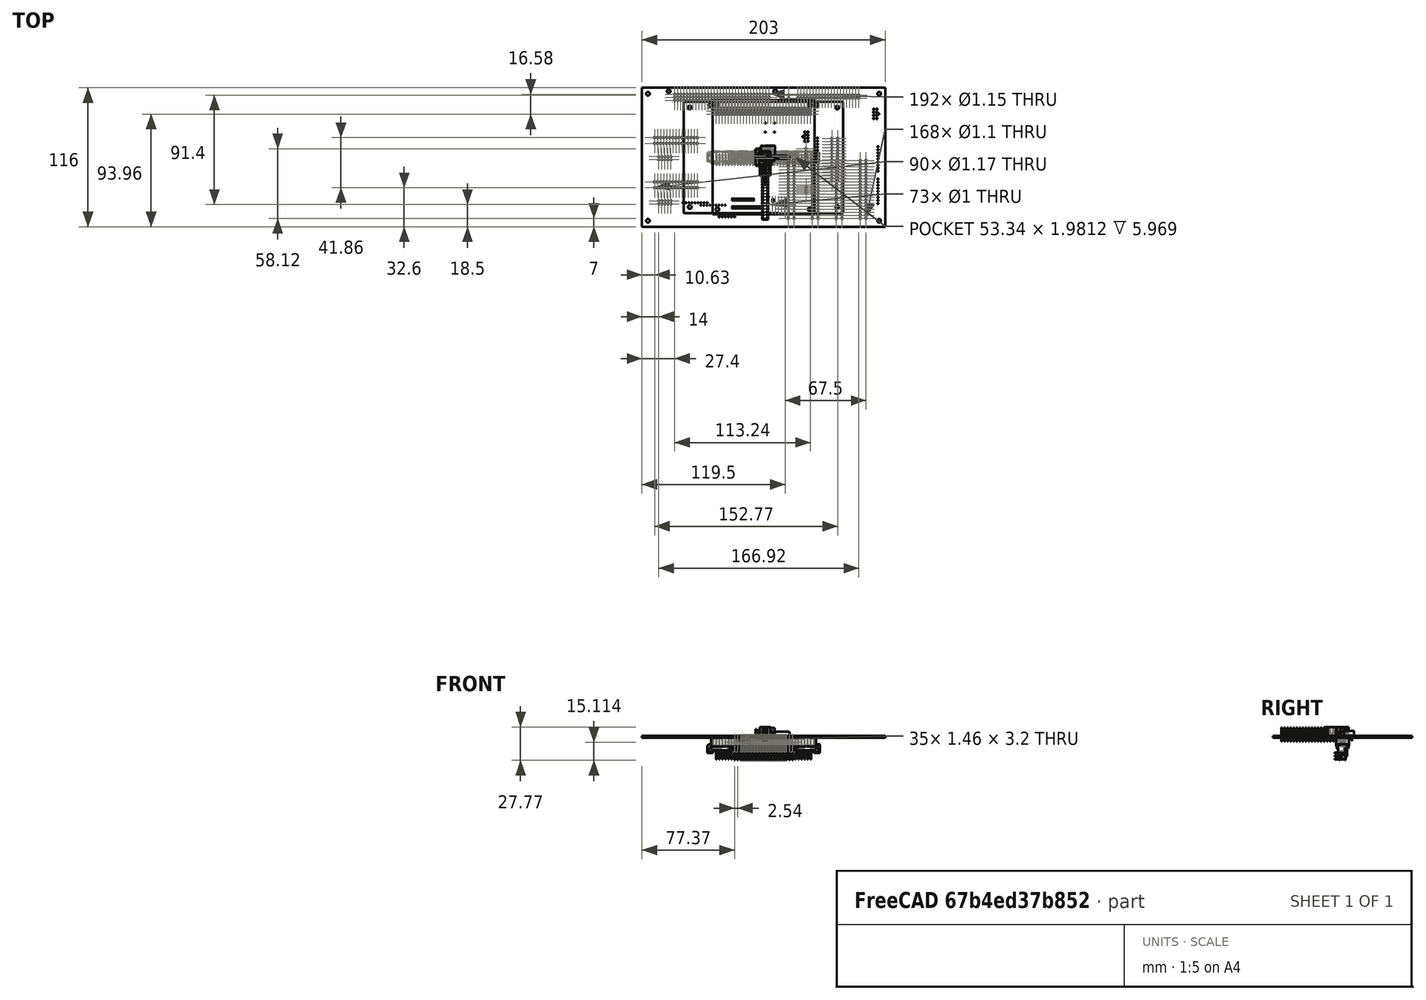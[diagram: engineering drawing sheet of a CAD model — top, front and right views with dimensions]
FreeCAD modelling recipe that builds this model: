
FCSTD DOCUMENT  (FreeCAD 2022.1112R26244 +5306 (Git))
Label: GComputerCaseAssembly
License: All rights reserved
objects: App::Link×216, App::FeaturePython×89, Part::FeaturePython×61, Part::Feature×46, App::LinkGroup×46, PartDesign::CoordinateSystem×1
note: 107 computed .brp shape members not serialized (recipe doc carries the construction recipe); baked Part::Feature solids carry a one-line shape summary decoded from their .brp
EXTERNAL_REF file=FirstPartPeripherals.FCStd obj=Part
EXTERNAL_REF file=SecondPartPeripherals.FCStd obj=Part
EXTERNAL_REF file=FirstPartProcessor.FCStd obj=Part
EXTERNAL_REF file=SecondPartProcessor.FCStd obj=Part
EXTERNAL_REF file=FirstPartPeripheralsTop.FCStd obj=Part
EXTERNAL_REF file=SecondPartPeripheralsTop.FCStd obj=Part
EXTERNAL_REF file=SecondPartProcessorTop.FCStd obj=Part
EXTERNAL_REF file=FirstPartProcessorTop.FCStd obj=Part

FEATURE [PartDesign::CoordinateSystem] Local_CS
  AttacherType = Attacher::AttachEngine3D
  TreeRank = 1
FEATURE [App::Link] Link  label="FirstPartPeripherals"
  AutoLinkLabel = false
  AutoPlacement = true
  LinkPlacement = pos=(65.4549,-31.7473,55.1601) rot=(0,0,1;0rad)
  LinkedObject = -> <external FirstPartPeripherals.FCStd>#Part
  Placement = pos=(65.4549,-31.7473,55.1601) rot=(0,0,1;0rad)
  SyncGroupVisibility = false
  TreeRank = 2
  _LinkOwner = 312
  _LinkVersion = 1
FEATURE [App::Link] Link001  label="SecondPartPeripherals"
  AutoLinkLabel = false
  AutoPlacement = true
  LinkPlacement = pos=(-74.5451,-31.7473,55.1601) rot=(0,0,1;0rad)
  LinkedObject = -> <external SecondPartPeripherals.FCStd>#Part
  Placement = pos=(-74.5451,-31.7473,55.1601) rot=(0,0,1;0rad)
  SyncGroupVisibility = false
  TreeRank = 3
  _LinkOwner = 312
  _LinkVersion = 1
FEATURE [App::Link] Link002  label="FirstPartProcessor"
  AutoLinkLabel = false
  AutoPlacement = true
  LinkPlacement = pos=(65.4549,91.6527,55.1601) rot=(0,0,1;0rad)
  LinkedObject = -> <external FirstPartProcessor.FCStd>#Part
  Placement = pos=(65.4549,91.6527,55.1601) rot=(0,0,1;0rad)
  SyncGroupVisibility = false
  TreeRank = 24
  _LinkOwner = 312
  _LinkVersion = 1
FEATURE [App::Link] Link003  label="SecondPartProcessor"
  AutoLinkLabel = false
  AutoPlacement = true
  LinkPlacement = pos=(-74.5451,91.6527,55.1601) rot=(0,0,1;0rad)
  LinkedObject = -> <external SecondPartProcessor.FCStd>#Part
  Placement = pos=(-74.5451,91.6527,55.1601) rot=(0,0,1;0rad)
  SyncGroupVisibility = false
  TreeRank = 39
  _LinkOwner = 312
  _LinkVersion = 1
FEATURE [Part::Feature] Solid  label="SOLID"
  TreeRank = 58
  shape: bbox 44.7 x 9.347 x 18.67 mm, 388 faces (baked)
FEATURE [App::LinkGroup] LinkGroup  label="5530843-2"
  ElementList = -> [Solid]
  LinkMode = 0
  Placement = pos=(59.5,-2.1,17.15) rot=(0,0,1;1.5708rad)
  TreeRank = 59
  _LinkVersion = 1
FEATURE [Part::Feature] Solid001  label="SOLID001"
  TreeRank = 60
  shape: bbox 93.85 x 12.08 x 18.02 mm, 1560 faces (baked)
FEATURE [App::LinkGroup] LinkGroup001  label="5650473-5"
  ElementList = -> [Solid001]
  LinkMode = 0
  Placement = pos=(-0.25,53.75,5.65) rot=(0,0.707107,0.707107;3.14159rad)
  TreeRank = 61
  _LinkVersion = 1
FEATURE [Part::Feature] Solid002  label="SOLID002"
  TreeRank = 121
  shape: bbox 2 x 1.25 x 1.25 mm, 28 faces (baked)
FEATURE [App::LinkGroup] LinkGroup002  label="C_0805_2012Metric"
  ElementList = -> [Solid002]
  LinkMode = 0
  Placement = pos=(8.5,11,-0.05) rot=(0,1,0;3.14159rad)
  TreeRank = 122
  _LinkVersion = 1
FEATURE [App::Link] Link004  label="C_0805_2012Metric001"
  AutoLinkLabel = true
  AutoPlacement = true
  LinkPlacement = pos=(20.5,11,-0.05) rot=(0,1,0;3.14159rad)
  LinkedObject = -> LinkGroup002
  Placement = pos=(20.5,11,-0.05) rot=(0,1,0;3.14159rad)
  SyncGroupVisibility = false
  TreeRank = 123
  _LinkVersion = 1
FEATURE [App::Link] Link005  label="C_0805_2012Metric002"
  AutoLinkLabel = true
  AutoPlacement = true
  LinkPlacement = pos=(32.5,11,-0.05) rot=(0,1,0;3.14159rad)
  LinkedObject = -> LinkGroup002
  Placement = pos=(32.5,11,-0.05) rot=(0,1,0;3.14159rad)
  SyncGroupVisibility = false
  TreeRank = 124
  _LinkVersion = 1
FEATURE [App::Link] Link006  label="C_0805_2012Metric003"
  AutoLinkLabel = true
  AutoPlacement = true
  LinkPlacement = pos=(-45.25,9.25,-0.05) rot=(1,0,0;3.14159rad)
  LinkedObject = -> LinkGroup002
  Placement = pos=(-45.25,9.25,-0.05) rot=(1,0,0;3.14159rad)
  SyncGroupVisibility = false
  TreeRank = 125
  _LinkVersion = 1
FEATURE [App::Link] Link007  label="C_0805_2012Metric004"
  AutoLinkLabel = true
  AutoPlacement = true
  LinkPlacement = pos=(-32.75,-4,-0.05) rot=(0,1,0;3.14159rad)
  LinkedObject = -> LinkGroup002
  Placement = pos=(-32.75,-4,-0.05) rot=(0,1,0;3.14159rad)
  SyncGroupVisibility = false
  TreeRank = 126
  _LinkVersion = 1
FEATURE [App::Link] Link008  label="C_0805_2012Metric005"
  AutoLinkLabel = true
  AutoPlacement = true
  LinkPlacement = pos=(-21.25,-4,-0.05) rot=(0,1,0;3.14159rad)
  LinkedObject = -> LinkGroup002
  Placement = pos=(-21.25,-4,-0.05) rot=(0,1,0;3.14159rad)
  SyncGroupVisibility = false
  TreeRank = 127
  _LinkVersion = 1
FEATURE [App::Link] Link009  label="C_0805_2012Metric006"
  AutoLinkLabel = true
  AutoPlacement = true
  LinkPlacement = pos=(-2,-7.5,1.65) rot=(0,0,1;3.14159rad)
  LinkedObject = -> LinkGroup002
  Placement = pos=(-2,-7.5,1.65) rot=(0,0,1;3.14159rad)
  SyncGroupVisibility = false
  TreeRank = 128
  _LinkVersion = 1
FEATURE [App::Link] Link010  label="C_0805_2012Metric007"
  AutoLinkLabel = true
  AutoPlacement = true
  LinkPlacement = pos=(-32.75,12.25,-0.05) rot=(0,1,0;3.14159rad)
  LinkedObject = -> LinkGroup002
  Placement = pos=(-32.75,12.25,-0.05) rot=(0,1,0;3.14159rad)
  SyncGroupVisibility = false
  TreeRank = 129
  _LinkVersion = 1
FEATURE [App::Link] Link011  label="C_0805_2012Metric008"
  AutoLinkLabel = true
  AutoPlacement = true
  LinkPlacement = pos=(25.5,-17.5,1.65) rot=(0,0,1;0rad)
  LinkedObject = -> LinkGroup002
  Placement = pos=(25.5,-17.5,1.65) rot=(0,0,1;0rad)
  SyncGroupVisibility = false
  TreeRank = 130
  _LinkVersion = 1
FEATURE [App::Link] Link012  label="C_0805_2012Metric009"
  AutoLinkLabel = true
  AutoPlacement = true
  LinkPlacement = pos=(-21.25,12.25,-0.05) rot=(0,1,0;3.14159rad)
  LinkedObject = -> LinkGroup002
  Placement = pos=(-21.25,12.25,-0.05) rot=(0,1,0;3.14159rad)
  SyncGroupVisibility = false
  TreeRank = 131
  _LinkVersion = 1
FEATURE [App::Link] Link013  label="C_0805_2012Metric010"
  AutoLinkLabel = true
  AutoPlacement = true
  LinkPlacement = pos=(-10,13.5,-0.05) rot=(0,1,0;3.14159rad)
  LinkedObject = -> LinkGroup002
  Placement = pos=(-10,13.5,-0.05) rot=(0,1,0;3.14159rad)
  SyncGroupVisibility = false
  TreeRank = 132
  _LinkVersion = 1
FEATURE [App::Link] Link014  label="C_0805_2012Metric011"
  AutoLinkLabel = true
  AutoPlacement = true
  LinkPlacement = pos=(-44.25,4.5,-0.05) rot=(-0.707107,0.707107,0;3.14159rad)
  LinkedObject = -> LinkGroup002
  Placement = pos=(-44.25,4.5,-0.05) rot=(-0.707107,0.707107,0;3.14159rad)
  SyncGroupVisibility = false
  TreeRank = 133
  _LinkVersion = 1
FEATURE [App::Link] Link015  label="C_0805_2012Metric012"
  AutoLinkLabel = true
  AutoPlacement = true
  LinkPlacement = pos=(-10,-3,-0.05) rot=(0,1,0;3.14159rad)
  LinkedObject = -> LinkGroup002
  Placement = pos=(-10,-3,-0.05) rot=(0,1,0;3.14159rad)
  SyncGroupVisibility = false
  TreeRank = 134
  _LinkVersion = 1
FEATURE [App::Link] Link016  label="C_0805_2012Metric013"
  AutoLinkLabel = true
  AutoPlacement = true
  LinkPlacement = pos=(-10.75,-13.5,-0.05) rot=(1,0,0;3.14159rad)
  LinkedObject = -> LinkGroup002
  Placement = pos=(-10.75,-13.5,-0.05) rot=(1,0,0;3.14159rad)
  SyncGroupVisibility = false
  TreeRank = 135
  _LinkVersion = 1
FEATURE [App::Link] Link017  label="C_0805_2012Metric014"
  AutoLinkLabel = true
  AutoPlacement = true
  LinkPlacement = pos=(-49,-12.25,1.65) rot=(0,0,1;3.14159rad)
  LinkedObject = -> LinkGroup002
  Placement = pos=(-49,-12.25,1.65) rot=(0,0,1;3.14159rad)
  SyncGroupVisibility = false
  TreeRank = 136
  _LinkVersion = 1
FEATURE [App::Link] Link018  label="C_0805_2012Metric015"
  AutoLinkLabel = true
  AutoPlacement = true
  LinkPlacement = pos=(-19,-27.75,-0.05) rot=(0,1,0;3.14159rad)
  LinkedObject = -> LinkGroup002
  Placement = pos=(-19,-27.75,-0.05) rot=(0,1,0;3.14159rad)
  SyncGroupVisibility = false
  TreeRank = 137
  _LinkVersion = 1
FEATURE [App::Link] Link019  label="C_0805_2012Metric016"
  AutoLinkLabel = true
  AutoPlacement = true
  LinkPlacement = pos=(-39.25,-27.75,-0.05) rot=(0,1,0;3.14159rad)
  LinkedObject = -> LinkGroup002
  Placement = pos=(-39.25,-27.75,-0.05) rot=(0,1,0;3.14159rad)
  SyncGroupVisibility = false
  TreeRank = 138
  _LinkVersion = 1
FEATURE [App::Link] Link020  label="C_0805_2012Metric017"
  AutoLinkLabel = true
  AutoPlacement = true
  LinkPlacement = pos=(-9,-12.25,1.65) rot=(0,0,1;3.14159rad)
  LinkedObject = -> LinkGroup002
  Placement = pos=(-9,-12.25,1.65) rot=(0,0,1;3.14159rad)
  SyncGroupVisibility = false
  TreeRank = 139
  _LinkVersion = 1
FEATURE [App::Link] Link021  label="C_0805_2012Metric018"
  AutoLinkLabel = true
  AutoPlacement = true
  LinkPlacement = pos=(-29,-12.25,1.65) rot=(0,0,1;3.14159rad)
  LinkedObject = -> LinkGroup002
  Placement = pos=(-29,-12.25,1.65) rot=(0,0,1;3.14159rad)
  SyncGroupVisibility = false
  TreeRank = 140
  _LinkVersion = 1
FEATURE [App::Link] Link022  label="C_0805_2012Metric019"
  AutoLinkLabel = true
  AutoPlacement = true
  LinkPlacement = pos=(11.5,2,1.65) rot=(0,0,1;1.5708rad)
  LinkedObject = -> LinkGroup002
  Placement = pos=(11.5,2,1.65) rot=(0,0,1;1.5708rad)
  SyncGroupVisibility = false
  TreeRank = 141
  _LinkVersion = 1
FEATURE [App::Link] Link023  label="C_0805_2012Metric020"
  AutoLinkLabel = true
  AutoPlacement = true
  LinkPlacement = pos=(-10.5,10,1.65) rot=(0,0,1;0rad)
  LinkedObject = -> LinkGroup002
  Placement = pos=(-10.5,10,1.65) rot=(0,0,1;0rad)
  SyncGroupVisibility = false
  TreeRank = 142
  _LinkVersion = 1
FEATURE [App::Link] Link024  label="C_0805_2012Metric021"
  AutoLinkLabel = true
  AutoPlacement = true
  LinkPlacement = pos=(-30.5,10,1.65) rot=(0,0,1;0rad)
  LinkedObject = -> LinkGroup002
  Placement = pos=(-30.5,10,1.65) rot=(0,0,1;0rad)
  SyncGroupVisibility = false
  TreeRank = 143
  _LinkVersion = 1
FEATURE [App::Link] Link025  label="C_0805_2012Metric022"
  AutoLinkLabel = true
  AutoPlacement = true
  LinkPlacement = pos=(-50.5,10,1.65) rot=(0,0,1;0rad)
  LinkedObject = -> LinkGroup002
  Placement = pos=(-50.5,10,1.65) rot=(0,0,1;0rad)
  SyncGroupVisibility = false
  TreeRank = 144
  _LinkVersion = 1
FEATURE [App::Link] Link026  label="C_0805_2012Metric023"
  AutoLinkLabel = true
  AutoPlacement = true
  LinkPlacement = pos=(25.5,-14.5,1.65) rot=(0,0,1;0rad)
  LinkedObject = -> LinkGroup002
  Placement = pos=(25.5,-14.5,1.65) rot=(0,0,1;0rad)
  SyncGroupVisibility = false
  TreeRank = 145
  _LinkVersion = 1
FEATURE [App::Link] Link027  label="C_0805_2012Metric024"
  AutoLinkLabel = true
  AutoPlacement = true
  LinkPlacement = pos=(-10.5,30,1.65) rot=(0,0,1;0rad)
  LinkedObject = -> LinkGroup002
  Placement = pos=(-10.5,30,1.65) rot=(0,0,1;0rad)
  SyncGroupVisibility = false
  TreeRank = 146
  _LinkVersion = 1
FEATURE [App::Link] Link028  label="C_0805_2012Metric025"
  AutoLinkLabel = true
  AutoPlacement = true
  LinkPlacement = pos=(6.5,2,1.65) rot=(0,0,1;1.5708rad)
  LinkedObject = -> LinkGroup002
  Placement = pos=(6.5,2,1.65) rot=(0,0,1;1.5708rad)
  SyncGroupVisibility = false
  TreeRank = 147
  _LinkVersion = 1
FEATURE [App::Link] Link029  label="C_0805_2012Metric026"
  AutoLinkLabel = true
  AutoPlacement = true
  LinkPlacement = pos=(-50.5,30,1.65) rot=(0,0,1;0rad)
  LinkedObject = -> LinkGroup002
  Placement = pos=(-50.5,30,1.65) rot=(0,0,1;0rad)
  SyncGroupVisibility = false
  TreeRank = 148
  _LinkVersion = 1
FEATURE [App::Link] Link030  label="C_0805_2012Metric027"
  AutoLinkLabel = true
  AutoPlacement = true
  LinkPlacement = pos=(5.5,-25,1.65) rot=(0,0,-1;1.5708rad)
  LinkedObject = -> LinkGroup002
  Placement = pos=(5.5,-25,1.65) rot=(0,0,-1;1.5708rad)
  SyncGroupVisibility = false
  TreeRank = 149
  _LinkVersion = 1
FEATURE [App::Link] Link031  label="C_0805_2012Metric028"
  AutoLinkLabel = true
  AutoPlacement = true
  LinkPlacement = pos=(-30.5,30,1.65) rot=(0,0,1;0rad)
  LinkedObject = -> LinkGroup002
  Placement = pos=(-30.5,30,1.65) rot=(0,0,1;0rad)
  SyncGroupVisibility = false
  TreeRank = 150
  _LinkVersion = 1
FEATURE [App::Link] Link032  label="C_0805_2012Metric029"
  AutoLinkLabel = true
  AutoPlacement = true
  LinkPlacement = pos=(34.25,32,-0.05) rot=(-0.707107,0.707107,0;3.14159rad)
  LinkedObject = -> LinkGroup002
  Placement = pos=(34.25,32,-0.05) rot=(-0.707107,0.707107,0;3.14159rad)
  SyncGroupVisibility = false
  TreeRank = 151
  _LinkVersion = 1
FEATURE [App::Link] Link033  label="C_0805_2012Metric030"
  AutoLinkLabel = true
  AutoPlacement = true
  LinkPlacement = pos=(36.5,32,-0.05) rot=(-0.707107,0.707107,0;3.14159rad)
  LinkedObject = -> LinkGroup002
  Placement = pos=(36.5,32,-0.05) rot=(-0.707107,0.707107,0;3.14159rad)
  SyncGroupVisibility = false
  TreeRank = 152
  _LinkVersion = 1
FEATURE [App::Link] Link034  label="C_0805_2012Metric031"
  AutoLinkLabel = true
  AutoPlacement = true
  LinkPlacement = pos=(11.5,-25,1.65) rot=(0,0,-1;1.5708rad)
  LinkedObject = -> LinkGroup002
  Placement = pos=(11.5,-25,1.65) rot=(0,0,-1;1.5708rad)
  SyncGroupVisibility = false
  TreeRank = 153
  _LinkVersion = 1
FEATURE [App::Link] Link035  label="C_0805_2012Metric032"
  AutoLinkLabel = true
  AutoPlacement = true
  LinkPlacement = pos=(15,-15.5,-0.05) rot=(-0.707107,0.707107,0;3.14159rad)
  LinkedObject = -> LinkGroup002
  Placement = pos=(15,-15.5,-0.05) rot=(-0.707107,0.707107,0;3.14159rad)
  SyncGroupVisibility = false
  TreeRank = 154
  _LinkVersion = 1
FEATURE [App::Link] Link036  label="C_0805_2012Metric033"
  AutoLinkLabel = true
  AutoPlacement = true
  LinkPlacement = pos=(45.75,-25,1.65) rot=(0,0,1;1.5708rad)
  LinkedObject = -> LinkGroup002
  Placement = pos=(45.75,-25,1.65) rot=(0,0,1;1.5708rad)
  SyncGroupVisibility = false
  TreeRank = 155
  _LinkVersion = 1
FEATURE [App::Link] Link037  label="C_0805_2012Metric034"
  AutoLinkLabel = true
  AutoPlacement = true
  LinkPlacement = pos=(42.25,-25,-0.05) rot=(0.707107,0.707107,0;3.14159rad)
  LinkedObject = -> LinkGroup002
  Placement = pos=(42.25,-25,-0.05) rot=(0.707107,0.707107,0;3.14159rad)
  SyncGroupVisibility = false
  TreeRank = 156
  _LinkVersion = 1
FEATURE [App::Link] Link038  label="C_0805_2012Metric035"
  AutoLinkLabel = true
  AutoPlacement = true
  LinkPlacement = pos=(62,19.5,-0.05) rot=(0.707107,0.707107,0;3.14159rad)
  LinkedObject = -> LinkGroup002
  Placement = pos=(62,19.5,-0.05) rot=(0.707107,0.707107,0;3.14159rad)
  SyncGroupVisibility = false
  TreeRank = 157
  _LinkVersion = 1
FEATURE [App::Link] Link039  label="C_0805_2012Metric036"
  AutoLinkLabel = true
  AutoPlacement = true
  LinkPlacement = pos=(26.75,-25,1.65) rot=(0,0,-1;1.5708rad)
  LinkedObject = -> LinkGroup002
  Placement = pos=(26.75,-25,1.65) rot=(0,0,-1;1.5708rad)
  SyncGroupVisibility = false
  TreeRank = 158
  _LinkVersion = 1
FEATURE [App::Link] Link040  label="C_0805_2012Metric037"
  AutoLinkLabel = true
  AutoPlacement = true
  LinkPlacement = pos=(57,19.5,-0.05) rot=(0.707107,0.707107,0;3.14159rad)
  LinkedObject = -> LinkGroup002
  Placement = pos=(57,19.5,-0.05) rot=(0.707107,0.707107,0;3.14159rad)
  SyncGroupVisibility = false
  TreeRank = 159
  _LinkVersion = 1
FEATURE [App::Link] Link041  label="C_0805_2012Metric038"
  AutoLinkLabel = true
  AutoPlacement = true
  LinkPlacement = pos=(-2,-15,1.65) rot=(0,0,1;3.14159rad)
  LinkedObject = -> LinkGroup002
  Placement = pos=(-2,-15,1.65) rot=(0,0,1;3.14159rad)
  SyncGroupVisibility = false
  TreeRank = 160
  _LinkVersion = 1
FEATURE [App::Link] Link042  label="C_0805_2012Metric039"
  AutoLinkLabel = true
  AutoPlacement = true
  LinkPlacement = pos=(8,-14.5,-0.05) rot=(-0.707107,0.707107,0;3.14159rad)
  LinkedObject = -> LinkGroup002
  Placement = pos=(8,-14.5,-0.05) rot=(-0.707107,0.707107,0;3.14159rad)
  SyncGroupVisibility = false
  TreeRank = 161
  _LinkVersion = 1
FEATURE [App::Link] Link043  label="C_0805_2012Metric040"
  AutoLinkLabel = true
  AutoPlacement = true
  LinkPlacement = pos=(10.25,26.75,1.65) rot=(0,0,1;3.14159rad)
  LinkedObject = -> LinkGroup002
  Placement = pos=(10.25,26.75,1.65) rot=(0,0,1;3.14159rad)
  SyncGroupVisibility = false
  TreeRank = 162
  _LinkVersion = 1
FEATURE [App::Link] Link044  label="C_0805_2012Metric041"
  AutoLinkLabel = true
  AutoPlacement = true
  LinkPlacement = pos=(33.5,23.75,1.65) rot=(0,0,1;3.14159rad)
  LinkedObject = -> LinkGroup002
  Placement = pos=(33.5,23.75,1.65) rot=(0,0,1;3.14159rad)
  SyncGroupVisibility = false
  TreeRank = 163
  _LinkVersion = 1
FEATURE [App::Link] Link045  label="C_0805_2012Metric042"
  AutoLinkLabel = true
  AutoPlacement = true
  LinkPlacement = pos=(21.5,23.75,1.65) rot=(0,0,1;3.14159rad)
  LinkedObject = -> LinkGroup002
  Placement = pos=(21.5,23.75,1.65) rot=(0,0,1;3.14159rad)
  SyncGroupVisibility = false
  TreeRank = 164
  _LinkVersion = 1
FEATURE [Part::Feature] Solid003  label="SOLID003"
  TreeRank = 165
  shape: bbox 3.2 x 1.6 x 1.1 mm, 50 faces (baked)
FEATURE [App::LinkGroup] LinkGroup003  label="LED_1206_3216Metric"
  ElementList = -> [Solid003]
  LinkMode = 0
  Placement = pos=(55.75,34.5,1.65) rot=(0,0,-1;1.5708rad)
  TreeRank = 166
  _LinkVersion = 1
FEATURE [App::Link] Link046  label="LED_1206_3216Metric001"
  AutoLinkLabel = true
  AutoPlacement = true
  LinkPlacement = pos=(51.5,34.5,1.65) rot=(0,0,-1;1.5708rad)
  LinkedObject = -> LinkGroup003
  Placement = pos=(51.5,34.5,1.65) rot=(0,0,-1;1.5708rad)
  SyncGroupVisibility = false
  TreeRank = 167
  _LinkVersion = 1
FEATURE [Part::Feature] Solid004  label="SOLID004"
  TreeRank = 168
  shape: bbox 2 x 1.2 x 0.45 mm, 26 faces (baked)
FEATURE [App::LinkGroup] LinkGroup004  label="R_0805_2012Metric"
  ElementList = -> [Solid004]
  LinkMode = 0
  Placement = pos=(-2.25,16.75,-0.05) rot=(1,0,0;3.14159rad)
  TreeRank = 169
  _LinkVersion = 1
FEATURE [App::Link] Link047  label="R_0805_2012Metric001"
  AutoLinkLabel = true
  AutoPlacement = true
  LinkPlacement = pos=(15.25,8.75,-0.05) rot=(0.707107,0.707107,0;3.14159rad)
  LinkedObject = -> LinkGroup004
  Placement = pos=(15.25,8.75,-0.05) rot=(0.707107,0.707107,0;3.14159rad)
  SyncGroupVisibility = false
  TreeRank = 170
  _LinkVersion = 1
FEATURE [App::Link] Link048  label="R_0805_2012Metric002"
  AutoLinkLabel = true
  AutoPlacement = true
  LinkPlacement = pos=(27.5,9,-0.05) rot=(0,1,0;3.14159rad)
  LinkedObject = -> LinkGroup004
  Placement = pos=(27.5,9,-0.05) rot=(0,1,0;3.14159rad)
  SyncGroupVisibility = false
  TreeRank = 171
  _LinkVersion = 1
FEATURE [App::Link] Link049  label="R_0805_2012Metric003"
  AutoLinkLabel = true
  AutoPlacement = true
  LinkPlacement = pos=(55.75,30.25,1.65) rot=(0,0,1;1.5708rad)
  LinkedObject = -> LinkGroup004
  Placement = pos=(55.75,30.25,1.65) rot=(0,0,1;1.5708rad)
  SyncGroupVisibility = false
  TreeRank = 172
  _LinkVersion = 1
FEATURE [App::Link] Link050  label="R_0805_2012Metric004"
  AutoLinkLabel = true
  AutoPlacement = true
  LinkPlacement = pos=(51.5,30.25,1.65) rot=(0,0,1;1.5708rad)
  LinkedObject = -> LinkGroup004
  Placement = pos=(51.5,30.25,1.65) rot=(0,0,1;1.5708rad)
  SyncGroupVisibility = false
  TreeRank = 173
  _LinkVersion = 1
FEATURE [Part::Feature] Solid005  label="SOLID005"
  TreeRank = 174
  shape: bbox 22.86 x 2.51 x 8.3 mm, 118 faces (baked)
FEATURE [App::LinkGroup] LinkGroup005  label="R_Array_SIP9"
  ElementList = -> [Solid005]
  LinkMode = 0
  Placement = pos=(-32,-40,1.65) rot=(0,0,1;3.14159rad)
  TreeRank = 175
  _LinkVersion = 1
FEATURE [App::Link] Link051  label="R_Array_SIP010"
  AutoLinkLabel = true
  AutoPlacement = true
  LinkPlacement = pos=(45,16,1.65) rot=(0,0,-1;1.5708rad)
  LinkedObject = -> LinkGroup005
  Placement = pos=(45,16,1.65) rot=(0,0,-1;1.5708rad)
  SyncGroupVisibility = false
  TreeRank = 176
  _LinkVersion = 1
FEATURE [Part::Feature] Solid006  label="SOLID006"
  TreeRank = 177
  shape: bbox 6 x 8.7 x 1.75 mm, 246 faces (baked)
FEATURE [App::LinkGroup] LinkGroup006  label="SOIC-14_3.9x8.7mm_P1.27mm"
  ElementList = -> [Solid006]
  LinkMode = 0
  Placement = pos=(5,16.75,-0.05) rot=(1,0,0;3.14159rad)
  TreeRank = 178
  _LinkVersion = 1
FEATURE [App::Link] Link052  label="SOIC-14_3.9x8.7mm_P1.27mm001"
  AutoLinkLabel = true
  AutoPlacement = true
  LinkPlacement = pos=(17,16.75,-0.05) rot=(1,0,0;3.14159rad)
  LinkedObject = -> LinkGroup006
  Placement = pos=(17,16.75,-0.05) rot=(1,0,0;3.14159rad)
  SyncGroupVisibility = false
  TreeRank = 179
  _LinkVersion = 1
FEATURE [Part::Feature] Solid007  label="SOLID007"
  TreeRank = 187
  shape: bbox 2.8 x 2.9 x 1.55 mm, 109 faces (baked)
FEATURE [App::LinkGroup] LinkGroup007  label="SOT-23-5"
  ElementList = -> [Solid007]
  LinkMode = 0
  Placement = pos=(29,26.5,-0.05) rot=(0.707107,0.707107,0;3.14159rad)
  TreeRank = 188
  _LinkVersion = 1
FEATURE [App::Link] Link053  label="SOT-23-006"
  AutoLinkLabel = true
  AutoPlacement = true
  LinkPlacement = pos=(17,26.5,-0.05) rot=(0.707107,0.707107,0;3.14159rad)
  LinkedObject = -> LinkGroup007
  Placement = pos=(17,26.5,-0.05) rot=(0.707107,0.707107,0;3.14159rad)
  SyncGroupVisibility = false
  TreeRank = 189
  _LinkVersion = 1
FEATURE [App::Link] Link054  label="SOIC-14_3.9x8.7mm_P1.27mm002"
  AutoLinkLabel = true
  AutoPlacement = true
  LinkPlacement = pos=(29,16.75,-0.05) rot=(1,0,0;3.14159rad)
  LinkedObject = -> LinkGroup006
  Placement = pos=(29,16.75,-0.05) rot=(1,0,0;3.14159rad)
  SyncGroupVisibility = false
  TreeRank = 190
  _LinkVersion = 1
FEATURE [Part::Feature] Solid008  label="SOLID008"
  TreeRank = 191
  shape: bbox 10.3 x 12.8 x 2.75 mm, 336 faces (baked)
FEATURE [App::LinkGroup] LinkGroup008  label="SOIC-20W_7.5x12.8mm_P1.27mm"
  ElementList = -> [Solid008]
  LinkMode = 0
  Placement = pos=(4.5,19,1.65) rot=(0,0,1;0rad)
  TreeRank = 192
  _LinkVersion = 1
FEATURE [App::Link] Link055  label="SOIC-20W_7.5x12.8mm_P1.27mm001"
  AutoLinkLabel = true
  AutoPlacement = true
  LinkPlacement = pos=(-50.75,17,-0.05) rot=(1,0,0;3.14159rad)
  LinkedObject = -> LinkGroup008
  Placement = pos=(-50.75,17,-0.05) rot=(1,0,0;3.14159rad)
  SyncGroupVisibility = false
  TreeRank = 193
  _LinkVersion = 1
FEATURE [Part::Feature] Solid009  label="SOLID009"
  TreeRank = 226
  shape: bbox 6 x 9.9 x 1.75 mm, 276 faces (baked)
FEATURE [App::LinkGroup] LinkGroup009  label="SOIC-16_3.9x9.9mm_P1.27mm"
  ElementList = -> [Solid009]
  LinkMode = 0
  Placement = pos=(-24.75,2.25,-0.05) rot=(1,0,0;3.14159rad)
  TreeRank = 227
  _LinkVersion = 1
FEATURE [App::Link] Link056  label="SOIC-16_3.9x9.9mm_P1.27mm001"
  AutoLinkLabel = true
  AutoPlacement = true
  LinkPlacement = pos=(-36.25,2.25,-0.05) rot=(1,0,0;3.14159rad)
  LinkedObject = -> LinkGroup009
  Placement = pos=(-36.25,2.25,-0.05) rot=(1,0,0;3.14159rad)
  SyncGroupVisibility = false
  TreeRank = 228
  _LinkVersion = 1
FEATURE [App::Link] Link057  label="SOT-23-007"
  AutoLinkLabel = true
  AutoPlacement = true
  LinkPlacement = pos=(-25,28.5,-0.05) rot=(0.707107,0.707107,0;3.14159rad)
  LinkedObject = -> LinkGroup007
  Placement = pos=(-25,28.5,-0.05) rot=(0.707107,0.707107,0;3.14159rad)
  SyncGroupVisibility = false
  TreeRank = 229
  _LinkVersion = 1
FEATURE [App::Link] Link058  label="SOIC-16_3.9x9.9mm_P1.27mm002"
  AutoLinkLabel = true
  AutoPlacement = true
  LinkPlacement = pos=(-24.75,18.5,-0.05) rot=(1,0,0;3.14159rad)
  LinkedObject = -> LinkGroup009
  Placement = pos=(-24.75,18.5,-0.05) rot=(1,0,0;3.14159rad)
  SyncGroupVisibility = false
  TreeRank = 230
  _LinkVersion = 1
FEATURE [App::Link] Link059  label="SOT-23-008"
  AutoLinkLabel = true
  AutoPlacement = true
  LinkPlacement = pos=(-13.5,28.5,-0.05) rot=(0.707107,0.707107,0;3.14159rad)
  LinkedObject = -> LinkGroup007
  Placement = pos=(-13.5,28.5,-0.05) rot=(0.707107,0.707107,0;3.14159rad)
  SyncGroupVisibility = false
  TreeRank = 231
  _LinkVersion = 1
FEATURE [App::Link] Link060  label="SOIC-16_3.9x9.9mm_P1.27mm003"
  AutoLinkLabel = true
  AutoPlacement = true
  LinkPlacement = pos=(-36.25,18.5,-0.05) rot=(1,0,0;3.14159rad)
  LinkedObject = -> LinkGroup009
  Placement = pos=(-36.25,18.5,-0.05) rot=(1,0,0;3.14159rad)
  SyncGroupVisibility = false
  TreeRank = 232
  _LinkVersion = 1
FEATURE [App::Link] Link061  label="SOIC-14_3.9x8.7mm_P1.27mm003"
  AutoLinkLabel = true
  AutoPlacement = true
  LinkPlacement = pos=(-13.5,19.25,-0.05) rot=(1,0,0;3.14159rad)
  LinkedObject = -> LinkGroup006
  Placement = pos=(-13.5,19.25,-0.05) rot=(1,0,0;3.14159rad)
  SyncGroupVisibility = false
  TreeRank = 233
  _LinkVersion = 1
FEATURE [App::Link] Link062  label="SOIC-16_3.9x9.9mm_P1.27mm004"
  AutoLinkLabel = true
  AutoPlacement = true
  LinkPlacement = pos=(-50.5,1,-0.05) rot=(0.707107,0.707107,0;3.14159rad)
  LinkedObject = -> LinkGroup009
  Placement = pos=(-50.5,1,-0.05) rot=(0.707107,0.707107,0;3.14159rad)
  SyncGroupVisibility = false
  TreeRank = 234
  _LinkVersion = 1
FEATURE [App::Link] Link063  label="SOIC-14_3.9x8.7mm_P1.27mm004"
  AutoLinkLabel = true
  AutoPlacement = true
  LinkPlacement = pos=(-13.5,2.75,-0.05) rot=(1,0,0;3.14159rad)
  LinkedObject = -> LinkGroup006
  Placement = pos=(-13.5,2.75,-0.05) rot=(1,0,0;3.14159rad)
  SyncGroupVisibility = false
  TreeRank = 235
  _LinkVersion = 1
FEATURE [Part::Feature] Solid010  label="SOLID010"
  TreeRank = 236
  shape: bbox 7.1 x 10.2 x 1.6 mm, 276 faces (baked)
FEATURE [App::LinkGroup] LinkGroup010  label="SOIC-16W_5.3x10.2mm_P1.27mm"
  ElementList = -> [Solid010]
  LinkMode = 0
  Placement = pos=(-6.25,-20,-0.05) rot=(0,1,0;3.14159rad)
  TreeRank = 237
  _LinkVersion = 1
FEATURE [App::Link] Link064  label="SOIC-16_3.9x9.9mm_P1.27mm005"
  AutoLinkLabel = true
  AutoPlacement = true
  LinkPlacement = pos=(30,17.5,1.65) rot=(0,0,1;0rad)
  LinkedObject = -> LinkGroup009
  Placement = pos=(30,17.5,1.65) rot=(0,0,1;0rad)
  SyncGroupVisibility = false
  TreeRank = 238
  _LinkVersion = 1
FEATURE [App::Link] Link065  label="SOIC-20W_7.5x12.8mm_P1.27mm002"
  AutoLinkLabel = true
  AutoPlacement = true
  LinkPlacement = pos=(-34.5,2,1.65) rot=(0,0,1;0rad)
  LinkedObject = -> LinkGroup008
  Placement = pos=(-34.5,2,1.65) rot=(0,0,1;0rad)
  SyncGroupVisibility = false
  TreeRank = 239
  _LinkVersion = 1
FEATURE [App::Link] Link066  label="SOIC-16_3.9x9.9mm_P1.27mm006"
  AutoLinkLabel = true
  AutoPlacement = true
  LinkPlacement = pos=(18,17.5,1.65) rot=(0,0,1;0rad)
  LinkedObject = -> LinkGroup009
  Placement = pos=(18,17.5,1.65) rot=(0,0,1;0rad)
  SyncGroupVisibility = false
  TreeRank = 240
  _LinkVersion = 1
FEATURE [App::Link] Link067  label="SOIC-20W_7.5x12.8mm_P1.27mm003"
  AutoLinkLabel = true
  AutoPlacement = true
  LinkPlacement = pos=(-14.5,2,1.65) rot=(0,0,1;0rad)
  LinkedObject = -> LinkGroup008
  Placement = pos=(-14.5,2,1.65) rot=(0,0,1;0rad)
  SyncGroupVisibility = false
  TreeRank = 241
  _LinkVersion = 1
FEATURE [App::Link] Link068  label="SOIC-20W_7.5x12.8mm_P1.27mm004"
  AutoLinkLabel = true
  AutoPlacement = true
  LinkPlacement = pos=(-54.5,2,1.65) rot=(0,0,1;0rad)
  LinkedObject = -> LinkGroup008
  Placement = pos=(-54.5,2,1.65) rot=(0,0,1;0rad)
  SyncGroupVisibility = false
  TreeRank = 242
  _LinkVersion = 1
FEATURE [App::Link] Link069  label="SOIC-20W_7.5x12.8mm_P1.27mm005"
  AutoLinkLabel = true
  AutoPlacement = true
  LinkPlacement = pos=(-14.5,22,1.65) rot=(0,0,1;0rad)
  LinkedObject = -> LinkGroup008
  Placement = pos=(-14.5,22,1.65) rot=(0,0,1;0rad)
  SyncGroupVisibility = false
  TreeRank = 243
  _LinkVersion = 1
FEATURE [App::Link] Link070  label="SOIC-20W_7.5x12.8mm_P1.27mm006"
  AutoLinkLabel = true
  AutoPlacement = true
  LinkPlacement = pos=(-54.5,22,1.65) rot=(0,0,1;0rad)
  LinkedObject = -> LinkGroup008
  Placement = pos=(-54.5,22,1.65) rot=(0,0,1;0rad)
  SyncGroupVisibility = false
  TreeRank = 244
  _LinkVersion = 1
FEATURE [App::Link] Link071  label="SOIC-20W_7.5x12.8mm_P1.27mm007"
  AutoLinkLabel = true
  AutoPlacement = true
  LinkPlacement = pos=(-34.5,22,1.65) rot=(0,0,1;0rad)
  LinkedObject = -> LinkGroup008
  Placement = pos=(-34.5,22,1.65) rot=(0,0,1;0rad)
  SyncGroupVisibility = false
  TreeRank = 245
  _LinkVersion = 1
FEATURE [App::Link] Link072  label="SOIC-20W_7.5x12.8mm_P1.27mm008"
  AutoLinkLabel = true
  AutoPlacement = true
  LinkPlacement = pos=(53.5,-30.5,1.65) rot=(0,0,1;1.5708rad)
  LinkedObject = -> LinkGroup008
  Placement = pos=(53.5,-30.5,1.65) rot=(0,0,1;1.5708rad)
  SyncGroupVisibility = false
  TreeRank = 246
  _LinkVersion = 1
FEATURE [App::Link] Link073  label="SOT-23-009"
  AutoLinkLabel = true
  AutoPlacement = true
  LinkPlacement = pos=(41,-11.75,1.65) rot=(0,0,1;3.14159rad)
  LinkedObject = -> LinkGroup007
  Placement = pos=(41,-11.75,1.65) rot=(0,0,1;3.14159rad)
  SyncGroupVisibility = false
  TreeRank = 247
  _LinkVersion = 1
FEATURE [App::Link] Link074  label="SOIC-20W_7.5x12.8mm_P1.27mm009"
  AutoLinkLabel = true
  AutoPlacement = true
  LinkPlacement = pos=(34.5,-30.5,-0.05) rot=(0.707107,0.707107,0;3.14159rad)
  LinkedObject = -> LinkGroup008
  Placement = pos=(34.5,-30.5,-0.05) rot=(0.707107,0.707107,0;3.14159rad)
  SyncGroupVisibility = false
  TreeRank = 248
  _LinkVersion = 1
FEATURE [App::Link] Link075  label="SOIC-20W_7.5x12.8mm_P1.27mm010"
  AutoLinkLabel = true
  AutoPlacement = true
  LinkPlacement = pos=(34.5,-30.5,1.65) rot=(0,0,1;1.5708rad)
  LinkedObject = -> LinkGroup008
  Placement = pos=(34.5,-30.5,1.65) rot=(0,0,1;1.5708rad)
  SyncGroupVisibility = false
  TreeRank = 249
  _LinkVersion = 1
FEATURE [App::Link] Link076  label="SOT-23-010"
  AutoLinkLabel = true
  AutoPlacement = true
  LinkPlacement = pos=(41,-17.25,1.65) rot=(0,0,1;3.14159rad)
  LinkedObject = -> LinkGroup007
  Placement = pos=(41,-17.25,1.65) rot=(0,0,1;3.14159rad)
  SyncGroupVisibility = false
  TreeRank = 250
  _LinkVersion = 1
FEATURE [App::Link] Link077  label="SOIC-20W_7.5x12.8mm_P1.27mm011"
  AutoLinkLabel = true
  AutoPlacement = true
  LinkPlacement = pos=(-44.75,-20,-0.05) rot=(1,0,0;3.14159rad)
  LinkedObject = -> LinkGroup008
  Placement = pos=(-44.75,-20,-0.05) rot=(1,0,0;3.14159rad)
  SyncGroupVisibility = false
  TreeRank = 251
  _LinkVersion = 1
FEATURE [App::Link] Link078  label="SOIC-20W_7.5x12.8mm_P1.27mm012"
  AutoLinkLabel = true
  AutoPlacement = true
  LinkPlacement = pos=(-54.5,-20,1.65) rot=(0,0,1;0rad)
  LinkedObject = -> LinkGroup008
  Placement = pos=(-54.5,-20,1.65) rot=(0,0,1;0rad)
  SyncGroupVisibility = false
  TreeRank = 252
  _LinkVersion = 1
FEATURE [App::Link] Link079  label="SOIC-20W_7.5x12.8mm_P1.27mm013"
  AutoLinkLabel = true
  AutoPlacement = true
  LinkPlacement = pos=(-24.5,-20,-0.05) rot=(1,0,0;3.14159rad)
  LinkedObject = -> LinkGroup008
  Placement = pos=(-24.5,-20,-0.05) rot=(1,0,0;3.14159rad)
  SyncGroupVisibility = false
  TreeRank = 253
  _LinkVersion = 1
FEATURE [App::Link] Link080  label="SOIC-20W_7.5x12.8mm_P1.27mm014"
  AutoLinkLabel = true
  AutoPlacement = true
  LinkPlacement = pos=(-14.5,-20,1.65) rot=(0,0,1;0rad)
  LinkedObject = -> LinkGroup008
  Placement = pos=(-14.5,-20,1.65) rot=(0,0,1;0rad)
  SyncGroupVisibility = false
  TreeRank = 254
  _LinkVersion = 1
FEATURE [App::Link] Link081  label="SOIC-20W_7.5x12.8mm_P1.27mm015"
  AutoLinkLabel = true
  AutoPlacement = true
  LinkPlacement = pos=(-34.5,-20,1.65) rot=(0,0,1;0rad)
  LinkedObject = -> LinkGroup008
  Placement = pos=(-34.5,-20,1.65) rot=(0,0,1;0rad)
  SyncGroupVisibility = false
  TreeRank = 255
  _LinkVersion = 1
FEATURE [App::Link] Link082  label="C_0805_2012Metric043"
  AutoLinkLabel = true
  AutoPlacement = true
  LinkPlacement = pos=(18.5,-25.5,-0.05) rot=(0,1,0;3.14159rad)
  LinkedObject = -> LinkGroup002
  Placement = pos=(18.5,-25.5,-0.05) rot=(0,1,0;3.14159rad)
  SyncGroupVisibility = false
  TreeRank = 256
  _LinkVersion = 1
FEATURE [App::Link] Link083  label="C_0805_2012Metric044"
  AutoLinkLabel = true
  AutoPlacement = true
  LinkPlacement = pos=(19,-3.5,-0.05) rot=(0,1,0;3.14159rad)
  LinkedObject = -> LinkGroup002
  Placement = pos=(19,-3.5,-0.05) rot=(0,1,0;3.14159rad)
  SyncGroupVisibility = false
  TreeRank = 257
  _LinkVersion = 1
FEATURE [Part::Feature] Solid011  label="SOLID011"
  TreeRank = 260
  shape: bbox 16.32 x 16.32 x 1.6 mm, 1536 faces (baked)
FEATURE [App::LinkGroup] LinkGroup011  label="VQFP-100_14x14mm_P0.5mm"
  ElementList = -> [Solid011]
  LinkMode = 0
  Placement = pos=(11.5,-11.5,1.65) rot=(0,0,1;0rad)
  TreeRank = 261
  _LinkVersion = 1
FEATURE [Part::Feature] Solid012  label="SOLID012"
  TreeRank = 264
  shape: bbox 3.4 x 19.05 x 6.3 mm, 634 faces (baked)
FEATURE [App::LinkGroup] LinkGroup012  label="PinHeader_2x15_P1.27mm_Vertical"
  ElementList = -> [Solid012]
  LinkMode = 0
  Placement = pos=(-26,-36,1.65) rot=(0,0,1;1.5708rad)
  TreeRank = 265
  _LinkVersion = 1
FEATURE [Part::Feature] Solid013  label="SOLID013"
  TreeRank = 268
  shape: bbox 3.4 x 24.13 x 6.3 mm, 802 faces (baked)
FEATURE [App::LinkGroup] LinkGroup013  label="PinHeader_2x19_P1.27mm_Vertical"
  ElementList = -> [Solid013]
  LinkMode = 0
  Placement = pos=(-26,-42.5,1.65) rot=(0,0,1;1.5708rad)
  TreeRank = 269
  _LinkVersion = 1
FEATURE [Part::Feature] Solid014  label="SOLID014"
  TreeRank = 280
  shape: bbox 2.5 x 3 x 1.2 mm, 76 faces (baked)
FEATURE [App::LinkGroup] LinkGroup014  label="SOT-23"
  ElementList = -> [Solid014]
  LinkMode = 0
  Placement = pos=(11.5,-14.5,-0.05) rot=(1,0,0;3.14159rad)
  TreeRank = 281
  _LinkVersion = 1
FEATURE [Part::Feature] Solid015  label="SOLID015"
  TreeRank = 282
  shape: bbox 10.3 x 15.4 x 2.75 mm, 396 faces (baked)
FEATURE [App::LinkGroup] LinkGroup015  label="SOIC-24W_7.5x15.4mm_P1.27mm"
  ElementList = -> [Solid015]
  LinkMode = 0
  Placement = pos=(9,-3.5,-0.05) rot=(0.707107,0.707107,0;3.14159rad)
  TreeRank = 283
  _LinkVersion = 1
FEATURE [App::Link] Link084  label="SOIC-16_3.9x9.9mm_P1.27mm007"
  AutoLinkLabel = true
  AutoPlacement = true
  LinkPlacement = pos=(11,-25.5,-0.05) rot=(0.707107,0.707107,0;3.14159rad)
  LinkedObject = -> LinkGroup009
  Placement = pos=(11,-25.5,-0.05) rot=(0.707107,0.707107,0;3.14159rad)
  SyncGroupVisibility = false
  TreeRank = 284
  _LinkVersion = 1
FEATURE [App::Link] Link085  label="SOT-23-011"
  AutoLinkLabel = true
  AutoPlacement = true
  LinkPlacement = pos=(41,-11.75,-0.05) rot=(1,0,0;3.14159rad)
  LinkedObject = -> LinkGroup007
  Placement = pos=(41,-11.75,-0.05) rot=(1,0,0;3.14159rad)
  SyncGroupVisibility = false
  TreeRank = 285
  _LinkVersion = 1
FEATURE [App::Link] Link086  label="C_0805_2012Metric045"
  AutoLinkLabel = true
  AutoPlacement = true
  LinkPlacement = pos=(28,30,-0.05) rot=(1,0,0;3.14159rad)
  LinkedObject = -> LinkGroup002
  Placement = pos=(28,30,-0.05) rot=(1,0,0;3.14159rad)
  SyncGroupVisibility = false
  TreeRank = 286
  _LinkVersion = 1
FEATURE [App::Link] Link087  label="C_0805_2012Metric046"
  AutoLinkLabel = true
  AutoPlacement = true
  LinkPlacement = pos=(16,30,-0.05) rot=(1,0,0;3.14159rad)
  LinkedObject = -> LinkGroup002
  Placement = pos=(16,30,-0.05) rot=(1,0,0;3.14159rad)
  SyncGroupVisibility = false
  TreeRank = 287
  _LinkVersion = 1
FEATURE [App::Link] Link088  label="C_0805_2012Metric047"
  AutoLinkLabel = true
  AutoPlacement = true
  LinkPlacement = pos=(34.25,32,1.65) rot=(0,0,-1;1.5708rad)
  LinkedObject = -> LinkGroup002
  Placement = pos=(34.25,32,1.65) rot=(0,0,-1;1.5708rad)
  SyncGroupVisibility = false
  TreeRank = 288
  _LinkVersion = 1
FEATURE [App::Link] Link089  label="C_0805_2012Metric048"
  AutoLinkLabel = true
  AutoPlacement = true
  LinkPlacement = pos=(36.5,32,1.65) rot=(0,0,-1;1.5708rad)
  LinkedObject = -> LinkGroup002
  Placement = pos=(36.5,32,1.65) rot=(0,0,-1;1.5708rad)
  SyncGroupVisibility = false
  TreeRank = 289
  _LinkVersion = 1
FEATURE [Part::Feature] Solid016  label="SOLID016"
  TreeRank = 296
  shape: bbox 2.54 x 15.24 x 11.54 mm, 148 faces (baked)
FEATURE [App::LinkGroup] LinkGroup016  label="PinHeader_1x06_P2.54mm_Vertical"
  ElementList = -> [Solid016]
  LinkMode = 0
  Placement = pos=(7.5,-39.5,1.65) rot=(0,0,1;1.5708rad)
  TreeRank = 297
  _LinkVersion = 1
FEATURE [App::Link] Link090  label="R_0805_2012Metric005"
  AutoLinkLabel = true
  AutoPlacement = true
  LinkPlacement = pos=(7.4,24.1,-0.05) rot=(-0.707107,0.707107,0;3.14159rad)
  LinkedObject = -> LinkGroup004
  Placement = pos=(7.4,24.1,-0.05) rot=(-0.707107,0.707107,0;3.14159rad)
  SyncGroupVisibility = false
  TreeRank = 298
  _LinkVersion = 1
FEATURE [App::Link] Link091  label="R_0805_2012Metric006"
  AutoLinkLabel = true
  AutoPlacement = true
  LinkPlacement = pos=(36.6,15.5,-0.05) rot=(0,1,0;3.14159rad)
  LinkedObject = -> LinkGroup004
  Placement = pos=(36.6,15.5,-0.05) rot=(0,1,0;3.14159rad)
  SyncGroupVisibility = false
  TreeRank = 299
  _LinkVersion = 1
FEATURE [Part::Feature] Solid017  label="COMPOUND"
  TreeRank = 300
  shape: bbox 133 x 93 x 1.6 mm, 233 faces (baked)
FEATURE [App::LinkGroup] LinkGroup017  label="GP8B"
  ElementList = -> [LinkGroup,LinkGroup001,LinkGroup002,Link004,Link005,Link006,Link007,Link008,Link009,Link010,Link011,Link012,Link013,Link014,Link015,Link016,Link017,Link018,Link019,Link020,Link021,Link022,Link023,Link024,Link025,Link026,Link027,Link028,Link029,Link030,Link031,Link032,Link033,Link034,Link035,Link036,Link037,Link038,Link039,Link040,Link041,Link042,Link043,Link044,Link045,LinkGroup003,Link046,+59 more]
  LinkMode = 0
  Placement = pos=(-71.0451,138.153,72.5601) rot=(0,0,-1;3.14159rad)
  TreeRank = 301
  _LinkVersion = 1
FEATURE [Part::Feature] Solid018  label="SOLID017"
  TreeRank = 332
  shape: bbox 6 x 8.7 x 1.75 mm, 246 faces (baked)
FEATURE [App::LinkGroup] LinkGroup018  label="SOIC-14_3.9x8.7mm_P1.27mm005"
  ElementList = -> [Solid018]
  LinkMode = 0
  Placement = pos=(-34.5,17.5,1.65) rot=(0,0,1;0rad)
  TreeRank = 333
  _LinkVersion = 1
FEATURE [Part::Feature] Solid019  label="SOLID018"
  TreeRank = 334
  shape: bbox 5.08 x 53.34 x 11.54 mm, 886 faces (baked)
FEATURE [App::LinkGroup] LinkGroup019  label="PinHeader_2x21_P2.54mm_Vertical"
  ElementList = -> [Solid019]
  LinkMode = 0
  Placement = pos=(28.62,49.36,1.65) rot=(0,0,1;1.5708rad)
  TreeRank = 335
  _LinkVersion = 1
FEATURE [Part::Feature] Solid020  label="SOLID019"
  TreeRank = 340
  shape: bbox 6 x 9.9 x 1.75 mm, 276 faces (baked)
FEATURE [App::LinkGroup] LinkGroup020  label="SOIC-16_3.9x9.9mm_P1.27mm008"
  ElementList = -> [Solid020]
  LinkMode = 0
  Placement = pos=(21.83,18.65,-0.05) rot=(0,1,0;3.14159rad)
  TreeRank = 341
  _LinkVersion = 1
FEATURE [Part::Feature] Solid021  label="SOLID020"
  TreeRank = 342
  shape: bbox 93.85 x 12.08 x 18.02 mm, 1560 faces (baked)
FEATURE [App::LinkGroup] LinkGroup021  label="5650473-006"
  ElementList = -> [Solid021]
  LinkMode = 0
  Placement = pos=(-34.75,65.25,5.65) rot=(0,0.707107,0.707107;3.14159rad)
  TreeRank = 343
  _LinkVersion = 1
FEATURE [Part::Feature] Solid022  label="SOLID021"
  TreeRank = 347
  shape: bbox 44.7 x 9.347 x 18.67 mm, 388 faces (baked)
FEATURE [App::LinkGroup] LinkGroup022  label="5530843-003"
  ElementList = -> [Solid022]
  LinkMode = 0
  Placement = pos=(-73.1,-23,17.15) rot=(0,0,1;0rad)
  TreeRank = 348
  _LinkVersion = 1
FEATURE [App::Link] Link092  label="5530843-004"
  AutoLinkLabel = true
  AutoPlacement = true
  LinkPlacement = pos=(-73.1,14,17.15) rot=(0,0,1;0rad)
  LinkedObject = -> LinkGroup022
  Placement = pos=(-73.1,14,17.15) rot=(0,0,1;0rad)
  SyncGroupVisibility = false
  TreeRank = 349
  _LinkVersion = 1
FEATURE [Part::Feature] Solid023  label="SOLID022"
  TreeRank = 401
  shape: bbox 2 x 1.25 x 1.25 mm, 28 faces (baked)
FEATURE [App::LinkGroup] LinkGroup023  label="C_0805_2012Metric049"
  ElementList = -> [Solid023]
  LinkMode = 0
  Placement = pos=(-11,0,1.65) rot=(0,0,1;0rad)
  TreeRank = 402
  _LinkVersion = 1
FEATURE [App::Link] Link093  label="C_0805_2012Metric050"
  AutoLinkLabel = true
  AutoPlacement = true
  LinkPlacement = pos=(93.5,43,-0.05) rot=(0,1,0;3.14159rad)
  LinkedObject = -> LinkGroup023
  Placement = pos=(93.5,43,-0.05) rot=(0,1,0;3.14159rad)
  SyncGroupVisibility = false
  TreeRank = 403
  _LinkVersion = 1
FEATURE [App::Link] Link094  label="C_0805_2012Metric051"
  AutoLinkLabel = true
  AutoPlacement = true
  LinkPlacement = pos=(93.5,45,-0.05) rot=(0,1,0;3.14159rad)
  LinkedObject = -> LinkGroup023
  Placement = pos=(93.5,45,-0.05) rot=(0,1,0;3.14159rad)
  SyncGroupVisibility = false
  TreeRank = 404
  _LinkVersion = 1
FEATURE [App::Link] Link095  label="C_0805_2012Metric052"
  AutoLinkLabel = true
  AutoPlacement = true
  LinkPlacement = pos=(86.5,36,-0.05) rot=(0.707107,0.707107,0;3.14159rad)
  LinkedObject = -> LinkGroup023
  Placement = pos=(86.5,36,-0.05) rot=(0.707107,0.707107,0;3.14159rad)
  SyncGroupVisibility = false
  TreeRank = 405
  _LinkVersion = 1
FEATURE [App::Link] Link096  label="C_0805_2012Metric053"
  AutoLinkLabel = true
  AutoPlacement = true
  LinkPlacement = pos=(-47,38.5,1.65) rot=(0,0,1;0rad)
  LinkedObject = -> LinkGroup023
  Placement = pos=(-47,38.5,1.65) rot=(0,0,1;0rad)
  SyncGroupVisibility = false
  TreeRank = 406
  _LinkVersion = 1
FEATURE [App::Link] Link097  label="C_0805_2012Metric054"
  AutoLinkLabel = true
  AutoPlacement = true
  LinkPlacement = pos=(20.33,25.15,-0.05) rot=(0,1,0;3.14159rad)
  LinkedObject = -> LinkGroup023
  Placement = pos=(20.33,25.15,-0.05) rot=(0,1,0;3.14159rad)
  SyncGroupVisibility = false
  TreeRank = 407
  _LinkVersion = 1
FEATURE [App::Link] Link098  label="C_0805_2012Metric055"
  AutoLinkLabel = true
  AutoPlacement = true
  LinkPlacement = pos=(32.83,25.65,-0.05) rot=(1,0,0;3.14159rad)
  LinkedObject = -> LinkGroup023
  Placement = pos=(32.83,25.65,-0.05) rot=(1,0,0;3.14159rad)
  SyncGroupVisibility = false
  TreeRank = 408
  _LinkVersion = 1
FEATURE [App::Link] Link099  label="C_0805_2012Metric056"
  AutoLinkLabel = true
  AutoPlacement = true
  LinkPlacement = pos=(-71.5,44.5,-0.05) rot=(0,1,0;3.14159rad)
  LinkedObject = -> LinkGroup023
  Placement = pos=(-71.5,44.5,-0.05) rot=(0,1,0;3.14159rad)
  SyncGroupVisibility = false
  TreeRank = 409
  _LinkVersion = 1
FEATURE [App::Link] Link100  label="C_0805_2012Metric057"
  AutoLinkLabel = true
  AutoPlacement = true
  LinkPlacement = pos=(-72.5,44.5,1.65) rot=(0,0,1;3.14159rad)
  LinkedObject = -> LinkGroup023
  Placement = pos=(-72.5,44.5,1.65) rot=(0,0,1;3.14159rad)
  SyncGroupVisibility = false
  TreeRank = 410
  _LinkVersion = 1
FEATURE [App::Link] Link101  label="C_0805_2012Metric058"
  AutoLinkLabel = true
  AutoPlacement = true
  LinkPlacement = pos=(-76.5,28.5,-0.05) rot=(-0.707107,0.707107,0;3.14159rad)
  LinkedObject = -> LinkGroup023
  Placement = pos=(-76.5,28.5,-0.05) rot=(-0.707107,0.707107,0;3.14159rad)
  SyncGroupVisibility = false
  TreeRank = 411
  _LinkVersion = 1
FEATURE [App::Link] Link102  label="C_0805_2012Metric059"
  AutoLinkLabel = true
  AutoPlacement = true
  LinkPlacement = pos=(-96,28.5,-0.05) rot=(-0.707107,0.707107,0;3.14159rad)
  LinkedObject = -> LinkGroup023
  Placement = pos=(-96,28.5,-0.05) rot=(-0.707107,0.707107,0;3.14159rad)
  SyncGroupVisibility = false
  TreeRank = 412
  _LinkVersion = 1
FEATURE [App::Link] Link103  label="C_0805_2012Metric060"
  AutoLinkLabel = true
  AutoPlacement = true
  LinkPlacement = pos=(-25.5,-53,-0.05) rot=(1,0,0;3.14159rad)
  LinkedObject = -> LinkGroup023
  Placement = pos=(-25.5,-53,-0.05) rot=(1,0,0;3.14159rad)
  SyncGroupVisibility = false
  TreeRank = 413
  _LinkVersion = 1
FEATURE [App::Link] Link104  label="C_0805_2012Metric061"
  AutoLinkLabel = true
  AutoPlacement = true
  LinkPlacement = pos=(83.5,52,-0.05) rot=(0,1,0;3.14159rad)
  LinkedObject = -> LinkGroup023
  Placement = pos=(83.5,52,-0.05) rot=(0,1,0;3.14159rad)
  SyncGroupVisibility = false
  TreeRank = 414
  _LinkVersion = 1
FEATURE [App::Link] Link105  label="C_0805_2012Metric062"
  AutoLinkLabel = true
  AutoPlacement = true
  LinkPlacement = pos=(-31,37,1.65) rot=(0,0,1;3.14159rad)
  LinkedObject = -> LinkGroup023
  Placement = pos=(-31,37,1.65) rot=(0,0,1;3.14159rad)
  SyncGroupVisibility = false
  TreeRank = 415
  _LinkVersion = 1
FEATURE [App::Link] Link106  label="C_0805_2012Metric063"
  AutoLinkLabel = true
  AutoPlacement = true
  LinkPlacement = pos=(0.5,-19,-0.05) rot=(0.707107,0.707107,0;3.14159rad)
  LinkedObject = -> LinkGroup023
  Placement = pos=(0.5,-19,-0.05) rot=(0.707107,0.707107,0;3.14159rad)
  SyncGroupVisibility = false
  TreeRank = 416
  _LinkVersion = 1
FEATURE [App::Link] Link107  label="C_0805_2012Metric064"
  AutoLinkLabel = true
  AutoPlacement = true
  LinkPlacement = pos=(0.5,-32,-0.05) rot=(0.707107,0.707107,0;3.14159rad)
  LinkedObject = -> LinkGroup023
  Placement = pos=(0.5,-32,-0.05) rot=(0.707107,0.707107,0;3.14159rad)
  SyncGroupVisibility = false
  TreeRank = 417
  _LinkVersion = 1
FEATURE [App::Link] Link108  label="C_0805_2012Metric065"
  AutoLinkLabel = true
  AutoPlacement = true
  LinkPlacement = pos=(0.5,-45.562,-0.05) rot=(0.707107,0.707107,0;3.14159rad)
  LinkedObject = -> LinkGroup023
  Placement = pos=(0.5,-45.562,-0.05) rot=(0.707107,0.707107,0;3.14159rad)
  SyncGroupVisibility = false
  TreeRank = 418
  _LinkVersion = 1
FEATURE [App::Link] Link109  label="C_0805_2012Metric066"
  AutoLinkLabel = true
  AutoPlacement = true
  LinkPlacement = pos=(-16,-32,-0.05) rot=(0.707107,0.707107,0;3.14159rad)
  LinkedObject = -> LinkGroup023
  Placement = pos=(-16,-32,-0.05) rot=(0.707107,0.707107,0;3.14159rad)
  SyncGroupVisibility = false
  TreeRank = 419
  _LinkVersion = 1
FEATURE [App::Link] Link110  label="C_0805_2012Metric067"
  AutoLinkLabel = true
  AutoPlacement = true
  LinkPlacement = pos=(-16,-19,-0.05) rot=(0.707107,0.707107,0;3.14159rad)
  LinkedObject = -> LinkGroup023
  Placement = pos=(-16,-19,-0.05) rot=(0.707107,0.707107,0;3.14159rad)
  SyncGroupVisibility = false
  TreeRank = 420
  _LinkVersion = 1
FEATURE [App::Link] Link111  label="C_0805_2012Metric068"
  AutoLinkLabel = true
  AutoPlacement = true
  LinkPlacement = pos=(-16,-45.5,-0.05) rot=(0.707107,0.707107,0;3.14159rad)
  LinkedObject = -> LinkGroup023
  Placement = pos=(-16,-45.5,-0.05) rot=(0.707107,0.707107,0;3.14159rad)
  SyncGroupVisibility = false
  TreeRank = 421
  _LinkVersion = 1
FEATURE [App::Link] Link112  label="C_0805_2012Metric069"
  AutoLinkLabel = true
  AutoPlacement = true
  LinkPlacement = pos=(-54.5,-1,1.65) rot=(0,0,1;3.14159rad)
  LinkedObject = -> LinkGroup023
  Placement = pos=(-54.5,-1,1.65) rot=(0,0,1;3.14159rad)
  SyncGroupVisibility = false
  TreeRank = 422
  _LinkVersion = 1
FEATURE [App::Link] Link113  label="C_0805_2012Metric070"
  AutoLinkLabel = true
  AutoPlacement = true
  LinkPlacement = pos=(80.5,1,-0.05) rot=(0.707107,0.707107,0;3.14159rad)
  LinkedObject = -> LinkGroup023
  Placement = pos=(80.5,1,-0.05) rot=(0.707107,0.707107,0;3.14159rad)
  SyncGroupVisibility = false
  TreeRank = 423
  _LinkVersion = 1
FEATURE [App::Link] Link114  label="C_0805_2012Metric071"
  AutoLinkLabel = true
  AutoPlacement = true
  LinkPlacement = pos=(-52,12,-0.05) rot=(1,0,0;3.14159rad)
  LinkedObject = -> LinkGroup023
  Placement = pos=(-52,12,-0.05) rot=(1,0,0;3.14159rad)
  SyncGroupVisibility = false
  TreeRank = 424
  _LinkVersion = 1
FEATURE [App::Link] Link115  label="C_0805_2012Metric072"
  AutoLinkLabel = true
  AutoPlacement = true
  LinkPlacement = pos=(-52,16.5,-0.05) rot=(1,0,0;3.14159rad)
  LinkedObject = -> LinkGroup023
  Placement = pos=(-52,16.5,-0.05) rot=(1,0,0;3.14159rad)
  SyncGroupVisibility = false
  TreeRank = 425
  _LinkVersion = 1
FEATURE [App::Link] Link116  label="C_0805_2012Metric073"
  AutoLinkLabel = true
  AutoPlacement = true
  LinkPlacement = pos=(-39,27,-0.05) rot=(0,1,0;3.14159rad)
  LinkedObject = -> LinkGroup023
  Placement = pos=(-39,27,-0.05) rot=(0,1,0;3.14159rad)
  SyncGroupVisibility = false
  TreeRank = 426
  _LinkVersion = 1
FEATURE [App::Link] Link117  label="C_0805_2012Metric074"
  AutoLinkLabel = true
  AutoPlacement = true
  LinkPlacement = pos=(-23,27,-0.05) rot=(0,1,0;3.14159rad)
  LinkedObject = -> LinkGroup023
  Placement = pos=(-23,27,-0.05) rot=(0,1,0;3.14159rad)
  SyncGroupVisibility = false
  TreeRank = 427
  _LinkVersion = 1
FEATURE [App::Link] Link118  label="C_0805_2012Metric075"
  AutoLinkLabel = true
  AutoPlacement = true
  LinkPlacement = pos=(-54,-10.5,-0.05) rot=(1,0,0;3.14159rad)
  LinkedObject = -> LinkGroup023
  Placement = pos=(-54,-10.5,-0.05) rot=(1,0,0;3.14159rad)
  SyncGroupVisibility = false
  TreeRank = 428
  _LinkVersion = 1
FEATURE [App::Link] Link119  label="C_0805_2012Metric076"
  AutoLinkLabel = true
  AutoPlacement = true
  LinkPlacement = pos=(-17.5,-10.5,-0.05) rot=(1,0,0;3.14159rad)
  LinkedObject = -> LinkGroup023
  Placement = pos=(-17.5,-10.5,-0.05) rot=(1,0,0;3.14159rad)
  SyncGroupVisibility = false
  TreeRank = 429
  _LinkVersion = 1
FEATURE [App::Link] Link120  label="C_0805_2012Metric077"
  AutoLinkLabel = true
  AutoPlacement = true
  LinkPlacement = pos=(-35.5,4.5,1.65) rot=(0,0,1;0rad)
  LinkedObject = -> LinkGroup023
  Placement = pos=(-35.5,4.5,1.65) rot=(0,0,1;0rad)
  SyncGroupVisibility = false
  TreeRank = 430
  _LinkVersion = 1
FEATURE [App::Link] Link121  label="C_0805_2012Metric078"
  AutoLinkLabel = true
  AutoPlacement = true
  LinkPlacement = pos=(-52.05,-25,-0.05) rot=(1,0,0;3.14159rad)
  LinkedObject = -> LinkGroup023
  Placement = pos=(-52.05,-25,-0.05) rot=(1,0,0;3.14159rad)
  SyncGroupVisibility = false
  TreeRank = 431
  _LinkVersion = 1
FEATURE [App::Link] Link122  label="C_0805_2012Metric079"
  AutoLinkLabel = true
  AutoPlacement = true
  LinkPlacement = pos=(-51.95,-20.5,-0.05) rot=(1,0,0;3.14159rad)
  LinkedObject = -> LinkGroup023
  Placement = pos=(-51.95,-20.5,-0.05) rot=(1,0,0;3.14159rad)
  SyncGroupVisibility = false
  TreeRank = 432
  _LinkVersion = 1
FEATURE [App::Link] Link123  label="C_0805_2012Metric080"
  AutoLinkLabel = true
  AutoPlacement = true
  LinkPlacement = pos=(40.5,1,-0.05) rot=(0.707107,0.707107,0;3.14159rad)
  LinkedObject = -> LinkGroup023
  Placement = pos=(40.5,1,-0.05) rot=(0.707107,0.707107,0;3.14159rad)
  SyncGroupVisibility = false
  TreeRank = 433
  _LinkVersion = 1
FEATURE [App::Link] Link124  label="C_0805_2012Metric081"
  AutoLinkLabel = true
  AutoPlacement = true
  LinkPlacement = pos=(85.5,1,-0.05) rot=(0.707107,0.707107,0;3.14159rad)
  LinkedObject = -> LinkGroup023
  Placement = pos=(85.5,1,-0.05) rot=(0.707107,0.707107,0;3.14159rad)
  SyncGroupVisibility = false
  TreeRank = 434
  _LinkVersion = 1
FEATURE [App::Link] Link125  label="C_0805_2012Metric082"
  AutoLinkLabel = true
  AutoPlacement = true
  LinkPlacement = pos=(45.5,1,-0.05) rot=(0.707107,0.707107,0;3.14159rad)
  LinkedObject = -> LinkGroup023
  Placement = pos=(45.5,1,-0.05) rot=(0.707107,0.707107,0;3.14159rad)
  SyncGroupVisibility = false
  TreeRank = 435
  _LinkVersion = 1
FEATURE [App::Link] Link126  label="C_0805_2012Metric083"
  AutoLinkLabel = true
  AutoPlacement = true
  LinkPlacement = pos=(60.5,1,-0.05) rot=(0.707107,0.707107,0;3.14159rad)
  LinkedObject = -> LinkGroup023
  Placement = pos=(60.5,1,-0.05) rot=(0.707107,0.707107,0;3.14159rad)
  SyncGroupVisibility = false
  TreeRank = 436
  _LinkVersion = 1
FEATURE [App::Link] Link127  label="C_0805_2012Metric084"
  AutoLinkLabel = true
  AutoPlacement = true
  LinkPlacement = pos=(20.5,1,-0.05) rot=(0.707107,0.707107,0;3.14159rad)
  LinkedObject = -> LinkGroup023
  Placement = pos=(20.5,1,-0.05) rot=(0.707107,0.707107,0;3.14159rad)
  SyncGroupVisibility = false
  TreeRank = 437
  _LinkVersion = 1
FEATURE [App::Link] Link128  label="C_0805_2012Metric085"
  AutoLinkLabel = true
  AutoPlacement = true
  LinkPlacement = pos=(65.5,1,-0.05) rot=(0.707107,0.707107,0;3.14159rad)
  LinkedObject = -> LinkGroup023
  Placement = pos=(65.5,1,-0.05) rot=(0.707107,0.707107,0;3.14159rad)
  SyncGroupVisibility = false
  TreeRank = 438
  _LinkVersion = 1
FEATURE [App::Link] Link129  label="C_0805_2012Metric086"
  AutoLinkLabel = true
  AutoPlacement = true
  LinkPlacement = pos=(25.5,1,-0.05) rot=(0.707107,0.707107,0;3.14159rad)
  LinkedObject = -> LinkGroup023
  Placement = pos=(25.5,1,-0.05) rot=(0.707107,0.707107,0;3.14159rad)
  SyncGroupVisibility = false
  TreeRank = 439
  _LinkVersion = 1
FEATURE [Part::Feature] Solid024  label="SOLID023"
  TreeRank = 440
  shape: bbox 2 x 1.2 x 0.45 mm, 26 faces (baked)
FEATURE [App::LinkGroup] LinkGroup024  label="R_0805_2012Metric007"
  ElementList = -> [Solid024]
  LinkMode = 0
  Placement = pos=(7.5,0.5,1.65) rot=(0,0,-1;1.5708rad)
  TreeRank = 441
  _LinkVersion = 1
FEATURE [App::Link] Link130  label="R_0805_2012Metric008"
  AutoLinkLabel = true
  AutoPlacement = true
  LinkPlacement = pos=(7.5,-4.5,1.65) rot=(0,0,-1;1.5708rad)
  LinkedObject = -> LinkGroup024
  Placement = pos=(7.5,-4.5,1.65) rot=(0,0,-1;1.5708rad)
  SyncGroupVisibility = false
  TreeRank = 442
  _LinkVersion = 1
FEATURE [App::Link] Link131  label="R_0805_2012Metric009"
  AutoLinkLabel = true
  AutoPlacement = true
  LinkPlacement = pos=(-2,-3.5,1.65) rot=(0,0,-1;1.5708rad)
  LinkedObject = -> LinkGroup024
  Placement = pos=(-2,-3.5,1.65) rot=(0,0,-1;1.5708rad)
  SyncGroupVisibility = false
  TreeRank = 443
  _LinkVersion = 1
FEATURE [App::Link] Link132  label="R_0805_2012Metric010"
  AutoLinkLabel = true
  AutoPlacement = true
  LinkPlacement = pos=(21,45.5,-0.05) rot=(-0.707107,0.707107,0;3.14159rad)
  LinkedObject = -> LinkGroup024
  Placement = pos=(21,45.5,-0.05) rot=(-0.707107,0.707107,0;3.14159rad)
  SyncGroupVisibility = false
  TreeRank = 444
  _LinkVersion = 1
FEATURE [App::Link] Link133  label="R_0805_2012Metric011"
  AutoLinkLabel = true
  AutoPlacement = true
  LinkPlacement = pos=(-26.5,-46,-0.05) rot=(0.707107,0.707107,0;3.14159rad)
  LinkedObject = -> LinkGroup024
  Placement = pos=(-26.5,-46,-0.05) rot=(0.707107,0.707107,0;3.14159rad)
  SyncGroupVisibility = false
  TreeRank = 445
  _LinkVersion = 1
FEATURE [Part::Feature] Solid025  label="SOLID024"
  TreeRank = 446
  shape: bbox 22.86 x 2.51 x 8.3 mm, 118 faces (baked)
FEATURE [App::LinkGroup] LinkGroup025  label="R_Array_SIP011"
  ElementList = -> [Solid025]
  LinkMode = 0
  Placement = pos=(-47,-38,1.65) rot=(0,0,1;3.14159rad)
  TreeRank = 447
  _LinkVersion = 1
FEATURE [App::Link] Link134  label="R_Array_SIP012"
  AutoLinkLabel = true
  AutoPlacement = true
  LinkPlacement = pos=(95.5,-11.5,1.65) rot=(0,0,1;1.5708rad)
  LinkedObject = -> LinkGroup025
  Placement = pos=(95.5,-11.5,1.65) rot=(0,0,1;1.5708rad)
  SyncGroupVisibility = false
  TreeRank = 448
  _LinkVersion = 1
FEATURE [App::Link] Link135  label="R_Array_SIP013"
  AutoLinkLabel = true
  AutoPlacement = true
  LinkPlacement = pos=(95.5,-38.5,1.65) rot=(0,0,1;1.5708rad)
  LinkedObject = -> LinkGroup025
  Placement = pos=(95.5,-38.5,1.65) rot=(0,0,1;1.5708rad)
  SyncGroupVisibility = false
  TreeRank = 449
  _LinkVersion = 1
FEATURE [Part::Feature] Solid026  label="SOLID025"
  TreeRank = 450
  shape: bbox 2.8 x 2.9 x 1.55 mm, 109 faces (baked)
FEATURE [App::LinkGroup] LinkGroup026  label="SOT-23-012"
  ElementList = -> [Solid026]
  LinkMode = 0
  Placement = pos=(-5.5,10,-0.05) rot=(1,0,0;3.14159rad)
  TreeRank = 451
  _LinkVersion = 1
FEATURE [Part::Feature] Solid027  label="SOLID026"
  TreeRank = 455
  shape: bbox 10.3 x 12.8 x 2.75 mm, 336 faces (baked)
FEATURE [App::LinkGroup] LinkGroup027  label="SOIC-20W_7.5x12.8mm_P1.27mm016"
  ElementList = -> [Solid027]
  LinkMode = 0
  Placement = pos=(-50.5,30,1.65) rot=(0,0,1;0rad)
  TreeRank = 456
  _LinkVersion = 1
FEATURE [App::Link] Link136  label="SOT-23-013"
  AutoLinkLabel = true
  AutoPlacement = true
  LinkPlacement = pos=(4,10,-0.05) rot=(1,0,0;3.14159rad)
  LinkedObject = -> LinkGroup026
  Placement = pos=(4,10,-0.05) rot=(1,0,0;3.14159rad)
  SyncGroupVisibility = false
  TreeRank = 457
  _LinkVersion = 1
FEATURE [Part::Feature] Solid028  label="SOLID027"
  TreeRank = 485
  shape: bbox 7.1 x 10.2 x 1.6 mm, 276 faces (baked)
FEATURE [App::LinkGroup] LinkGroup028  label="SOIC-16W_5.3x10.2mm_P1.27mm001"
  ElementList = -> [Solid028]
  LinkMode = 0
  Placement = pos=(35.33,18.65,-0.05) rot=(0,1,0;3.14159rad)
  TreeRank = 486
  _LinkVersion = 1
FEATURE [App::Link] Link137  label="SOIC-20W_7.5x12.8mm_P1.27mm017"
  AutoLinkLabel = true
  AutoPlacement = true
  LinkPlacement = pos=(-68.5,32,-0.05) rot=(-0.707107,0.707107,0;3.14159rad)
  LinkedObject = -> LinkGroup027
  Placement = pos=(-68.5,32,-0.05) rot=(-0.707107,0.707107,0;3.14159rad)
  SyncGroupVisibility = false
  TreeRank = 487
  _LinkVersion = 1
FEATURE [App::Link] Link138  label="SOIC-20W_7.5x12.8mm_P1.27mm018"
  AutoLinkLabel = true
  AutoPlacement = true
  LinkPlacement = pos=(-88,32,-0.05) rot=(-0.707107,0.707107,0;3.14159rad)
  LinkedObject = -> LinkGroup027
  Placement = pos=(-88,32,-0.05) rot=(-0.707107,0.707107,0;3.14159rad)
  SyncGroupVisibility = false
  TreeRank = 488
  _LinkVersion = 1
FEATURE [App::Link] Link139  label="SOT-23-014"
  AutoLinkLabel = true
  AutoPlacement = true
  LinkPlacement = pos=(4,3,-0.05) rot=(1,0,0;3.14159rad)
  LinkedObject = -> LinkGroup026
  Placement = pos=(4,3,-0.05) rot=(1,0,0;3.14159rad)
  SyncGroupVisibility = false
  TreeRank = 489
  _LinkVersion = 1
FEATURE [App::Link] Link140  label="SOIC-20W_7.5x12.8mm_P1.27mm019"
  AutoLinkLabel = true
  AutoPlacement = true
  LinkPlacement = pos=(-35.5,18,-0.05) rot=(0,1,0;3.14159rad)
  LinkedObject = -> LinkGroup027
  Placement = pos=(-35.5,18,-0.05) rot=(0,1,0;3.14159rad)
  SyncGroupVisibility = false
  TreeRank = 490
  _LinkVersion = 1
FEATURE [App::Link] Link141  label="SOT-23-015"
  AutoLinkLabel = true
  AutoPlacement = true
  LinkPlacement = pos=(-24.5,-30.5,-0.05) rot=(1,0,0;3.14159rad)
  LinkedObject = -> LinkGroup026
  Placement = pos=(-24.5,-30.5,-0.05) rot=(1,0,0;3.14159rad)
  SyncGroupVisibility = false
  TreeRank = 491
  _LinkVersion = 1
FEATURE [App::Link] Link142  label="SOT-23-016"
  AutoLinkLabel = true
  AutoPlacement = true
  LinkPlacement = pos=(8.5,-18,1.65) rot=(0,0,-1;1.5708rad)
  LinkedObject = -> LinkGroup026
  Placement = pos=(8.5,-18,1.65) rot=(0,0,-1;1.5708rad)
  SyncGroupVisibility = false
  TreeRank = 492
  _LinkVersion = 1
FEATURE [App::Link] Link143  label="SOIC-20W_7.5x12.8mm_P1.27mm020"
  AutoLinkLabel = true
  AutoPlacement = true
  LinkPlacement = pos=(-19.5,18,-0.05) rot=(0,1,0;3.14159rad)
  LinkedObject = -> LinkGroup027
  Placement = pos=(-19.5,18,-0.05) rot=(0,1,0;3.14159rad)
  SyncGroupVisibility = false
  TreeRank = 493
  _LinkVersion = 1
FEATURE [Part::Feature] Solid029  label="SOLID028"
  TreeRank = 494
  shape: bbox 8.1 x 14 x 1.05 mm, 876 faces (baked)
FEATURE [App::LinkGroup] LinkGroup029  label="TSSOP-56_6.1x14mm_P0.5mm"
  ElementList = -> [Solid029]
  LinkMode = 0
  Placement = pos=(-54,-3,-0.05) rot=(0.707107,0.707107,0;3.14159rad)
  TreeRank = 495
  _LinkVersion = 1
FEATURE [App::Link] Link144  label="TSSOP-56_6.1x14mm_P0.5mm001"
  AutoLinkLabel = true
  AutoPlacement = true
  LinkPlacement = pos=(-17.5,-3,-0.05) rot=(0.707107,0.707107,0;3.14159rad)
  LinkedObject = -> LinkGroup029
  Placement = pos=(-17.5,-3,-0.05) rot=(0.707107,0.707107,0;3.14159rad)
  SyncGroupVisibility = false
  TreeRank = 496
  _LinkVersion = 1
FEATURE [App::Link] Link145  label="TSSOP-56_6.1x14mm_P0.5mm002"
  AutoLinkLabel = true
  AutoPlacement = true
  LinkPlacement = pos=(-35.5,-3,1.65) rot=(0,0,-1;1.5708rad)
  LinkedObject = -> LinkGroup029
  Placement = pos=(-35.5,-3,1.65) rot=(0,0,-1;1.5708rad)
  SyncGroupVisibility = false
  TreeRank = 497
  _LinkVersion = 1
FEATURE [App::Link] Link146  label="C_0805_2012Metric087"
  AutoLinkLabel = true
  AutoPlacement = true
  LinkPlacement = pos=(-31,23.5,1.65) rot=(0,0,1;3.14159rad)
  LinkedObject = -> LinkGroup023
  Placement = pos=(-31,23.5,1.65) rot=(0,0,1;3.14159rad)
  SyncGroupVisibility = false
  TreeRank = 498
  _LinkVersion = 1
FEATURE [App::Link] Link147  label="C_0805_2012Metric088"
  AutoLinkLabel = true
  AutoPlacement = true
  LinkPlacement = pos=(-18.5,38,1.65) rot=(0,0,1;3.14159rad)
  LinkedObject = -> LinkGroup023
  Placement = pos=(-18.5,38,1.65) rot=(0,0,1;3.14159rad)
  SyncGroupVisibility = false
  TreeRank = 499
  _LinkVersion = 1
FEATURE [App::Link] Link148  label="C_0805_2012Metric089"
  AutoLinkLabel = true
  AutoPlacement = true
  LinkPlacement = pos=(-18.5,23.5,1.65) rot=(0,0,1;3.14159rad)
  LinkedObject = -> LinkGroup023
  Placement = pos=(-18.5,23.5,1.65) rot=(0,0,1;3.14159rad)
  SyncGroupVisibility = false
  TreeRank = 500
  _LinkVersion = 1
FEATURE [App::Link] Link149  label="C_0805_2012Metric090"
  AutoLinkLabel = true
  AutoPlacement = true
  LinkPlacement = pos=(-6.5,31,1.65) rot=(0,0,1;3.14159rad)
  LinkedObject = -> LinkGroup023
  Placement = pos=(-6.5,31,1.65) rot=(0,0,1;3.14159rad)
  SyncGroupVisibility = false
  TreeRank = 501
  _LinkVersion = 1
FEATURE [App::Link] Link150  label="C_0805_2012Metric091"
  AutoLinkLabel = true
  AutoPlacement = true
  LinkPlacement = pos=(29,35.5,1.65) rot=(0,0,1;0rad)
  LinkedObject = -> LinkGroup023
  Placement = pos=(29,35.5,1.65) rot=(0,0,1;0rad)
  SyncGroupVisibility = false
  TreeRank = 502
  _LinkVersion = 1
FEATURE [App::Link] Link151  label="C_0805_2012Metric092"
  AutoLinkLabel = true
  AutoPlacement = true
  LinkPlacement = pos=(44.5,39.5,1.65) rot=(0,0,1;3.14159rad)
  LinkedObject = -> LinkGroup023
  Placement = pos=(44.5,39.5,1.65) rot=(0,0,1;3.14159rad)
  SyncGroupVisibility = false
  TreeRank = 503
  _LinkVersion = 1
FEATURE [App::Link] Link152  label="C_0805_2012Metric093"
  AutoLinkLabel = true
  AutoPlacement = true
  LinkPlacement = pos=(44.5,24,1.65) rot=(0,0,1;3.14159rad)
  LinkedObject = -> LinkGroup023
  Placement = pos=(44.5,24,1.65) rot=(0,0,1;3.14159rad)
  SyncGroupVisibility = false
  TreeRank = 504
  _LinkVersion = 1
FEATURE [App::Link] Link153  label="C_0805_2012Metric094"
  AutoLinkLabel = true
  AutoPlacement = true
  LinkPlacement = pos=(57.5,40.5,1.65) rot=(0,0,1;3.14159rad)
  LinkedObject = -> LinkGroup023
  Placement = pos=(57.5,40.5,1.65) rot=(0,0,1;3.14159rad)
  SyncGroupVisibility = false
  TreeRank = 505
  _LinkVersion = 1
FEATURE [App::Link] Link154  label="C_0805_2012Metric095"
  AutoLinkLabel = true
  AutoPlacement = true
  LinkPlacement = pos=(57.5,24,1.65) rot=(0,0,1;3.14159rad)
  LinkedObject = -> LinkGroup023
  Placement = pos=(57.5,24,1.65) rot=(0,0,1;3.14159rad)
  SyncGroupVisibility = false
  TreeRank = 506
  _LinkVersion = 1
FEATURE [App::Link] Link155  label="C_0805_2012Metric096"
  AutoLinkLabel = true
  AutoPlacement = true
  LinkPlacement = pos=(68.5,32,1.65) rot=(0,0,1;3.14159rad)
  LinkedObject = -> LinkGroup023
  Placement = pos=(68.5,32,1.65) rot=(0,0,1;3.14159rad)
  SyncGroupVisibility = false
  TreeRank = 507
  _LinkVersion = 1
FEATURE [App::Link] Link156  label="C_0805_2012Metric097"
  AutoLinkLabel = true
  AutoPlacement = true
  LinkPlacement = pos=(-40.5,-19.5,-0.05) rot=(0,1,0;3.14159rad)
  LinkedObject = -> LinkGroup023
  Placement = pos=(-40.5,-19.5,-0.05) rot=(0,1,0;3.14159rad)
  SyncGroupVisibility = false
  TreeRank = 508
  _LinkVersion = 1
FEATURE [App::Link] Link157  label="C_0805_2012Metric098"
  AutoLinkLabel = true
  AutoPlacement = true
  LinkPlacement = pos=(-33.5,-19.5,1.65) rot=(0,0,1;0rad)
  LinkedObject = -> LinkGroup023
  Placement = pos=(-33.5,-19.5,1.65) rot=(0,0,1;0rad)
  SyncGroupVisibility = false
  TreeRank = 509
  _LinkVersion = 1
FEATURE [App::Link] Link158  label="C_0805_2012Metric099"
  AutoLinkLabel = true
  AutoPlacement = true
  LinkPlacement = pos=(-20.5,-19.5,1.65) rot=(0,0,1;0rad)
  LinkedObject = -> LinkGroup023
  Placement = pos=(-20.5,-19.5,1.65) rot=(0,0,1;0rad)
  SyncGroupVisibility = false
  TreeRank = 510
  _LinkVersion = 1
FEATURE [App::Link] Link159  label="C_0805_2012Metric100"
  AutoLinkLabel = true
  AutoPlacement = true
  LinkPlacement = pos=(-7.5,-19.5,1.65) rot=(0,0,1;0rad)
  LinkedObject = -> LinkGroup023
  Placement = pos=(-7.5,-19.5,1.65) rot=(0,0,1;0rad)
  SyncGroupVisibility = false
  TreeRank = 511
  _LinkVersion = 1
FEATURE [Part::Feature] Solid030  label="SOLID029"
  TreeRank = 518
  shape: bbox 57.4 x 9.347 x 18.67 mm, 488 faces (baked)
FEATURE [App::LinkGroup] LinkGroup030  label="TE_5-5530843-4"
  ElementList = -> [Solid030]
  LinkMode = 0
  Placement = pos=(83,-26.85,17.15) rot=(0,0,1;1.5708rad)
  TreeRank = 519
  _LinkVersion = 1
FEATURE [App::Link] Link160  label="TE_5-5530843-005"
  AutoLinkLabel = true
  AutoPlacement = true
  LinkPlacement = pos=(43,-26.85,17.15) rot=(0,0,1;1.5708rad)
  LinkedObject = -> LinkGroup030
  Placement = pos=(43,-26.85,17.15) rot=(0,0,1;1.5708rad)
  SyncGroupVisibility = false
  TreeRank = 520
  _LinkVersion = 1
FEATURE [App::Link] Link161  label="TE_5-5530843-006"
  AutoLinkLabel = true
  AutoPlacement = true
  LinkPlacement = pos=(63,-26.85,17.15) rot=(0,0,1;1.5708rad)
  LinkedObject = -> LinkGroup030
  Placement = pos=(63,-26.85,17.15) rot=(0,0,1;1.5708rad)
  SyncGroupVisibility = false
  TreeRank = 521
  _LinkVersion = 1
FEATURE [App::Link] Link162  label="TE_5-5530843-007"
  AutoLinkLabel = true
  AutoPlacement = true
  LinkPlacement = pos=(23,-26.85,17.15) rot=(0,0,1;1.5708rad)
  LinkedObject = -> LinkGroup030
  Placement = pos=(23,-26.85,17.15) rot=(0,0,1;1.5708rad)
  SyncGroupVisibility = false
  TreeRank = 522
  _LinkVersion = 1
FEATURE [App::Link] Link163  label="R_0805_2012Metric012"
  AutoLinkLabel = true
  AutoPlacement = true
  LinkPlacement = pos=(9.5,24.5,-0.05) rot=(-0.707107,0.707107,0;3.14159rad)
  LinkedObject = -> LinkGroup024
  Placement = pos=(9.5,24.5,-0.05) rot=(-0.707107,0.707107,0;3.14159rad)
  SyncGroupVisibility = false
  TreeRank = 523
  _LinkVersion = 1
FEATURE [Part::Feature] Solid031  label="SOLID030"
  TreeRank = 528
  shape: bbox 2.5 x 3 x 1.2 mm, 76 faces (baked)
FEATURE [App::LinkGroup] LinkGroup031  label="SOT-024"
  ElementList = -> [Solid031]
  LinkMode = 0
  Placement = pos=(-11,3,1.65) rot=(0,0,1;3.14159rad)
  TreeRank = 529
  _LinkVersion = 1
FEATURE [Part::Feature] Solid032  label="SOLID031"
  TreeRank = 530
  shape: bbox 2.8 x 2.9 x 0.95 mm, 124 faces (baked)
FEATURE [App::LinkGroup] LinkGroup032  label="TSOT-23-6"
  ElementList = -> [Solid032]
  LinkMode = 0
  Placement = pos=(1.5,0,1.65) rot=(0,0,1;0rad)
  TreeRank = 531
  _LinkVersion = 1
FEATURE [Part::Feature] Solid033  label="SOLID032"
  TreeRank = 571
  shape: bbox 4 x 2.95 x 1.35 mm, 156 faces (baked)
FEATURE [App::LinkGroup] LinkGroup033  label="SSOP-8_2.95x2.8mm_P0.65mm"
  ElementList = -> [Solid033]
  LinkMode = 0
  Placement = pos=(-58,-4,1.65) rot=(0,0,1;0rad)
  TreeRank = 572
  _LinkVersion = 1
FEATURE [App::Link] Link164  label="SOIC-16_3.9x9.9mm_P1.27mm009"
  AutoLinkLabel = true
  AutoPlacement = true
  LinkPlacement = pos=(7,-15.5,-0.05) rot=(-0.707107,0.707107,0;3.14159rad)
  LinkedObject = -> LinkGroup020
  Placement = pos=(7,-15.5,-0.05) rot=(-0.707107,0.707107,0;3.14159rad)
  SyncGroupVisibility = false
  TreeRank = 573
  _LinkVersion = 1
FEATURE [App::Link] Link165  label="SOIC-16_3.9x9.9mm_P1.27mm010"
  AutoLinkLabel = true
  AutoPlacement = true
  LinkPlacement = pos=(7,-28.5,-0.05) rot=(-0.707107,0.707107,0;3.14159rad)
  LinkedObject = -> LinkGroup020
  Placement = pos=(7,-28.5,-0.05) rot=(-0.707107,0.707107,0;3.14159rad)
  SyncGroupVisibility = false
  TreeRank = 574
  _LinkVersion = 1
FEATURE [App::Link] Link166  label="SOIC-16_3.9x9.9mm_P1.27mm011"
  AutoLinkLabel = true
  AutoPlacement = true
  LinkPlacement = pos=(7,-42,-0.05) rot=(-0.707107,0.707107,0;3.14159rad)
  LinkedObject = -> LinkGroup020
  Placement = pos=(7,-42,-0.05) rot=(-0.707107,0.707107,0;3.14159rad)
  SyncGroupVisibility = false
  TreeRank = 575
  _LinkVersion = 1
FEATURE [App::Link] Link167  label="SOIC-16_3.9x9.9mm_P1.27mm012"
  AutoLinkLabel = true
  AutoPlacement = true
  LinkPlacement = pos=(-9.5,-28.5,-0.05) rot=(-0.707107,0.707107,0;3.14159rad)
  LinkedObject = -> LinkGroup020
  Placement = pos=(-9.5,-28.5,-0.05) rot=(-0.707107,0.707107,0;3.14159rad)
  SyncGroupVisibility = false
  TreeRank = 576
  _LinkVersion = 1
FEATURE [App::Link] Link168  label="SOIC-16_3.9x9.9mm_P1.27mm013"
  AutoLinkLabel = true
  AutoPlacement = true
  LinkPlacement = pos=(-9.5,-15.5,-0.05) rot=(-0.707107,0.707107,0;3.14159rad)
  LinkedObject = -> LinkGroup020
  Placement = pos=(-9.5,-15.5,-0.05) rot=(-0.707107,0.707107,0;3.14159rad)
  SyncGroupVisibility = false
  TreeRank = 577
  _LinkVersion = 1
FEATURE [App::Link] Link169  label="SOIC-16_3.9x9.9mm_P1.27mm014"
  AutoLinkLabel = true
  AutoPlacement = true
  LinkPlacement = pos=(-9.5,-42,-0.05) rot=(-0.707107,0.707107,0;3.14159rad)
  LinkedObject = -> LinkGroup020
  Placement = pos=(-9.5,-42,-0.05) rot=(-0.707107,0.707107,0;3.14159rad)
  SyncGroupVisibility = false
  TreeRank = 578
  _LinkVersion = 1
FEATURE [App::Link] Link170  label="SOT-23-017"
  AutoLinkLabel = true
  AutoPlacement = true
  LinkPlacement = pos=(-5.5,10,1.65) rot=(0,0,1;0rad)
  LinkedObject = -> LinkGroup026
  Placement = pos=(-5.5,10,1.65) rot=(0,0,1;0rad)
  SyncGroupVisibility = false
  TreeRank = 579
  _LinkVersion = 1
FEATURE [App::Link] Link171  label="SOIC-14_3.9x8.7mm_P1.27mm006"
  AutoLinkLabel = true
  AutoPlacement = true
  LinkPlacement = pos=(-34.5,31,1.65) rot=(0,0,1;0rad)
  LinkedObject = -> LinkGroup018
  Placement = pos=(-34.5,31,1.65) rot=(0,0,1;0rad)
  SyncGroupVisibility = false
  TreeRank = 580
  _LinkVersion = 1
FEATURE [App::Link] Link172  label="SOIC-16_3.9x9.9mm_P1.27mm015"
  AutoLinkLabel = true
  AutoPlacement = true
  LinkPlacement = pos=(-22,31.5,1.65) rot=(0,0,1;0rad)
  LinkedObject = -> LinkGroup020
  Placement = pos=(-22,31.5,1.65) rot=(0,0,1;0rad)
  SyncGroupVisibility = false
  TreeRank = 581
  _LinkVersion = 1
FEATURE [App::Link] Link173  label="SOIC-16_3.9x9.9mm_P1.27mm016"
  AutoLinkLabel = true
  AutoPlacement = true
  LinkPlacement = pos=(-22,17,1.65) rot=(0,0,1;0rad)
  LinkedObject = -> LinkGroup020
  Placement = pos=(-22,17,1.65) rot=(0,0,1;0rad)
  SyncGroupVisibility = false
  TreeRank = 582
  _LinkVersion = 1
FEATURE [App::Link] Link174  label="SOT-23-018"
  AutoLinkLabel = true
  AutoPlacement = true
  LinkPlacement = pos=(4,10,1.65) rot=(0,0,1;0rad)
  LinkedObject = -> LinkGroup026
  Placement = pos=(4,10,1.65) rot=(0,0,1;0rad)
  SyncGroupVisibility = false
  TreeRank = 583
  _LinkVersion = 1
FEATURE [App::Link] Link175  label="SOIC-16_3.9x9.9mm_P1.27mm017"
  AutoLinkLabel = true
  AutoPlacement = true
  LinkPlacement = pos=(-10,24.5,1.65) rot=(0,0,1;0rad)
  LinkedObject = -> LinkGroup020
  Placement = pos=(-10,24.5,1.65) rot=(0,0,1;0rad)
  SyncGroupVisibility = false
  TreeRank = 584
  _LinkVersion = 1
FEATURE [App::Link] Link176  label="SOIC-20W_7.5x12.8mm_P1.27mm021"
  AutoLinkLabel = true
  AutoPlacement = true
  LinkPlacement = pos=(25.5,27.5,1.65) rot=(0,0,1;0rad)
  LinkedObject = -> LinkGroup027
  Placement = pos=(25.5,27.5,1.65) rot=(0,0,1;0rad)
  SyncGroupVisibility = false
  TreeRank = 585
  _LinkVersion = 1
FEATURE [App::Link] Link177  label="SOIC-14_3.9x8.7mm_P1.27mm007"
  AutoLinkLabel = true
  AutoPlacement = true
  LinkPlacement = pos=(41,33.5,1.65) rot=(0,0,1;0rad)
  LinkedObject = -> LinkGroup018
  Placement = pos=(41,33.5,1.65) rot=(0,0,1;0rad)
  SyncGroupVisibility = false
  TreeRank = 586
  _LinkVersion = 1
FEATURE [App::Link] Link178  label="SOIC-14_3.9x8.7mm_P1.27mm008"
  AutoLinkLabel = true
  AutoPlacement = true
  LinkPlacement = pos=(41,18,1.65) rot=(0,0,1;0rad)
  LinkedObject = -> LinkGroup018
  Placement = pos=(41,18,1.65) rot=(0,0,1;0rad)
  SyncGroupVisibility = false
  TreeRank = 587
  _LinkVersion = 1
FEATURE [App::Link] Link179  label="SOIC-16_3.9x9.9mm_P1.27mm018"
  AutoLinkLabel = true
  AutoPlacement = true
  LinkPlacement = pos=(54,34,1.65) rot=(0,0,1;0rad)
  LinkedObject = -> LinkGroup020
  Placement = pos=(54,34,1.65) rot=(0,0,1;0rad)
  SyncGroupVisibility = false
  TreeRank = 588
  _LinkVersion = 1
FEATURE [App::Link] Link180  label="SOIC-16_3.9x9.9mm_P1.27mm019"
  AutoLinkLabel = true
  AutoPlacement = true
  LinkPlacement = pos=(54,17.5,1.65) rot=(0,0,1;0rad)
  LinkedObject = -> LinkGroup020
  Placement = pos=(54,17.5,1.65) rot=(0,0,1;0rad)
  SyncGroupVisibility = false
  TreeRank = 589
  _LinkVersion = 1
FEATURE [App::Link] Link181  label="SOIC-16_3.9x9.9mm_P1.27mm020"
  AutoLinkLabel = true
  AutoPlacement = true
  LinkPlacement = pos=(65,25.5,1.65) rot=(0,0,1;0rad)
  LinkedObject = -> LinkGroup020
  Placement = pos=(65,25.5,1.65) rot=(0,0,1;0rad)
  SyncGroupVisibility = false
  TreeRank = 590
  _LinkVersion = 1
FEATURE [App::Link] Link182  label="SOIC-20W_7.5x12.8mm_P1.27mm022"
  AutoLinkLabel = true
  AutoPlacement = true
  LinkPlacement = pos=(-36.845,-27.955,-0.05) rot=(0,1,0;3.14159rad)
  LinkedObject = -> LinkGroup027
  Placement = pos=(-36.845,-27.955,-0.05) rot=(0,1,0;3.14159rad)
  SyncGroupVisibility = false
  TreeRank = 591
  _LinkVersion = 1
FEATURE [App::Link] Link183  label="SOT-23-019"
  AutoLinkLabel = true
  AutoPlacement = true
  LinkPlacement = pos=(-24.5,-23.5,-0.05) rot=(1,0,0;3.14159rad)
  LinkedObject = -> LinkGroup026
  Placement = pos=(-24.5,-23.5,-0.05) rot=(1,0,0;3.14159rad)
  SyncGroupVisibility = false
  TreeRank = 592
  _LinkVersion = 1
FEATURE [App::Link] Link184  label="SOIC-20W_7.5x12.8mm_P1.27mm023"
  AutoLinkLabel = true
  AutoPlacement = true
  LinkPlacement = pos=(-36.785,-27.795,1.65) rot=(0,0,1;0rad)
  LinkedObject = -> LinkGroup027
  Placement = pos=(-36.785,-27.795,1.65) rot=(0,0,1;0rad)
  SyncGroupVisibility = false
  TreeRank = 593
  _LinkVersion = 1
FEATURE [App::Link] Link185  label="SOIC-20W_7.5x12.8mm_P1.27mm024"
  AutoLinkLabel = true
  AutoPlacement = true
  LinkPlacement = pos=(-23.875,-27.795,1.65) rot=(0,0,1;0rad)
  LinkedObject = -> LinkGroup027
  Placement = pos=(-23.875,-27.795,1.65) rot=(0,0,1;0rad)
  SyncGroupVisibility = false
  TreeRank = 594
  _LinkVersion = 1
FEATURE [App::Link] Link186  label="SOIC-20W_7.5x12.8mm_P1.27mm025"
  AutoLinkLabel = true
  AutoPlacement = true
  LinkPlacement = pos=(-10.965,-27.795,1.65) rot=(0,0,1;0rad)
  LinkedObject = -> LinkGroup027
  Placement = pos=(-10.965,-27.795,1.65) rot=(0,0,1;0rad)
  SyncGroupVisibility = false
  TreeRank = 595
  _LinkVersion = 1
FEATURE [Part::Feature] Solid034  label="SOLID033"
  TreeRank = 596
  shape: bbox 12.7 x 12.7 x 8.08 mm, 35 faces (baked)
FEATURE [App::LinkGroup] LinkGroup034  label="Oscillator_DIP-8"
  ElementList = -> [Solid034]
  LinkMode = 0
  Placement = pos=(1.5,21,1.65) rot=(0,0,1;0rad)
  TreeRank = 597
  _LinkVersion = 1
FEATURE [Part::Feature] Solid035  label="SOLID034"
  TreeRank = 598
  shape: bbox 9.1 x 20.36 x 12.1 mm, 222 faces (baked)
FEATURE [App::LinkGroup] LinkGroup035  label="IDC-Header_2x05_P2.54mm_Vertical"
  ElementList = -> [Solid035]
  LinkMode = 0
  Placement = pos=(-87.5,-2,1.65) rot=(0,0,1;1.5708rad)
  TreeRank = 599
  _LinkVersion = 1
FEATURE [App::Link] Link187  label="IDC-Header_2x05_P2.54mm_Vertical001"
  AutoLinkLabel = true
  AutoPlacement = true
  LinkPlacement = pos=(-87.5,-39,1.65) rot=(0,0,1;1.5708rad)
  LinkedObject = -> LinkGroup035
  Placement = pos=(-87.5,-39,1.65) rot=(0,0,1;1.5708rad)
  SyncGroupVisibility = false
  TreeRank = 600
  _LinkVersion = 1
FEATURE [App::Link] Link188  label="C_0805_2012Metric101"
  AutoLinkLabel = true
  AutoPlacement = true
  LinkPlacement = pos=(2.82,4.53,1.65) rot=(0,0,1;0rad)
  LinkedObject = -> LinkGroup023
  Placement = pos=(2.82,4.53,1.65) rot=(0,0,1;0rad)
  SyncGroupVisibility = false
  TreeRank = 601
  _LinkVersion = 1
FEATURE [App::Link] Link189  label="C_0805_2012Metric102"
  AutoLinkLabel = true
  AutoPlacement = true
  LinkPlacement = pos=(5,24.5,-0.05) rot=(1,0,0;3.14159rad)
  LinkedObject = -> LinkGroup023
  Placement = pos=(5,24.5,-0.05) rot=(1,0,0;3.14159rad)
  SyncGroupVisibility = false
  TreeRank = 602
  _LinkVersion = 1
FEATURE [App::Link] Link190  label="C_0805_2012Metric103"
  AutoLinkLabel = true
  AutoPlacement = true
  LinkPlacement = pos=(88.5,36,-0.05) rot=(0.707107,0.707107,0;3.14159rad)
  LinkedObject = -> LinkGroup023
  Placement = pos=(88.5,36,-0.05) rot=(0.707107,0.707107,0;3.14159rad)
  SyncGroupVisibility = false
  TreeRank = 603
  _LinkVersion = 1
FEATURE [Part::Feature] Solid036  label="SOLID035"
  TreeRank = 604
  shape: bbox 15.24 x 5.715 x 13.59 mm, 79 faces (baked)
FEATURE [App::LinkGroup] LinkGroup036  label="TE_3-641124-6"
  ElementList = -> [Solid036]
  LinkMode = 0
  Placement = pos=(-30.5,-49.5,4.15) rot=(0,0,1;0rad)
  TreeRank = 605
  _LinkVersion = 1
FEATURE [Part::Feature] Solid037  label="SOLID036"
  TreeRank = 606
  shape: bbox 2.54 x 5.08 x 11.54 mm, 52 faces (baked)
FEATURE [App::LinkGroup] LinkGroup037  label="PinHeader_1x02_P2.54mm_Vertical"
  ElementList = -> [Solid037]
  LinkMode = 0
  Placement = pos=(21,51.9,1.65) rot=(0,0,1;0rad)
  TreeRank = 607
  _LinkVersion = 1
FEATURE [App::Link] Link191  label="C_0805_2012Metric104"
  AutoLinkLabel = true
  AutoPlacement = true
  LinkPlacement = pos=(-71.5,42.5,-0.05) rot=(0,1,0;3.14159rad)
  LinkedObject = -> LinkGroup023
  Placement = pos=(-71.5,42.5,-0.05) rot=(0,1,0;3.14159rad)
  SyncGroupVisibility = false
  TreeRank = 608
  _LinkVersion = 1
FEATURE [App::Link] Link192  label="C_0805_2012Metric105"
  AutoLinkLabel = true
  AutoPlacement = true
  LinkPlacement = pos=(-72.5,42.5,1.65) rot=(0,0,1;3.14159rad)
  LinkedObject = -> LinkGroup023
  Placement = pos=(-72.5,42.5,1.65) rot=(0,0,1;3.14159rad)
  SyncGroupVisibility = false
  TreeRank = 609
  _LinkVersion = 1
FEATURE [Part::Feature] Solid038  label="COMPOUND001"
  TreeRank = 612
  shape: bbox 203 x 116 x 1.6 mm, 438 faces (baked)
FEATURE [App::LinkGroup] LinkGroup038  label="GCM"
  ElementList = -> [LinkGroup018,LinkGroup019,LinkGroup020,LinkGroup021,LinkGroup022,Link092,LinkGroup023,Link093,Link094,Link095,Link096,Link097,Link098,Link099,Link100,Link101,Link102,Link103,Link104,Link105,Link106,Link107,Link108,Link109,Link110,Link111,Link112,Link113,Link114,Link115,Link116,Link117,Link118,Link119,Link120,Link121,Link122,Link123,Link124,Link125,Link126,Link127,Link128,Link129,LinkGroup024,+77 more]
  LinkMode = 0
  Placement = pos=(-36.0451,26.2527,72.5601) rot=(0,0,1;0rad)
  TreeRank = 613
  _LinkVersion = 1
FEATURE [Part::Feature] Solid039  label="SOLID037"
  TreeRank = 650
  shape: bbox 3.2 x 1.6 x 1.6 mm, 28 faces (baked)
FEATURE [App::LinkGroup] LinkGroup039  label="C_1206_3216Metric"
  ElementList = -> [Solid039]
  LinkMode = 0
  Placement = pos=(4,-7.5,1.65) rot=(0,0,1;1.5708rad)
  TreeRank = 651
  _LinkVersion = 1
FEATURE [App::Link] Link193  label="C_1206_3216Metric001"
  AutoLinkLabel = true
  AutoPlacement = true
  LinkPlacement = pos=(4,26,1.65) rot=(0,0,1;1.5708rad)
  LinkedObject = -> LinkGroup039
  Placement = pos=(4,26,1.65) rot=(0,0,1;1.5708rad)
  SyncGroupVisibility = false
  TreeRank = 652
  _LinkVersion = 1
FEATURE [App::Link] Link194  label="C_1206_3216Metric002"
  AutoLinkLabel = true
  AutoPlacement = true
  LinkPlacement = pos=(12,-7.5,1.65) rot=(0,0,1;1.5708rad)
  LinkedObject = -> LinkGroup039
  Placement = pos=(12,-7.5,1.65) rot=(0,0,1;1.5708rad)
  SyncGroupVisibility = false
  TreeRank = 653
  _LinkVersion = 1
FEATURE [App::Link] Link195  label="C_1206_3216Metric003"
  AutoLinkLabel = true
  AutoPlacement = true
  LinkPlacement = pos=(12,26,1.65) rot=(0,0,1;1.5708rad)
  LinkedObject = -> LinkGroup039
  Placement = pos=(12,26,1.65) rot=(0,0,1;1.5708rad)
  SyncGroupVisibility = false
  TreeRank = 654
  _LinkVersion = 1
FEATURE [App::Link] Link196  label="C_1206_3216Metric004"
  AutoLinkLabel = true
  AutoPlacement = true
  LinkPlacement = pos=(8,-7.5,1.65) rot=(0,0,1;1.5708rad)
  LinkedObject = -> LinkGroup039
  Placement = pos=(8,-7.5,1.65) rot=(0,0,1;1.5708rad)
  SyncGroupVisibility = false
  TreeRank = 655
  _LinkVersion = 1
FEATURE [App::Link] Link197  label="C_1206_3216Metric005"
  AutoLinkLabel = true
  AutoPlacement = true
  LinkPlacement = pos=(8,26,1.65) rot=(0,0,1;1.5708rad)
  LinkedObject = -> LinkGroup039
  Placement = pos=(8,26,1.65) rot=(0,0,1;1.5708rad)
  SyncGroupVisibility = false
  TreeRank = 656
  _LinkVersion = 1
FEATURE [App::Link] Link198  label="C_1206_3216Metric006"
  AutoLinkLabel = true
  AutoPlacement = true
  LinkPlacement = pos=(21,-2.5,1.65) rot=(0,0,1;0rad)
  LinkedObject = -> LinkGroup039
  Placement = pos=(21,-2.5,1.65) rot=(0,0,1;0rad)
  SyncGroupVisibility = false
  TreeRank = 657
  _LinkVersion = 1
FEATURE [App::Link] Link199  label="C_1206_3216Metric007"
  AutoLinkLabel = true
  AutoPlacement = true
  LinkPlacement = pos=(21,31,1.65) rot=(0,0,1;0rad)
  LinkedObject = -> LinkGroup039
  Placement = pos=(21,31,1.65) rot=(0,0,1;0rad)
  SyncGroupVisibility = false
  TreeRank = 658
  _LinkVersion = 1
FEATURE [App::Link] Link200  label="C_1206_3216Metric008"
  AutoLinkLabel = true
  AutoPlacement = true
  LinkPlacement = pos=(1,5.5,1.65) rot=(0,0,1;0rad)
  LinkedObject = -> LinkGroup039
  Placement = pos=(1,5.5,1.65) rot=(0,0,1;0rad)
  SyncGroupVisibility = false
  TreeRank = 659
  _LinkVersion = 1
FEATURE [App::Link] Link201  label="C_1206_3216Metric009"
  AutoLinkLabel = true
  AutoPlacement = true
  LinkPlacement = pos=(1,43,1.65) rot=(0,0,1;0rad)
  LinkedObject = -> LinkGroup039
  Placement = pos=(1,43,1.65) rot=(0,0,1;0rad)
  SyncGroupVisibility = false
  TreeRank = 660
  _LinkVersion = 1
FEATURE [App::Link] Link202  label="C_1206_3216Metric010"
  AutoLinkLabel = true
  AutoPlacement = true
  LinkPlacement = pos=(1,1.5,1.65) rot=(0,0,1;0rad)
  LinkedObject = -> LinkGroup039
  Placement = pos=(1,1.5,1.65) rot=(0,0,1;0rad)
  SyncGroupVisibility = false
  TreeRank = 661
  _LinkVersion = 1
FEATURE [App::Link] Link203  label="C_1206_3216Metric011"
  AutoLinkLabel = true
  AutoPlacement = true
  LinkPlacement = pos=(1,39,1.65) rot=(0,0,1;0rad)
  LinkedObject = -> LinkGroup039
  Placement = pos=(1,39,1.65) rot=(0,0,1;0rad)
  SyncGroupVisibility = false
  TreeRank = 662
  _LinkVersion = 1
FEATURE [App::Link] Link204  label="C_1206_3216Metric012"
  AutoLinkLabel = true
  AutoPlacement = true
  LinkPlacement = pos=(1,35,1.65) rot=(0,0,1;0rad)
  LinkedObject = -> LinkGroup039
  Placement = pos=(1,35,1.65) rot=(0,0,1;0rad)
  SyncGroupVisibility = false
  TreeRank = 663
  _LinkVersion = 1
FEATURE [Part::Feature] Solid040  label="SOLID038"
  TreeRank = 664
  shape: bbox 8 x 5.9 x 2.31 mm, 41 faces (baked)
FEATURE [App::LinkGroup] LinkGroup040  label="D_SMC"
  ElementList = -> [Solid040]
  LinkMode = 0
  Placement = pos=(3,-25,1.65) rot=(0,0,-1;1.5708rad)
  TreeRank = 665
  _LinkVersion = 1
FEATURE [App::Link] Link205  label="D_SMC001"
  AutoLinkLabel = true
  AutoPlacement = true
  LinkPlacement = pos=(20.5,-25,1.65) rot=(0,0,-1;1.5708rad)
  LinkedObject = -> LinkGroup040
  Placement = pos=(20.5,-25,1.65) rot=(0,0,-1;1.5708rad)
  SyncGroupVisibility = false
  TreeRank = 666
  _LinkVersion = 1
FEATURE [Part::Feature] Solid041  label="SOLID039"
  TreeRank = 667
  shape: bbox 5.54 x 6.2 x 12 mm, 81 faces (baked)
FEATURE [App::LinkGroup] LinkGroup041  label="TerminalBlock_Phoenix_MPT-0,5-2-2.54_1x02_P2.54mm_Horizontal"
  ElementList = -> [Solid041]
  LinkMode = 0
  Placement = pos=(18,-40.5,1.65) rot=(0,0,1;0rad)
  TreeRank = 668
  _LinkVersion = 1
FEATURE [Part::Feature] Solid042  label="SOLID040"
  TreeRank = 669
  shape: bbox 10.62 x 6.2 x 12 mm, 145 faces (baked)
FEATURE [App::LinkGroup] LinkGroup042  label="TerminalBlock_Phoenix_MPT-0,5-4-2.54_1x04_P2.54mm_Horizontal"
  ElementList = -> [Solid042]
  LinkMode = 0
  Placement = pos=(35.5,-0.5,1.65) rot=(0,0,1;1.5708rad)
  TreeRank = 670
  _LinkVersion = 1
FEATURE [Part::Feature] Solid043  label="SOLID041"
  TreeRank = 683
  shape: bbox 2 x 1.2 x 0.45 mm, 26 faces (baked)
FEATURE [App::LinkGroup] LinkGroup043  label="R_0805_2012Metric013"
  ElementList = -> [Solid043]
  LinkMode = 0
  Placement = pos=(24,-12.5,1.65) rot=(0,0,1;1.5708rad)
  TreeRank = 684
  _LinkVersion = 1
FEATURE [App::Link] Link206  label="R_0805_2012Metric014"
  AutoLinkLabel = true
  AutoPlacement = true
  LinkPlacement = pos=(24,20.5,1.65) rot=(0,0,1;1.5708rad)
  LinkedObject = -> LinkGroup043
  Placement = pos=(24,20.5,1.65) rot=(0,0,1;1.5708rad)
  SyncGroupVisibility = false
  TreeRank = 685
  _LinkVersion = 1
FEATURE [App::Link] Link207  label="R_0805_2012Metric015"
  AutoLinkLabel = true
  AutoPlacement = true
  LinkPlacement = pos=(29,-6.5,1.65) rot=(0,0,-1;1.5708rad)
  LinkedObject = -> LinkGroup043
  Placement = pos=(29,-6.5,1.65) rot=(0,0,-1;1.5708rad)
  SyncGroupVisibility = false
  TreeRank = 686
  _LinkVersion = 1
FEATURE [App::Link] Link208  label="R_0805_2012Metric016"
  AutoLinkLabel = true
  AutoPlacement = true
  LinkPlacement = pos=(27,-6.5,1.65) rot=(0,0,1;1.5708rad)
  LinkedObject = -> LinkGroup043
  Placement = pos=(27,-6.5,1.65) rot=(0,0,1;1.5708rad)
  SyncGroupVisibility = false
  TreeRank = 687
  _LinkVersion = 1
FEATURE [App::Link] Link209  label="R_0805_2012Metric017"
  AutoLinkLabel = true
  AutoPlacement = true
  LinkPlacement = pos=(29,27,1.65) rot=(0,0,-1;1.5708rad)
  LinkedObject = -> LinkGroup043
  Placement = pos=(29,27,1.65) rot=(0,0,-1;1.5708rad)
  SyncGroupVisibility = false
  TreeRank = 688
  _LinkVersion = 1
FEATURE [App::Link] Link210  label="R_0805_2012Metric018"
  AutoLinkLabel = true
  AutoPlacement = true
  LinkPlacement = pos=(27,27,1.65) rot=(0,0,1;1.5708rad)
  LinkedObject = -> LinkGroup043
  Placement = pos=(27,27,1.65) rot=(0,0,1;1.5708rad)
  SyncGroupVisibility = false
  TreeRank = 689
  _LinkVersion = 1
FEATURE [Part::Feature] Solid044  label="SOLID042"
  TreeRank = 690
  shape: bbox 2.8 x 2.9 x 1.55 mm, 124 faces (baked)
FEATURE [App::LinkGroup] LinkGroup044  label="SOT-23-6"
  ElementList = -> [Solid044]
  LinkMode = 0
  Placement = pos=(20,-7.5,1.65) rot=(0,0,1;0rad)
  TreeRank = 691
  _LinkVersion = 1
FEATURE [App::Link] Link211  label="SOT-23-020"
  AutoLinkLabel = true
  AutoPlacement = true
  LinkPlacement = pos=(20,26,1.65) rot=(0,0,1;0rad)
  LinkedObject = -> LinkGroup044
  Placement = pos=(20,26,1.65) rot=(0,0,1;0rad)
  SyncGroupVisibility = false
  TreeRank = 692
  _LinkVersion = 1
FEATURE [Part::Feature] Solid045  label="COMPOUND002"
  TreeRank = 693
  shape: bbox 85 x 95 x 1.6 mm, 45 faces (baked)
FEATURE [App::LinkGroup] LinkGroup045  label="GCM_powerSupply"
  ElementList = -> [LinkGroup039,Link193,Link194,Link195,Link196,Link197,Link198,Link199,Link200,Link201,Link202,Link203,Link204,LinkGroup040,Link205,LinkGroup041,LinkGroup042,LinkGroup043,Link206,Link207,Link208,Link209,Link210,LinkGroup044,Link211,Solid045]
  LinkMode = 0
  Placement = pos=(58.4549,136.153,106.66) rot=(-0.707107,0,0.707107;3.14159rad)
  TreeRank = 694
  _LinkVersion = 1
FEATURE [App::Link] Link212  label="FirstPartPeripheralsTop"
  AutoLinkLabel = false
  AutoPlacement = true
  LinkPlacement = pos=(65.4549,-31.7473,162.16) rot=(0,0,1;0rad)
  LinkedObject = -> <external FirstPartPeripheralsTop.FCStd>#Part
  Placement = pos=(65.4549,-31.7473,162.16) rot=(0,0,1;0rad)
  SyncGroupVisibility = false
  TreeRank = 713
  _LinkOwner = 312
  _LinkVersion = 1
FEATURE [App::Link] Link213  label="SecondPartPeripheralsTop"
  AutoLinkLabel = false
  AutoPlacement = true
  LinkPlacement = pos=(-74.5451,-31.7473,162.16) rot=(0,0,1;0rad)
  LinkedObject = -> <external SecondPartPeripheralsTop.FCStd>#Part
  Placement = pos=(-74.5451,-31.7473,162.16) rot=(0,0,1;0rad)
  SyncGroupVisibility = false
  TreeRank = 728
  _LinkOwner = 312
  _LinkVersion = 1
FEATURE [App::Link] Link214  label="SecondPartProcessorTop"
  AutoLinkLabel = false
  AutoPlacement = true
  LinkPlacement = pos=(-74.5451,91.6527,162.16) rot=(0,0,1;0rad)
  LinkedObject = -> <external SecondPartProcessorTop.FCStd>#Part
  Placement = pos=(-74.5451,91.6527,162.16) rot=(0,0,1;0rad)
  SyncGroupVisibility = false
  TreeRank = 744
  _LinkOwner = 312
  _LinkVersion = 1
FEATURE [App::Link] Link215  label="FirstPartProcessorTop"
  AutoLinkLabel = false
  AutoPlacement = true
  LinkPlacement = pos=(65.4549,91.6527,162.16) rot=(0,0,1;0rad)
  LinkedObject = -> <external FirstPartProcessorTop.FCStd>#Part
  Placement = pos=(65.4549,91.6527,162.16) rot=(0,0,1;0rad)
  SyncGroupVisibility = false
  TreeRank = 760
  _LinkOwner = 312
  _LinkVersion = 1
FEATURE [Part::FeaturePython] Parts  # WARN: FeaturePython — macro-defined, semantics opaque (R4)
  Group = -> [Link,Link001,Link002,Link003,LinkGroup017,LinkGroup038,LinkGroup045,Link212,Link213,Link214,Link215]
  GroupMode = 0
  TreeRank = 0
  _LinkVersion = 1
FEATURE [Part::FeaturePython] Assembly  # WARN: FeaturePython — macro-defined, semantics opaque (R4)
  AutoRelax = true
  BuildShape = 0
  Freeze = false
  Group = -> [Constraints,Elements,Parts]
  Placement = pos=(6.43504,0.0201416,-24.6051) rot=(0,0,1;0rad)
  TreeRank = 0
  Verbose = false
  _LinkVersion = 1
  _SolverType = 1
  _Version = 1
FEATURE [App::FeaturePython] Constraints  # WARN: FeaturePython — macro-defined, semantics opaque (R4)
  Group = -> [Constraint001,Constraint,Constraint002,Constraint003,Constraint004,Constraint005,Constraint006,Constraint007,Constraint008,Constraint009,Constraint010,Constraint011,Constraint012,Constraint013,Constraint014,Constraint015,Constraint016,Constraint017,Constraint018,Constraint019,Constraint020,Constraint021,Constraint022,Constraint023,Constraint024,Constraint025,Constraint026,Constraint027,+1 more]
  TreeRank = 0
  _LinkVersion = 1
  _Version = 1
FEATURE [App::FeaturePython] Elements  # WARN: FeaturePython — macro-defined, semantics opaque (R4)
  Group = -> [_Element,_Element001,_Element002,_Element003,_Element004,_Element005,_Element006,_Element007,_Element008,_Element009,_Element010,_Element011,_Element012,_Element013,_Element014,_Element015,_Element016,_Element017,_Element018,_Element019,_Element020,_Element021,_Element022,_Element023,_Element024,_Element025,_Element026,_Element027,_Element028,_Element029,_Element030,_Element031,_Element032,+26 more]
  TreeRank = 0
  _LinkVersion = 1
FEATURE [Part::FeaturePython] _Element  # link proxy (typed FeaturePython)
  Detach = false
  LinkTransform = true
  LinkedObject = -> Link001 [Body.Fillet.Face7]
  TreeRank = 6
  _LinkVersion = 1
  _Parent = -> Elements
FEATURE [Part::FeaturePython] _Element001  # link proxy (typed FeaturePython)
  Detach = false
  LinkTransform = true
  LinkedObject = -> Link [Body.Fillet.Face4]
  TreeRank = 10
  _LinkVersion = 1
  _Parent = -> Elements
FEATURE [App::FeaturePython] Constraint001  label="PlaneAlignment"  # WARN: FeaturePython — macro-defined, semantics opaque (R4)
  Angle = 0
  AnglePitch = 0
  AngleRoll = 0
  Cascade = false
  Disabled = false
  Group = -> [ElementLink002,ElementLink003]
  LockAngle = false
  TreeRank = 11
  _ConstraintType = 37
  _LinkVersion = 1
  _Parent = -> Constraints
FEATURE [App::FeaturePython] ElementLink002  label="_Element002"  # link proxy (typed FeaturePython)
  LinkTransform = true
  LinkedObject = -> _Element002
  TreeRank = 12
  _LinkVersion = 1
  _Parent = -> Constraint001
FEATURE [Part::FeaturePython] _Element002  # link proxy (typed FeaturePython)
  Detach = false
  LinkTransform = true
  LinkedObject = -> Link001 [Body.Fillet.Face59]
  TreeRank = 13
  _LinkVersion = 1
  _Parent = -> Elements
FEATURE [App::FeaturePython] ElementLink003  label="_Element003"  # link proxy (typed FeaturePython)
  LinkTransform = true
  LinkedObject = -> _Element003
  TreeRank = 14
  _LinkVersion = 1
  _Parent = -> Constraint001
FEATURE [Part::FeaturePython] _Element003  # link proxy (typed FeaturePython)
  Detach = false
  LinkTransform = true
  LinkedObject = -> Link [Body.Fillet.Face32]
  TreeRank = 15
  _LinkVersion = 1
  _Parent = -> Elements
FEATURE [App::FeaturePython] Constraint  label="PlaneAlignment001"  # WARN: FeaturePython — macro-defined, semantics opaque (R4)
  Angle = 0
  AnglePitch = 0
  AngleRoll = 0
  Cascade = false
  Disabled = false
  Group = -> [ElementLink,ElementLink004]
  LockAngle = false
  TreeRank = 16
  _ConstraintType = 37
  _LinkVersion = 1
  _Parent = -> Constraints
FEATURE [App::FeaturePython] ElementLink  label="_Element"  # link proxy (typed FeaturePython)
  LinkTransform = true
  LinkedObject = -> _Element
  TreeRank = 17
  _LinkVersion = 1
  _Parent = -> Constraint
FEATURE [App::FeaturePython] ElementLink004  label="_Element001"  # link proxy (typed FeaturePython)
  LinkTransform = true
  LinkedObject = -> _Element001
  TreeRank = 18
  _LinkVersion = 1
  _Parent = -> Constraint
FEATURE [App::FeaturePython] Constraint002  label="PlaneAlignment002"  # WARN: FeaturePython — macro-defined, semantics opaque (R4)
  Angle = 0
  AnglePitch = 0
  AngleRoll = 0
  Cascade = false
  Disabled = false
  Group = -> [ElementLink005,ElementLink006]
  LockAngle = false
  TreeRank = 19
  _ConstraintType = 37
  _LinkVersion = 1
  _Parent = -> Constraints
FEATURE [App::FeaturePython] ElementLink005  label="_Element004"  # link proxy (typed FeaturePython)
  LinkTransform = true
  LinkedObject = -> _Element004
  TreeRank = 20
  _LinkVersion = 1
  _Parent = -> Constraint002
FEATURE [Part::FeaturePython] _Element004  # link proxy (typed FeaturePython)
  Detach = false
  LinkTransform = true
  LinkedObject = -> Link001 [Body.Fillet.Face5]
  TreeRank = 21
  _LinkVersion = 1
  _Parent = -> Elements
FEATURE [App::FeaturePython] ElementLink006  label="_Element005"  # link proxy (typed FeaturePython)
  LinkTransform = true
  LinkedObject = -> _Element005
  TreeRank = 22
  _LinkVersion = 1
  _Parent = -> Constraint002
FEATURE [Part::FeaturePython] _Element005  # link proxy (typed FeaturePython)
  Detach = false
  LinkTransform = true
  LinkedObject = -> Link [Body.Fillet.Face2]
  TreeRank = 23
  _LinkVersion = 1
  _Parent = -> Elements
FEATURE [App::FeaturePython] Constraint003  label="PlaneAlignment003"  # WARN: FeaturePython — macro-defined, semantics opaque (R4)
  Angle = 0
  AnglePitch = 0
  AngleRoll = 0
  Cascade = false
  Disabled = false
  Group = -> [ElementLink007,ElementLink008]
  LockAngle = false
  TreeRank = 25
  _ConstraintType = 37
  _LinkVersion = 1
  _Parent = -> Constraints
FEATURE [App::FeaturePython] ElementLink007  label="_Element006"  # link proxy (typed FeaturePython)
  LinkTransform = true
  LinkedObject = -> _Element006
  TreeRank = 26
  _LinkVersion = 1
  _Parent = -> Constraint003
FEATURE [Part::FeaturePython] _Element006  # link proxy (typed FeaturePython)
  Detach = false
  LinkTransform = true
  LinkedObject = -> Link002 [Body.Pocket006.Face30]
  TreeRank = 27
  _LinkVersion = 1
  _Parent = -> Elements
FEATURE [App::FeaturePython] ElementLink008  label="_Element007"  # link proxy (typed FeaturePython)
  LinkTransform = true
  LinkedObject = -> _Element007
  TreeRank = 28
  _LinkVersion = 1
  _Parent = -> Constraint003
FEATURE [Part::FeaturePython] _Element007  # link proxy (typed FeaturePython)
  Detach = false
  LinkTransform = true
  LinkedObject = -> Link [Body.Fillet.Face1]
  TreeRank = 29
  _LinkVersion = 1
  _Parent = -> Elements
FEATURE [App::FeaturePython] Constraint004  label="PlaneAlignment004"  # WARN: FeaturePython — macro-defined, semantics opaque (R4)
  Angle = 0
  AnglePitch = 0
  AngleRoll = 0
  Cascade = false
  Disabled = false
  Group = -> [ElementLink009,ElementLink010]
  LockAngle = false
  TreeRank = 30
  _ConstraintType = 37
  _LinkVersion = 1
  _Parent = -> Constraints
FEATURE [App::FeaturePython] ElementLink009  label="_Element008"  # link proxy (typed FeaturePython)
  LinkTransform = true
  LinkedObject = -> _Element008
  TreeRank = 31
  _LinkVersion = 1
  _Parent = -> Constraint004
FEATURE [Part::FeaturePython] _Element008  # link proxy (typed FeaturePython)
  Detach = false
  LinkTransform = true
  LinkedObject = -> Link002 [Body.Pocket006.Face5]
  TreeRank = 32
  _LinkVersion = 1
  _Parent = -> Elements
FEATURE [App::FeaturePython] ElementLink010  label="_Element005"  # link proxy (typed FeaturePython)
  LinkTransform = true
  LinkedObject = -> _Element005
  TreeRank = 33
  _LinkVersion = 1
  _Parent = -> Constraint004
FEATURE [App::FeaturePython] Constraint005  label="PlaneAlignment005"  # WARN: FeaturePython — macro-defined, semantics opaque (R4)
  Angle = 0
  AnglePitch = 0
  AngleRoll = 0
  Cascade = false
  Disabled = false
  Group = -> [ElementLink011,ElementLink012]
  LockAngle = false
  TreeRank = 34
  _ConstraintType = 37
  _LinkVersion = 1
  _Parent = -> Constraints
FEATURE [App::FeaturePython] ElementLink011  label="_Element009"  # link proxy (typed FeaturePython)
  LinkTransform = true
  LinkedObject = -> _Element009
  TreeRank = 35
  _LinkVersion = 1
  _Parent = -> Constraint005
FEATURE [Part::FeaturePython] _Element009  # link proxy (typed FeaturePython)
  Detach = false
  LinkTransform = true
  LinkedObject = -> Link [Body.Fillet.Face49]
  TreeRank = 36
  _LinkVersion = 1
  _Parent = -> Elements
FEATURE [App::FeaturePython] ElementLink012  label="_Element010"  # link proxy (typed FeaturePython)
  LinkTransform = true
  LinkedObject = -> _Element010
  TreeRank = 37
  _LinkVersion = 1
  _Parent = -> Constraint005
FEATURE [Part::FeaturePython] _Element010  # link proxy (typed FeaturePython)
  Detach = false
  LinkTransform = true
  LinkedObject = -> Link002 [Body.Pocket006.Face8]
  TreeRank = 38
  _LinkVersion = 1
  _Parent = -> Elements
FEATURE [App::FeaturePython] Constraint006  label="PlaneAlignment006"  # WARN: FeaturePython — macro-defined, semantics opaque (R4)
  Angle = 0
  AnglePitch = 0
  AngleRoll = 0
  Cascade = false
  Disabled = false
  Group = -> [ElementLink013,ElementLink014]
  LockAngle = false
  TreeRank = 40
  _ConstraintType = 37
  _LinkVersion = 1
  _Parent = -> Constraints
FEATURE [App::FeaturePython] ElementLink013  label="_Element011"  # link proxy (typed FeaturePython)
  LinkTransform = true
  LinkedObject = -> _Element011
  TreeRank = 41
  _LinkVersion = 1
  _Parent = -> Constraint006
FEATURE [Part::FeaturePython] _Element011  # link proxy (typed FeaturePython)
  Detach = false
  LinkTransform = true
  LinkedObject = -> Link003 [Body.Fillet.Face4]
  TreeRank = 42
  _LinkVersion = 1
  _Parent = -> Elements
FEATURE [App::FeaturePython] ElementLink014  label="_Element012"  # link proxy (typed FeaturePython)
  LinkTransform = true
  LinkedObject = -> _Element012
  TreeRank = 43
  _LinkVersion = 1
  _Parent = -> Constraint006
FEATURE [Part::FeaturePython] _Element012  # link proxy (typed FeaturePython)
  Detach = false
  LinkTransform = true
  LinkedObject = -> Link002 [Body.Pocket006.Face14]
  TreeRank = 44
  _LinkVersion = 1
  _Parent = -> Elements
FEATURE [App::FeaturePython] Constraint007  label="PlaneAlignment007"  # WARN: FeaturePython — macro-defined, semantics opaque (R4)
  Angle = 0
  AnglePitch = 0
  AngleRoll = 0
  Cascade = false
  Disabled = false
  Group = -> [ElementLink015,ElementLink016]
  LockAngle = false
  TreeRank = 45
  _ConstraintType = 37
  _LinkVersion = 1
  _Parent = -> Constraints
FEATURE [App::FeaturePython] ElementLink015  label="_Element013"  # link proxy (typed FeaturePython)
  LinkTransform = true
  LinkedObject = -> _Element013
  TreeRank = 46
  _LinkVersion = 1
  _Parent = -> Constraint007
FEATURE [Part::FeaturePython] _Element013  # link proxy (typed FeaturePython)
  Detach = false
  LinkTransform = true
  LinkedObject = -> Link003 [Body.Fillet.Face1]
  TreeRank = 47
  _LinkVersion = 1
  _Parent = -> Elements
FEATURE [App::FeaturePython] ElementLink016  label="_Element008"  # link proxy (typed FeaturePython)
  LinkTransform = true
  LinkedObject = -> _Element008
  TreeRank = 48
  _LinkVersion = 1
  _Parent = -> Constraint007
FEATURE [App::FeaturePython] Constraint008  label="PlaneAlignment008"  # WARN: FeaturePython — macro-defined, semantics opaque (R4)
  Angle = 0
  AnglePitch = 0
  AngleRoll = 0
  Cascade = false
  Disabled = false
  Group = -> [ElementLink017,ElementLink018]
  LockAngle = false
  TreeRank = 49
  _ConstraintType = 37
  _LinkVersion = 1
  _Parent = -> Constraints
FEATURE [App::FeaturePython] ElementLink017  label="_Element014"  # link proxy (typed FeaturePython)
  LinkTransform = true
  LinkedObject = -> _Element014
  TreeRank = 50
  _LinkVersion = 1
  _Parent = -> Constraint008
FEATURE [Part::FeaturePython] _Element014  # link proxy (typed FeaturePython)
  Detach = false
  LinkTransform = true
  LinkedObject = -> Link003 [Body.Fillet.Face23]
  TreeRank = 51
  _LinkVersion = 1
  _Parent = -> Elements
FEATURE [App::FeaturePython] ElementLink018  label="_Element015"  # link proxy (typed FeaturePython)
  LinkTransform = true
  LinkedObject = -> _Element015
  TreeRank = 52
  _LinkVersion = 1
  _Parent = -> Constraint008
FEATURE [Part::FeaturePython] _Element015  # link proxy (typed FeaturePython)
  Detach = false
  LinkTransform = true
  LinkedObject = -> Link002 [Body.Pocket006.Face79]
  TreeRank = 53
  _LinkVersion = 1
  _Parent = -> Elements
FEATURE [App::FeaturePython] Constraint009  label="PlaneAlignment009"  # WARN: FeaturePython — macro-defined, semantics opaque (R4)
  Angle = 0
  AnglePitch = 0
  AngleRoll = 0
  Cascade = false
  Disabled = false
  Group = -> [ElementLink019,ElementLink020]
  LockAngle = false
  TreeRank = 302
  _ConstraintType = 37
  _LinkVersion = 1
  _Parent = -> Constraints
FEATURE [App::FeaturePython] ElementLink019  label="_Element016"  # link proxy (typed FeaturePython)
  LinkTransform = true
  LinkedObject = -> _Element016
  TreeRank = 303
  _LinkVersion = 1
  _Parent = -> Constraint009
FEATURE [Part::FeaturePython] _Element016  # link proxy (typed FeaturePython)
  Detach = false
  LinkTransform = true
  LinkedObject = -> LinkGroup017 [Solid017.Face4]
  TreeRank = 304
  _LinkVersion = 1
  _Parent = -> Elements
FEATURE [App::FeaturePython] ElementLink020  label="_Element017"  # link proxy (typed FeaturePython)
  LinkTransform = true
  LinkedObject = -> _Element017
  TreeRank = 305
  _LinkVersion = 1
  _Parent = -> Constraint009
FEATURE [Part::FeaturePython] _Element017  # link proxy (typed FeaturePython)
  Detach = false
  LinkTransform = true
  LinkedObject = -> Link002 [Body.Pocket006.Face59]
  TreeRank = 306
  _LinkVersion = 1
  _Parent = -> Elements
FEATURE [Part::FeaturePython] _Element018  # link proxy (typed FeaturePython)
  Detach = false
  LinkTransform = true
  LinkedObject = -> LinkGroup017 [Solid017.Edge231]
  TreeRank = 309
  _LinkVersion = 1
  _Parent = -> Elements
FEATURE [Part::FeaturePython] _Element019  # link proxy (typed FeaturePython)
  Detach = false
  LinkTransform = true
  LinkedObject = -> Link002 [Body.Pocket006.Edge186]
  TreeRank = 311
  _LinkVersion = 1
  _Parent = -> Elements
FEATURE [App::FeaturePython] Constraint010  label="PointsCoincident"  # WARN: FeaturePython — macro-defined, semantics opaque (R4)
  Disabled = false
  Group = -> [ElementLink021,ElementLink022]
  TreeRank = 312
  _ConstraintType = 1
  _LinkVersion = 1
  _Parent = -> Constraints
FEATURE [App::FeaturePython] ElementLink021  label="_Element018"  # link proxy (typed FeaturePython)
  LinkTransform = true
  LinkedObject = -> _Element018
  TreeRank = 313
  _LinkVersion = 1
  _Parent = -> Constraint010
FEATURE [App::FeaturePython] ElementLink022  label="_Element019"  # link proxy (typed FeaturePython)
  LinkTransform = true
  LinkedObject = -> _Element019
  TreeRank = 314
  _LinkVersion = 1
  _Parent = -> Constraint010
FEATURE [Part::FeaturePython] _Element020  # link proxy (typed FeaturePython)
  Detach = false
  LinkTransform = true
  LinkedObject = -> LinkGroup017 [Solid017.Edge142]
  TreeRank = 317
  _LinkVersion = 1
  _Parent = -> Elements
FEATURE [Part::FeaturePython] _Element021  # link proxy (typed FeaturePython)
  Detach = false
  LinkTransform = true
  LinkedObject = -> Link003 [Body.Fillet.Edge139]
  TreeRank = 319
  _LinkVersion = 1
  _Parent = -> Elements
FEATURE [Part::FeaturePython] _Element022  # link proxy (typed FeaturePython)
  Detach = false
  LinkTransform = true
  LinkedObject = -> LinkGroup017 [Solid017.Face3]
  TreeRank = 322
  _LinkVersion = 1
  _Parent = -> Elements
FEATURE [Part::FeaturePython] _Element023  # link proxy (typed FeaturePython)
  Detach = false
  LinkTransform = true
  LinkedObject = -> Link002 [Body.Pocket006.Face49]
  TreeRank = 324
  _LinkVersion = 1
  _Parent = -> Elements
FEATURE [App::FeaturePython] Constraint011  label="SameOrientation"  # WARN: FeaturePython — macro-defined, semantics opaque (R4)
  Disabled = false
  Group = -> [ElementLink023,ElementLink024]
  TreeRank = 325
  _ConstraintType = 2
  _LinkVersion = 1
  _Parent = -> Constraints
FEATURE [App::FeaturePython] ElementLink023  label="_Element022"  # link proxy (typed FeaturePython)
  LinkTransform = true
  LinkedObject = -> _Element022
  TreeRank = 326
  _LinkVersion = 1
  _Parent = -> Constraint011
FEATURE [App::FeaturePython] ElementLink024  label="_Element023"  # link proxy (typed FeaturePython)
  LinkTransform = true
  LinkedObject = -> _Element023
  TreeRank = 327
  _LinkVersion = 1
  _Parent = -> Constraint011
FEATURE [App::FeaturePython] Constraint012  label="PlaneAlignment010"  # WARN: FeaturePython — macro-defined, semantics opaque (R4)
  Angle = 0
  AnglePitch = 0
  AngleRoll = 0
  Cascade = false
  Disabled = false
  Group = -> [ElementLink025,ElementLink026]
  LockAngle = false
  TreeRank = 614
  _ConstraintType = 37
  _LinkVersion = 1
  _Parent = -> Constraints
FEATURE [App::FeaturePython] ElementLink025  label="_Element024"  # link proxy (typed FeaturePython)
  LinkTransform = true
  LinkedObject = -> _Element024
  TreeRank = 615
  _LinkVersion = 1
  _Parent = -> Constraint012
FEATURE [Part::FeaturePython] _Element024  # link proxy (typed FeaturePython)
  Detach = false
  LinkTransform = true
  LinkedObject = -> LinkGroup038 [Solid038.Face4]
  TreeRank = 616
  _LinkVersion = 1
  _Parent = -> Elements
FEATURE [App::FeaturePython] ElementLink026  label="_Element025"  # link proxy (typed FeaturePython)
  LinkTransform = true
  LinkedObject = -> _Element025
  TreeRank = 617
  _LinkVersion = 1
  _Parent = -> Constraint012
FEATURE [Part::FeaturePython] _Element025  # link proxy (typed FeaturePython)
  Detach = false
  LinkTransform = true
  LinkedObject = -> Link001 [Body.Fillet.Face34]
  TreeRank = 618
  _LinkVersion = 1
  _Parent = -> Elements
FEATURE [App::FeaturePython] Constraint013  label="PointsCoincident001"  # WARN: FeaturePython — macro-defined, semantics opaque (R4)
  Disabled = false
  Group = -> [ElementLink027,ElementLink028]
  TreeRank = 619
  _ConstraintType = 1
  _LinkVersion = 1
  _Parent = -> Constraints
FEATURE [App::FeaturePython] ElementLink027  label="_Element026"  # link proxy (typed FeaturePython)
  LinkTransform = true
  LinkedObject = -> _Element026
  TreeRank = 620
  _LinkVersion = 1
  _Parent = -> Constraint013
FEATURE [Part::FeaturePython] _Element026  # link proxy (typed FeaturePython)
  Detach = false
  LinkTransform = true
  LinkedObject = -> LinkGroup038 [Solid038.Edge393]
  TreeRank = 621
  _LinkVersion = 1
  _Parent = -> Elements
FEATURE [App::FeaturePython] ElementLink028  label="_Element027"  # link proxy (typed FeaturePython)
  LinkTransform = true
  LinkedObject = -> _Element027
  TreeRank = 622
  _LinkVersion = 1
  _Parent = -> Constraint013
FEATURE [Part::FeaturePython] _Element027  # link proxy (typed FeaturePython)
  Detach = false
  LinkTransform = true
  LinkedObject = -> Link001 [Body.Fillet.Edge105]
  TreeRank = 623
  _LinkVersion = 1
  _Parent = -> Elements
FEATURE [App::FeaturePython] Constraint014  label="SameOrientation001"  # WARN: FeaturePython — macro-defined, semantics opaque (R4)
  Disabled = false
  Group = -> [ElementLink029,ElementLink030]
  TreeRank = 624
  _ConstraintType = 2
  _LinkVersion = 1
  _Parent = -> Constraints
FEATURE [App::FeaturePython] ElementLink029  label="_Element028"  # link proxy (typed FeaturePython)
  LinkTransform = true
  LinkedObject = -> _Element028
  TreeRank = 625
  _LinkVersion = 1
  _Parent = -> Constraint014
FEATURE [Part::FeaturePython] _Element028  # link proxy (typed FeaturePython)
  Detach = false
  LinkTransform = true
  LinkedObject = -> LinkGroup038 [Solid038.Face6]
  TreeRank = 626
  _LinkVersion = 1
  _Parent = -> Elements
FEATURE [App::FeaturePython] ElementLink030  label="_Element029"  # link proxy (typed FeaturePython)
  LinkTransform = true
  LinkedObject = -> _Element029
  TreeRank = 627
  _LinkVersion = 1
  _Parent = -> Constraint014
FEATURE [Part::FeaturePython] _Element029  # link proxy (typed FeaturePython)
  Detach = false
  LinkTransform = true
  LinkedObject = -> Link [Body.Fillet.Face50]
  TreeRank = 628
  _LinkVersion = 1
  _Parent = -> Elements
FEATURE [Part::FeaturePython] _Element030  # link proxy (typed FeaturePython)
  Detach = false
  LinkTransform = true
  LinkedObject = -> LinkGroup045 [Solid045.Face4]
  TreeRank = 697
  _LinkVersion = 1
  _Parent = -> Elements
FEATURE [Part::FeaturePython] _Element031  # link proxy (typed FeaturePython)
  Detach = false
  LinkTransform = true
  LinkedObject = -> Link002 [Body.Pocket006.Face4]
  TreeRank = 699
  _LinkVersion = 1
  _Parent = -> Elements
FEATURE [App::FeaturePython] Constraint015  label="PointsCoincident002"  # WARN: FeaturePython — macro-defined, semantics opaque (R4)
  Disabled = false
  Group = -> [ElementLink031,ElementLink032]
  TreeRank = 700
  _ConstraintType = 1
  _LinkVersion = 1
  _Parent = -> Constraints
FEATURE [App::FeaturePython] ElementLink031  label="_Element032"  # link proxy (typed FeaturePython)
  LinkTransform = true
  LinkedObject = -> _Element032
  TreeRank = 701
  _LinkVersion = 1
  _Parent = -> Constraint015
FEATURE [Part::FeaturePython] _Element032  # link proxy (typed FeaturePython)
  Detach = false
  LinkTransform = true
  LinkedObject = -> LinkGroup045 [Solid045.Edge28]
  TreeRank = 702
  _LinkVersion = 1
  _Parent = -> Elements
FEATURE [App::FeaturePython] ElementLink032  label="_Element033"  # link proxy (typed FeaturePython)
  LinkTransform = true
  LinkedObject = -> _Element033
  TreeRank = 703
  _LinkVersion = 1
  _Parent = -> Constraint015
FEATURE [Part::FeaturePython] _Element033  # link proxy (typed FeaturePython)
  Detach = false
  LinkTransform = true
  LinkedObject = -> Link002 [Body.Pocket006.Edge74]
  TreeRank = 704
  _LinkVersion = 1
  _Parent = -> Elements
FEATURE [Part::FeaturePython] _Element034  # link proxy (typed FeaturePython)
  Detach = false
  LinkTransform = true
  LinkedObject = -> LinkGroup045 [Solid045.Edge48]
  TreeRank = 707
  _LinkVersion = 1
  _Parent = -> Elements
FEATURE [Part::FeaturePython] _Element035  # link proxy (typed FeaturePython)
  Detach = false
  LinkTransform = true
  LinkedObject = -> Link002 [Body.Pocket006.Edge14]
  TreeRank = 709
  _LinkVersion = 1
  _Parent = -> Elements
FEATURE [App::FeaturePython] Constraint016  label="SameOrientation002"  # WARN: FeaturePython — macro-defined, semantics opaque (R4)
  Disabled = false
  Group = -> [ElementLink033,ElementLink034]
  TreeRank = 710
  _ConstraintType = 2
  _LinkVersion = 1
  _Parent = -> Constraints
FEATURE [App::FeaturePython] ElementLink033  label="_Element030"  # link proxy (typed FeaturePython)
  LinkTransform = true
  LinkedObject = -> _Element030
  TreeRank = 711
  _LinkVersion = 1
  _Parent = -> Constraint016
FEATURE [App::FeaturePython] ElementLink034  label="_Element023"  # link proxy (typed FeaturePython)
  LinkTransform = true
  LinkedObject = -> _Element023
  TreeRank = 712
  _LinkVersion = 1
  _Parent = -> Constraint016
FEATURE [App::FeaturePython] Constraint017  label="PlaneAlignment011"  # WARN: FeaturePython — macro-defined, semantics opaque (R4)
  Angle = 0
  AnglePitch = 0
  AngleRoll = 0
  Cascade = false
  Disabled = false
  Group = -> [ElementLink035,ElementLink036]
  LockAngle = false
  TreeRank = 714
  _ConstraintType = 37
  _LinkVersion = 1
  _Parent = -> Constraints
FEATURE [App::FeaturePython] ElementLink035  label="_Element036"  # link proxy (typed FeaturePython)
  LinkTransform = true
  LinkedObject = -> _Element036
  TreeRank = 715
  _LinkVersion = 1
  _Parent = -> Constraint017
FEATURE [Part::FeaturePython] _Element036  # link proxy (typed FeaturePython)
  Detach = false
  LinkTransform = true
  LinkedObject = -> Link212 [Body.Chamfer.Face63]
  TreeRank = 716
  _LinkVersion = 1
  _Parent = -> Elements
FEATURE [App::FeaturePython] ElementLink036  label="_Element037"  # link proxy (typed FeaturePython)
  LinkTransform = true
  LinkedObject = -> _Element037
  TreeRank = 717
  _LinkVersion = 1
  _Parent = -> Constraint017
FEATURE [Part::FeaturePython] _Element037  # link proxy (typed FeaturePython)
  Detach = false
  LinkTransform = true
  LinkedObject = -> Link [Body.Fillet.Face53]
  TreeRank = 718
  _LinkVersion = 1
  _Parent = -> Elements
FEATURE [App::FeaturePython] Constraint018  label="PlaneAlignment012"  # WARN: FeaturePython — macro-defined, semantics opaque (R4)
  Angle = 0
  AnglePitch = 0
  AngleRoll = 0
  Cascade = false
  Disabled = false
  Group = -> [ElementLink037,ElementLink038]
  LockAngle = false
  TreeRank = 719
  _ConstraintType = 37
  _LinkVersion = 1
  _Parent = -> Constraints
FEATURE [App::FeaturePython] ElementLink037  label="_Element038"  # link proxy (typed FeaturePython)
  LinkTransform = true
  LinkedObject = -> _Element038
  TreeRank = 720
  _LinkVersion = 1
  _Parent = -> Constraint018
FEATURE [Part::FeaturePython] _Element038  # link proxy (typed FeaturePython)
  Detach = false
  LinkTransform = true
  LinkedObject = -> Link212 [Body.Chamfer.Face72]
  TreeRank = 721
  _LinkVersion = 1
  _Parent = -> Elements
FEATURE [App::FeaturePython] ElementLink038  label="_Element029"  # link proxy (typed FeaturePython)
  LinkTransform = true
  LinkedObject = -> _Element029
  TreeRank = 722
  _LinkVersion = 1
  _Parent = -> Constraint018
FEATURE [App::FeaturePython] Constraint019  label="PlaneAlignment013"  # WARN: FeaturePython — macro-defined, semantics opaque (R4)
  Angle = 0
  AnglePitch = 0
  AngleRoll = 0
  Cascade = false
  Disabled = false
  Group = -> [ElementLink039,ElementLink040]
  LockAngle = false
  TreeRank = 723
  _ConstraintType = 37
  _LinkVersion = 1
  _Parent = -> Constraints
FEATURE [App::FeaturePython] ElementLink039  label="_Element039"  # link proxy (typed FeaturePython)
  LinkTransform = true
  LinkedObject = -> _Element039
  TreeRank = 724
  _LinkVersion = 1
  _Parent = -> Constraint019
FEATURE [Part::FeaturePython] _Element039  # link proxy (typed FeaturePython)
  Detach = false
  LinkTransform = true
  LinkedObject = -> Link212 [Body.Chamfer.Face13]
  TreeRank = 725
  _LinkVersion = 1
  _Parent = -> Elements
FEATURE [App::FeaturePython] ElementLink040  label="_Element040"  # link proxy (typed FeaturePython)
  LinkTransform = true
  LinkedObject = -> _Element040
  TreeRank = 726
  _LinkVersion = 1
  _Parent = -> Constraint019
FEATURE [Part::FeaturePython] _Element040  # link proxy (typed FeaturePython)
  Detach = false
  LinkTransform = true
  LinkedObject = -> Link [Body.Fillet.Face75]
  TreeRank = 727
  _LinkVersion = 1
  _Parent = -> Elements
FEATURE [App::FeaturePython] Constraint020  label="PlaneAlignment014"  # WARN: FeaturePython — macro-defined, semantics opaque (R4)
  Angle = 0
  AnglePitch = 0
  AngleRoll = 0
  Cascade = false
  Disabled = false
  Group = -> [ElementLink041,ElementLink042]
  LockAngle = false
  TreeRank = 729
  _ConstraintType = 37
  _LinkVersion = 1
  _Parent = -> Constraints
FEATURE [App::FeaturePython] ElementLink041  label="_Element041"  # link proxy (typed FeaturePython)
  LinkTransform = true
  LinkedObject = -> _Element041
  TreeRank = 730
  _LinkVersion = 1
  _Parent = -> Constraint020
FEATURE [Part::FeaturePython] _Element041  # link proxy (typed FeaturePython)
  Detach = false
  LinkTransform = true
  LinkedObject = -> Link213 [Body.Pocket002.Face44]
  TreeRank = 731
  _LinkVersion = 1
  _Parent = -> Elements
FEATURE [App::FeaturePython] ElementLink042  label="_Element042"  # link proxy (typed FeaturePython)
  LinkTransform = true
  LinkedObject = -> _Element042
  TreeRank = 732
  _LinkVersion = 1
  _Parent = -> Constraint020
FEATURE [Part::FeaturePython] _Element042  # link proxy (typed FeaturePython)
  Detach = false
  LinkTransform = true
  LinkedObject = -> Link001 [Body.Fillet.Face51]
  TreeRank = 733
  _LinkVersion = 1
  _Parent = -> Elements
FEATURE [App::FeaturePython] Constraint021  label="PlaneAlignment015"  # WARN: FeaturePython — macro-defined, semantics opaque (R4)
  Angle = 0
  AnglePitch = 0
  AngleRoll = 0
  Cascade = false
  Disabled = false
  Group = -> [ElementLink043,ElementLink044]
  LockAngle = false
  TreeRank = 734
  _ConstraintType = 37
  _LinkVersion = 1
  _Parent = -> Constraints
FEATURE [App::FeaturePython] ElementLink043  label="_Element043"  # link proxy (typed FeaturePython)
  LinkTransform = true
  LinkedObject = -> _Element043
  TreeRank = 735
  _LinkVersion = 1
  _Parent = -> Constraint021
FEATURE [Part::FeaturePython] _Element043  # link proxy (typed FeaturePython)
  Detach = false
  LinkTransform = true
  LinkedObject = -> Link213 [Body.Pocket002.Face25]
  TreeRank = 736
  _LinkVersion = 1
  _Parent = -> Elements
FEATURE [App::FeaturePython] ElementLink044  label="_Element044"  # link proxy (typed FeaturePython)
  LinkTransform = true
  LinkedObject = -> _Element044
  TreeRank = 737
  _LinkVersion = 1
  _Parent = -> Constraint021
FEATURE [Part::FeaturePython] _Element044  # link proxy (typed FeaturePython)
  Detach = false
  LinkTransform = true
  LinkedObject = -> Link001 [Body.Fillet.Face36]
  TreeRank = 738
  _LinkVersion = 1
  _Parent = -> Elements
FEATURE [App::FeaturePython] Constraint022  label="PlaneAlignment016"  # WARN: FeaturePython — macro-defined, semantics opaque (R4)
  Angle = 0
  AnglePitch = 0
  AngleRoll = 0
  Cascade = false
  Disabled = false
  Group = -> [ElementLink045,ElementLink046]
  LockAngle = false
  TreeRank = 739
  _ConstraintType = 37
  _LinkVersion = 1
  _Parent = -> Constraints
FEATURE [App::FeaturePython] ElementLink045  label="_Element045"  # link proxy (typed FeaturePython)
  LinkTransform = true
  LinkedObject = -> _Element045
  TreeRank = 740
  _LinkVersion = 1
  _Parent = -> Constraint022
FEATURE [Part::FeaturePython] _Element045  # link proxy (typed FeaturePython)
  Detach = false
  LinkTransform = true
  LinkedObject = -> Link001 [Body.Fillet.Face53]
  TreeRank = 741
  _LinkVersion = 1
  _Parent = -> Elements
FEATURE [App::FeaturePython] ElementLink046  label="_Element046"  # link proxy (typed FeaturePython)
  LinkTransform = true
  LinkedObject = -> _Element046
  TreeRank = 742
  _LinkVersion = 1
  _Parent = -> Constraint022
FEATURE [Part::FeaturePython] _Element046  # link proxy (typed FeaturePython)
  Detach = false
  LinkTransform = true
  LinkedObject = -> Link213 [Body.Pocket002.Face38]
  TreeRank = 743
  _LinkVersion = 1
  _Parent = -> Elements
FEATURE [App::FeaturePython] Constraint023  label="PlaneAlignment017"  # WARN: FeaturePython — macro-defined, semantics opaque (R4)
  Angle = 0
  AnglePitch = 0
  AngleRoll = 0
  Cascade = false
  Disabled = false
  Group = -> [ElementLink047,ElementLink048]
  LockAngle = false
  TreeRank = 745
  _ConstraintType = 37
  _LinkVersion = 1
  _Parent = -> Constraints
FEATURE [App::FeaturePython] ElementLink047  label="_Element047"  # link proxy (typed FeaturePython)
  LinkTransform = true
  LinkedObject = -> _Element047
  TreeRank = 746
  _LinkVersion = 1
  _Parent = -> Constraint023
FEATURE [Part::FeaturePython] _Element047  # link proxy (typed FeaturePython)
  Detach = false
  LinkTransform = true
  LinkedObject = -> Link214 [Body.Pocket001.Face43]
  TreeRank = 747
  _LinkVersion = 1
  _Parent = -> Elements
FEATURE [App::FeaturePython] ElementLink048  label="_Element048"  # link proxy (typed FeaturePython)
  LinkTransform = true
  LinkedObject = -> _Element048
  TreeRank = 748
  _LinkVersion = 1
  _Parent = -> Constraint023
FEATURE [Part::FeaturePython] _Element048  # link proxy (typed FeaturePython)
  Detach = false
  LinkTransform = true
  LinkedObject = -> Link003 [Body.Fillet.Face44]
  TreeRank = 749
  _LinkVersion = 1
  _Parent = -> Elements
FEATURE [App::FeaturePython] Constraint024  label="PlaneAlignment018"  # WARN: FeaturePython — macro-defined, semantics opaque (R4)
  Angle = 0
  AnglePitch = 0
  AngleRoll = 0
  Cascade = false
  Disabled = false
  Group = -> [ElementLink049,ElementLink050]
  LockAngle = false
  TreeRank = 750
  _ConstraintType = 37
  _LinkVersion = 1
  _Parent = -> Constraints
FEATURE [App::FeaturePython] ElementLink049  label="_Element049"  # link proxy (typed FeaturePython)
  LinkTransform = true
  LinkedObject = -> _Element049
  TreeRank = 751
  _LinkVersion = 1
  _Parent = -> Constraint024
FEATURE [Part::FeaturePython] _Element049  # link proxy (typed FeaturePython)
  Detach = false
  LinkTransform = true
  LinkedObject = -> Link214 [Body.Pocket001.Face30]
  TreeRank = 752
  _LinkVersion = 1
  _Parent = -> Elements
FEATURE [App::FeaturePython] ElementLink050  label="_Element050"  # link proxy (typed FeaturePython)
  LinkTransform = true
  LinkedObject = -> _Element050
  TreeRank = 753
  _LinkVersion = 1
  _Parent = -> Constraint024
FEATURE [Part::FeaturePython] _Element050  # link proxy (typed FeaturePython)
  Detach = false
  LinkTransform = true
  LinkedObject = -> Link002 [Body.Pocket006.Face50]
  TreeRank = 754
  _LinkVersion = 1
  _Parent = -> Elements
FEATURE [App::FeaturePython] Constraint025  label="PlaneAlignment019"  # WARN: FeaturePython — macro-defined, semantics opaque (R4)
  Angle = 0
  AnglePitch = 0
  AngleRoll = 0
  Cascade = false
  Disabled = false
  Group = -> [ElementLink051,ElementLink052]
  LockAngle = false
  TreeRank = 755
  _ConstraintType = 37
  _LinkVersion = 1
  _Parent = -> Constraints
FEATURE [App::FeaturePython] ElementLink051  label="_Element051"  # link proxy (typed FeaturePython)
  LinkTransform = true
  LinkedObject = -> _Element051
  TreeRank = 756
  _LinkVersion = 1
  _Parent = -> Constraint025
FEATURE [Part::FeaturePython] _Element051  # link proxy (typed FeaturePython)
  Detach = false
  LinkTransform = true
  LinkedObject = -> Link214 [Body.Pocket001.Face37]
  TreeRank = 757
  _LinkVersion = 1
  _Parent = -> Elements
FEATURE [App::FeaturePython] ElementLink052  label="_Element052"  # link proxy (typed FeaturePython)
  LinkTransform = true
  LinkedObject = -> _Element052
  TreeRank = 758
  _LinkVersion = 1
  _Parent = -> Constraint025
FEATURE [Part::FeaturePython] _Element052  # link proxy (typed FeaturePython)
  Detach = false
  LinkTransform = true
  LinkedObject = -> Link003 [Body.Fillet.Face55]
  TreeRank = 759
  _LinkVersion = 1
  _Parent = -> Elements
FEATURE [App::FeaturePython] Constraint026  label="PlaneAlignment020"  # WARN: FeaturePython — macro-defined, semantics opaque (R4)
  Angle = 0
  AnglePitch = 0
  AngleRoll = 0
  Cascade = false
  Disabled = false
  Group = -> [ElementLink053,ElementLink054]
  LockAngle = false
  TreeRank = 761
  _ConstraintType = 37
  _LinkVersion = 1
  _Parent = -> Constraints
FEATURE [App::FeaturePython] ElementLink053  label="_Element053"  # link proxy (typed FeaturePython)
  LinkTransform = true
  LinkedObject = -> _Element053
  TreeRank = 762
  _LinkVersion = 1
  _Parent = -> Constraint026
FEATURE [Part::FeaturePython] _Element053  # link proxy (typed FeaturePython)
  Detach = false
  LinkTransform = true
  LinkedObject = -> Link215 [Body.Pad009.Face46]
  TreeRank = 763
  _LinkVersion = 1
  _Parent = -> Elements
FEATURE [App::FeaturePython] ElementLink054  label="_Element054"  # link proxy (typed FeaturePython)
  LinkTransform = true
  LinkedObject = -> _Element054
  TreeRank = 764
  _LinkVersion = 1
  _Parent = -> Constraint026
FEATURE [Part::FeaturePython] _Element054  # link proxy (typed FeaturePython)
  Detach = false
  LinkTransform = true
  LinkedObject = -> Link002 [Body.PolarPattern.Face52]
  TreeRank = 765
  _LinkVersion = 1
  _Parent = -> Elements
FEATURE [App::FeaturePython] Constraint027  label="PlaneAlignment021"  # WARN: FeaturePython — macro-defined, semantics opaque (R4)
  Angle = 0
  AnglePitch = 0
  AngleRoll = 0
  Cascade = false
  Disabled = false
  Group = -> [ElementLink055,ElementLink056]
  LockAngle = false
  TreeRank = 766
  _ConstraintType = 37
  _LinkVersion = 1
  _Parent = -> Constraints
FEATURE [App::FeaturePython] ElementLink055  label="_Element055"  # link proxy (typed FeaturePython)
  LinkTransform = true
  LinkedObject = -> _Element055
  TreeRank = 767
  _LinkVersion = 1
  _Parent = -> Constraint027
FEATURE [Part::FeaturePython] _Element055  # link proxy (typed FeaturePython)
  Detach = false
  LinkTransform = true
  LinkedObject = -> Link215 [Body.Pad009.Face30]
  TreeRank = 768
  _LinkVersion = 1
  _Parent = -> Elements
FEATURE [App::FeaturePython] ElementLink056  label="_Element056"  # link proxy (typed FeaturePython)
  LinkTransform = true
  LinkedObject = -> _Element056
  TreeRank = 769
  _LinkVersion = 1
  _Parent = -> Constraint027
FEATURE [Part::FeaturePython] _Element056  # link proxy (typed FeaturePython)
  Detach = false
  LinkTransform = true
  LinkedObject = -> Link002 [Body.PolarPattern.Face50]
  TreeRank = 770
  _LinkVersion = 1
  _Parent = -> Elements
FEATURE [App::FeaturePython] Constraint028  label="PlaneAlignment022"  # WARN: FeaturePython — macro-defined, semantics opaque (R4)
  Angle = 0
  AnglePitch = 0
  AngleRoll = 0
  Cascade = false
  Disabled = false
  Group = -> [ElementLink057,ElementLink058]
  LockAngle = false
  TreeRank = 771
  _ConstraintType = 37
  _LinkVersion = 1
  _Parent = -> Constraints
FEATURE [App::FeaturePython] ElementLink057  label="_Element057"  # link proxy (typed FeaturePython)
  LinkTransform = true
  LinkedObject = -> _Element057
  TreeRank = 772
  _LinkVersion = 1
  _Parent = -> Constraint028
FEATURE [Part::FeaturePython] _Element057  # link proxy (typed FeaturePython)
  Detach = false
  LinkTransform = true
  LinkedObject = -> Link215 [Body.Pad009.Face44]
  TreeRank = 773
  _LinkVersion = 1
  _Parent = -> Elements
FEATURE [App::FeaturePython] ElementLink058  label="_Element058"  # link proxy (typed FeaturePython)
  LinkTransform = true
  LinkedObject = -> _Element058
  TreeRank = 774
  _LinkVersion = 1
  _Parent = -> Constraint028
FEATURE [Part::FeaturePython] _Element058  # link proxy (typed FeaturePython)
  Detach = false
  LinkTransform = true
  LinkedObject = -> Link002 [Body.PolarPattern.Face49]
  TreeRank = 775
  _LinkVersion = 1
  _Parent = -> Elements

RESOLVED EXTERNAL PARTS (link-assembly join: the EXTERNAL_REF files above that resolve inside this repo's crawl, each included once):
---- part FirstPartPeripherals.FCStd = doc fcstd_c1a7728164f3 ----
FCSTD DOCUMENT  (FreeCAD 2022.1112R26244 +5306 (Git))
Label: FirstPartPeripherals
License: All rights reserved
LicenseURL: http://en.wikipedia.org/wiki/All_rights_reserved
objects: Sketcher::SketchObject×14, PartDesign::Pad×9, PartDesign::Pocket×5, PartDesign::CoordinateSystem×1, PartDesign::Fillet×1, PartDesign::Chamfer×1, PartDesign::Body×1, App::Part×1
note: 78 computed .brp shape members not serialized (recipe doc carries the construction recipe); baked Part::Feature solids carry a one-line shape summary decoded from their .brp

FEATURE [PartDesign::CoordinateSystem] LCS_0
  AttacherType = Attacher::AttachEngine3D
  AttachmentSupport = -> [X_Axis001]
  MapMode = 2
  Support = -> [X_Axis001]
  TreeRank = 0
FEATURE [Sketcher::SketchObject] Sketch_1
  ArcFitTolerance = 0
  ExternalBSplineMaxDegree = 0
  ExternalBSplineTolerance = 0
  FullyConstrained = true
  InternalTolerance = 1e-06
  MakeInternals = false
  TreeRank = 0
  sketch-geometry (4):
    g0: LineSegment StartX=0 StartY=0 StartZ=0 EndX=-140 EndY=0 EndZ=0
    g1: LineSegment StartX=-140 StartY=0 StartZ=0 EndX=-140 EndY=116 EndZ=0
    g2: LineSegment StartX=-140 StartY=116 StartZ=0 EndX=0 EndY=116 EndZ=0
    g3: LineSegment StartX=0 StartY=116 StartZ=0 EndX=0 EndY=0 EndZ=0
  constraints (11):
    c: Coincident(g0,g1)
    c: Coincident(g1,g2)
    c: Coincident(g2,g3)
    c: Coincident(g3,g0)
    c: Horizontal(g0)
    c: Horizontal(g2)
    c: Vertical(g1)
    c: Vertical(g3)
    c: Coincident(g0,g-1)
    c: DistanceY(g3,g3) = 116
    c: DistanceX(g2,g2) = 140
FEATURE [PartDesign::Pad] Pad  label="MainSupport"
  AddSubType = 0
  AutoTaperInnerAngle = false
  CheckUpToFaceLimits = true
  ClaimChildren = false
  Direction = (0,0,1)
  Fit = 0
  FitJoin = 0
  InnerFit = 0
  InnerFitJoin = 0
  Length = 5
  Length2 = 100
  NewSolid = false
  Profile = -> Sketch_1
  Suppress = false
  TaperInnerAngle = 0
  TaperInnerAngleRev = 0
  TreeRank = 0
  Type = 0
  _ProfileBasedVersion = 0
FEATURE [Sketcher::SketchObject] Sketch
  ArcFitTolerance = 0
  AttachmentSupport = -> [XY_Plane001]
  ExternalBSplineMaxDegree = 0
  ExternalBSplineTolerance = 0
  ExternalGeometry = -> [Pad]
  FullyConstrained = true
  InternalTolerance = 1e-06
  MakeInternals = false
  MapMode = 5
  Support = -> [XY_Plane001]
  TreeRank = 0
  sketch-geometry (4):
    g0: LineSegment StartX=0 StartY=0 StartZ=0 EndX=-140 EndY=0 EndZ=0
    g1: LineSegment StartX=-140 StartY=0 StartZ=0 EndX=-140 EndY=-15 EndZ=0
    g2: LineSegment StartX=-140 StartY=-15 StartZ=0 EndX=0 EndY=-15 EndZ=0
    g3: LineSegment StartX=0 StartY=-15 StartZ=0 EndX=0 EndY=0 EndZ=0
  constraints (10):
    c: Coincident(g0,g1)
    c: Coincident(g1,g2)
    c: Coincident(g2,g3)
    c: Coincident(g3,g0)
    c: Horizontal(g2)
    c: Vertical(g1)
    c: Vertical(g3)
    c: Coincident(g0,g-1)
    c: Coincident(g0,g-3)
    c: DistanceY(g3,g3) = 15
FEATURE [PartDesign::Pad] Pad001  label="ExtraPeripheralsSize"
  AddSubType = 0
  AutoTaperInnerAngle = false
  BaseFeature = -> Pad
  CheckUpToFaceLimits = true
  ClaimChildren = false
  Direction = (0,0,1)
  Fit = 0
  FitJoin = 0
  InnerFit = 0
  InnerFitJoin = 0
  Length = 5
  Length2 = 100
  NewSolid = false
  Profile = -> Sketch
  Suppress = false
  TaperInnerAngle = 0
  TaperInnerAngleRev = 0
  TreeRank = 0
  Type = 0
  _ProfileBasedVersion = 0
FEATURE [Sketcher::SketchObject] Sketch001
  ArcFitTolerance = 0
  AttachmentSupport = -> [Pad001]
  ExternalBSplineMaxDegree = 0
  ExternalBSplineTolerance = 0
  ExternalGeometry = -> [Pad001]
  FullyConstrained = true
  InternalTolerance = 1e-06
  MakeInternals = false
  MapMode = 5
  Placement = pos=(0,0,5) rot=(0,0,1;0rad)
  Support = -> [Pad001]
  TreeRank = 0
  sketch-geometry (4):
    g0: LineSegment StartX=0 StartY=-15 StartZ=0 EndX=-107 EndY=-15 EndZ=0
    g1: LineSegment StartX=-107 StartY=-15 StartZ=0 EndX=-107 EndY=-13 EndZ=0
    g2: LineSegment StartX=-107 StartY=-13 StartZ=0 EndX=0 EndY=-13 EndZ=0
    g3: LineSegment StartX=0 StartY=-13 StartZ=0 EndX=0 EndY=-15 EndZ=0
  constraints (11):
    c: Coincident(g0,g1)
    c: Coincident(g1,g2)
    c: Coincident(g2,g3)
    c: Coincident(g3,g0)
    c: Horizontal(g2)
    c: Vertical(g1)
    c: Vertical(g3)
    c: Coincident(g0,g-3)
    c: DistanceY(g3,g3) = 2
    c: DistanceX(g0,g0) = 107
    c: Horizontal(g0)
FEATURE [PartDesign::Pad] Pad002  label="PeripheralPanel"
  AddSubType = 0
  AutoTaperInnerAngle = false
  BaseFeature = -> Pad001
  CheckUpToFaceLimits = true
  ClaimChildren = false
  Direction = (0,0,1)
  Fit = 0
  FitJoin = 0
  InnerFit = 0
  InnerFitJoin = 0
  Length = 51
  Length2 = 100
  NewSolid = false
  Profile = -> Sketch001
  Suppress = false
  TaperInnerAngle = 0
  TaperInnerAngleRev = 0
  TreeRank = 0
  Type = 0
  _ProfileBasedVersion = 0
FEATURE [Sketcher::SketchObject] Sketch002
  ArcFitTolerance = 0
  AttachmentSupport = -> [Pad002]
  ExternalBSplineMaxDegree = 0
  ExternalBSplineTolerance = 0
  ExternalGeometry = -> [Pad002]
  FullyConstrained = true
  InternalTolerance = 1e-06
  MakeInternals = false
  MapMode = 5
  Placement = pos=(0,-15,0) rot=(1,0,0;1.5708rad)
  Support = -> [Pad002]
  TreeRank = 0
  sketch-geometry (20):
    g0: LineSegment [constr] StartX=0 StartY=5 StartZ=0 EndX=-107 EndY=5 EndZ=0
    g1: LineSegment [constr] StartX=-107 StartY=5 StartZ=0 EndX=-107 EndY=35 EndZ=0
    g2: LineSegment [constr] StartX=-107 StartY=35 StartZ=0 EndX=0 EndY=35 EndZ=0
    g3: LineSegment [constr] StartX=0 StartY=35 StartZ=0 EndX=0 EndY=5 EndZ=0
    g4: LineSegment StartX=-16 StartY=35 StartZ=0 EndX=-31 EndY=35 EndZ=0
    g5: LineSegment StartX=-31 StartY=35 StartZ=0 EndX=-31 EndY=76 EndZ=0
    g6: LineSegment StartX=-31 StartY=76 StartZ=0 EndX=-16 EndY=76 EndZ=0
    g7: LineSegment StartX=-16 StartY=76 StartZ=0 EndX=-16 EndY=35 EndZ=0
    g8: LineSegment StartX=-36 StartY=35 StartZ=0 EndX=-51 EndY=35 EndZ=0
    g9: LineSegment StartX=-51 StartY=35 StartZ=0 EndX=-51 EndY=76 EndZ=0
    g10: LineSegment StartX=-51 StartY=76 StartZ=0 EndX=-36 EndY=76 EndZ=0
    g11: LineSegment StartX=-36 StartY=76 StartZ=0 EndX=-36 EndY=35 EndZ=0
    g12: LineSegment StartX=-56 StartY=35 StartZ=0 EndX=-71 EndY=35 EndZ=0
    g13: LineSegment StartX=-71 StartY=35 StartZ=0 EndX=-71 EndY=76 EndZ=0
    g14: LineSegment StartX=-71 StartY=76 StartZ=0 EndX=-56 EndY=76 EndZ=0
    g15: LineSegment StartX=-56 StartY=76 StartZ=0 EndX=-56 EndY=35 EndZ=0
    g16: LineSegment StartX=-76 StartY=35 StartZ=0 EndX=-91 EndY=35 EndZ=0
    g17: LineSegment StartX=-91 StartY=35 StartZ=0 EndX=-91 EndY=76 EndZ=0
    g18: LineSegment StartX=-91 StartY=76 StartZ=0 EndX=-76 EndY=76 EndZ=0
    g19: LineSegment StartX=-76 StartY=76 StartZ=0 EndX=-76 EndY=35 EndZ=0
  constraints (58):
    c: Coincident(g0,g1)
    c: Coincident(g1,g2)
    c: Coincident(g2,g3)
    c: Coincident(g3,g0)
    c: Horizontal(g2)
    c: Vertical(g1)
    c: Vertical(g3)
    c: Coincident(g0,g-3)
    c: Coincident(g0,g-3)
    c: DistanceY(g3,g3) = 30
    c: Coincident(g4,g5)
    c: Coincident(g5,g6)
    c: Coincident(g6,g7)
    c: Coincident(g7,g4)
    c: Horizontal(g4)
    c: Horizontal(g6)
    c: Vertical(g5)
    c: Vertical(g7)
    c: PointOnObject(g4,g2)
    c: DistanceX(g4,g2) = 16
    c: DistanceX(g4,g4) = 15
    c: DistanceY(g5,g5) = 41
    c: Coincident(g8,g9)
    c: Coincident(g9,g10)
    c: Coincident(g10,g11)
    c: Coincident(g11,g8)
    c: Horizontal(g8)
    c: Horizontal(g10)
    c: Vertical(g9)
    c: Vertical(g11)
    c: PointOnObject(g8,g2)
    c: Coincident(g12,g13)
    c: Coincident(g13,g14)
    c: Coincident(g14,g15)
    c: Coincident(g15,g12)
    c: Horizontal(g12)
    c: Horizontal(g14)
    c: Vertical(g13)
    c: Vertical(g15)
    c: PointOnObject(g12,g2)
    c: Coincident(g16,g17)
    c: Coincident(g17,g18)
    c: Coincident(g18,g19)
    c: Coincident(g19,g16)
    c: Horizontal(g16)
    c: Horizontal(g18)
    c: Vertical(g17)
    c: Vertical(g19)
    c: PointOnObject(g16,g2)
    c: DistanceX(g8,g4) = 5
    c: Equal(g4,g8)
    c: Equal(g5,g11)
    c: DistanceX(g12,g8) = 5
    c: Equal(g12,g8)
    c: Equal(g15,g9)
    c: DistanceX(g16,g12) = 5
    c: Equal(g16,g12)
    c: Equal(g19,g13)
FEATURE [PartDesign::Pocket] Pocket  label="PeripheralHoles"
  AddSubType = 1
  AutoTaperInnerAngle = false
  BaseFeature = -> Pad002
  CheckUpToFaceLimits = true
  ClaimChildren = false
  Fit = 0
  FitJoin = 0
  InnerFit = 0
  InnerFitJoin = 0
  Length = 0
  Length2 = 100
  NewSolid = false
  Profile = -> Sketch002
  Suppress = false
  TaperInnerAngle = 0
  TaperInnerAngleRev = 0
  TreeRank = 0
  Type = 2
  _ProfileBasedVersion = 0
  _Version = 0
FEATURE [Sketcher::SketchObject] Sketch003
  ArcFitTolerance = 0
  AttachmentSupport = -> [XY_Plane001]
  ExternalBSplineMaxDegree = 0
  ExternalBSplineTolerance = 0
  ExternalGeometry = -> [Pocket]
  FullyConstrained = true
  InternalTolerance = 1e-06
  MakeInternals = false
  MapMode = 5
  Support = -> [XY_Plane001]
  TreeRank = 0
  sketch-geometry (4):
    g0: LineSegment StartX=0 StartY=-15 StartZ=0 EndX=5 EndY=-15 EndZ=0
    g1: LineSegment StartX=5 StartY=-15 StartZ=0 EndX=5 EndY=116 EndZ=0
    g2: LineSegment StartX=5 StartY=116 StartZ=0 EndX=0 EndY=116 EndZ=0
    g3: LineSegment StartX=0 StartY=116 StartZ=0 EndX=0 EndY=-15 EndZ=0
  constraints (10):
    c: Coincident(g0,g1)
    c: Coincident(g1,g2)
    c: Coincident(g2,g3)
    c: Coincident(g3,g0)
    c: Horizontal(g0)
    c: Horizontal(g2)
    c: Vertical(g1)
    c: Coincident(g0,g-3)
    c: Coincident(g2,g-4)
    c: DistanceX(g0,g0) = 5
FEATURE [PartDesign::Pad] Pad003  label="ExtraSideSize"
  AddSubType = 0
  AutoTaperInnerAngle = false
  BaseFeature = -> Pocket
  CheckUpToFaceLimits = true
  ClaimChildren = false
  Direction = (0,0,1)
  Fit = 0
  FitJoin = 0
  InnerFit = 0
  InnerFitJoin = 0
  Length = 5
  Length2 = 100
  NewSolid = false
  Profile = -> Sketch003
  Suppress = false
  TaperInnerAngle = 0
  TaperInnerAngleRev = 0
  TreeRank = 0
  Type = 0
  _ProfileBasedVersion = 0
FEATURE [Sketcher::SketchObject] Sketch004
  ArcFitTolerance = 0
  AttachmentSupport = -> [Pad003]
  ExternalBSplineMaxDegree = 0
  ExternalBSplineTolerance = 0
  ExternalGeometry = -> [Pad003]
  FullyConstrained = true
  InternalTolerance = 1e-06
  MakeInternals = false
  MapMode = 5
  Placement = pos=(0,0,5) rot=(0,0,1;0rad)
  Support = -> [Pad003]
  TreeRank = 0
  sketch-geometry (6):
    g0: LineSegment StartX=5 StartY=116 StartZ=0 EndX=3 EndY=116 EndZ=0
    g1: LineSegment StartX=5 StartY=-15 StartZ=0 EndX=5 EndY=116 EndZ=0
    g2: LineSegment StartX=0 StartY=-13 StartZ=0 EndX=3 EndY=-13 EndZ=0
    g3: LineSegment StartX=5 StartY=-15 StartZ=0 EndX=0 EndY=-15 EndZ=0
    g4: LineSegment StartX=0 StartY=-15 StartZ=0 EndX=0 EndY=-13 EndZ=0
    g5: LineSegment StartX=3 StartY=-13 StartZ=0 EndX=3 EndY=116 EndZ=0
  constraints (15):
    c: Coincident(g1,g0)
    c: Horizontal(g0)
    c: Coincident(g0,g-3)
    c: DistanceX(g0,g0) = 2
    c: Coincident(g3,g4)
    c: Coincident(g4,g2)
    c: Horizontal(g2)
    c: Horizontal(g3)
    c: Vertical(g4)
    c: Coincident(g2,g-4)
    c: Coincident(g5,g2)
    c: Coincident(g5,g0)
    c: Vertical(g5)
    c: Coincident(g3,g1)
    c: Coincident(g1,g-3)
FEATURE [PartDesign::Pad] Pad004  label="SidePanel"
  AddSubType = 0
  AutoTaperInnerAngle = false
  BaseFeature = -> Pad003
  CheckUpToFaceLimits = true
  ClaimChildren = false
  Direction = (0,0,1)
  Fit = 0
  FitJoin = 0
  InnerFit = 0
  InnerFitJoin = 0
  Length = 51
  Length2 = 100
  NewSolid = false
  Profile = -> Sketch004
  Suppress = false
  TaperInnerAngle = 0
  TaperInnerAngleRev = 0
  TreeRank = 0
  Type = 0
  _ProfileBasedVersion = 0
FEATURE [Sketcher::SketchObject] Sketch005
  ArcFitTolerance = 0
  AttachmentSupport = -> [Pad004]
  ExternalBSplineMaxDegree = 0
  ExternalBSplineTolerance = 0
  ExternalGeometry = -> [Pad004]
  FullyConstrained = true
  InternalTolerance = 1e-06
  MakeInternals = false
  MapMode = 5
  Placement = pos=(0,0,5) rot=(0,0,1;0rad)
  Support = -> [Pad004]
  TreeRank = 0
  sketch-geometry (4):
    g0: LineSegment StartX=-140 StartY=-13 StartZ=0 EndX=-107 EndY=-13 EndZ=0
    g1: LineSegment StartX=-107 StartY=-13 StartZ=0 EndX=-107 EndY=-15 EndZ=0
    g2: LineSegment StartX=-107 StartY=-15 StartZ=0 EndX=-140 EndY=-15 EndZ=0
    g3: LineSegment StartX=-140 StartY=-15 StartZ=0 EndX=-140 EndY=-13 EndZ=0
  constraints (10):
    c: Coincident(g0,g1)
    c: Coincident(g1,g2)
    c: Coincident(g2,g3)
    c: Coincident(g3,g0)
    c: Horizontal(g0)
    c: Horizontal(g2)
    c: Vertical(g1)
    c: Vertical(g3)
    c: Coincident(g2,g-4)
    c: Coincident(g0,g-3)
FEATURE [PartDesign::Pad] Pad005  label="EndPeripheralPanel"
  AddSubType = 0
  AutoTaperInnerAngle = false
  BaseFeature = -> Pad004
  CheckUpToFaceLimits = true
  ClaimChildren = false
  Direction = (0,0,1)
  Fit = 0
  FitJoin = 0
  InnerFit = 0
  InnerFitJoin = 0
  Length = 51
  Length2 = 100
  NewSolid = false
  Profile = -> Sketch005
  Suppress = false
  TaperInnerAngle = 0
  TaperInnerAngleRev = 0
  TreeRank = 0
  Type = 0
  _ProfileBasedVersion = 0
FEATURE [Sketcher::SketchObject] Sketch006
  ArcFitTolerance = 0
  AttachmentSupport = -> [Pad005]
  ExternalBSplineMaxDegree = 0
  ExternalBSplineTolerance = 0
  ExternalGeometry = -> [Pad005]
  FullyConstrained = true
  InternalTolerance = 1e-06
  MakeInternals = false
  MapMode = 5
  Placement = pos=(0,0,5) rot=(0,0,1;0rad)
  Support = -> [Pad005]
  TreeRank = 0
  sketch-geometry (2):
    g0: Circle CenterX=-5 CenterY=5 CenterZ=0 NormalX=0 NormalY=0 NormalZ=1 AngleXU=0 Radius=3.6
    g1: Circle CenterX=-5 CenterY=111 CenterZ=0 NormalX=0 NormalY=0 NormalZ=1 AngleXU=0 Radius=3.6
  constraints (6):
    c: DistanceX(g0,g-1) = 5
    c: DistanceY(g-1,g0) = 5
    c: Diameter(g0) = 7.2
    c: DistanceY(g1,g-3) = 5
    c: DistanceX(g1,g-3) = 5
    c: Diameter(g1) = 7.2
FEATURE [PartDesign::Pad] Pad006  label="MotherboardColumn"
  AddSubType = 0
  AutoTaperInnerAngle = false
  BaseFeature = -> Pad005
  CheckUpToFaceLimits = true
  ClaimChildren = false
  Direction = (0,0,1)
  Fit = 0
  FitJoin = 0
  InnerFit = 0
  InnerFitJoin = 0
  Length = 12.4
  Length2 = 100
  NewSolid = false
  Profile = -> Sketch006
  Suppress = false
  TaperInnerAngle = 0
  TaperInnerAngleRev = 0
  TreeRank = 0
  Type = 0
  _ProfileBasedVersion = 0
FEATURE [Sketcher::SketchObject] Sketch007
  ArcFitTolerance = 0
  AttachmentSupport = -> [Pad006]
  ExternalBSplineMaxDegree = 0
  ExternalBSplineTolerance = 0
  ExternalGeometry = -> [Pad006]
  FullyConstrained = true
  InternalTolerance = 1e-06
  MakeInternals = false
  MapMode = 5
  Placement = pos=(0,0,17.4) rot=(0,0,1;0rad)
  Support = -> [Pad006]
  TreeRank = 0
  sketch-geometry (2):
    g0: Circle CenterX=-5 CenterY=5 CenterZ=0 NormalX=0 NormalY=0 NormalZ=1 AngleXU=0 Radius=2
    g1: Circle CenterX=-5 CenterY=111 CenterZ=0 NormalX=0 NormalY=0 NormalZ=1 AngleXU=0 Radius=2
  constraints (4):
    c: Coincident(g0,g-3)
    c: Diameter(g0) = 4
    c: Coincident(g1,g-4)
    c: Diameter(g1) = 4
FEATURE [PartDesign::Pocket] Pocket001  label="ColumnInsertHole"
  AddSubType = 1
  AutoTaperInnerAngle = false
  BaseFeature = -> Pad006
  CheckUpToFaceLimits = true
  ClaimChildren = false
  Fit = 0
  FitJoin = 0
  InnerFit = 0
  InnerFitJoin = 0
  Length = 6.7
  Length2 = 100
  NewSolid = false
  Profile = -> Sketch007
  Suppress = false
  TaperInnerAngle = 0
  TaperInnerAngleRev = 0
  TreeRank = 0
  Type = 0
  _ProfileBasedVersion = 0
  _Version = 0
FEATURE [Sketcher::SketchObject] Sketch008
  ArcFitTolerance = 0
  AttachmentSupport = -> [Pocket001]
  ExternalBSplineMaxDegree = 0
  ExternalBSplineTolerance = 0
  ExternalGeometry = -> [Pocket001]
  FullyConstrained = true
  InternalTolerance = 1e-06
  MakeInternals = false
  MapMode = 5
  Placement = pos=(0,116,0) rot=(0,0.707107,0.707107;3.14159rad)
  Support = -> [Pocket001]
  TreeRank = 0
  sketch-geometry (4):
    g0: LineSegment StartX=-3.05 StartY=3.5 StartZ=0 EndX=119.05 EndY=3.5 EndZ=0
    g1: LineSegment StartX=119.05 StartY=3.5 StartZ=0 EndX=119.05 EndY=1.42 EndZ=0
    g2: LineSegment StartX=119.05 StartY=1.42 StartZ=0 EndX=-3.05 EndY=1.42 EndZ=0
    g3: LineSegment StartX=-3.05 StartY=1.42 StartZ=0 EndX=-3.05 EndY=3.5 EndZ=0
  constraints (12):
    c: Coincident(g0,g1)
    c: Coincident(g1,g2)
    c: Coincident(g2,g3)
    c: Coincident(g3,g0)
    c: Horizontal(g0)
    c: Horizontal(g2)
    c: Vertical(g1)
    c: Vertical(g3)
    c: DistanceX(g-4,g0) = 1.95
    c: DistanceY(g3,g3) = 2.08
    c: DistanceY(g0,g-4) = 1.5
    c: DistanceX(g0,g-3) = 20.95
FEATURE [PartDesign::Pocket] Pocket002  label="PuzzleHole1"
  AddSubType = 1
  AutoTaperInnerAngle = false
  BaseFeature = -> Pocket001
  CheckUpToFaceLimits = true
  ClaimChildren = false
  Fit = 0
  FitJoin = 0
  InnerFit = 0
  InnerFitJoin = 0
  Length = 11
  Length2 = 100
  NewSolid = false
  Profile = -> Sketch008
  Suppress = false
  TaperInnerAngle = 0
  TaperInnerAngleRev = 0
  TreeRank = 0
  Type = 0
  _ProfileBasedVersion = 0
  _Version = 0
FEATURE [Sketcher::SketchObject] Sketch009
  ArcFitTolerance = 0
  AttachmentSupport = -> [Pocket002]
  ExternalBSplineMaxDegree = 0
  ExternalBSplineTolerance = 0
  ExternalGeometry = -> [Pocket002]
  FullyConstrained = true
  InternalTolerance = 1e-06
  MakeInternals = false
  MapMode = 5
  Placement = pos=(-140,0,0) rot=(0.57735,-0.57735,-0.57735;2.0944rad)
  Support = -> [Pocket002]
  TreeRank = 0
  sketch-geometry (4):
    g0: LineSegment StartX=-95.05 StartY=3.5 StartZ=0 EndX=13.05 EndY=3.5 EndZ=0
    g1: LineSegment StartX=13.05 StartY=3.5 StartZ=0 EndX=13.05 EndY=1.42 EndZ=0
    g2: LineSegment StartX=13.05 StartY=1.42 StartZ=0 EndX=-95.05 EndY=1.42 EndZ=0
    g3: LineSegment StartX=-95.05 StartY=1.42 StartZ=0 EndX=-95.05 EndY=3.5 EndZ=0
  constraints (12):
    c: Coincident(g0,g1)
    c: Coincident(g1,g2)
    c: Coincident(g2,g3)
    c: Coincident(g3,g0)
    c: Horizontal(g0)
    c: Horizontal(g2)
    c: Vertical(g1)
    c: Vertical(g3)
    c: DistanceX(g-3,g0) = 20.95
    c: DistanceY(g1,g1) = 2.08
    c: DistanceY(g0,g-4) = 1.5
    c: DistanceX(g0,g-4) = 1.95
FEATURE [PartDesign::Pocket] Pocket003  label="PuzzleHole2"
  AddSubType = 1
  AutoTaperInnerAngle = false
  BaseFeature = -> Pocket002
  CheckUpToFaceLimits = true
  ClaimChildren = false
  Fit = 0
  FitJoin = 0
  InnerFit = 0
  InnerFitJoin = 0
  Length = 11
  Length2 = 100
  NewSolid = false
  Profile = -> Sketch009
  Suppress = false
  TaperInnerAngle = 0
  TaperInnerAngleRev = 0
  TreeRank = 0
  Type = 0
  _ProfileBasedVersion = 0
  _Version = 0
FEATURE [Sketcher::SketchObject] Sketch010
  ArcFitTolerance = 0
  AttachmentSupport = -> [Pocket003]
  ExternalBSplineMaxDegree = 0
  ExternalBSplineTolerance = 0
  ExternalGeometry = -> [Pocket003]
  FullyConstrained = true
  InternalTolerance = 1e-06
  MakeInternals = false
  MapMode = 5
  Placement = pos=(0,0,5) rot=(0,0,1;0rad)
  Support = -> [Pocket003]
  TreeRank = 0
  sketch-geometry (4):
    g0: LineSegment StartX=-4.2 StartY=-13 StartZ=0 EndX=3 EndY=-13 EndZ=0
    g1: LineSegment StartX=3 StartY=-13 StartZ=0 EndX=3 EndY=-5.8 EndZ=0
    g2: LineSegment StartX=3 StartY=-5.8 StartZ=0 EndX=-4.2 EndY=-5.8 EndZ=0
    g3: LineSegment StartX=-4.2 StartY=-5.8 StartZ=0 EndX=-4.2 EndY=-13 EndZ=0
  constraints (11):
    c: Coincident(g0,g1)
    c: Coincident(g1,g2)
    c: Coincident(g2,g3)
    c: Coincident(g3,g0)
    c: Horizontal(g0)
    c: Horizontal(g2)
    c: Vertical(g1)
    c: Vertical(g3)
    c: Coincident(g0,g-4)
    c: Equal(g2,g3)
    c: DistanceX(g2,g2) = 7.2
FEATURE [PartDesign::Pad] Pad007  label="ColumnPart"
  AddSubType = 0
  AutoTaperInnerAngle = false
  BaseFeature = -> Pocket003
  CheckUpToFaceLimits = true
  ClaimChildren = false
  Direction = (0,0,1)
  Fit = 0
  FitJoin = 0
  InnerFit = 0
  InnerFitJoin = 0
  Length = 10
  Length2 = 100
  NewSolid = false
  Profile = -> Sketch010
  Suppress = false
  TaperInnerAngle = 0
  TaperInnerAngleRev = 0
  TreeRank = 0
  Type = 3
  UpToFace = -> Pocket003 [Face39]
  _ProfileBasedVersion = 0
FEATURE [Sketcher::SketchObject] Sketch011
  ArcFitTolerance = 0
  AttachmentSupport = -> [Pad007]
  ExternalBSplineMaxDegree = 0
  ExternalBSplineTolerance = 0
  ExternalGeometry = -> [Pad007]
  FullyConstrained = true
  InternalTolerance = 1e-06
  MakeInternals = false
  MapMode = 5
  Placement = pos=(0,0,56) rot=(0,0,1;0rad)
  Support = -> [Pad007]
  TreeRank = 0
  sketch-geometry (3):
    g0: Circle CenterX=-0.6 CenterY=-9.4 CenterZ=0 NormalX=0 NormalY=0 NormalZ=1 AngleXU=0 Radius=2
    g1: LineSegment [constr] StartX=-0.6 StartY=-5.8 StartZ=0 EndX=-0.6 EndY=-9.4 EndZ=0
    g2: LineSegment [constr] StartX=-0.6 StartY=-9.4 StartZ=0 EndX=-4.2 EndY=-9.4 EndZ=0
  constraints (8):
    c: Vertical(g1)
    c: Coincident(g2,g1)
    c: PointOnObject(g2,g-4)
    c: Horizontal(g2)
    c: Equal(g1,g2)
    c: Symmetric(g-3,g-4,g1)
    c: Coincident(g0,g1)
    c: Diameter(g0) = 4
FEATURE [PartDesign::Pocket] Pocket004  label="ColumnPartHole"
  AddSubType = 1
  AutoTaperInnerAngle = false
  BaseFeature = -> Pad007
  CheckUpToFaceLimits = true
  ClaimChildren = false
  Fit = 0
  FitJoin = 0
  InnerFit = 0
  InnerFitJoin = 0
  Length = 6.7
  Length2 = 100
  NewSolid = false
  Profile = -> Sketch011
  Suppress = false
  TaperInnerAngle = 0
  TaperInnerAngleRev = 0
  TreeRank = 0
  Type = 0
  _ProfileBasedVersion = 0
  _Version = 0
FEATURE [Sketcher::SketchObject] Sketch012
  ArcFitTolerance = 0
  AttachmentSupport = -> [Pocket004]
  ExternalBSplineMaxDegree = 0
  ExternalBSplineTolerance = 0
  ExternalGeometry = -> [Pocket004]
  FullyConstrained = true
  InternalTolerance = 1e-06
  MakeInternals = false
  MapMode = 5
  Placement = pos=(0,0,5) rot=(0,0,1;0rad)
  Support = -> [Pocket004]
  TreeRank = 1
  sketch-geometry (7):
    g0: LineSegment StartX=3 StartY=116 StartZ=0 EndX=3 EndY=114 EndZ=0
    g1: LineSegment [constr] StartX=3 StartY=114 StartZ=0 EndX=2 EndY=114 EndZ=0
    g2: LineSegment StartX=2 StartY=114 StartZ=0 EndX=2 EndY=117.5 EndZ=0
    g3: LineSegment StartX=2 StartY=117.5 StartZ=0 EndX=3 EndY=117.5 EndZ=0
    g4: LineSegment StartX=3 StartY=117.5 StartZ=0 EndX=3 EndY=116 EndZ=0
    g5: LineSegment StartX=2 StartY=114 StartZ=0 EndX=3 EndY=113 EndZ=0
    g6: LineSegment StartX=3 StartY=113 StartZ=0 EndX=3 EndY=114 EndZ=0
  constraints (19):
    c: Coincident(g0,g-3)
    c: Vertical(g0)
    c: Coincident(g1,g0)
    c: Horizontal(g1)
    c: Coincident(g2,g1)
    c: Vertical(g2)
    c: Coincident(g3,g2)
    c: Horizontal(g3)
    c: Coincident(g4,g3)
    c: Coincident(g4,g0)
    c: Vertical(g4)
    c: DistanceY(g4,g4) = 1.5
    c: DistanceX(g1,g1) = 1
    c: DistanceY(g0,g0) = 2
    c: Coincident(g5,g2)
    c: PointOnObject(g5,g-3)
    c: Coincident(g6,g5)
    c: Coincident(g6,g0)
    c: Angle(g5,g1) = 0.785398
FEATURE [PartDesign::Pad] Pad008  label="PanelGuard1"
  AddSubType = 0
  AlongSketchNormal = false
  AutoTaperInnerAngle = false
  BaseFeature = -> Pocket004
  CheckUpToFaceLimits = true
  ClaimChildren = false
  Direction = (0,0,1)
  Fit = 0
  FitJoin = 0
  InnerFit = 0
  InnerFitJoin = 0
  Length = 51
  Length2 = 100
  Linearize = true
  NewSolid = false
  Profile = -> Sketch012
  Suppress = false
  TaperInnerAngle = 0
  TaperInnerAngleRev = 0
  TreeRank = 2
  Type = 0
  _ProfileBasedVersion = 1
FEATURE [PartDesign::Fillet] Fillet
  AddSubType = 0
  Base = -> Pad008 [Edge20,Edge21]
  BaseFeature = -> Pad008
  NewSolid = false
  Radius = 2
  SupportTransform = false
  Suppress = false
  TreeRank = 3
FEATURE [PartDesign::Chamfer] Chamfer
  AddSubType = 0
  Angle = 45
  Base = -> Fillet [Edge192,Edge184,Edge190,Edge182,Edge176,Edge174,Edge168,Edge166]
  BaseFeature = -> Fillet
  ChamferType = 0
  FlipDirection = false
  NewSolid = false
  Size = 2
  Size2 = 1
  SupportTransform = false
  Suppress = false
  TreeRank = 4
FEATURE [PartDesign::Body] Body
  AutoGroupSolids = false
  ClaimAllChildren = false
  ExportMode = 0
  Group = -> [LCS_0,Sketch_1,Pad,Sketch,Pad001,Sketch001,Pad002,Sketch002,Pocket,Sketch003,Pad003,Sketch004,Pad004,Sketch005,Pad005,Sketch006,Pad006,Sketch007,Pocket001,Sketch008,Pocket002,Sketch009,Pocket003,Sketch010,Pad007,Sketch011,Pocket004,Sketch012,Pad008,Fillet,Chamfer]
  Origin = -> Origin001
  Tip = -> Chamfer
  TreeRank = 0
  _ExportChildren = -> [LCS_0,Pad,Pad001,Pad002,Pocket,Pad003,Pad004,Pad005,Pad006,Pocket001,Pocket002,Pocket003,Pad007,Pocket004,Pad008,Fillet,Chamfer]
  _GroupVersion = 1
FEATURE [App::Part] Part  label="FirstPartPeripherals"
  ClaimAllChildren = false
  ExportMode = 1
  Group = -> [Body]
  Origin = -> Origin
  TreeRank = 0
  _ExportChildren = -> [Body]
  _GroupVersion = 1
---- part FirstPartPeripheralsTop.FCStd = doc fcstd_58b2082d1679 ----
FCSTD DOCUMENT  (FreeCAD 2022.1112R26244 +5306 (Git))
Label: FirstPartPeripheralsTop
License: All rights reserved
LicenseURL: http://en.wikipedia.org/wiki/All_rights_reserved
objects: Sketcher::SketchObject×14, PartDesign::Pad×9, PartDesign::Pocket×5, PartDesign::Chamfer×2, PartDesign::CoordinateSystem×1, PartDesign::Body×1, App::Part×1
note: 78 computed .brp shape members not serialized (recipe doc carries the construction recipe); baked Part::Feature solids carry a one-line shape summary decoded from their .brp

FEATURE [PartDesign::CoordinateSystem] LCS_0
  AttacherType = Attacher::AttachEngine3D
  AttachmentSupport = -> [X_Axis001]
  MapMode = 2
  Support = -> [X_Axis001]
  TreeRank = 0
FEATURE [Sketcher::SketchObject] Sketch_1
  ArcFitTolerance = 0
  ExternalBSplineMaxDegree = 0
  ExternalBSplineTolerance = 0
  FullyConstrained = true
  InternalTolerance = 1e-06
  MakeInternals = false
  TreeRank = 0
  sketch-geometry (4):
    g0: LineSegment StartX=0 StartY=0 StartZ=0 EndX=-140 EndY=0 EndZ=0
    g1: LineSegment StartX=-140 StartY=0 StartZ=0 EndX=-140 EndY=116 EndZ=0
    g2: LineSegment StartX=-140 StartY=116 StartZ=0 EndX=0 EndY=116 EndZ=0
    g3: LineSegment StartX=0 StartY=116 StartZ=0 EndX=0 EndY=0 EndZ=0
  constraints (11):
    c: Coincident(g0,g1)
    c: Coincident(g1,g2)
    c: Coincident(g2,g3)
    c: Coincident(g3,g0)
    c: Horizontal(g0)
    c: Horizontal(g2)
    c: Vertical(g1)
    c: Vertical(g3)
    c: Coincident(g0,g-1)
    c: DistanceY(g3,g3) = 116
    c: DistanceX(g2,g2) = 140
FEATURE [PartDesign::Pad] Pad  label="MainSupport"
  AddSubType = 0
  AutoTaperInnerAngle = false
  CheckUpToFaceLimits = true
  ClaimChildren = false
  Direction = (0,0,1)
  Fit = 0
  FitJoin = 0
  InnerFit = 0
  InnerFitJoin = 0
  Length = 5
  Length2 = 100
  NewSolid = false
  Profile = -> Sketch_1
  Suppress = false
  TaperInnerAngle = 0
  TaperInnerAngleRev = 0
  TreeRank = 0
  Type = 0
  _ProfileBasedVersion = 0
FEATURE [Sketcher::SketchObject] Sketch
  ArcFitTolerance = 0
  AttachmentSupport = -> [XY_Plane001]
  ExternalBSplineMaxDegree = 0
  ExternalBSplineTolerance = 0
  ExternalGeometry = -> [Pad]
  FullyConstrained = true
  InternalTolerance = 1e-06
  MakeInternals = false
  MapMode = 5
  Support = -> [XY_Plane001]
  TreeRank = 0
  sketch-geometry (4):
    g0: LineSegment StartX=0 StartY=0 StartZ=0 EndX=-140 EndY=0 EndZ=0
    g1: LineSegment StartX=-140 StartY=0 StartZ=0 EndX=-140 EndY=-15 EndZ=0
    g2: LineSegment StartX=-140 StartY=-15 StartZ=0 EndX=0 EndY=-15 EndZ=0
    g3: LineSegment StartX=0 StartY=-15 StartZ=0 EndX=0 EndY=0 EndZ=0
  constraints (10):
    c: Coincident(g0,g1)
    c: Coincident(g1,g2)
    c: Coincident(g2,g3)
    c: Coincident(g3,g0)
    c: Horizontal(g2)
    c: Vertical(g1)
    c: Vertical(g3)
    c: Coincident(g0,g-1)
    c: Coincident(g0,g-3)
    c: DistanceY(g3,g3) = 15
FEATURE [PartDesign::Pad] Pad001  label="ExtraPeripheralsSize"
  AddSubType = 0
  AutoTaperInnerAngle = false
  BaseFeature = -> Pad
  CheckUpToFaceLimits = true
  ClaimChildren = false
  Direction = (0,0,1)
  Fit = 0
  FitJoin = 0
  InnerFit = 0
  InnerFitJoin = 0
  Length = 5
  Length2 = 100
  NewSolid = false
  Profile = -> Sketch
  Suppress = false
  TaperInnerAngle = 0
  TaperInnerAngleRev = 0
  TreeRank = 0
  Type = 0
  _ProfileBasedVersion = 0
FEATURE [Sketcher::SketchObject] Sketch001
  ArcFitTolerance = 0
  AttachmentSupport = -> [Pad001]
  ExternalBSplineMaxDegree = 0
  ExternalBSplineTolerance = 0
  ExternalGeometry = -> [Pad001]
  FullyConstrained = true
  InternalTolerance = 1e-06
  MakeInternals = false
  MapMode = 5
  Placement = pos=(0,0,0) rot=(0.57735,0.57735,0.57735;2.0944rad)
  Support = -> [Pad001]
  TreeRank = 1
  sketch-geometry (4):
    g0: LineSegment StartX=-15 StartY=5 StartZ=0 EndX=116 EndY=5 EndZ=0
    g1: LineSegment StartX=116 StartY=5 StartZ=0 EndX=116 EndY=0 EndZ=0
    g2: LineSegment StartX=116 StartY=0 StartZ=0 EndX=-15 EndY=0 EndZ=0
    g3: LineSegment StartX=-15 StartY=0 StartZ=0 EndX=-15 EndY=5 EndZ=0
  constraints (10):
    c: Coincident(g0,g1)
    c: Coincident(g1,g2)
    c: Coincident(g2,g3)
    c: Coincident(g3,g0)
    c: Horizontal(g0)
    c: Horizontal(g2)
    c: Vertical(g1)
    c: Vertical(g3)
    c: Coincident(g0,g-3)
    c: Coincident(g1,g-4)
FEATURE [PartDesign::Pad] Pad002  label="ExtraSideSize"
  AddSubType = 0
  AlongSketchNormal = false
  AutoTaperInnerAngle = false
  BaseFeature = -> Pad001
  CheckUpToFaceLimits = true
  ClaimChildren = false
  Direction = (1,0,0)
  Fit = 0
  FitJoin = 0
  InnerFit = 0
  InnerFitJoin = 0
  Length = 5
  Length2 = 100
  Linearize = true
  NewSolid = false
  Profile = -> Sketch001
  Suppress = false
  TaperInnerAngle = 0
  TaperInnerAngleRev = 0
  TreeRank = 2
  Type = 0
  _ProfileBasedVersion = 1
FEATURE [Sketcher::SketchObject] Sketch002
  ArcFitTolerance = 0
  AttachmentSupport = -> [Pad002]
  ExternalBSplineMaxDegree = 0
  ExternalBSplineTolerance = 0
  ExternalGeometry = -> [Pad002]
  FullyConstrained = true
  InternalTolerance = 1e-06
  MakeInternals = false
  MapMode = 5
  Placement = pos=(0,0,5) rot=(0,0,1;0rad)
  Support = -> [Pad002]
  TreeRank = 3
  sketch-geometry (4):
    g0: LineSegment StartX=5 StartY=-15 StartZ=0 EndX=-4.2 EndY=-15 EndZ=0
    g1: LineSegment StartX=-4.2 StartY=-15 StartZ=0 EndX=-4.2 EndY=-5.8 EndZ=0
    g2: LineSegment StartX=-4.2 StartY=-5.8 StartZ=0 EndX=5 EndY=-5.8 EndZ=0
    g3: LineSegment StartX=5 StartY=-5.8 StartZ=0 EndX=5 EndY=-15 EndZ=0
  constraints (11):
    c: Coincident(g0,g1)
    c: Coincident(g1,g2)
    c: Coincident(g2,g3)
    c: Coincident(g3,g0)
    c: Horizontal(g0)
    c: Horizontal(g2)
    c: Vertical(g1)
    c: Vertical(g3)
    c: Coincident(g0,g-3)
    c: Equal(g2,g1)
    c: DistanceX(g2,g2) = 9.2
FEATURE [PartDesign::Pocket] Pocket  label="ColumnPartHole"
  AddSubType = 1
  AutoTaperInnerAngle = false
  BaseFeature = -> Pad002
  CheckUpToFaceLimits = true
  ClaimChildren = false
  Fit = 0
  FitJoin = 0
  InnerFit = 0
  InnerFitJoin = 0
  Length = 5
  Length2 = 100
  Linearize = true
  NewSolid = false
  Profile = -> Sketch002
  Suppress = false
  TaperInnerAngle = 0
  TaperInnerAngleRev = 0
  TreeRank = 4
  Type = 0
  _ProfileBasedVersion = 1
  _Version = 1
FEATURE [Sketcher::SketchObject] Sketch003
  ArcFitTolerance = 0
  AttachmentSupport = -> [Pocket]
  ExternalBSplineMaxDegree = 0
  ExternalBSplineTolerance = 0
  ExternalGeometry = -> [Pocket]
  FullyConstrained = true
  InternalTolerance = 1e-06
  MakeInternals = false
  MapMode = 5
  Placement = pos=(0,0,0) rot=(1,0,0;3.14159rad)
  Support = -> [Pocket]
  TreeRank = 5
  sketch-geometry (4):
    g0: LineSegment StartX=-4.2 StartY=15 StartZ=0 EndX=-107 EndY=15 EndZ=0
    g1: LineSegment StartX=-107 StartY=15 StartZ=0 EndX=-107 EndY=13 EndZ=0
    g2: LineSegment StartX=-107 StartY=13 StartZ=0 EndX=-4.2 EndY=13 EndZ=0
    g3: LineSegment StartX=-4.2 StartY=13 StartZ=0 EndX=-4.2 EndY=15 EndZ=0
  constraints (11):
    c: Coincident(g0,g1)
    c: Coincident(g1,g2)
    c: Coincident(g2,g3)
    c: Coincident(g3,g0)
    c: Horizontal(g0)
    c: Horizontal(g2)
    c: Vertical(g1)
    c: Vertical(g3)
    c: Coincident(g0,g-4)
    c: DistanceX(g0,g-1) = 107
    c: DistanceY(g3,g3) = 2
FEATURE [PartDesign::Pad] Pad003  label="PeripheralPanel"
  AddSubType = 0
  AlongSketchNormal = false
  AutoTaperInnerAngle = false
  BaseFeature = -> Pocket
  CheckUpToFaceLimits = true
  ClaimChildren = false
  Direction = (0,0,-1)
  Fit = 0
  FitJoin = 0
  InnerFit = 0
  InnerFitJoin = 0
  Length = 51
  Length2 = 100
  Linearize = true
  NewSolid = false
  Profile = -> Sketch003
  Suppress = false
  TaperInnerAngle = 0
  TaperInnerAngleRev = 0
  TreeRank = 6
  Type = 0
  _ProfileBasedVersion = 1
FEATURE [Sketcher::SketchObject] Sketch004
  ArcFitTolerance = 0
  AttachmentSupport = -> [Pad003]
  ExternalBSplineMaxDegree = 0
  ExternalBSplineTolerance = 0
  ExternalGeometry = -> [Pad003]
  FullyConstrained = true
  InternalTolerance = 1e-06
  MakeInternals = false
  MapMode = 5
  Placement = pos=(0,0,0) rot=(1,0,0;3.14159rad)
  Support = -> [Pad003]
  TreeRank = 7
  sketch-geometry (4):
    g0: LineSegment StartX=5 StartY=-116 StartZ=0 EndX=3 EndY=-116 EndZ=0
    g1: LineSegment StartX=3 StartY=-116 StartZ=0 EndX=3 EndY=5.8 EndZ=0
    g2: LineSegment StartX=3 StartY=5.8 StartZ=0 EndX=5 EndY=5.8 EndZ=0
    g3: LineSegment StartX=5 StartY=5.8 StartZ=0 EndX=5 EndY=-116 EndZ=0
  constraints (10):
    c: Coincident(g0,g1)
    c: Coincident(g1,g2)
    c: Coincident(g2,g3)
    c: Coincident(g3,g0)
    c: Horizontal(g0)
    c: Horizontal(g2)
    c: Vertical(g1)
    c: Coincident(g0,g-3)
    c: Coincident(g2,g-3)
    c: DistanceX(g0,g0) = 2
FEATURE [PartDesign::Pad] Pad004  label="SidePanel"
  AddSubType = 0
  AlongSketchNormal = false
  AutoTaperInnerAngle = false
  BaseFeature = -> Pad003
  CheckUpToFaceLimits = true
  ClaimChildren = false
  Direction = (0,0,-1)
  Fit = 0
  FitJoin = 0
  InnerFit = 0
  InnerFitJoin = 0
  Length = 51
  Length2 = 100
  Linearize = true
  NewSolid = false
  Profile = -> Sketch004
  Suppress = false
  TaperInnerAngle = 0
  TaperInnerAngleRev = 0
  TreeRank = 8
  Type = 0
  _ProfileBasedVersion = 1
FEATURE [Sketcher::SketchObject] Sketch005
  ArcFitTolerance = 0
  AttachmentSupport = -> [Pad004]
  ExternalBSplineMaxDegree = 0
  ExternalBSplineTolerance = 0
  ExternalGeometry = -> [Pad004]
  FullyConstrained = true
  InternalTolerance = 1e-06
  MakeInternals = false
  MapMode = 5
  Placement = pos=(0,0,0) rot=(1,0,0;3.14159rad)
  Support = -> [Pad004]
  TreeRank = 9
  sketch-geometry (6):
    g0: LineSegment StartX=-4.2 StartY=13 StartZ=0 EndX=-6.2 EndY=13 EndZ=0
    g1: LineSegment StartX=-6.2 StartY=13 StartZ=0 EndX=-6.2 EndY=3.8 EndZ=0
    g2: LineSegment StartX=-6.2 StartY=3.8 StartZ=0 EndX=3 EndY=3.8 EndZ=0
    g3: LineSegment StartX=3 StartY=3.8 StartZ=0 EndX=3 EndY=5.8 EndZ=0
    g4: LineSegment StartX=-4.2 StartY=13 StartZ=0 EndX=-4.2 EndY=5.8 EndZ=0
    g5: LineSegment StartX=-4.2 StartY=5.8 StartZ=0 EndX=3 EndY=5.8 EndZ=0
  constraints (15):
    c: Coincident(g0,g-3)
    c: Horizontal(g0)
    c: Coincident(g1,g0)
    c: Vertical(g1)
    c: Coincident(g2,g1)
    c: Horizontal(g2)
    c: Coincident(g3,g2)
    c: Coincident(g3,g-4)
    c: Vertical(g3)
    c: DistanceX(g0,g0) = 2
    c: DistanceY(g3,g3) = 2
    c: Coincident(g4,g0)
    c: Coincident(g4,g-3)
    c: Coincident(g5,g4)
    c: Coincident(g5,g3)
FEATURE [PartDesign::Pad] Pad005  label="ColumnPartPanel"
  AddSubType = 0
  AlongSketchNormal = false
  AutoTaperInnerAngle = false
  BaseFeature = -> Pad004
  CheckUpToFaceLimits = true
  ClaimChildren = false
  Direction = (0,0,-1)
  Fit = 0
  FitJoin = 0
  InnerFit = 0
  InnerFitJoin = 0
  Length = 53
  Length2 = 100
  Linearize = true
  NewSolid = false
  Profile = -> Sketch005
  Suppress = false
  TaperInnerAngle = 0
  TaperInnerAngleRev = 0
  TreeRank = 10
  Type = 0
  _ProfileBasedVersion = 1
FEATURE [Sketcher::SketchObject] Sketch006
  ArcFitTolerance = 0
  AttachmentSupport = -> [Pad005]
  ExternalBSplineMaxDegree = 0
  ExternalBSplineTolerance = 0
  ExternalGeometry = -> [Pad005]
  FullyConstrained = true
  InternalTolerance = 1e-06
  MakeInternals = false
  MapMode = 5
  Placement = pos=(0,-15,0) rot=(1,0,0;1.5708rad)
  Support = -> [Pad005]
  TreeRank = 11
  sketch-geometry (20):
    g0: LineSegment [constr] StartX=0 StartY=0 StartZ=0 EndX=-107 EndY=0 EndZ=0
    g1: LineSegment [constr] StartX=-107 StartY=0 StartZ=0 EndX=-107 EndY=-30 EndZ=0
    g2: LineSegment [constr] StartX=-107 StartY=-30 StartZ=0 EndX=0 EndY=-30 EndZ=0
    g3: LineSegment [constr] StartX=0 StartY=-30 StartZ=0 EndX=0 EndY=0 EndZ=0
    g4: LineSegment StartX=-16 StartY=-30 StartZ=0 EndX=-31 EndY=-30 EndZ=0
    g5: LineSegment StartX=-31 StartY=-30 StartZ=0 EndX=-31 EndY=-71 EndZ=0
    g6: LineSegment StartX=-31 StartY=-71 StartZ=0 EndX=-16 EndY=-71 EndZ=0
    g7: LineSegment StartX=-16 StartY=-71 StartZ=0 EndX=-16 EndY=-30 EndZ=0
    g8: LineSegment StartX=-36 StartY=-30 StartZ=0 EndX=-51 EndY=-30 EndZ=0
    g9: LineSegment StartX=-51 StartY=-30 StartZ=0 EndX=-51 EndY=-71 EndZ=0
    g10: LineSegment StartX=-51 StartY=-71 StartZ=0 EndX=-36 EndY=-71 EndZ=0
    g11: LineSegment StartX=-36 StartY=-71 StartZ=0 EndX=-36 EndY=-30 EndZ=0
    g12: LineSegment StartX=-56 StartY=-30 StartZ=0 EndX=-71 EndY=-30 EndZ=0
    g13: LineSegment StartX=-71 StartY=-30 StartZ=0 EndX=-71 EndY=-71 EndZ=0
    g14: LineSegment StartX=-71 StartY=-71 StartZ=0 EndX=-56 EndY=-71 EndZ=0
    g15: LineSegment StartX=-56 StartY=-71 StartZ=0 EndX=-56 EndY=-30 EndZ=0
    g16: LineSegment StartX=-76 StartY=-30 StartZ=0 EndX=-91 EndY=-30 EndZ=0
    g17: LineSegment StartX=-91 StartY=-30 StartZ=0 EndX=-91 EndY=-71 EndZ=0
    g18: LineSegment StartX=-91 StartY=-71 StartZ=0 EndX=-76 EndY=-71 EndZ=0
    g19: LineSegment StartX=-76 StartY=-71 StartZ=0 EndX=-76 EndY=-30 EndZ=0
  constraints (59):
    c: Coincident(g0,g1)
    c: Coincident(g1,g2)
    c: Coincident(g2,g3)
    c: Coincident(g3,g0)
    c: Horizontal(g0)
    c: Horizontal(g2)
    c: Vertical(g1)
    c: Vertical(g3)
    c: Coincident(g0,g-1)
    c: PointOnObject(g1,g-3)
    c: DistanceY(g1,g1) = 30
    c: Coincident(g4,g5)
    c: Coincident(g5,g6)
    c: Coincident(g6,g7)
    c: Coincident(g7,g4)
    c: Horizontal(g4)
    c: Horizontal(g6)
    c: Vertical(g5)
    c: Vertical(g7)
    c: PointOnObject(g4,g2)
    c: Coincident(g8,g9)
    c: Coincident(g9,g10)
    c: Coincident(g10,g11)
    c: Coincident(g11,g8)
    c: Horizontal(g8)
    c: Horizontal(g10)
    c: Vertical(g9)
    c: Vertical(g11)
    c: PointOnObject(g8,g2)
    c: Coincident(g12,g13)
    c: Coincident(g13,g14)
    c: Coincident(g14,g15)
    c: Coincident(g15,g12)
    c: Horizontal(g12)
    c: Horizontal(g14)
    c: Vertical(g13)
    c: Vertical(g15)
    c: PointOnObject(g12,g2)
    c: Coincident(g16,g17)
    c: Coincident(g17,g18)
    c: Coincident(g18,g19)
    c: Coincident(g19,g16)
    c: Horizontal(g16)
    c: Horizontal(g18)
    c: Vertical(g17)
    c: Vertical(g19)
    c: PointOnObject(g16,g2)
    c: DistanceX(g4,g2) = 16
    c: DistanceX(g4,g4) = 15
    c: Equal(g8,g4)
    c: Equal(g12,g8)
    c: Equal(g16,g12)
    c: DistanceX(g8,g4) = 5
    c: DistanceX(g12,g8) = 5
    c: DistanceX(g16,g12) = 5
    c: Equal(g5,g9)
    c: Equal(g9,g13)
    c: Equal(g13,g17)
    c: DistanceY(g7,g7) = 41
FEATURE [PartDesign::Pocket] Pocket001  label="PeripheralHoles"
  AddSubType = 1
  AutoTaperInnerAngle = false
  BaseFeature = -> Pad005
  CheckUpToFaceLimits = true
  ClaimChildren = false
  Fit = 0
  FitJoin = 0
  InnerFit = 0
  InnerFitJoin = 0
  Length = 0
  Length2 = 100
  Linearize = true
  NewSolid = false
  Profile = -> Sketch006
  Suppress = false
  TaperInnerAngle = 0
  TaperInnerAngleRev = 0
  TreeRank = 12
  Type = 2
  _ProfileBasedVersion = 1
  _Version = 1
FEATURE [Sketcher::SketchObject] Sketch007
  ArcFitTolerance = 0
  AttachmentSupport = -> [Pocket001]
  ExternalBSplineMaxDegree = 0
  ExternalBSplineTolerance = 0
  ExternalGeometry = -> [Pocket001]
  FullyConstrained = true
  InternalTolerance = 1e-06
  MakeInternals = false
  MapMode = 5
  Placement = pos=(0,-5.8,0) rot=(1,0,0;1.5708rad)
  Support = -> [Pocket001]
  TreeRank = 13
  sketch-geometry (4):
    g0: LineSegment StartX=-4.2 StartY=-51 StartZ=0 EndX=5 EndY=-51 EndZ=0
    g1: LineSegment StartX=5 StartY=-51 StartZ=0 EndX=5 EndY=-46 EndZ=0
    g2: LineSegment StartX=5 StartY=-46 StartZ=0 EndX=-4.2 EndY=-46 EndZ=0
    g3: LineSegment StartX=-4.2 StartY=-46 StartZ=0 EndX=-4.2 EndY=-51 EndZ=0
  constraints (10):
    c: Coincident(g0,g1)
    c: Coincident(g1,g2)
    c: Coincident(g2,g3)
    c: Coincident(g3,g0)
    c: Horizontal(g2)
    c: Vertical(g1)
    c: Vertical(g3)
    c: Coincident(g0,g-3)
    c: Coincident(g0,g-4)
    c: DistanceY(g1,g1) = 5
FEATURE [PartDesign::Pad] Pad006  label="HoleSupport"
  AddSubType = 0
  AlongSketchNormal = false
  AutoTaperInnerAngle = false
  BaseFeature = -> Pocket001
  CheckUpToFaceLimits = true
  ClaimChildren = false
  Direction = (0,-1,2e-16)
  Fit = 0
  FitJoin = 0
  InnerFit = 0
  InnerFitJoin = 0
  Length = 10
  Length2 = 100
  Linearize = true
  NewSolid = false
  Profile = -> Sketch007
  Suppress = false
  TaperInnerAngle = 0
  TaperInnerAngleRev = 0
  TreeRank = 14
  Type = 3
  UpToFace = -> Pocket001 [Face12]
  _ProfileBasedVersion = 1
FEATURE [Sketcher::SketchObject] Sketch008
  ArcFitTolerance = 0
  AttachmentSupport = -> [Pad006]
  ExternalBSplineMaxDegree = 0
  ExternalBSplineTolerance = 0
  ExternalGeometry = -> [Pad006]
  FullyConstrained = true
  InternalTolerance = 1e-06
  MakeInternals = false
  MapMode = 5
  Placement = pos=(0,-1.01e-14,-46) rot=(0,0,1;0rad)
  Support = -> [Pad006]
  TreeRank = 15
  sketch-geometry (3):
    g0: LineSegment [constr] StartX=-4.2 StartY=-9.4 StartZ=0 EndX=-0.6 EndY=-9.4 EndZ=0
    g1: LineSegment [constr] StartX=-0.6 StartY=-9.4 StartZ=0 EndX=-0.6 EndY=-15 EndZ=0
    g2: Circle CenterX=-0.6 CenterY=-9.4 CenterZ=0 NormalX=0 NormalY=0 NormalZ=1 AngleXU=0 Radius=1.6
  constraints (9):
    c: Horizontal(g0)
    c: Coincident(g1,g0)
    c: Vertical(g1)
    c: Coincident(g2,g0)
    c: Diameter(g2) = 3.2
    c: PointOnObject(g0,g-3)
    c: PointOnObject(g1,g-4)
    c: DistanceX(g-4,g1) = 3.6
    c: DistanceY(g0,g-3) = 3.6
FEATURE [PartDesign::Pocket] Pocket002  label="Hole"
  AddSubType = 1
  AutoTaperInnerAngle = false
  BaseFeature = -> Pad006
  CheckUpToFaceLimits = true
  ClaimChildren = false
  Fit = 0
  FitJoin = 0
  InnerFit = 0
  InnerFitJoin = 0
  Length = 5
  Length2 = 100
  Linearize = true
  NewSolid = false
  Profile = -> Sketch008
  Suppress = false
  TaperInnerAngle = 0
  TaperInnerAngleRev = 0
  TreeRank = 16
  Type = 2
  _ProfileBasedVersion = 1
  _Version = 1
FEATURE [Sketcher::SketchObject] Sketch009
  ArcFitTolerance = 0
  AttachmentSupport = -> [Pocket002]
  ExternalBSplineMaxDegree = 0
  ExternalBSplineTolerance = 0
  ExternalGeometry = -> [Pocket002]
  FullyConstrained = true
  InternalTolerance = 1e-06
  MakeInternals = false
  MapMode = 5
  Placement = pos=(0,0,0) rot=(1,0,0;3.14159rad)
  Support = -> [Pocket002]
  TreeRank = 17
  sketch-geometry (4):
    g0: LineSegment StartX=-140 StartY=15 StartZ=0 EndX=-107 EndY=15 EndZ=0
    g1: LineSegment StartX=-107 StartY=15 StartZ=0 EndX=-107 EndY=13 EndZ=0
    g2: LineSegment StartX=-107 StartY=13 StartZ=0 EndX=-140 EndY=13 EndZ=0
    g3: LineSegment StartX=-140 StartY=13 StartZ=0 EndX=-140 EndY=15 EndZ=0
  constraints (10):
    c: Coincident(g0,g1)
    c: Coincident(g1,g2)
    c: Coincident(g2,g3)
    c: Coincident(g3,g0)
    c: Horizontal(g0)
    c: Horizontal(g2)
    c: Vertical(g1)
    c: Vertical(g3)
    c: Coincident(g0,g-3)
    c: Coincident(g1,g-4)
FEATURE [PartDesign::Pad] Pad007  label="EndPeripheralPanel"
  AddSubType = 0
  AlongSketchNormal = false
  AutoTaperInnerAngle = false
  BaseFeature = -> Pocket002
  CheckUpToFaceLimits = true
  ClaimChildren = false
  Direction = (0,0,-1)
  Fit = 0
  FitJoin = 0
  InnerFit = 0
  InnerFitJoin = 0
  Length = 51
  Length2 = 100
  Linearize = true
  NewSolid = false
  Profile = -> Sketch009
  Suppress = false
  TaperInnerAngle = 0
  TaperInnerAngleRev = 0
  TreeRank = 18
  Type = 0
  _ProfileBasedVersion = 1
FEATURE [Sketcher::SketchObject] Sketch010
  ArcFitTolerance = 0
  AttachmentSupport = -> [Pad007]
  ExternalBSplineMaxDegree = 0
  ExternalBSplineTolerance = 0
  ExternalGeometry = -> [Pad007]
  FullyConstrained = true
  InternalTolerance = 1e-06
  MakeInternals = false
  MapMode = 5
  Placement = pos=(-140,0,0) rot=(0.57735,-0.57735,-0.57735;2.0944rad)
  Support = -> [Pad007]
  TreeRank = 19
  sketch-geometry (4):
    g0: LineSegment StartX=-95.05 StartY=3.58 StartZ=0 EndX=13.05 EndY=3.58 EndZ=0
    g1: LineSegment StartX=13.05 StartY=3.58 StartZ=0 EndX=13.05 EndY=1.5 EndZ=0
    g2: LineSegment StartX=13.05 StartY=1.5 StartZ=0 EndX=-95.05 EndY=1.5 EndZ=0
    g3: LineSegment StartX=-95.05 StartY=1.5 StartZ=0 EndX=-95.05 EndY=3.58 EndZ=0
  constraints (12):
    c: Coincident(g0,g1)
    c: Coincident(g1,g2)
    c: Coincident(g2,g3)
    c: Coincident(g3,g0)
    c: Horizontal(g0)
    c: Horizontal(g2)
    c: Vertical(g1)
    c: Vertical(g3)
    c: DistanceX(g-3,g0) = 20.95
    c: DistanceX(g0,g-4) = 1.95
    c: DistanceY(g1,g1) = 2.08
    c: DistanceY(g-4,g1) = 1.5
FEATURE [PartDesign::Pocket] Pocket003  label="PuzzleHole1"
  AddSubType = 1
  AutoTaperInnerAngle = false
  BaseFeature = -> Pad007
  CheckUpToFaceLimits = true
  ClaimChildren = false
  Fit = 0
  FitJoin = 0
  InnerFit = 0
  InnerFitJoin = 0
  Length = 11
  Length2 = 100
  Linearize = true
  NewSolid = false
  Profile = -> Sketch010
  Suppress = false
  TaperInnerAngle = 0
  TaperInnerAngleRev = 0
  TreeRank = 20
  Type = 0
  _ProfileBasedVersion = 1
  _Version = 1
FEATURE [Sketcher::SketchObject] Sketch011
  ArcFitTolerance = 0
  AttachmentSupport = -> [Pocket003]
  ExternalBSplineMaxDegree = 0
  ExternalBSplineTolerance = 0
  ExternalGeometry = -> [Pocket003]
  FullyConstrained = true
  InternalTolerance = 1e-06
  MakeInternals = false
  MapMode = 5
  Placement = pos=(0,116,0) rot=(0,0.707107,0.707107;3.14159rad)
  Support = -> [Pocket003]
  TreeRank = 21
  sketch-geometry (4):
    g0: LineSegment StartX=-3.05 StartY=3.58 StartZ=0 EndX=119.05 EndY=3.58 EndZ=0
    g1: LineSegment StartX=119.05 StartY=3.58 StartZ=0 EndX=119.05 EndY=1.5 EndZ=0
    g2: LineSegment StartX=119.05 StartY=1.5 StartZ=0 EndX=-3.05 EndY=1.5 EndZ=0
    g3: LineSegment StartX=-3.05 StartY=1.5 StartZ=0 EndX=-3.05 EndY=3.58 EndZ=0
  constraints (12):
    c: Coincident(g0,g1)
    c: Coincident(g1,g2)
    c: Coincident(g2,g3)
    c: Coincident(g3,g0)
    c: Horizontal(g0)
    c: Horizontal(g2)
    c: Vertical(g1)
    c: Vertical(g3)
    c: DistanceX(g0,g-3) = 20.95
    c: DistanceX(g-4,g0) = 1.95
    c: DistanceY(g3,g3) = 2.08
    c: DistanceY(g-4,g2) = 1.5
FEATURE [PartDesign::Pocket] Pocket004  label="PuzzleHole2"
  AddSubType = 1
  AutoTaperInnerAngle = false
  BaseFeature = -> Pocket003
  CheckUpToFaceLimits = true
  ClaimChildren = false
  Fit = 0
  FitJoin = 0
  InnerFit = 0
  InnerFitJoin = 0
  Length = 11
  Length2 = 100
  Linearize = true
  NewSolid = false
  Profile = -> Sketch011
  Suppress = false
  TaperInnerAngle = 0
  TaperInnerAngleRev = 0
  TreeRank = 22
  Type = 0
  _ProfileBasedVersion = 1
  _Version = 1
FEATURE [PartDesign::Chamfer] Chamfer
  AddSubType = 0
  Angle = 45
  Base = -> Pocket004 [Edge58,Edge57,Edge56,Edge60,Edge59]
  BaseFeature = -> Pocket004
  ChamferType = 0
  FlipDirection = false
  NewSolid = false
  Size = 2
  Size2 = 1
  SupportTransform = false
  Suppress = false
  TreeRank = 23
FEATURE [Sketcher::SketchObject] Sketch012
  ArcFitTolerance = 0
  AttachmentSupport = -> [Chamfer]
  ExternalBSplineMaxDegree = 0
  ExternalBSplineTolerance = 0
  ExternalGeometry = -> [Chamfer]
  FullyConstrained = true
  InternalTolerance = 1e-06
  MakeInternals = false
  MapMode = 5
  Placement = pos=(0,0,0) rot=(1,0,0;3.14159rad)
  Support = -> [Chamfer]
  TreeRank = 24
  sketch-geometry (6):
    g0: LineSegment [constr] StartX=3 StartY=-114 StartZ=0 EndX=2 EndY=-114 EndZ=0
    g1: LineSegment StartX=2 StartY=-114 StartZ=0 EndX=2 EndY=-117.5 EndZ=0
    g2: LineSegment StartX=2 StartY=-117.5 StartZ=0 EndX=3 EndY=-117.5 EndZ=0
    g3: LineSegment StartX=3 StartY=-117.5 StartZ=0 EndX=3 EndY=-114 EndZ=0
    g4: LineSegment StartX=2 StartY=-114 StartZ=0 EndX=3 EndY=-113 EndZ=0
    g5: LineSegment StartX=3 StartY=-113 StartZ=0 EndX=3 EndY=-114 EndZ=0
  constraints (17):
    c: Coincident(g0,g1)
    c: Coincident(g1,g2)
    c: Coincident(g2,g3)
    c: Coincident(g3,g0)
    c: Horizontal(g0)
    c: Horizontal(g2)
    c: Vertical(g1)
    c: Vertical(g3)
    c: PointOnObject(g0,g-3)
    c: DistanceY(g-3,g0) = 2
    c: DistanceY(g2,g-3) = 1.5
    c: DistanceX(g0,g0) = 1
    c: Coincident(g4,g1)
    c: PointOnObject(g4,g-3)
    c: Coincident(g5,g4)
    c: Coincident(g5,g3)
    c: Angle(g0,g4) = 0.785398
FEATURE [PartDesign::Pad] Pad008  label="PanelGuard"
  AddSubType = 0
  AlongSketchNormal = false
  AutoTaperInnerAngle = false
  BaseFeature = -> Chamfer
  CheckUpToFaceLimits = true
  ClaimChildren = false
  Direction = (0,0,-1)
  Fit = 0
  FitJoin = 0
  InnerFit = 0
  InnerFitJoin = 0
  Length = 10
  Length2 = 100
  Linearize = true
  NewSolid = false
  Profile = -> Sketch012
  Suppress = false
  TaperInnerAngle = 0
  TaperInnerAngleRev = 0
  TreeRank = 25
  Type = 3
  UpToFace = -> Chamfer [Face69]
  _ProfileBasedVersion = 1
FEATURE [PartDesign::Chamfer] Chamfer001
  AddSubType = 0
  Angle = 45
  Base = -> Pad008 [Edge126,Edge127,Edge130,Edge131,Edge134,Edge135,Edge138,Edge139]
  BaseFeature = -> Pad008
  ChamferType = 0
  FlipDirection = false
  NewSolid = false
  Size = 2
  Size2 = 1
  SupportTransform = false
  Suppress = false
  TreeRank = 26
FEATURE [PartDesign::Body] Body
  AutoGroupSolids = false
  ClaimAllChildren = false
  ExportMode = 0
  Group = -> [LCS_0,Sketch_1,Pad,Sketch,Pad001,Sketch001,Pad002,Sketch002,Pocket,Sketch003,Pad003,Sketch004,Pad004,Sketch005,Pad005,Sketch006,Pocket001,Sketch007,Pad006,Sketch008,Pocket002,Sketch009,Pad007,Sketch010,Pocket003,Sketch011,Pocket004,Chamfer,Sketch012,Pad008,Chamfer001]
  Origin = -> Origin001
  Tip = -> Chamfer001
  TreeRank = 0
  _ExportChildren = -> [LCS_0,Pad,Pad001,Pad002,Pocket,Pad003,Pad004,Pad005,Pocket001,Pad006,Pocket002,Pad007,Pocket003,Pocket004,Chamfer,Pad008,Chamfer001]
  _GroupVersion = 1
FEATURE [App::Part] Part  label="FirstPartPeripheralsTop"
  ClaimAllChildren = false
  ExportMode = 1
  Group = -> [Body]
  Origin = -> Origin
  TreeRank = 0
  _ExportChildren = -> [Body]
  _GroupVersion = 1
---- part FirstPartProcessor.FCStd = doc fcstd_48e0bf0786dc ----
FCSTD DOCUMENT  (FreeCAD 2022.430R26244 +4758 (Git))
Label: FirstPartProcessor
License: All rights reserved
LicenseURL: http://en.wikipedia.org/wiki/All_rights_reserved
objects: Sketcher::SketchObject×15, PartDesign::Pad×9, PartDesign::Pocket×6, PartDesign::Fillet×2, PartDesign::CoordinateSystem×1, PartDesign::PolarPattern×1, PartDesign::Body×1, App::Part×1
note: 71 computed .brp shape members not serialized (recipe doc carries the construction recipe); baked Part::Feature solids carry a one-line shape summary decoded from their .brp

FEATURE [PartDesign::CoordinateSystem] LCS_0
  AttacherType = Attacher::AttachEngine3D
  MapMode = 2
  Support = -> [X_Axis001]
  TreeRank = 0
FEATURE [Sketcher::SketchObject] Sketch_1
  FullyConstrained = true
  TreeRank = 0
  sketch-geometry (4):
    g0: LineSegment StartX=0 StartY=0 StartZ=0 EndX=-140 EndY=0 EndZ=0
    g1: LineSegment StartX=-140 StartY=0 StartZ=0 EndX=-140 EndY=93 EndZ=0
    g2: LineSegment StartX=-140 StartY=93 StartZ=0 EndX=0 EndY=93 EndZ=0
    g3: LineSegment StartX=0 StartY=93 StartZ=0 EndX=0 EndY=0 EndZ=0
  constraints (11):
    c: Coincident(g0,g1)
    c: Coincident(g1,g2)
    c: Coincident(g2,g3)
    c: Coincident(g3,g0)
    c: Horizontal(g0)
    c: Horizontal(g2)
    c: Vertical(g1)
    c: Vertical(g3)
    c: Coincident(g0,g-1)
    c: DistanceY(g3,g3) = 93
    c: DistanceX(g2,g2) = 140
FEATURE [PartDesign::Pad] Pad  label="MainSupport"
  AddSubType = 0
  CheckUpToFaceLimits = true
  ClaimChildren = false
  Direction = (0,0,1)
  Fit = 0
  FitJoin = 0
  InnerFit = 0
  InnerFitJoin = 0
  InnerTaperAngle = 0
  InnerTaperAngleRev = 0
  Length = 5
  Length2 = 100
  NewSolid = false
  Profile = -> Sketch_1
  Suppress = false
  TreeRank = 0
  Type = 0
  _ProfileBasedVersion = 0
FEATURE [Sketcher::SketchObject] Sketch
  ExternalGeometry = -> [Pad]
  FullyConstrained = true
  MapMode = 5
  Support = -> [XY_Plane001]
  TreeRank = 0
  sketch-geometry (4):
    g0: LineSegment StartX=0 StartY=0 StartZ=0 EndX=-140 EndY=0 EndZ=0
    g1: LineSegment StartX=-140 StartY=0 StartZ=0 EndX=-140 EndY=-7.4 EndZ=0
    g2: LineSegment StartX=-140 StartY=-7.4 StartZ=0 EndX=0 EndY=-7.4 EndZ=0
    g3: LineSegment StartX=0 StartY=-7.4 StartZ=0 EndX=0 EndY=0 EndZ=0
  constraints (10):
    c: Coincident(g0,g1)
    c: Coincident(g1,g2)
    c: Coincident(g2,g3)
    c: Coincident(g3,g0)
    c: Horizontal(g2)
    c: Vertical(g1)
    c: Vertical(g3)
    c: Coincident(g0,g-1)
    c: Coincident(g0,g-3)
    c: DistanceY(g3,g3) = 7.4
FEATURE [PartDesign::Pad] Pad001  label="ExtraGapSize"
  AddSubType = 0
  BaseFeature = -> Pad
  CheckUpToFaceLimits = true
  ClaimChildren = false
  Direction = (0,0,1)
  Fit = 0
  FitJoin = 0
  InnerFit = 0
  InnerFitJoin = 0
  InnerTaperAngle = 0
  InnerTaperAngleRev = 0
  Length = 5
  Length2 = 100
  NewSolid = false
  Profile = -> Sketch
  Suppress = false
  TreeRank = 0
  Type = 0
  _ProfileBasedVersion = 0
FEATURE [Sketcher::SketchObject] Sketch003
  ExternalGeometry = -> [Pad001]
  FullyConstrained = true
  MapMode = 5
  Support = -> [XY_Plane001]
  TreeRank = 0
  sketch-geometry (6):
    g0: LineSegment StartX=0 StartY=-7.4 StartZ=0 EndX=5 EndY=-7.4 EndZ=0
    g1: LineSegment StartX=5 StartY=-7.4 StartZ=0 EndX=5 EndY=103.2 EndZ=0
    g2: LineSegment StartX=5 StartY=103.2 StartZ=0 EndX=-140 EndY=103.2 EndZ=0
    g3: LineSegment StartX=0 StartY=93 StartZ=0 EndX=0 EndY=-7.4 EndZ=0
    g4: LineSegment StartX=-140 StartY=93 StartZ=0 EndX=-140 EndY=103.2 EndZ=0
    g5: LineSegment StartX=-140 StartY=93 StartZ=0 EndX=0 EndY=93 EndZ=0
  constraints (15):
    c: Coincident(g0,g1)
    c: Coincident(g1,g2)
    c: Coincident(g3,g0)
    c: Horizontal(g0)
    c: Horizontal(g2)
    c: Vertical(g1)
    c: DistanceX(g0,g0) = 5
    c: Coincident(g0,g-4)
    c: Coincident(g3,g-3)
    c: Coincident(g4,g-5)
    c: Vertical(g4)
    c: Coincident(g5,g4)
    c: Coincident(g5,g3)
    c: Coincident(g2,g4)
    c: DistanceY(g4,g4) = 10.2
FEATURE [PartDesign::Pad] Pad003  label="ExtraSideSize"
  AddSubType = 0
  BaseFeature = -> Pad001
  CheckUpToFaceLimits = true
  ClaimChildren = false
  Direction = (0,0,1)
  Fit = 0
  FitJoin = 0
  InnerFit = 0
  InnerFitJoin = 0
  InnerTaperAngle = 0
  InnerTaperAngleRev = 0
  Length = 5
  Length2 = 100
  NewSolid = false
  Profile = -> Sketch003
  Suppress = false
  TreeRank = 0
  Type = 0
  _ProfileBasedVersion = 0
FEATURE [Sketcher::SketchObject] Sketch004
  ExternalGeometry = -> [Pad003]
  FullyConstrained = true
  MapMode = 5
  Placement = pos=(0,0,5) rot=(0,0,1;0rad)
  Support = -> [Pad003]
  TreeRank = 0
  sketch-geometry (6):
    g0: LineSegment StartX=5 StartY=103.2 StartZ=0 EndX=-140 EndY=103.2 EndZ=0
    g1: LineSegment StartX=5 StartY=-7.4 StartZ=0 EndX=5 EndY=103.2 EndZ=0
    g2: LineSegment StartX=3 StartY=-7.4 StartZ=0 EndX=3 EndY=101.2 EndZ=0
    g3: LineSegment StartX=3 StartY=-7.4 StartZ=0 EndX=5 EndY=-7.4 EndZ=0
    g4: LineSegment StartX=-140 StartY=103.2 StartZ=0 EndX=-140 EndY=101.2 EndZ=0
    g5: LineSegment StartX=3 StartY=101.2 StartZ=0 EndX=-140 EndY=101.2 EndZ=0
  constraints (15):
    c: Coincident(g1,g0)
    c: Coincident(g0,g-3)
    c: Vertical(g2)
    c: Coincident(g1,g-3)
    c: PointOnObject(g2,g-4)
    c: Coincident(g3,g2)
    c: Coincident(g3,g1)
    c: Coincident(g0,g-5)
    c: Coincident(g4,g0)
    c: PointOnObject(g4,g-5)
    c: Coincident(g5,g2)
    c: Coincident(g5,g4)
    c: Horizontal(g5)
    c: DistanceX(g3,g3) = 2
    c: DistanceY(g4,g4) = 2
FEATURE [PartDesign::Pad] Pad004  label="SidePanel"
  AddSubType = 0
  BaseFeature = -> Pad003
  CheckUpToFaceLimits = true
  ClaimChildren = false
  Direction = (0,0,1)
  Fit = 0
  FitJoin = 0
  InnerFit = 0
  InnerFitJoin = 0
  InnerTaperAngle = 0
  InnerTaperAngleRev = 0
  Length = 51
  Length2 = 100
  NewSolid = false
  Profile = -> Sketch004
  Suppress = false
  TreeRank = 0
  Type = 0
  _ProfileBasedVersion = 0
FEATURE [Sketcher::SketchObject] Sketch006
  ExternalGeometry = -> [Pad004]
  FullyConstrained = true
  MapMode = 5
  Placement = pos=(0,0,5) rot=(0,0,1;0rad)
  TreeRank = 0
  sketch-geometry (3):
    g0: Circle CenterX=-75 CenterY=5 CenterZ=0 NormalX=0 NormalY=0 NormalZ=1 AngleXU=0 Radius=3.6
    g1: Circle CenterX=-75 CenterY=88 CenterZ=0 NormalX=0 NormalY=0 NormalZ=1 AngleXU=0 Radius=3.6
    g2: LineSegment [constr] StartX=-75 StartY=88 StartZ=0 EndX=-75 EndY=5 EndZ=0
  constraints (8):
    c: DistanceY(g-1,g0) = 5
    c: Diameter(g0) = 7.2
    c: DistanceY(g1,g-3) = 5
    c: Diameter(g1) = 7.2
    c: DistanceX(g-3,g1) = 65
    c: Coincident(g2,g1)
    c: Coincident(g2,g0)
    c: Vertical(g2)
FEATURE [PartDesign::Pad] Pad006  label="ProcessorColumn"
  AddSubType = 0
  BaseFeature = -> Pad004
  CheckUpToFaceLimits = true
  ClaimChildren = false
  Direction = (0,0,1)
  Fit = 0
  FitJoin = 0
  InnerFit = 0
  InnerFitJoin = 0
  InnerTaperAngle = 0
  InnerTaperAngleRev = 0
  Length = 12.4
  Length2 = 100
  NewSolid = false
  Profile = -> Sketch006
  Suppress = false
  TreeRank = 0
  Type = 0
  _ProfileBasedVersion = 0
FEATURE [Sketcher::SketchObject] Sketch009
  ExternalGeometry = -> [Pad006]
  FullyConstrained = true
  MapMode = 5
  Placement = pos=(-140,0,0) rot=(0.57735,-0.57735,-0.57735;2.0944rad)
  TreeRank = 0
  sketch-geometry (4):
    g0: LineSegment StartX=-101.25 StartY=3.5 StartZ=0 EndX=-13.55 EndY=3.5 EndZ=0
    g1: LineSegment StartX=-13.55 StartY=3.5 StartZ=0 EndX=-13.55 EndY=1.42 EndZ=0
    g2: LineSegment StartX=-13.55 StartY=1.42 StartZ=0 EndX=-101.25 EndY=1.42 EndZ=0
    g3: LineSegment StartX=-101.25 StartY=1.42 StartZ=0 EndX=-101.25 EndY=3.5 EndZ=0
  constraints (12):
    c: Coincident(g0,g1)
    c: Coincident(g1,g2)
    c: Coincident(g2,g3)
    c: Coincident(g3,g0)
    c: Horizontal(g0)
    c: Horizontal(g2)
    c: Vertical(g1)
    c: Vertical(g3)
    c: DistanceX(g-3,g0) = 1.95
    c: DistanceY(g1,g1) = 2.08
    c: DistanceY(g0,g-4) = 1.5
    c: DistanceX(g0,g-4) = 20.95
FEATURE [PartDesign::Pocket] Pocket003  label="PuzzleHole2"
  AddSubType = 1
  BaseFeature = -> Pad006
  CheckUpToFaceLimits = true
  ClaimChildren = false
  Fit = 0
  FitJoin = 0
  InnerFit = 0
  InnerFitJoin = 0
  InnerTaperAngle = 0
  InnerTaperAngleRev = 0
  Length = 11
  Length2 = 100
  NewSolid = false
  Profile = -> Sketch009
  Suppress = false
  TreeRank = 0
  Type = 0
  _ProfileBasedVersion = 0
  _Version = 0
FEATURE [Sketcher::SketchObject] Sketch010
  ExternalGeometry = -> [Pocket003]
  FullyConstrained = true
  MapMode = 5
  Placement = pos=(0,0,17.4) rot=(0,0,1;0rad)
  Support = -> [Pocket003]
  TreeRank = 1
  sketch-geometry (2):
    g0: Circle CenterX=-75 CenterY=88 CenterZ=0 NormalX=0 NormalY=0 NormalZ=1 AngleXU=0 Radius=2
    g1: Circle CenterX=-75 CenterY=5 CenterZ=0 NormalX=0 NormalY=0 NormalZ=1 AngleXU=0 Radius=2
  constraints (4):
    c: Coincident(g0,g-3)
    c: Coincident(g1,g-4)
    c: Diameter(g0) = 4
    c: Diameter(g1) = 4
FEATURE [PartDesign::Pocket] Pocket  label="ProcessorColumnHole"
  AddSubType = 1
  BaseFeature = -> Pocket003
  CheckUpToFaceLimits = true
  ClaimChildren = false
  Fit = 0
  FitJoin = 0
  InnerFit = 0
  InnerFitJoin = 0
  InnerTaperAngle = 0
  InnerTaperAngleRev = 0
  Length = 6.7
  Length2 = 100
  Linearize = true
  NewSolid = false
  Profile = -> Sketch010
  Suppress = false
  TreeRank = 2
  Type = 0
  _ProfileBasedVersion = 1
  _Version = 1
FEATURE [Sketcher::SketchObject] Sketch011
  ExternalGeometry = -> [Pocket]
  FullyConstrained = true
  MapMode = 5
  Placement = pos=(0,0,5) rot=(0,0,1;0rad)
  Support = -> [Pocket]
  TreeRank = 3
  sketch-geometry (6):
    g0: LineSegment StartX=-138.5 StartY=101.2 StartZ=0 EndX=-142 EndY=101.2 EndZ=0
    g1: LineSegment StartX=-142 StartY=101.2 StartZ=0 EndX=-142 EndY=100.2 EndZ=0
    g2: LineSegment StartX=-142 StartY=100.2 StartZ=0 EndX=-138.5 EndY=100.2 EndZ=0
    g3: LineSegment [constr] StartX=-138.5 StartY=100.2 StartZ=0 EndX=-138.5 EndY=101.2 EndZ=0
    g4: LineSegment StartX=-138.5 StartY=100.2 StartZ=0 EndX=-137.5 EndY=101.2 EndZ=0
    g5: LineSegment StartX=-137.5 StartY=101.2 StartZ=0 EndX=-138.5 EndY=101.2 EndZ=0
  constraints (17):
    c: Coincident(g0,g1)
    c: Coincident(g1,g2)
    c: Coincident(g2,g3)
    c: Coincident(g3,g0)
    c: Horizontal(g0)
    c: Horizontal(g2)
    c: Vertical(g1)
    c: Vertical(g3)
    c: PointOnObject(g0,g-3)
    c: DistanceX(g0,g-3) = 2
    c: DistanceX(g-3,g0) = 1.5
    c: DistanceY(g1,g1) = 1
    c: Coincident(g4,g2)
    c: PointOnObject(g4,g-3)
    c: Coincident(g5,g4)
    c: Coincident(g5,g0)
    c: Angle(g4,g3) = 0.785398
FEATURE [PartDesign::Pad] Pad007  label="PanelGuard"
  AddSubType = 0
  AlongSketchNormal = false
  BaseFeature = -> Pocket
  CheckUpToFaceLimits = true
  ClaimChildren = false
  Direction = (0,0,1)
  Fit = 0
  FitJoin = 0
  InnerFit = 0
  InnerFitJoin = 0
  InnerTaperAngle = 0
  InnerTaperAngleRev = 0
  Length = 10
  Length2 = 100
  Linearize = true
  NewSolid = false
  Profile = -> Sketch011
  Suppress = false
  TreeRank = 4
  Type = 3
  UpToFace = -> Pocket [Face24]
  _ProfileBasedVersion = 1
FEATURE [Sketcher::SketchObject] Sketch012
  ExternalGeometry = -> [Pad007]
  FullyConstrained = true
  MapMode = 5
  Placement = pos=(0,-7.4,0) rot=(1,0,0;1.5708rad)
  Support = -> [Pad007]
  TreeRank = 5
  sketch-geometry (4):
    g0: LineSegment StartX=-118.8 StartY=3.06 StartZ=0 EndX=2.8 EndY=3.06 EndZ=0
    g1: LineSegment StartX=2.8 StartY=3.06 StartZ=0 EndX=2.8 EndY=1.66 EndZ=0
    g2: LineSegment StartX=2.8 StartY=1.66 StartZ=0 EndX=-118.8 EndY=1.66 EndZ=0
    g3: LineSegment StartX=-118.8 StartY=1.66 StartZ=0 EndX=-118.8 EndY=3.06 EndZ=0
  constraints (12):
    c: Coincident(g0,g1)
    c: Coincident(g1,g2)
    c: Coincident(g2,g3)
    c: Coincident(g3,g0)
    c: Horizontal(g0)
    c: Horizontal(g2)
    c: Vertical(g1)
    c: Vertical(g3)
    c: DistanceX(g-4,g0) = 21.2
    c: DistanceX(g0,g-3) = 2.2
    c: DistanceY(g1,g1) = 1.4
    c: DistanceY(g0,g-3) = 1.94
FEATURE [PartDesign::Pad] Pad008  label="Puzzle1"
  AddSubType = 0
  AlongSketchNormal = false
  BaseFeature = -> Pad007
  CheckUpToFaceLimits = true
  ClaimChildren = false
  Direction = (0,-1,2e-16)
  Fit = 0
  FitJoin = 0
  InnerFit = 0
  InnerFitJoin = 0
  InnerTaperAngle = 0
  InnerTaperAngleRev = 0
  Length = 10
  Length2 = 100
  Linearize = true
  NewSolid = false
  Profile = -> Sketch012
  Suppress = false
  TreeRank = 6
  Type = 0
  _ProfileBasedVersion = 1
FEATURE [Sketcher::SketchObject] Sketch013
  ExternalGeometry = -> [Pad008]
  FullyConstrained = true
  MapMode = 5
  Placement = pos=(0,0,5) rot=(0,0,1;0rad)
  Support = -> [Pad008]
  TreeRank = 7
  sketch-geometry (4):
    g0: LineSegment StartX=3 StartY=101.2 StartZ=0 EndX=-4.2 EndY=101.2 EndZ=0
    g1: LineSegment StartX=-4.2 StartY=101.2 StartZ=0 EndX=-4.2 EndY=94 EndZ=0
    g2: LineSegment StartX=-4.2 StartY=94 StartZ=0 EndX=3 EndY=94 EndZ=0
    g3: LineSegment StartX=3 StartY=94 StartZ=0 EndX=3 EndY=101.2 EndZ=0
  constraints (11):
    c: Coincident(g0,g1)
    c: Coincident(g1,g2)
    c: Coincident(g2,g3)
    c: Coincident(g3,g0)
    c: Horizontal(g0)
    c: Horizontal(g2)
    c: Vertical(g1)
    c: Vertical(g3)
    c: Coincident(g0,g-4)
    c: DistanceY(g1,g1) = 7.2
    c: Equal(g1,g2)
FEATURE [PartDesign::Pad] Pad009  label="ColumnPart"
  AddSubType = 0
  AlongSketchNormal = false
  BaseFeature = -> Pad008
  CheckUpToFaceLimits = true
  ClaimChildren = false
  Direction = (0,0,1)
  Fit = 0
  FitJoin = 0
  InnerFit = 0
  InnerFitJoin = 0
  InnerTaperAngle = 0
  InnerTaperAngleRev = 0
  Length = 10
  Length2 = 100
  Linearize = true
  NewSolid = false
  Profile = -> Sketch013
  Suppress = false
  TreeRank = 8
  Type = 3
  UpToFace = -> Pad008 [Face25]
  _ProfileBasedVersion = 1
FEATURE [Sketcher::SketchObject] Sketch014
  ExternalGeometry = -> [Pad009]
  FullyConstrained = true
  MapMode = 5
  Placement = pos=(0,0,56) rot=(0,0,1;0rad)
  Support = -> [Pad009]
  TreeRank = 9
  sketch-geometry (3):
    g0: LineSegment [constr] StartX=-4.2 StartY=97.6 StartZ=0 EndX=-0.6 EndY=97.6 EndZ=0
    g1: LineSegment [constr] StartX=-0.6 StartY=97.6 StartZ=0 EndX=-0.6 EndY=94 EndZ=0
    g2: Circle CenterX=-0.6 CenterY=97.6 CenterZ=0 NormalX=0 NormalY=0 NormalZ=1 AngleXU=0 Radius=2
  constraints (7):
    c: Horizontal(g0)
    c: Coincident(g1,g0)
    c: Vertical(g1)
    c: Symmetric(g-4,g-4,g0)
    c: Symmetric(g-3,g-4,g1)
    c: Coincident(g2,g0)
    c: Diameter(g2) = 4
FEATURE [PartDesign::Pocket] Pocket004  label="ColumnPartHole"
  AddSubType = 1
  BaseFeature = -> Pad009
  CheckUpToFaceLimits = true
  ClaimChildren = false
  Fit = 0
  FitJoin = 0
  InnerFit = 0
  InnerFitJoin = 0
  InnerTaperAngle = 0
  InnerTaperAngleRev = 0
  Length = 6.7
  Length2 = 100
  Linearize = true
  NewSolid = false
  Profile = -> Sketch014
  Suppress = false
  TreeRank = 10
  Type = 0
  _ProfileBasedVersion = 1
  _Version = 1
FEATURE [Sketcher::SketchObject] Sketch015
  ExternalGeometry = -> [Pocket004]
  FullyConstrained = true
  MapMode = 5
  Placement = pos=(3,0,0) rot=(0.57735,-0.57735,-0.57735;2.0944rad)
  Support = -> [Pocket004]
  TreeRank = 11
  sketch-geometry (11):
    g0: LineSegment [constr] StartX=-88 StartY=13 StartZ=0 EndX=-1 EndY=13 EndZ=0
    g1: LineSegment StartX=-90 StartY=10.0067 StartZ=0 EndX=-90 EndY=5 EndZ=0
    g2: LineSegment StartX=-86 StartY=10.0067 StartZ=0 EndX=-86 EndY=5 EndZ=0
    g3: LineSegment [constr] StartX=-86 StartY=10.0067 StartZ=0 EndX=-90 EndY=10.0067 EndZ=0
    g4: LineSegment StartX=-86 StartY=5 StartZ=0 EndX=-90 EndY=5 EndZ=0
    g5: ArcOfCircle CenterX=-88 CenterY=13 CenterZ=0 NormalX=0 NormalY=0 NormalZ=1 AngleXU=0 Radius=3.6 StartAngle=5.30142 EndAngle=10.4065
    g6: LineSegment StartX=-3 StartY=10.0067 StartZ=0 EndX=-3 EndY=5 EndZ=0
    g7: LineSegment [constr] StartX=-3 StartY=10.0067 StartZ=0 EndX=1 EndY=10.0067 EndZ=0
    g8: LineSegment StartX=1 StartY=10.0067 StartZ=0 EndX=1 EndY=5 EndZ=0
    g9: LineSegment StartX=-3 StartY=5 StartZ=0 EndX=1 EndY=5 EndZ=0
    g10: ArcOfCircle CenterX=-1 CenterY=13 CenterZ=0 NormalX=0 NormalY=0 NormalZ=1 AngleXU=0 Radius=3.6 StartAngle=5.30142 EndAngle=10.4065
  constraints (32):
    c: DistanceX(g-3,g5) = 6
    c: DistanceY(g-3,g5) = 8
    c: Coincident(g0,g5)
    c: Coincident(g0,g10)
    c: Horizontal(g0)
    c: DistanceX(g0,g0) = 87
    c: PointOnObject(g1,g-4)
    c: Vertical(g1)
    c: PointOnObject(g2,g-4)
    c: Vertical(g2)
    c: Coincident(g3,g2)
    c: Coincident(g3,g1)
    c: Horizontal(g3)
    c: Coincident(g4,g2)
    c: Coincident(g4,g1)
    c: DistanceX(g3,g3) = 4
    c: Diameter(g5) = 7.2
    c: Coincident(g2,g5)
    c: Coincident(g5,g1)
    c: PointOnObject(g6,g-4)
    c: Vertical(g6)
    c: Coincident(g7,g6)
    c: Horizontal(g7)
    c: Coincident(g8,g7)
    c: Vertical(g8)
    c: Coincident(g9,g6)
    c: Coincident(g9,g8)
    c: Horizontal(g9)
    c: DistanceX(g7,g7) = 4
    c: Diameter(g10) = 7.2
    c: Coincident(g10,g6)
    c: Coincident(g10,g8)
FEATURE [PartDesign::Pad] Pad010  label="ColumnPowerSupply"
  AddSubType = 0
  AlongSketchNormal = false
  BaseFeature = -> Pocket004
  CheckUpToFaceLimits = true
  ClaimChildren = false
  Direction = (-1,0,0)
  Fit = 0
  FitJoin = 0
  InnerFit = 0
  InnerFitJoin = 0
  InnerTaperAngle = 0
  InnerTaperAngleRev = 0
  Length = 10
  Length2 = 100
  Linearize = true
  NewSolid = false
  Profile = -> Sketch015
  Suppress = false
  TreeRank = 12
  Type = 0
  _ProfileBasedVersion = 1
FEATURE [PartDesign::Fillet] Fillet
  AddSubType = 0
  Base = -> Pad010 [Edge37,Edge36]
  BaseFeature = -> Pad010
  NewSolid = false
  Radius = 2
  SupportTransform = false
  Suppress = false
  TreeRank = 13
FEATURE [PartDesign::Fillet] Fillet001
  AddSubType = 0
  Base = -> Fillet [Edge81,Edge44,Edge61,Edge33,Edge80,Edge67]
  BaseFeature = -> Fillet
  NewSolid = false
  Radius = 3
  SupportTransform = false
  Suppress = false
  TreeRank = 14
FEATURE [Sketcher::SketchObject] Sketch016
  ExternalGeometry = -> [Fillet001]
  FullyConstrained = true
  MapMode = 5
  Placement = pos=(-7,0,0) rot=(0.57735,-0.57735,-0.57735;2.0944rad)
  Support = -> [Fillet001]
  TreeRank = 15
  sketch-geometry (2):
    g0: Circle CenterX=-88 CenterY=13 CenterZ=0 NormalX=0 NormalY=0 NormalZ=1 AngleXU=0 Radius=2
    g1: Circle CenterX=-1 CenterY=13 CenterZ=0 NormalX=0 NormalY=0 NormalZ=1 AngleXU=0 Radius=2
  constraints (4):
    c: Coincident(g0,g-3)
    c: Coincident(g1,g-4)
    c: Diameter(g1) = 4
    c: Diameter(g0) = 4
FEATURE [PartDesign::Pocket] Pocket005  label="ColumnPowerSupplyHole"
  AddSubType = 1
  BaseFeature = -> Fillet001
  CheckUpToFaceLimits = true
  ClaimChildren = false
  Fit = 0
  FitJoin = 0
  InnerFit = 0
  InnerFitJoin = 0
  InnerTaperAngle = 0
  InnerTaperAngleRev = 0
  Length = 6.7
  Length2 = 100
  Linearize = true
  NewSolid = false
  Profile = -> Sketch016
  Suppress = false
  TreeRank = 16
  Type = 0
  _ProfileBasedVersion = 1
  _Version = 1
FEATURE [Sketcher::SketchObject] Sketch017
  ExternalGeometry = -> [Pocket005]
  FullyConstrained = true
  MapMode = 5
  Placement = pos=(0,101.2,0) rot=(1,0,0;1.5708rad)
  Support = -> [Pocket005]
  TreeRank = 17
  sketch-geometry (9):
    g0: LineSegment StartX=-19.1 StartY=53 StartZ=0 EndX=-8.6 EndY=53 EndZ=0
    g1: LineSegment StartX=-8.6 StartY=53 StartZ=0 EndX=-8.6 EndY=44 EndZ=0
    g2: LineSegment StartX=-8.6 StartY=44 StartZ=0 EndX=-19.1 EndY=44 EndZ=0
    g3: LineSegment StartX=-19.1 StartY=44 StartZ=0 EndX=-19.1 EndY=53 EndZ=0
    g4: LineSegment StartX=-18.6 StartY=23 StartZ=0 EndX=-8.6 EndY=23 EndZ=0
    g5: LineSegment StartX=-8.6 StartY=23 StartZ=0 EndX=-8.6 EndY=13 EndZ=0
    g6: LineSegment StartX=-8.6 StartY=13 StartZ=0 EndX=-18.6 EndY=13 EndZ=0
    g7: LineSegment StartX=-18.6 StartY=13 StartZ=0 EndX=-18.6 EndY=23 EndZ=0
    g8: LineSegment [constr] StartX=-8.6 StartY=44 StartZ=0 EndX=-8.6 EndY=23 EndZ=0
  constraints (26):
    c: Coincident(g0,g1)
    c: Coincident(g1,g2)
    c: Coincident(g2,g3)
    c: Coincident(g3,g0)
    c: Horizontal(g0)
    c: Horizontal(g2)
    c: Vertical(g1)
    c: Vertical(g3)
    c: DistanceX(g1,g-3) = 11.6
    c: DistanceY(g-3,g1) = 39
    c: DistanceX(g2,g2) = 10.5
    c: DistanceY(g3,g3) = 9
    c: Coincident(g4,g5)
    c: Coincident(g5,g6)
    c: Coincident(g6,g7)
    c: Coincident(g7,g4)
    c: Horizontal(g4)
    c: Horizontal(g6)
    c: Vertical(g5)
    c: Vertical(g7)
    c: DistanceY(g-3,g5) = 8
    c: DistanceY(g7,g7) = 10
    c: Coincident(g8,g1)
    c: Coincident(g8,g4)
    c: Vertical(g8)
    c: DistanceX(g4,g4) = 10
FEATURE [PartDesign::Pocket] Pocket006  label="ConnectorsHole"
  AddSubType = 1
  BaseFeature = -> Pocket005
  CheckUpToFaceLimits = true
  ClaimChildren = false
  Fit = 0
  FitJoin = 0
  InnerFit = 0
  InnerFitJoin = 0
  InnerTaperAngle = 0
  InnerTaperAngleRev = 0
  Length = 5
  Length2 = 100
  Linearize = true
  NewSolid = false
  Profile = -> Sketch017
  Suppress = false
  TreeRank = 18
  Type = 2
  _ProfileBasedVersion = 1
  _Version = 1
FEATURE [Sketcher::SketchObject] Sketch018
  ExternalGeometry = -> [Pocket006]
  FullyConstrained = true
  MapMode = 5
  Placement = pos=(0,103.2,0) rot=(0,0.707107,0.707107;3.14159rad)
  Support = -> [Pocket006]
  TreeRank = 19
  sketch-geometry (7):
    g0: LineSegment [constr] StartX=45 StartY=5 StartZ=0 EndX=45 EndY=30 EndZ=0
    g1: LineSegment [constr] StartX=45 StartY=30 StartZ=0 EndX=25 EndY=30 EndZ=0
    g2: Circle CenterX=33 CenterY=30 CenterZ=0 NormalX=0 NormalY=0 NormalZ=1 AngleXU=0 Radius=0.75
    g3: Circle CenterX=36 CenterY=30 CenterZ=0 NormalX=0 NormalY=0 NormalZ=1 AngleXU=0 Radius=0.75
    g4: Circle CenterX=39 CenterY=30 CenterZ=0 NormalX=0 NormalY=0 NormalZ=1 AngleXU=0 Radius=0.75
    g5: Circle CenterX=42 CenterY=30 CenterZ=0 NormalX=0 NormalY=0 NormalZ=1 AngleXU=0 Radius=0.75
    g6: Circle CenterX=45 CenterY=30 CenterZ=0 NormalX=0 NormalY=0 NormalZ=1 AngleXU=0 Radius=0.75
  constraints (21):
    c: PointOnObject(g0,g-3)
    c: Vertical(g0)
    c: Coincident(g1,g0)
    c: Horizontal(g1)
    c: PointOnObject(g2,g1)
    c: PointOnObject(g3,g1)
    c: PointOnObject(g4,g1)
    c: PointOnObject(g5,g1)
    c: DistanceY(g0,g0) = 25
    c: DistanceX(g1,g1) = 20
    c: Equal(g2,g3)
    c: Equal(g3,g4)
    c: Equal(g4,g5)
    c: DistanceX(g2,g3) = 3
    c: DistanceX(g3,g4) = 3
    c: DistanceX(g4,g5) = 3
    c: Coincident(g6,g0)
    c: Equal(g6,g5)
    c: DistanceX(g-3,g0) = 50
    c: Diameter(g2) = 1.5
    c: DistanceX(g5,g6) = 3
FEATURE [PartDesign::Pocket] Pocket007  label="AirHole"
  AddSubType = 1
  BaseFeature = -> Pocket006
  CheckUpToFaceLimits = true
  ClaimChildren = false
  Fit = 0
  FitJoin = 0
  InnerFit = 0
  InnerFitJoin = 0
  InnerTaperAngle = 0
  InnerTaperAngleRev = 0
  Length = 5
  Length2 = 100
  Linearize = true
  NewSolid = false
  Profile = -> Sketch018
  Suppress = false
  TreeRank = 20
  Type = 2
  _ProfileBasedVersion = 1
  _Version = 1
FEATURE [PartDesign::PolarPattern] PolarPattern
  AddSubType = 0
  Angle = 360
  Axis = -> Pocket007 [Edge182]
  BaseFeature = -> Pocket007
  CopyShape = false
  NewSolid = false
  Occurrences = 8
  OriginalSubs = -> [Pocket007]
  Originals = -> [Pocket007]
  ParallelTransform = true
  SubTransform = true
  Suppress = false
  TreeRank = 21
  _Version = 3
FEATURE [PartDesign::Body] Body
  AutoGroupSolids = false
  ClaimAllChildren = false
  ExportMode = 0
  Group = -> [LCS_0,Sketch_1,Pad,Sketch,Pad001,Sketch003,Pad003,Sketch004,Pad004,Sketch006,Pad006,Sketch009,Pocket003,Sketch010,Pocket,Sketch011,Pad007,Sketch012,Pad008,Sketch013,Pad009,Sketch014,Pocket004,Sketch015,Pad010,Fillet,Fillet001,Sketch016,Pocket005,Sketch017,Pocket006,Sketch018,Pocket007,PolarPattern]
  Origin = -> Origin001
  Tip = -> PolarPattern
  TreeRank = 0
  _ExportChildren = -> [LCS_0,Pad,Pad001,Pad003,Pad004,Pad006,Pocket003,Pocket,Pad007,Pad008,Pad009,Pocket004,Pad010,Fillet,Fillet001,Pocket005,Pocket006,Pocket007,PolarPattern]
  _GroupVersion = 1
FEATURE [App::Part] Part  label="FirstPartProcessor"
  ClaimAllChildren = false
  ExportMode = 1
  Group = -> [Body]
  Origin = -> Origin
  TreeRank = 0
  _ExportChildren = -> [Body]
  _GroupVersion = 1
---- part FirstPartProcessorTop.FCStd = doc fcstd_d741b76737f5 ----
FCSTD DOCUMENT  (FreeCAD 2022.430R26244 +4758 (Git))
Label: FirstPartProcessorTop
License: All rights reserved
LicenseURL: http://en.wikipedia.org/wiki/All_rights_reserved
objects: Sketcher::SketchObject×15, PartDesign::Pad×11, PartDesign::Pocket×4, PartDesign::Chamfer×2, PartDesign::CoordinateSystem×1, PartDesign::Fillet×1, PartDesign::Body×1, App::Part×1
note: 71 computed .brp shape members not serialized (recipe doc carries the construction recipe); baked Part::Feature solids carry a one-line shape summary decoded from their .brp

FEATURE [PartDesign::CoordinateSystem] LCS_0
  AttacherType = Attacher::AttachEngine3D
  MapMode = 2
  Support = -> [X_Axis001]
  TreeRank = 0
FEATURE [Sketcher::SketchObject] Sketch_1
  FullyConstrained = true
  TreeRank = 0
  sketch-geometry (4):
    g0: LineSegment StartX=0 StartY=0 StartZ=0 EndX=-140 EndY=0 EndZ=0
    g1: LineSegment StartX=-140 StartY=0 StartZ=0 EndX=-140 EndY=93 EndZ=0
    g2: LineSegment StartX=-140 StartY=93 StartZ=0 EndX=0 EndY=93 EndZ=0
    g3: LineSegment StartX=0 StartY=93 StartZ=0 EndX=0 EndY=0 EndZ=0
  constraints (11):
    c: Coincident(g0,g1)
    c: Coincident(g1,g2)
    c: Coincident(g2,g3)
    c: Coincident(g3,g0)
    c: Horizontal(g0)
    c: Horizontal(g2)
    c: Vertical(g1)
    c: Vertical(g3)
    c: Coincident(g0,g-1)
    c: DistanceY(g3,g3) = 93
    c: DistanceX(g2,g2) = 140
FEATURE [PartDesign::Pad] Pad  label="MainSupport"
  AddSubType = 0
  CheckUpToFaceLimits = true
  ClaimChildren = false
  Direction = (0,0,1)
  Fit = 0
  FitJoin = 0
  InnerFit = 0
  InnerFitJoin = 0
  InnerTaperAngle = 0
  InnerTaperAngleRev = 0
  Length = 5
  Length2 = 100
  NewSolid = false
  Profile = -> Sketch_1
  Suppress = false
  TreeRank = 0
  Type = 0
  _ProfileBasedVersion = 0
FEATURE [Sketcher::SketchObject] Sketch
  ExternalGeometry = -> [Pad]
  FullyConstrained = true
  MapMode = 5
  Support = -> [XY_Plane001]
  TreeRank = 0
  sketch-geometry (4):
    g0: LineSegment StartX=0 StartY=0 StartZ=0 EndX=-140 EndY=0 EndZ=0
    g1: LineSegment StartX=-140 StartY=0 StartZ=0 EndX=-140 EndY=-7.4 EndZ=0
    g2: LineSegment StartX=-140 StartY=-7.4 StartZ=0 EndX=0 EndY=-7.4 EndZ=0
    g3: LineSegment StartX=0 StartY=-7.4 StartZ=0 EndX=0 EndY=0 EndZ=0
  constraints (10):
    c: Coincident(g0,g1)
    c: Coincident(g1,g2)
    c: Coincident(g2,g3)
    c: Coincident(g3,g0)
    c: Horizontal(g2)
    c: Vertical(g1)
    c: Vertical(g3)
    c: Coincident(g0,g-1)
    c: Coincident(g0,g-3)
    c: DistanceY(g3,g3) = 7.4
FEATURE [PartDesign::Pad] Pad001  label="ExtraGapSize"
  AddSubType = 0
  BaseFeature = -> Pad
  CheckUpToFaceLimits = true
  ClaimChildren = false
  Direction = (0,0,1)
  Fit = 0
  FitJoin = 0
  InnerFit = 0
  InnerFitJoin = 0
  InnerTaperAngle = 0
  InnerTaperAngleRev = 0
  Length = 5
  Length2 = 100
  NewSolid = false
  Profile = -> Sketch
  Suppress = false
  TreeRank = 0
  Type = 0
  _ProfileBasedVersion = 0
FEATURE [Sketcher::SketchObject] Sketch011
  ExternalGeometry = -> [Pad001]
  FullyConstrained = true
  MapMode = 5
  Placement = pos=(0,0,5) rot=(0,0,1;0rad)
  Support = -> [Pad001]
  TreeRank = 21
  sketch-geometry (6):
    g0: LineSegment StartX=-140 StartY=93 StartZ=0 EndX=-140 EndY=103.2 EndZ=0
    g1: LineSegment StartX=-140 StartY=103.2 StartZ=0 EndX=5 EndY=103.2 EndZ=0
    g2: LineSegment StartX=5 StartY=103.2 StartZ=0 EndX=5 EndY=-7.4 EndZ=0
    g3: LineSegment StartX=5 StartY=-7.4 StartZ=0 EndX=0 EndY=-7.4 EndZ=0
    g4: LineSegment StartX=0 StartY=-7.4 StartZ=0 EndX=0 EndY=93 EndZ=0
    g5: LineSegment StartX=0 StartY=93 StartZ=0 EndX=-140 EndY=93 EndZ=0
  constraints (15):
    c: Coincident(g0,g-4)
    c: Vertical(g0)
    c: Coincident(g1,g0)
    c: Horizontal(g1)
    c: Coincident(g2,g1)
    c: Vertical(g2)
    c: Coincident(g3,g2)
    c: Coincident(g3,g-3)
    c: Coincident(g4,g3)
    c: Coincident(g4,g-4)
    c: Coincident(g5,g4)
    c: Coincident(g5,g0)
    c: Horizontal(g3)
    c: DistanceY(g0,g0) = 10.2
    c: DistanceX(g3,g3) = 5
FEATURE [PartDesign::Pad] Pad005  label="ExtraSideSize"
  AddSubType = 0
  AlongSketchNormal = false
  BaseFeature = -> Pad001
  CheckUpToFaceLimits = true
  ClaimChildren = false
  Direction = (0,0,1)
  Fit = 0
  FitJoin = 0
  InnerFit = 0
  InnerFitJoin = 0
  InnerTaperAngle = 0
  InnerTaperAngleRev = 0
  Length = 5
  Length2 = 100
  Linearize = true
  NewSolid = false
  Profile = -> Sketch011
  Reversed = true
  Suppress = false
  TreeRank = 22
  Type = 0
  _ProfileBasedVersion = 1
FEATURE [Sketcher::SketchObject] Sketch002
  ExternalGeometry = -> [Pad005]
  FullyConstrained = true
  MapMode = 5
  Placement = pos=(0,0,5) rot=(0,0,1;0rad)
  TreeRank = 3
  sketch-geometry (4):
    g0: LineSegment StartX=5 StartY=103.2 StartZ=0 EndX=-4.2 EndY=103.2 EndZ=0
    g1: LineSegment StartX=-4.2 StartY=103.2 StartZ=0 EndX=-4.2 EndY=94 EndZ=0
    g2: LineSegment StartX=-4.2 StartY=94 StartZ=0 EndX=5 EndY=94 EndZ=0
    g3: LineSegment StartX=5 StartY=94 StartZ=0 EndX=5 EndY=103.2 EndZ=0
  constraints (11):
    c: Coincident(g0,g1)
    c: Coincident(g1,g2)
    c: Coincident(g2,g3)
    c: Coincident(g3,g0)
    c: Horizontal(g0)
    c: Horizontal(g2)
    c: Vertical(g1)
    c: Vertical(g3)
    c: Coincident(g0,g-3)
    c: Equal(g2,g1)
    c: DistanceX(g2,g2) = 9.2
FEATURE [PartDesign::Pocket] Pocket  label="ColumnPartHole"
  AddSubType = 1
  BaseFeature = -> Pad005
  CheckUpToFaceLimits = true
  ClaimChildren = false
  Fit = 0
  FitJoin = 0
  InnerFit = 0
  InnerFitJoin = 0
  InnerTaperAngle = 0
  InnerTaperAngleRev = 0
  Length = 5
  Length2 = 100
  Linearize = true
  NewSolid = false
  Profile = -> Sketch002
  Suppress = false
  TreeRank = 4
  Type = 0
  _ProfileBasedVersion = 1
  _Version = 1
FEATURE [Sketcher::SketchObject] Sketch004
  ExternalGeometry = -> [Pocket]
  FullyConstrained = true
  MapMode = 5
  Placement = pos=(0,0,0) rot=(1,0,0;3.14159rad)
  TreeRank = 7
  sketch-geometry (4):
    g0: LineSegment StartX=5 StartY=-94 StartZ=0 EndX=3 EndY=-94 EndZ=0
    g1: LineSegment StartX=3 StartY=-94 StartZ=0 EndX=3 EndY=7.4 EndZ=0
    g2: LineSegment StartX=3 StartY=7.4 StartZ=0 EndX=5 EndY=7.4 EndZ=0
    g3: LineSegment StartX=5 StartY=7.4 StartZ=0 EndX=5 EndY=-94 EndZ=0
  constraints (10):
    c: Coincident(g0,g1)
    c: Coincident(g1,g2)
    c: Coincident(g2,g3)
    c: Coincident(g3,g0)
    c: Horizontal(g0)
    c: Horizontal(g2)
    c: Vertical(g1)
    c: Coincident(g0,g-3)
    c: Coincident(g2,g-3)
    c: DistanceX(g0,g0) = 2
FEATURE [PartDesign::Pad] Pad004  label="SidePanel"
  AddSubType = 0
  AlongSketchNormal = false
  BaseFeature = -> Pocket
  CheckUpToFaceLimits = true
  ClaimChildren = false
  Direction = (0,0,-1)
  Fit = 0
  FitJoin = 0
  InnerFit = 0
  InnerFitJoin = 0
  InnerTaperAngle = 0
  InnerTaperAngleRev = 0
  Length = 51
  Length2 = 100
  Linearize = true
  NewSolid = false
  Profile = -> Sketch004
  Suppress = false
  TreeRank = 8
  Type = 0
  _ProfileBasedVersion = 1
FEATURE [Sketcher::SketchObject] Sketch010
  ExternalGeometry = -> [Pad004]
  FullyConstrained = true
  MapMode = 5
  Placement = pos=(-140,0,0) rot=(0.57735,-0.57735,-0.57735;2.0944rad)
  TreeRank = 19
  sketch-geometry (4):
    g0: LineSegment StartX=-101.25 StartY=3.58 StartZ=0 EndX=-13.55 EndY=3.58 EndZ=0
    g1: LineSegment StartX=-13.55 StartY=3.58 StartZ=0 EndX=-13.55 EndY=1.5 EndZ=0
    g2: LineSegment StartX=-13.55 StartY=1.5 StartZ=0 EndX=-101.25 EndY=1.5 EndZ=0
    g3: LineSegment StartX=-101.25 StartY=1.5 StartZ=0 EndX=-101.25 EndY=3.58 EndZ=0
  constraints (12):
    c: Coincident(g0,g1)
    c: Coincident(g1,g2)
    c: Coincident(g2,g3)
    c: Coincident(g3,g0)
    c: Horizontal(g0)
    c: Horizontal(g2)
    c: Vertical(g1)
    c: Vertical(g3)
    c: DistanceX(g-3,g0) = 1.95
    c: DistanceX(g0,g-4) = 20.95
    c: DistanceY(g1,g1) = 2.08
    c: DistanceY(g-4,g1) = 1.5
FEATURE [PartDesign::Pocket] Pocket003  label="PuzzleHole1"
  AddSubType = 1
  BaseFeature = -> Pad004
  CheckUpToFaceLimits = true
  ClaimChildren = false
  Fit = 0
  FitJoin = 0
  InnerFit = 0
  InnerFitJoin = 0
  InnerTaperAngle = 0
  InnerTaperAngleRev = 0
  Length = 11
  Length2 = 100
  Linearize = true
  NewSolid = false
  Profile = -> Sketch010
  Suppress = false
  TreeRank = 20
  Type = 0
  _ProfileBasedVersion = 1
  _Version = 1
FEATURE [Sketcher::SketchObject] Sketch012
  ExternalGeometry = -> [Pocket003]
  FullyConstrained = true
  MapMode = 5
  Placement = pos=(0,0,0) rot=(1,0,0;3.14159rad)
  Support = -> [Pocket003]
  TreeRank = 23
  sketch-geometry (4):
    g0: LineSegment StartX=-140 StartY=-103.2 StartZ=0 EndX=-4.2 EndY=-103.2 EndZ=0
    g1: LineSegment StartX=-4.2 StartY=-103.2 StartZ=0 EndX=-4.2 EndY=-101.2 EndZ=0
    g2: LineSegment StartX=-4.2 StartY=-101.2 StartZ=0 EndX=-140 EndY=-101.2 EndZ=0
    g3: LineSegment StartX=-140 StartY=-101.2 StartZ=0 EndX=-140 EndY=-103.2 EndZ=0
  constraints (10):
    c: Coincident(g0,g1)
    c: Coincident(g1,g2)
    c: Coincident(g2,g3)
    c: Coincident(g3,g0)
    c: Horizontal(g2)
    c: Vertical(g1)
    c: Vertical(g3)
    c: Coincident(g0,g-3)
    c: Coincident(g-3,g0)
    c: DistanceY(g3,g3) = 2
FEATURE [PartDesign::Pad] Pad006  label="BackPanel"
  AddSubType = 0
  AlongSketchNormal = false
  BaseFeature = -> Pocket003
  CheckUpToFaceLimits = true
  ClaimChildren = false
  Direction = (0,0,-1)
  Fit = 0
  FitJoin = 0
  InnerFit = 0
  InnerFitJoin = 0
  InnerTaperAngle = 0
  InnerTaperAngleRev = 0
  Length = 51
  Length2 = 100
  Linearize = true
  NewSolid = false
  Profile = -> Sketch012
  Suppress = false
  TreeRank = 24
  Type = 0
  _ProfileBasedVersion = 1
FEATURE [Sketcher::SketchObject] Sketch013
  ExternalGeometry = -> [Pad006]
  FullyConstrained = true
  MapMode = 5
  Placement = pos=(0,0,0) rot=(1,0,0;3.14159rad)
  Support = -> [Pad006]
  TreeRank = 25
  sketch-geometry (6):
    g0: LineSegment StartX=-4.2 StartY=-101.2 StartZ=0 EndX=-6.2 EndY=-101.2 EndZ=0
    g1: LineSegment StartX=-6.2 StartY=-101.2 StartZ=0 EndX=-6.2 EndY=-92 EndZ=0
    g2: LineSegment StartX=-6.2 StartY=-92 StartZ=0 EndX=3 EndY=-92 EndZ=0
    g3: LineSegment StartX=3 StartY=-92 StartZ=0 EndX=3 EndY=-94 EndZ=0
    g4: LineSegment StartX=-4.2 StartY=-101.2 StartZ=0 EndX=-4.2 EndY=-94 EndZ=0
    g5: LineSegment StartX=-4.2 StartY=-94 StartZ=0 EndX=3 EndY=-94 EndZ=0
  constraints (15):
    c: Coincident(g0,g-4)
    c: Horizontal(g0)
    c: Coincident(g1,g0)
    c: Vertical(g1)
    c: Coincident(g2,g1)
    c: Horizontal(g2)
    c: Coincident(g3,g2)
    c: Coincident(g3,g-3)
    c: Vertical(g3)
    c: DistanceY(g3,g3) = 2
    c: Equal(g3,g0)
    c: Coincident(g4,g0)
    c: Coincident(g4,g-4)
    c: Coincident(g5,g4)
    c: Coincident(g5,g3)
FEATURE [PartDesign::Pad] Pad007  label="ColumnPartPanel"
  AddSubType = 0
  AlongSketchNormal = false
  BaseFeature = -> Pad006
  CheckUpToFaceLimits = true
  ClaimChildren = false
  Direction = (0,0,-1)
  Fit = 0
  FitJoin = 0
  InnerFit = 0
  InnerFitJoin = 0
  InnerTaperAngle = 0
  InnerTaperAngleRev = 0
  Length = 53
  Length2 = 100
  Linearize = true
  NewSolid = false
  Profile = -> Sketch013
  Suppress = false
  TreeRank = 26
  Type = 0
  _ProfileBasedVersion = 1
FEATURE [Sketcher::SketchObject] Sketch014
  ExternalGeometry = -> [Pad007]
  FullyConstrained = true
  MapMode = 5
  Placement = pos=(0,94,0) rot=(0,0.707107,0.707107;3.14159rad)
  Support = -> [Pad007]
  TreeRank = 27
  sketch-geometry (4):
    g0: LineSegment StartX=-5 StartY=-51 StartZ=0 EndX=4.2 EndY=-51 EndZ=0
    g1: LineSegment StartX=4.2 StartY=-51 StartZ=0 EndX=4.2 EndY=-46 EndZ=0
    g2: LineSegment StartX=4.2 StartY=-46 StartZ=0 EndX=-5 EndY=-46 EndZ=0
    g3: LineSegment StartX=-5 StartY=-46 StartZ=0 EndX=-5 EndY=-51 EndZ=0
  constraints (11):
    c: Coincident(g0,g1)
    c: Coincident(g1,g2)
    c: Coincident(g2,g3)
    c: Coincident(g3,g0)
    c: Horizontal(g0)
    c: Horizontal(g2)
    c: Vertical(g1)
    c: Vertical(g3)
    c: Coincident(g0,g-3)
    c: PointOnObject(g1,g-4)
    c: DistanceY(g3,g3) = 5
FEATURE [PartDesign::Pad] Pad008  label="HoleSupport"
  AddSubType = 0
  AlongSketchNormal = false
  BaseFeature = -> Pad007
  CheckUpToFaceLimits = true
  ClaimChildren = false
  Direction = (0,1,-2e-16)
  Fit = 0
  FitJoin = 0
  InnerFit = 0
  InnerFitJoin = 0
  InnerTaperAngle = 0
  InnerTaperAngleRev = 0
  Length = 10
  Length2 = 100
  Linearize = true
  NewSolid = false
  Profile = -> Sketch014
  Suppress = false
  TreeRank = 28
  Type = 3
  UpToFace = -> Pad007 [Face30]
  _ProfileBasedVersion = 1
FEATURE [Sketcher::SketchObject] Sketch015
  ExternalGeometry = -> [Pad008]
  FullyConstrained = true
  MapMode = 5
  Placement = pos=(0,-1.02e-14,-46) rot=(0,0,1;0rad)
  Support = -> [Pad008]
  TreeRank = 29
  sketch-geometry (3):
    g0: LineSegment [constr] StartX=-4.2 StartY=97.6 StartZ=0 EndX=-0.6 EndY=97.6 EndZ=0
    g1: LineSegment [constr] StartX=-0.6 StartY=97.6 StartZ=0 EndX=-0.6 EndY=94 EndZ=0
    g2: Circle CenterX=-0.6 CenterY=97.6 CenterZ=0 NormalX=0 NormalY=0 NormalZ=1 AngleXU=0 Radius=1.6
  constraints (9):
    c: PointOnObject(g0,g-3)
    c: Horizontal(g0)
    c: Coincident(g1,g0)
    c: PointOnObject(g1,g-4)
    c: Vertical(g1)
    c: DistanceY(g-4,g0) = 3.6
    c: DistanceX(g-4,g1) = 3.6
    c: Coincident(g2,g0)
    c: Diameter(g2) = 3.2
FEATURE [PartDesign::Pocket] Pocket004  label="Hole"
  AddSubType = 1
  BaseFeature = -> Pad008
  CheckUpToFaceLimits = true
  ClaimChildren = false
  Fit = 0
  FitJoin = 0
  InnerFit = 0
  InnerFitJoin = 0
  InnerTaperAngle = 0
  InnerTaperAngleRev = 0
  Length = 5
  Length2 = 100
  Linearize = true
  NewSolid = false
  Profile = -> Sketch015
  Suppress = false
  TreeRank = 30
  Type = 2
  _ProfileBasedVersion = 1
  _Version = 1
FEATURE [Sketcher::SketchObject] Sketch016
  ExternalGeometry = -> [Pocket004]
  FullyConstrained = true
  MapMode = 5
  Placement = pos=(0,-7.4,0) rot=(1,0,0;1.5708rad)
  Support = -> [Pocket004]
  TreeRank = 31
  sketch-geometry (4):
    g0: LineSegment StartX=-118.8 StartY=3.34 StartZ=0 EndX=2.8 EndY=3.34 EndZ=0
    g1: LineSegment StartX=2.8 StartY=3.34 StartZ=0 EndX=2.8 EndY=1.94 EndZ=0
    g2: LineSegment StartX=2.8 StartY=1.94 StartZ=0 EndX=-118.8 EndY=1.94 EndZ=0
    g3: LineSegment StartX=-118.8 StartY=1.94 StartZ=0 EndX=-118.8 EndY=3.34 EndZ=0
  constraints (12):
    c: Coincident(g0,g1)
    c: Coincident(g1,g2)
    c: Coincident(g2,g3)
    c: Coincident(g3,g0)
    c: Horizontal(g0)
    c: Horizontal(g2)
    c: Vertical(g1)
    c: Vertical(g3)
    c: DistanceX(g0,g-3) = 2.2
    c: DistanceY(g1,g1) = 1.4
    c: DistanceX(g-4,g0) = 21.2
    c: DistanceY(g-4,g2) = 1.94
FEATURE [PartDesign::Pad] Pad009  label="Puzzle1"
  AddSubType = 0
  AlongSketchNormal = false
  BaseFeature = -> Pocket004
  CheckUpToFaceLimits = true
  ClaimChildren = false
  Direction = (0,-1,2e-16)
  Fit = 0
  FitJoin = 0
  InnerFit = 0
  InnerFitJoin = 0
  InnerTaperAngle = 0
  InnerTaperAngleRev = 0
  Length = 10
  Length2 = 100
  Linearize = true
  NewSolid = false
  Profile = -> Sketch016
  Suppress = false
  TreeRank = 32
  Type = 0
  _ProfileBasedVersion = 1
FEATURE [PartDesign::Chamfer] Chamfer
  AddSubType = 0
  Angle = 45
  Base = -> Pad009 [Edge52,Edge49]
  BaseFeature = -> Pad009
  ChamferType = 0
  FlipDirection = false
  NewSolid = false
  Size = 2
  Size2 = 1
  SupportTransform = false
  Suppress = false
  TreeRank = 33
FEATURE [PartDesign::Chamfer] Chamfer001
  AddSubType = 0
  Angle = 45
  Base = -> Chamfer [Edge13,Edge15]
  BaseFeature = -> Chamfer
  ChamferType = 0
  FlipDirection = false
  NewSolid = false
  Size = 0.99
  Size2 = 1
  SupportTransform = false
  Suppress = false
  TreeRank = 34
FEATURE [Sketcher::SketchObject] Sketch017
  ExternalGeometry = -> [Chamfer001]
  FullyConstrained = true
  MapMode = 5
  Placement = pos=(3,0,0) rot=(0.57735,-0.57735,-0.57735;2.0944rad)
  Support = -> [Chamfer001]
  TreeRank = 35
  sketch-geometry (3):
    g0: LineSegment [constr] StartX=-88 StartY=-17 StartZ=0 EndX=-1 EndY=-17 EndZ=0
    g1: Circle CenterX=-88 CenterY=-17 CenterZ=0 NormalX=0 NormalY=0 NormalZ=1 AngleXU=0 Radius=3.6
    g2: Circle CenterX=-1 CenterY=-17 CenterZ=0 NormalX=0 NormalY=0 NormalZ=1 AngleXU=0 Radius=3.6
  constraints (8):
    c: Horizontal(g0)
    c: DistanceY(g-3,g0) = 34
    c: Coincident(g1,g0)
    c: Coincident(g2,g0)
    c: Diameter(g2) = 7.2
    c: Diameter(g1) = 7.2
    c: DistanceX(g0,g0) = 87
    c: DistanceX(g-3,g1) = 4
FEATURE [PartDesign::Pad] Pad010  label="PowerSupplyColumn"
  AddSubType = 0
  AlongSketchNormal = false
  BaseFeature = -> Chamfer001
  CheckUpToFaceLimits = true
  ClaimChildren = false
  Direction = (-1,0,0)
  Fit = 0
  FitJoin = 0
  InnerFit = 0
  InnerFitJoin = 0
  InnerTaperAngle = 0
  InnerTaperAngleRev = 0
  Length = 10
  Length2 = 100
  Linearize = true
  NewSolid = false
  Profile = -> Sketch017
  Suppress = false
  TreeRank = 36
  Type = 0
  _ProfileBasedVersion = 1
FEATURE [Sketcher::SketchObject] Sketch018
  ExternalGeometry = -> [Pad010]
  FullyConstrained = true
  MapMode = 5
  Placement = pos=(3,0,0) rot=(0.57735,-0.57735,-0.57735;2.0944rad)
  Support = -> [Pad010]
  TreeRank = 37
  sketch-geometry (6):
    g0: LineSegment StartX=-85.0067 StartY=-15 StartZ=0 EndX=-3.99333 EndY=-15 EndZ=0
    g1: LineSegment StartX=-85.0067 StartY=-19 StartZ=0 EndX=-3.99333 EndY=-19 EndZ=0
    g2: LineSegment [constr] StartX=-85.0067 StartY=-15 StartZ=0 EndX=-85.0067 EndY=-19 EndZ=0
    g3: LineSegment [constr] StartX=-3.99333 StartY=-15 StartZ=0 EndX=-3.99333 EndY=-19 EndZ=0
    g4: ArcOfCircle CenterX=-88 CenterY=-17 CenterZ=0 NormalX=0 NormalY=0 NormalZ=1 AngleXU=0 Radius=3.6 StartAngle=5.69415 EndAngle=6.87222
    g5: ArcOfCircle CenterX=-1 CenterY=-17 CenterZ=0 NormalX=0 NormalY=0 NormalZ=1 AngleXU=0 Radius=3.6 StartAngle=2.55256 EndAngle=3.73062
  constraints (16):
    c: PointOnObject(g0,g-3)
    c: PointOnObject(g0,g-4)
    c: Horizontal(g0)
    c: Horizontal(g1)
    c: Coincident(g2,g0)
    c: Coincident(g2,g1)
    c: Vertical(g2)
    c: Coincident(g3,g0)
    c: Coincident(g3,g1)
    c: Coincident(g4,g-3)
    c: Coincident(g4,g0)
    c: Coincident(g4,g1)
    c: Coincident(g5,g-4)
    c: Coincident(g5,g0)
    c: Coincident(g5,g1)
    c: DistanceY(g2,g2) = 4
FEATURE [PartDesign::Pad] Pad011  label="PowerSupplyColumnSupport"
  AddSubType = 0
  AlongSketchNormal = false
  BaseFeature = -> Pad010
  CheckUpToFaceLimits = true
  ClaimChildren = false
  Direction = (-1,0,0)
  Fit = 0
  FitJoin = 0
  InnerFit = 0
  InnerFitJoin = 0
  InnerTaperAngle = 0
  InnerTaperAngleRev = 0
  Length = 5
  Length2 = 100
  Linearize = true
  NewSolid = false
  Profile = -> Sketch018
  Suppress = false
  TreeRank = 38
  Type = 0
  _ProfileBasedVersion = 1
FEATURE [PartDesign::Fillet] Fillet
  AddSubType = 0
  Base = -> Pad011 [Edge116,Edge115,Edge117,Edge119,Edge118]
  BaseFeature = -> Pad011
  NewSolid = false
  Radius = 3
  SupportTransform = false
  Suppress = false
  TreeRank = 39
FEATURE [Sketcher::SketchObject] Sketch019
  ExternalGeometry = -> [Fillet]
  FullyConstrained = true
  MapMode = 5
  Placement = pos=(-7,0,0) rot=(-0.57735,0.57735,0.57735;4.18879rad)
  Support = -> [Fillet]
  TreeRank = 40
  sketch-geometry (2):
    g0: Circle CenterX=-88 CenterY=-17 CenterZ=0 NormalX=0 NormalY=0 NormalZ=1 AngleXU=0 Radius=2
    g1: Circle CenterX=-1 CenterY=-17 CenterZ=0 NormalX=0 NormalY=0 NormalZ=1 AngleXU=0 Radius=2
  constraints (4):
    c: Coincident(g0,g-4)
    c: Coincident(g1,g-3)
    c: Diameter(g0) = 4
    c: Diameter(g1) = 4
FEATURE [PartDesign::Pocket] Pocket005  label="InsertsHole"
  AddSubType = 1
  BaseFeature = -> Fillet
  CheckUpToFaceLimits = true
  ClaimChildren = false
  Fit = 0
  FitJoin = 0
  InnerFit = 0
  InnerFitJoin = 0
  InnerTaperAngle = 0
  InnerTaperAngleRev = 0
  Length = 6.7
  Length2 = 100
  Linearize = true
  NewSolid = false
  Profile = -> Sketch019
  Suppress = false
  TreeRank = 41
  Type = 0
  _ProfileBasedVersion = 1
  _Version = 1
FEATURE [Sketcher::SketchObject] Sketch020
  ExternalGeometry = -> [Pocket005]
  FullyConstrained = true
  MapMode = 5
  Placement = pos=(0,0,0) rot=(1,0,0;3.14159rad)
  Support = -> [Pocket005]
  TreeRank = 42
  sketch-geometry (7):
    g0: LineSegment StartX=-140 StartY=-101.2 StartZ=0 EndX=-142 EndY=-101.2 EndZ=0
    g1: LineSegment StartX=-142 StartY=-101.2 StartZ=0 EndX=-142 EndY=-100.2 EndZ=0
    g2: LineSegment StartX=-142 StartY=-100.2 StartZ=0 EndX=-138.5 EndY=-100.2 EndZ=0
    g3: LineSegment [constr] StartX=-138.5 StartY=-100.2 StartZ=0 EndX=-138.5 EndY=-101.2 EndZ=0
    g4: LineSegment StartX=-140 StartY=-101.2 StartZ=0 EndX=-138.5 EndY=-101.2 EndZ=0
    g5: LineSegment StartX=-138.5 StartY=-100.2 StartZ=0 EndX=-137.5 EndY=-101.2 EndZ=0
    g6: LineSegment StartX=-138.5 StartY=-101.2 StartZ=0 EndX=-137.5 EndY=-101.2 EndZ=0
  constraints (19):
    c: Coincident(g0,g-3)
    c: Horizontal(g0)
    c: Coincident(g1,g0)
    c: Vertical(g1)
    c: Coincident(g2,g1)
    c: Horizontal(g2)
    c: Coincident(g3,g2)
    c: Vertical(g3)
    c: Coincident(g4,g0)
    c: Coincident(g4,g3)
    c: Horizontal(g4)
    c: Coincident(g5,g2)
    c: Coincident(g6,g3)
    c: Coincident(g6,g5)
    c: Horizontal(g6)
    c: Angle(g3,g5) = 0.785398
    c: DistanceY(g1,g1) = 1
    c: DistanceX(g0,g0) = 2
    c: DistanceX(g4,g4) = 1.5
FEATURE [PartDesign::Pad] Pad012  label="PanelGuard"
  AddSubType = 0
  AlongSketchNormal = false
  BaseFeature = -> Pocket005
  CheckUpToFaceLimits = true
  ClaimChildren = false
  Direction = (0,0,-1)
  Fit = 0
  FitJoin = 0
  InnerFit = 0
  InnerFitJoin = 0
  InnerTaperAngle = 0
  InnerTaperAngleRev = 0
  Length = 10
  Length2 = 100
  Linearize = true
  NewSolid = false
  Profile = -> Sketch020
  Suppress = false
  TreeRank = 43
  Type = 3
  UpToFace = -> Pocket005 [Face45]
  _ProfileBasedVersion = 1
FEATURE [PartDesign::Body] Body
  AutoGroupSolids = false
  ClaimAllChildren = false
  ExportMode = 0
  Group = -> [LCS_0,Sketch_1,Pad,Sketch,Pad001,Pad005,Sketch002,Sketch011,Pocket,Sketch004,Pad004,Sketch010,Pocket003,Sketch012,Pad006,Sketch013,Pad007,Sketch014,Pad008,Sketch015,Pocket004,Sketch016,Pad009,Chamfer,Chamfer001,Sketch017,Pad010,Sketch018,Pad011,Fillet,Sketch019,Pocket005,Sketch020,Pad012]
  Origin = -> Origin001
  Tip = -> Pad012
  TreeRank = 0
  _ExportChildren = -> [LCS_0,Pad,Pad001,Pad005,Pocket,Pad004,Pocket003,Pad006,Pad007,Pad008,Pocket004,Pad009,Chamfer,Chamfer001,Pad010,Pad011,Fillet,Pocket005,Pad012]
  _GroupVersion = 1
FEATURE [App::Part] Part  label="FirstPartProcessorTop"
  ClaimAllChildren = false
  ExportMode = 1
  Group = -> [Body]
  Origin = -> Origin
  TreeRank = 0
  _ExportChildren = -> [Body]
  _GroupVersion = 1
---- part SecondPartPeripherals.FCStd = doc fcstd_02b2a3177532 ----
FCSTD DOCUMENT  (FreeCAD 2022.430R26244 +4758 (Git))
Label: SecondPartPeripherals
License: All rights reserved
LicenseURL: http://en.wikipedia.org/wiki/All_rights_reserved
objects: Sketcher::SketchObject×11, PartDesign::Pad×8, PartDesign::Pocket×3, PartDesign::CoordinateSystem×1, PartDesign::Fillet×1, PartDesign::Body×1, App::Part×1
note: 49 computed .brp shape members not serialized (recipe doc carries the construction recipe); baked Part::Feature solids carry a one-line shape summary decoded from their .brp

FEATURE [PartDesign::CoordinateSystem] LCS_0
  AttacherType = Attacher::AttachEngine3D
  MapMode = 2
  Support = -> [X_Axis001]
  TreeRank = 0
FEATURE [Sketcher::SketchObject] Sketch_1
  FullyConstrained = true
  TreeRank = 0
  sketch-geometry (4):
    g0: LineSegment StartX=0 StartY=0 StartZ=0 EndX=-63 EndY=0 EndZ=0
    g1: LineSegment StartX=-63 StartY=0 StartZ=0 EndX=-63 EndY=116 EndZ=0
    g2: LineSegment StartX=-63 StartY=116 StartZ=0 EndX=0 EndY=116 EndZ=0
    g3: LineSegment StartX=0 StartY=116 StartZ=0 EndX=0 EndY=0 EndZ=0
  constraints (11):
    c: Coincident(g0,g1)
    c: Coincident(g1,g2)
    c: Coincident(g2,g3)
    c: Coincident(g3,g0)
    c: Horizontal(g0)
    c: Horizontal(g2)
    c: Vertical(g1)
    c: Vertical(g3)
    c: Coincident(g0,g-1)
    c: DistanceY(g3,g3) = 116
    c: DistanceX(g2,g2) = 63
FEATURE [PartDesign::Pad] Pad  label="MainSupport"
  AddSubType = 0
  CheckUpToFaceLimits = true
  ClaimChildren = false
  Direction = (0,0,1)
  Fit = 0
  FitJoin = 0
  InnerFit = 0
  InnerFitJoin = 0
  InnerTaperAngle = 0
  InnerTaperAngleRev = 0
  Length = 5
  Length2 = 100
  NewSolid = false
  Profile = -> Sketch_1
  Suppress = false
  TreeRank = 0
  Type = 0
  _ProfileBasedVersion = 0
FEATURE [Sketcher::SketchObject] Sketch
  ExternalGeometry = -> [Pad]
  FullyConstrained = true
  MapMode = 5
  Support = -> [XY_Plane001]
  TreeRank = 1
  sketch-geometry (5):
    g0: LineSegment StartX=0 StartY=0 StartZ=0 EndX=-63 EndY=0 EndZ=0
    g1: LineSegment StartX=-63 StartY=0 StartZ=0 EndX=-63 EndY=-10.2 EndZ=0
    g2: LineSegment StartX=0 StartY=-15 StartZ=0 EndX=0 EndY=0 EndZ=0
    g3: LineSegment StartX=0 StartY=-15 StartZ=0 EndX=-27.2222 EndY=-10.2 EndZ=0
    g4: LineSegment StartX=-27.2222 StartY=-10.2 StartZ=0 EndX=-63 EndY=-10.2 EndZ=0
  constraints (13):
    c: Coincident(g0,g1)
    c: Coincident(g2,g0)
    c: Vertical(g1)
    c: Vertical(g2)
    c: Coincident(g0,g-1)
    c: Coincident(g0,g-3)
    c: DistanceY(g2,g2) = 15
    c: DistanceY(g1,g1) = 10.2
    c: Coincident(g3,g2)
    c: Coincident(g4,g3)
    c: Coincident(g4,g1)
    c: Horizontal(g4)
    c: Angle(g2,g3) = 1.39626
FEATURE [PartDesign::Pad] Pad001  label="ExtraPeripheralsSize"
  AddSubType = 0
  AlongSketchNormal = false
  BaseFeature = -> Pad
  CheckUpToFaceLimits = true
  ClaimChildren = false
  Direction = (0,0,1)
  Fit = 0
  FitJoin = 0
  InnerFit = 0
  InnerFitJoin = 0
  InnerTaperAngle = 0
  InnerTaperAngleRev = 0
  Length = 5
  Length2 = 100
  Linearize = true
  NewSolid = false
  Profile = -> Sketch
  Suppress = false
  TreeRank = 2
  Type = 0
  _ProfileBasedVersion = 1
FEATURE [Sketcher::SketchObject] Sketch001
  ExternalGeometry = -> [Pad001]
  FullyConstrained = true
  MapMode = 5
  Support = -> [XY_Plane001]
  TreeRank = 3
  sketch-geometry (4):
    g0: LineSegment StartX=-63 StartY=116 StartZ=0 EndX=-68 EndY=116 EndZ=0
    g1: LineSegment StartX=-68 StartY=116 StartZ=0 EndX=-68 EndY=-10.2 EndZ=0
    g2: LineSegment StartX=-68 StartY=-10.2 StartZ=0 EndX=-63 EndY=-10.2 EndZ=0
    g3: LineSegment StartX=-63 StartY=-10.2 StartZ=0 EndX=-63 EndY=116 EndZ=0
  constraints (10):
    c: Coincident(g0,g1)
    c: Coincident(g1,g2)
    c: Coincident(g2,g3)
    c: Coincident(g3,g0)
    c: Horizontal(g0)
    c: Horizontal(g2)
    c: Vertical(g1)
    c: Coincident(g0,g-3)
    c: Coincident(g2,g-4)
    c: DistanceX(g2,g2) = 5
FEATURE [PartDesign::Pad] Pad002  label="ExtraSideSize"
  AddSubType = 0
  AlongSketchNormal = false
  BaseFeature = -> Pad001
  CheckUpToFaceLimits = true
  ClaimChildren = false
  Direction = (0,0,1)
  Fit = 0
  FitJoin = 0
  InnerFit = 0
  InnerFitJoin = 0
  InnerTaperAngle = 0
  InnerTaperAngleRev = 0
  Length = 5
  Length2 = 100
  Linearize = true
  NewSolid = false
  Profile = -> Sketch001
  Suppress = false
  TreeRank = 4
  Type = 0
  _ProfileBasedVersion = 1
FEATURE [Sketcher::SketchObject] Sketch002
  ExternalGeometry = -> [Pad002]
  FullyConstrained = true
  MapMode = 5
  Placement = pos=(0,0,5) rot=(0,0,1;0rad)
  Support = -> [Pad002]
  TreeRank = 5
  sketch-geometry (9):
    g0: LineSegment StartX=-68 StartY=116 StartZ=0 EndX=-68 EndY=-10.2 EndZ=0
    g1: LineSegment StartX=-68 StartY=-10.2 StartZ=0 EndX=-27.2222 EndY=-10.2 EndZ=0
    g2: LineSegment StartX=-27.2222 StartY=-8.2 StartZ=0 EndX=-66 EndY=-8.2 EndZ=0
    g3: LineSegment StartX=-66 StartY=-8.2 StartZ=0 EndX=-66 EndY=116 EndZ=0
    g4: LineSegment StartX=-66 StartY=116 StartZ=0 EndX=-68 EndY=116 EndZ=0
    g5: LineSegment [constr] StartX=-27.2222 StartY=-10.2 StartZ=0 EndX=-27.2222 EndY=-8.2 EndZ=0
    g6: LineSegment StartX=-27.2222 StartY=-10.2 StartZ=0 EndX=0 EndY=-15 EndZ=0
    g7: LineSegment StartX=0 StartY=-15 StartZ=0 EndX=0 EndY=-13 EndZ=0
    g8: LineSegment StartX=-27.2222 StartY=-8.2 StartZ=0 EndX=0 EndY=-13 EndZ=0
  constraints (22):
    c: Coincident(g0,g-3)
    c: Coincident(g0,g-3)
    c: Coincident(g1,g0)
    c: Horizontal(g2)
    c: Coincident(g3,g2)
    c: Vertical(g3)
    c: Coincident(g4,g3)
    c: Coincident(g4,g0)
    c: Horizontal(g4)
    c: DistanceX(g4,g4) = 2
    c: Coincident(g1,g-4)
    c: Coincident(g5,g1)
    c: Vertical(g5)
    c: DistanceY(g5,g5) = 2
    c: Coincident(g2,g5)
    c: Coincident(g6,g1)
    c: Coincident(g6,g-5)
    c: Coincident(g7,g6)
    c: Vertical(g7)
    c: DistanceY(g7,g7) = 2
    c: Coincident(g8,g2)
    c: Coincident(g8,g7)
FEATURE [PartDesign::Pad] Pad003  label="SidePanel"
  AddSubType = 0
  AlongSketchNormal = false
  BaseFeature = -> Pad002
  CheckUpToFaceLimits = true
  ClaimChildren = false
  Direction = (0,0,1)
  Fit = 0
  FitJoin = 0
  InnerFit = 0
  InnerFitJoin = 0
  InnerTaperAngle = 0
  InnerTaperAngleRev = 0
  Length = 51
  Length2 = 100
  Linearize = true
  NewSolid = false
  Profile = -> Sketch002
  Suppress = false
  TreeRank = 6
  Type = 0
  _ProfileBasedVersion = 1
FEATURE [Sketcher::SketchObject] Sketch003
  ExternalGeometry = -> [Pad003]
  FullyConstrained = true
  MapMode = 5
  Placement = pos=(0,0,5) rot=(0,0,1;0rad)
  Support = -> [Pad003]
  TreeRank = 7
  sketch-geometry (4):
    g0: LineSegment StartX=-66 StartY=-8.2 StartZ=0 EndX=-58.8 EndY=-8.2 EndZ=0
    g1: LineSegment StartX=-58.8 StartY=-8.2 StartZ=0 EndX=-58.8 EndY=-1 EndZ=0
    g2: LineSegment StartX=-58.8 StartY=-1 StartZ=0 EndX=-66 EndY=-1 EndZ=0
    g3: LineSegment StartX=-66 StartY=-1 StartZ=0 EndX=-66 EndY=-8.2 EndZ=0
  constraints (11):
    c: Coincident(g0,g1)
    c: Coincident(g1,g2)
    c: Coincident(g2,g3)
    c: Coincident(g3,g0)
    c: Vertical(g3)
    c: Coincident(g0,g-3)
    c: Equal(g3,g0)
    c: Equal(g3,g1)
    c: Horizontal(g0)
    c: Vertical(g1)
    c: DistanceX(g2,g2) = 7.2
FEATURE [PartDesign::Pad] Pad004  label="ColumnPart"
  AddSubType = 0
  AlongSketchNormal = false
  BaseFeature = -> Pad003
  CheckUpToFaceLimits = true
  ClaimChildren = false
  Direction = (0,0,1)
  Fit = 0
  FitJoin = 0
  InnerFit = 0
  InnerFitJoin = 0
  InnerTaperAngle = 0
  InnerTaperAngleRev = 0
  Length = 51
  Length2 = 100
  Linearize = true
  NewSolid = false
  Profile = -> Sketch003
  Suppress = false
  TreeRank = 8
  Type = 0
  _ProfileBasedVersion = 1
FEATURE [Sketcher::SketchObject] Sketch004
  ExternalGeometry = -> [Pad004]
  FullyConstrained = true
  MapMode = 5
  Placement = pos=(0,0,56) rot=(0,0,1;0rad)
  Support = -> [Pad004]
  TreeRank = 9
  sketch-geometry (3):
    g0: LineSegment [constr] StartX=-62.4 StartY=-1 StartZ=0 EndX=-62.4 EndY=-4.6 EndZ=0
    g1: LineSegment [constr] StartX=-62.4 StartY=-4.6 StartZ=0 EndX=-58.8 EndY=-4.6 EndZ=0
    g2: Circle CenterX=-62.4 CenterY=-4.6 CenterZ=0 NormalX=0 NormalY=0 NormalZ=1 AngleXU=0 Radius=2
  constraints (7):
    c: Vertical(g0)
    c: Coincident(g1,g0)
    c: Horizontal(g1)
    c: Symmetric(g-4,g-3,g0)
    c: Symmetric(g-4,g-4,g1)
    c: Coincident(g2,g0)
    c: Diameter(g2) = 4
FEATURE [PartDesign::Pocket] Pocket  label="ColumnPartHole"
  AddSubType = 1
  BaseFeature = -> Pad004
  CheckUpToFaceLimits = true
  ClaimChildren = false
  Fit = 0
  FitJoin = 0
  InnerFit = 0
  InnerFitJoin = 0
  InnerTaperAngle = 0
  InnerTaperAngleRev = 0
  Length = 6.7
  Length2 = 100
  Linearize = true
  NewSolid = false
  Profile = -> Sketch004
  Suppress = false
  TreeRank = 10
  Type = 0
  _ProfileBasedVersion = 1
  _Version = 1
FEATURE [Sketcher::SketchObject] Sketch005
  ExternalGeometry = -> [Pocket]
  FullyConstrained = true
  MapMode = 5
  Placement = pos=(0,0,0) rot=(0.57735,0.57735,0.57735;2.0944rad)
  Support = -> [Pocket]
  TreeRank = 11
  sketch-geometry (4):
    g0: LineSegment StartX=94.8 StartY=3.06 StartZ=0 EndX=-12.8 EndY=3.06 EndZ=0
    g1: LineSegment StartX=-12.8 StartY=3.06 StartZ=0 EndX=-12.8 EndY=1.66 EndZ=0
    g2: LineSegment StartX=-12.8 StartY=1.66 StartZ=0 EndX=94.8 EndY=1.66 EndZ=0
    g3: LineSegment StartX=94.8 StartY=1.66 StartZ=0 EndX=94.8 EndY=3.06 EndZ=0
  constraints (12):
    c: Coincident(g0,g1)
    c: Coincident(g1,g2)
    c: Coincident(g2,g3)
    c: Coincident(g3,g0)
    c: Horizontal(g0)
    c: Horizontal(g2)
    c: Vertical(g1)
    c: Vertical(g3)
    c: DistanceX(g0,g-3) = 21.2
    c: DistanceX(g-4,g0) = 2.2
    c: DistanceY(g0,g-4) = 1.94
    c: DistanceY(g1,g1) = 1.4
FEATURE [PartDesign::Pad] Pad005  label="Puzzle1"
  AddSubType = 0
  AlongSketchNormal = false
  BaseFeature = -> Pocket
  CheckUpToFaceLimits = true
  ClaimChildren = false
  Direction = (1,0,0)
  Fit = 0
  FitJoin = 0
  InnerFit = 0
  InnerFitJoin = 0
  InnerTaperAngle = 0
  InnerTaperAngleRev = 0
  Length = 10
  Length2 = 100
  Linearize = true
  NewSolid = false
  Profile = -> Sketch005
  Suppress = false
  TreeRank = 12
  Type = 0
  _ProfileBasedVersion = 1
FEATURE [Sketcher::SketchObject] Sketch006
  ExternalGeometry = -> [Pad005]
  FullyConstrained = true
  MapMode = 5
  Placement = pos=(0,0,5) rot=(0,0,1;0rad)
  Support = -> [Pad005]
  TreeRank = 13
  sketch-geometry (2):
    g0: Circle CenterX=-58 CenterY=5 CenterZ=0 NormalX=0 NormalY=0 NormalZ=1 AngleXU=0 Radius=3.6
    g1: Circle CenterX=-58 CenterY=111 CenterZ=0 NormalX=0 NormalY=0 NormalZ=1 AngleXU=0 Radius=3.6
  constraints (6):
    c: DistanceY(g-3,g0) = 5
    c: DistanceX(g-3,g0) = 5
    c: DistanceX(g-3,g1) = 5
    c: DistanceY(g1,g-3) = 5
    c: Diameter(g1) = 7.2
    c: Diameter(g0) = 7.2
FEATURE [PartDesign::Pad] Pad006  label="MotherboardColumn"
  AddSubType = 0
  AlongSketchNormal = false
  BaseFeature = -> Pad005
  CheckUpToFaceLimits = true
  ClaimChildren = false
  Direction = (0,0,1)
  Fit = 0
  FitJoin = 0
  InnerFit = 0
  InnerFitJoin = 0
  InnerTaperAngle = 0
  InnerTaperAngleRev = 0
  Length = 12.4
  Length2 = 100
  Linearize = true
  NewSolid = false
  Profile = -> Sketch006
  Suppress = false
  TreeRank = 14
  Type = 0
  _ProfileBasedVersion = 1
FEATURE [Sketcher::SketchObject] Sketch007
  ExternalGeometry = -> [Pad006]
  FullyConstrained = true
  MapMode = 5
  Placement = pos=(0,0,17.4) rot=(0,0,1;0rad)
  Support = -> [Pad006]
  TreeRank = 15
  sketch-geometry (2):
    g0: Circle CenterX=-58 CenterY=5 CenterZ=0 NormalX=0 NormalY=0 NormalZ=1 AngleXU=0 Radius=2
    g1: Circle CenterX=-58 CenterY=111 CenterZ=0 NormalX=0 NormalY=0 NormalZ=1 AngleXU=0 Radius=2
  constraints (4):
    c: Coincident(g0,g-3)
    c: Coincident(g1,g-4)
    c: Diameter(g1) = 4
    c: Diameter(g0) = 4
FEATURE [PartDesign::Pocket] Pocket001  label="ColumnInsertHole"
  AddSubType = 1
  BaseFeature = -> Pad006
  CheckUpToFaceLimits = true
  ClaimChildren = false
  Fit = 0
  FitJoin = 0
  InnerFit = 0
  InnerFitJoin = 0
  InnerTaperAngle = 0
  InnerTaperAngleRev = 0
  Length = 6.7
  Length2 = 100
  Linearize = true
  NewSolid = false
  Profile = -> Sketch007
  Suppress = false
  TreeRank = 16
  Type = 0
  _ProfileBasedVersion = 1
  _Version = 1
FEATURE [Sketcher::SketchObject] Sketch008
  ExternalGeometry = -> [Pocket001]
  FullyConstrained = true
  MapMode = 5
  Placement = pos=(0,116,0) rot=(0,0.707107,0.707107;3.14159rad)
  Support = -> [Pocket001]
  TreeRank = 17
  sketch-geometry (4):
    g0: LineSegment StartX=20.95 StartY=3.5 StartZ=0 EndX=66.05 EndY=3.5 EndZ=0
    g1: LineSegment StartX=66.05 StartY=3.5 StartZ=0 EndX=66.05 EndY=1.42 EndZ=0
    g2: LineSegment StartX=66.05 StartY=1.42 StartZ=0 EndX=20.95 EndY=1.42 EndZ=0
    g3: LineSegment StartX=20.95 StartY=1.42 StartZ=0 EndX=20.95 EndY=3.5 EndZ=0
  constraints (12):
    c: Coincident(g0,g1)
    c: Coincident(g1,g2)
    c: Coincident(g2,g3)
    c: Coincident(g3,g0)
    c: Horizontal(g0)
    c: Horizontal(g2)
    c: Vertical(g1)
    c: Vertical(g3)
    c: DistanceX(g-3,g0) = 20.95
    c: DistanceY(g0,g-4) = 1.5
    c: DistanceX(g0,g-4) = 1.95
    c: DistanceY(g1,g1) = 2.08
FEATURE [PartDesign::Pocket] Pocket002  label="PuzzleHole1"
  AddSubType = 1
  BaseFeature = -> Pocket001
  CheckUpToFaceLimits = true
  ClaimChildren = false
  Fit = 0
  FitJoin = 0
  InnerFit = 0
  InnerFitJoin = 0
  InnerTaperAngle = 0
  InnerTaperAngleRev = 0
  Length = 11
  Length2 = 100
  Linearize = true
  NewSolid = false
  Profile = -> Sketch008
  Suppress = false
  TreeRank = 18
  Type = 0
  _ProfileBasedVersion = 1
  _Version = 1
FEATURE [Sketcher::SketchObject] Sketch009
  ExternalGeometry = -> [Pocket002]
  FullyConstrained = true
  MapMode = 5
  Placement = pos=(0,0,5) rot=(0,0,1;0rad)
  Support = -> [Pocket002]
  TreeRank = 19
  sketch-geometry (6):
    g0: LineSegment [constr] StartX=0 StartY=-13 StartZ=0 EndX=0 EndY=-12 EndZ=0
    g1: LineSegment StartX=0 StartY=-12 StartZ=0 EndX=-5.67128 EndY=-12 EndZ=0
    g2: LineSegment StartX=0 StartY=-12 StartZ=0 EndX=1.5 EndY=-12 EndZ=0
    g3: LineSegment StartX=1.5 StartY=-12 StartZ=0 EndX=1.5 EndY=-13 EndZ=0
    g4: LineSegment StartX=1.5 StartY=-13 StartZ=0 EndX=0 EndY=-13 EndZ=0
    g5: LineSegment StartX=0 StartY=-13 StartZ=0 EndX=-5.67128 EndY=-12 EndZ=0
  constraints (16):
    c: Coincident(g0,g-3)
    c: Vertical(g0)
    c: Coincident(g1,g0)
    c: PointOnObject(g1,g-3)
    c: Horizontal(g1)
    c: Coincident(g2,g1)
    c: Horizontal(g2)
    c: Coincident(g3,g2)
    c: Vertical(g3)
    c: Coincident(g4,g3)
    c: Coincident(g4,g-3)
    c: Horizontal(g4)
    c: DistanceX(g2,g2) = 1.5
    c: DistanceY(g3,g3) = 1
    c: Coincident(g5,g4)
    c: Coincident(g5,g1)
FEATURE [PartDesign::Pad] Pad007  label="PanelGuard1"
  AddSubType = 0
  AlongSketchNormal = false
  BaseFeature = -> Pocket002
  CheckUpToFaceLimits = true
  ClaimChildren = false
  Direction = (0,0,1)
  Fit = 0
  FitJoin = 0
  InnerFit = 0
  InnerFitJoin = 0
  InnerTaperAngle = 0
  InnerTaperAngleRev = 0
  Length = 51
  Length2 = 100
  Linearize = true
  NewSolid = false
  Profile = -> Sketch009
  Suppress = false
  TreeRank = 20
  Type = 0
  _ProfileBasedVersion = 1
FEATURE [PartDesign::Fillet] Fillet
  AddSubType = 0
  Base = -> Pad007 [Edge21,Edge20]
  BaseFeature = -> Pad007
  NewSolid = false
  Radius = 2
  SupportTransform = false
  Suppress = false
  TreeRank = 21
FEATURE [PartDesign::Body] Body
  AutoGroupSolids = false
  ClaimAllChildren = false
  ExportMode = 0
  Group = -> [LCS_0,Sketch_1,Pad,Sketch,Pad001,Sketch001,Pad002,Sketch002,Pad003,Sketch003,Pad004,Sketch004,Pocket,Sketch005,Pad005,Sketch006,Pad006,Sketch007,Pocket001,Sketch008,Pocket002,Sketch009,Pad007,Fillet]
  Origin = -> Origin001
  Tip = -> Fillet
  TreeRank = 0
  _ExportChildren = -> [LCS_0,Pad,Pad001,Pad002,Pad003,Pad004,Pocket,Pad005,Pad006,Pocket001,Pocket002,Pad007,Fillet]
  _GroupVersion = 1
FEATURE [App::Part] Part  label="SecondPartPeripherals"
  ClaimAllChildren = false
  ExportMode = 1
  Group = -> [Body]
  Origin = -> Origin
  TreeRank = 0
  _ExportChildren = -> [Body]
  _GroupVersion = 1
---- part SecondPartPeripheralsTop.FCStd = doc fcstd_5ff440fee658 ----
FCSTD DOCUMENT  (FreeCAD 2022.430R26244 +4758 (Git))
Label: SecondPartPeripheralsTop
License: All rights reserved
LicenseURL: http://en.wikipedia.org/wiki/All_rights_reserved
objects: Sketcher::SketchObject×14, PartDesign::Pad×11, PartDesign::Pocket×3, PartDesign::CoordinateSystem×1, PartDesign::Chamfer×1, PartDesign::Body×1, App::Part×1
note: 61 computed .brp shape members not serialized (recipe doc carries the construction recipe); baked Part::Feature solids carry a one-line shape summary decoded from their .brp

FEATURE [PartDesign::CoordinateSystem] LCS_0
  AttacherType = Attacher::AttachEngine3D
  MapMode = 2
  Support = -> [X_Axis001]
  TreeRank = 0
FEATURE [Sketcher::SketchObject] Sketch_1
  FullyConstrained = true
  TreeRank = 0
  sketch-geometry (4):
    g0: LineSegment StartX=0 StartY=0 StartZ=0 EndX=-40 EndY=0 EndZ=0
    g1: LineSegment StartX=-40 StartY=0 StartZ=0 EndX=-40 EndY=116 EndZ=0
    g2: LineSegment StartX=-40 StartY=116 StartZ=0 EndX=0 EndY=116 EndZ=0
    g3: LineSegment StartX=0 StartY=116 StartZ=0 EndX=0 EndY=0 EndZ=0
  constraints (11):
    c: Coincident(g0,g1)
    c: Coincident(g1,g2)
    c: Coincident(g2,g3)
    c: Coincident(g3,g0)
    c: Horizontal(g0)
    c: Horizontal(g2)
    c: Vertical(g1)
    c: Vertical(g3)
    c: Coincident(g0,g-1)
    c: DistanceY(g3,g3) = 116
    c: DistanceX(g2,g2) = 40
FEATURE [PartDesign::Pad] Pad  label="MainSupport"
  AddSubType = 0
  CheckUpToFaceLimits = true
  ClaimChildren = false
  Direction = (0,0,1)
  Fit = 0
  FitJoin = 0
  InnerFit = 0
  InnerFitJoin = 0
  InnerTaperAngle = 0
  InnerTaperAngleRev = 0
  Length = 5
  Length2 = 100
  NewSolid = false
  Profile = -> Sketch_1
  Suppress = false
  TreeRank = 0
  Type = 0
  _ProfileBasedVersion = 0
FEATURE [Sketcher::SketchObject] Sketch
  ExternalGeometry = -> [Pad]
  FullyConstrained = true
  MapMode = 5
  Support = -> [XY_Plane001]
  TreeRank = 1
  sketch-geometry (5):
    g0: LineSegment StartX=0 StartY=0 StartZ=0 EndX=-40 EndY=0 EndZ=0
    g1: LineSegment StartX=-40 StartY=0 StartZ=0 EndX=-40 EndY=-10.2 EndZ=0
    g2: LineSegment StartX=0 StartY=-15 StartZ=0 EndX=0 EndY=0 EndZ=0
    g3: LineSegment StartX=0 StartY=-15 StartZ=0 EndX=-27.2222 EndY=-10.2 EndZ=0
    g4: LineSegment StartX=-40 StartY=-10.2 StartZ=0 EndX=-27.2222 EndY=-10.2 EndZ=0
  constraints (14):
    c: Coincident(g2,g0)
    c: Vertical(g1)
    c: Vertical(g2)
    c: Coincident(g0,g-1)
    c: DistanceY(g2,g2) = 15
    c: DistanceY(g1,g1) = 10.2
    c: Coincident(g3,g2)
    c: Angle(g2,g3) = 1.39626
    c: Horizontal(g0)
    c: Coincident(g1,g0)
    c: Coincident(g4,g1)
    c: Coincident(g4,g3)
    c: Horizontal(g4)
    c: DistanceX(g0,g0) = 40
FEATURE [PartDesign::Pad] Pad001  label="ExtraPeripheralsSize"
  AddSubType = 0
  AlongSketchNormal = false
  BaseFeature = -> Pad
  CheckUpToFaceLimits = true
  ClaimChildren = false
  Direction = (0,0,1)
  Fit = 0
  FitJoin = 0
  InnerFit = 0
  InnerFitJoin = 0
  InnerTaperAngle = 0
  InnerTaperAngleRev = 0
  Length = 5
  Length2 = 100
  Linearize = true
  NewSolid = false
  Profile = -> Sketch
  Suppress = false
  TreeRank = 2
  Type = 0
  _ProfileBasedVersion = 1
FEATURE [Sketcher::SketchObject] Sketch001
  ExternalGeometry = -> [Pad001]
  FullyConstrained = true
  MapMode = 5
  Placement = pos=(0,-10.2,0) rot=(1,0,0;1.5708rad)
  Support = -> [Pad001]
  TreeRank = 3
  sketch-geometry (7):
    g0: LineSegment StartX=-40 StartY=5 StartZ=0 EndX=-68 EndY=-23 EndZ=0
    g1: LineSegment StartX=-68 StartY=-23 StartZ=0 EndX=-68 EndY=-28 EndZ=0
    g2: LineSegment StartX=-40 StartY=5 StartZ=0 EndX=-40 EndY=0 EndZ=0
    g3: LineSegment StartX=-68 StartY=-28 StartZ=0 EndX=-66 EndY=-28 EndZ=0
    g4: LineSegment StartX=-66 StartY=-28 StartZ=0 EndX=-66 EndY=-26 EndZ=0
    g5: LineSegment StartX=-40 StartY=0 StartZ=0 EndX=-66 EndY=-26 EndZ=0
    g6: LineSegment [constr] StartX=-66 StartY=-26 StartZ=0 EndX=-68 EndY=-28 EndZ=0
  constraints (19):
    c: Coincident(g0,g-3)
    c: Coincident(g5,g-3)
    c: Coincident(g1,g0)
    c: Vertical(g1)
    c: DistanceX(g0,g0) = 28
    c: Angle(g0,g-3) = 0.785398
    c: Coincident(g2,g0)
    c: Coincident(g2,g5)
    c: Equal(g2,g1)
    c: DistanceY(g1,g5) = 28
    c: Horizontal(g3)
    c: Coincident(g4,g3)
    c: Vertical(g4)
    c: Coincident(g5,g4)
    c: Coincident(g3,g1)
    c: Coincident(g6,g4)
    c: Coincident(g6,g1)
    c: Parallel(g6,g5)
    c: DistanceX(g3,g3) = 2
FEATURE [PartDesign::Pad] Pad002  label="Slope"
  AddSubType = 0
  AlongSketchNormal = false
  BaseFeature = -> Pad001
  CheckUpToFaceLimits = true
  ClaimChildren = false
  Direction = (0,-1,2e-16)
  Fit = 0
  FitJoin = 0
  InnerFit = 0
  InnerFitJoin = 0
  InnerTaperAngle = 0
  InnerTaperAngleRev = 0
  Length = 10
  Length2 = 100
  Linearize = true
  NewSolid = false
  Profile = -> Sketch001
  Reversed = true
  Suppress = false
  TreeRank = 4
  Type = 3
  UpToFace = -> Pad001 [Face3]
  _ProfileBasedVersion = 1
FEATURE [Sketcher::SketchObject] Sketch005
  ExternalGeometry = -> [Pad002]
  FullyConstrained = true
  MapMode = 5
  Placement = pos=(0,0,5) rot=(0,0,1;0rad)
  Support = -> [Pad002]
  TreeRank = 11
  sketch-geometry (4):
    g0: LineSegment StartX=-68 StartY=-10.2 StartZ=0 EndX=-58.8 EndY=-10.2 EndZ=0
    g1: LineSegment StartX=-58.8 StartY=-10.2 StartZ=0 EndX=-58.8 EndY=-1 EndZ=0
    g2: LineSegment StartX=-58.8 StartY=-1 StartZ=0 EndX=-68 EndY=-1 EndZ=0
    g3: LineSegment StartX=-68 StartY=-1 StartZ=0 EndX=-68 EndY=-10.2 EndZ=0
  constraints (11):
    c: Coincident(g0,g1)
    c: Coincident(g1,g2)
    c: Coincident(g2,g3)
    c: Coincident(g3,g0)
    c: Horizontal(g0)
    c: Horizontal(g2)
    c: Vertical(g1)
    c: Vertical(g3)
    c: Coincident(g0,g-3)
    c: Equal(g1,g2)
    c: DistanceX(g2,g2) = 9.2
FEATURE [PartDesign::Pocket] Pocket  label="ColumnPartHole"
  AddSubType = 1
  BaseFeature = -> Pad002
  CheckUpToFaceLimits = true
  ClaimChildren = false
  Fit = 0
  FitJoin = 0
  InnerFit = 0
  InnerFitJoin = 0
  InnerTaperAngle = 0
  InnerTaperAngleRev = 0
  Length = 5
  Length2 = 100
  Linearize = true
  NewSolid = false
  Profile = -> Sketch005
  Suppress = false
  TreeRank = 12
  Type = 1
  _ProfileBasedVersion = 1
  _Version = 1
FEATURE [Sketcher::SketchObject] Sketch003
  ExternalGeometry = -> [Pocket]
  FullyConstrained = true
  MapMode = 5
  Placement = pos=(0,-10.2,0) rot=(1,0,0;1.5708rad)
  TreeRank = 7
  sketch-geometry (5):
    g0: LineSegment StartX=-58.8 StartY=-51 StartZ=0 EndX=-58.8 EndY=-18.8 EndZ=0
    g1: LineSegment StartX=-58.8 StartY=-18.8 StartZ=0 EndX=-40 EndY=0 EndZ=0
    g2: LineSegment StartX=-40 StartY=0 StartZ=0 EndX=-27.2222 EndY=0 EndZ=0
    g3: LineSegment StartX=-27.2222 StartY=0 StartZ=0 EndX=-27.2222 EndY=-51 EndZ=0
    g4: LineSegment StartX=-58.8 StartY=-51 StartZ=0 EndX=-27.2222 EndY=-51 EndZ=0
  constraints (12):
    c: Coincident(g0,g-4)
    c: Coincident(g1,g0)
    c: Coincident(g1,g-4)
    c: Coincident(g2,g1)
    c: Coincident(g2,g-3)
    c: Coincident(g3,g2)
    c: Vertical(g3)
    c: Coincident(g4,g0)
    c: Horizontal(g4)
    c: Coincident(g4,g3)
    c: Vertical(g0)
    c: DistanceY(g3,g3) = 51
FEATURE [PartDesign::Pad] Pad004  label="SlopeFrontPanel"
  AddSubType = 0
  AlongSketchNormal = false
  BaseFeature = -> Pocket
  CheckUpToFaceLimits = true
  ClaimChildren = false
  Direction = (0,-1,2e-16)
  Fit = 0
  FitJoin = 0
  InnerFit = 0
  InnerFitJoin = 0
  InnerTaperAngle = 0
  InnerTaperAngleRev = 0
  Length = 2
  Length2 = 100
  Linearize = true
  NewSolid = false
  Profile = -> Sketch003
  Reversed = true
  Suppress = false
  TreeRank = 8
  Type = 0
  _ProfileBasedVersion = 1
FEATURE [Sketcher::SketchObject] Sketch004
  ExternalGeometry = -> [Pad004]
  FullyConstrained = true
  MapMode = 5
  Placement = pos=(0,0,0) rot=(1,0,0;3.14159rad)
  Support = -> [Pad004]
  TreeRank = 9
  sketch-geometry (4):
    g0: LineSegment StartX=-27.2222 StartY=10.2 StartZ=0 EndX=0 EndY=15 EndZ=0
    g1: LineSegment StartX=-27.2222 StartY=8.2 StartZ=0 EndX=-27.2222 EndY=10.2 EndZ=0
    g2: LineSegment StartX=-27.2222 StartY=8.2 StartZ=0 EndX=0 EndY=13 EndZ=0
    g3: LineSegment StartX=0 StartY=13 StartZ=0 EndX=0 EndY=15 EndZ=0
  constraints (9):
    c: Coincident(g0,g-3)
    c: Coincident(g0,g-4)
    c: Coincident(g1,g-3)
    c: Coincident(g1,g0)
    c: Coincident(g2,g1)
    c: PointOnObject(g2,g-4)
    c: Coincident(g3,g2)
    c: Coincident(g3,g0)
    c: DistanceY(g3,g3) = 2
FEATURE [PartDesign::Pad] Pad005  label="AnglePanel"
  AddSubType = 0
  AlongSketchNormal = false
  BaseFeature = -> Pad004
  CheckUpToFaceLimits = true
  ClaimChildren = false
  Direction = (0,0,-1)
  Fit = 0
  FitJoin = 0
  InnerFit = 0
  InnerFitJoin = 0
  InnerTaperAngle = 0
  InnerTaperAngleRev = 0
  Length = 51
  Length2 = 100
  Linearize = true
  NewSolid = false
  Profile = -> Sketch004
  Suppress = false
  TreeRank = 10
  Type = 0
  _ProfileBasedVersion = 1
FEATURE [Sketcher::SketchObject] Sketch006
  ExternalGeometry = -> [Pad005]
  FullyConstrained = true
  MapMode = 5
  Placement = pos=(0,-6.2e-15,-28) rot=(1,0,0;3.14159rad)
  Support = -> [Pad005]
  TreeRank = 13
  sketch-geometry (4):
    g0: LineSegment StartX=-68 StartY=-116 StartZ=0 EndX=-66 EndY=-116 EndZ=0
    g1: LineSegment StartX=-66 StartY=-116 StartZ=0 EndX=-66 EndY=1 EndZ=0
    g2: LineSegment StartX=-66 StartY=1 StartZ=0 EndX=-68 EndY=1 EndZ=0
    g3: LineSegment StartX=-68 StartY=1 StartZ=0 EndX=-68 EndY=-116 EndZ=0
  constraints (10):
    c: Coincident(g0,g1)
    c: Coincident(g1,g2)
    c: Coincident(g2,g3)
    c: Coincident(g3,g0)
    c: Horizontal(g0)
    c: Horizontal(g2)
    c: Vertical(g1)
    c: Vertical(g3)
    c: Coincident(g0,g-4)
    c: Coincident(g1,g-3)
FEATURE [PartDesign::Pad] Pad006  label="SlopeSidePanel"
  AddSubType = 0
  AlongSketchNormal = false
  BaseFeature = -> Pad005
  CheckUpToFaceLimits = true
  ClaimChildren = false
  Direction = (0,-2e-16,-1)
  Fit = 0
  FitJoin = 0
  InnerFit = 0
  InnerFitJoin = 0
  InnerTaperAngle = 0
  InnerTaperAngleRev = 0
  Length = 10
  Length2 = 100
  Linearize = true
  NewSolid = false
  Profile = -> Sketch006
  Suppress = false
  TreeRank = 14
  Type = 3
  UpToFace = -> Pad005 [Face24]
  _ProfileBasedVersion = 1
FEATURE [Sketcher::SketchObject] Sketch007
  ExternalGeometry = -> [Pad006]
  FullyConstrained = true
  MapMode = 5
  Placement = pos=(0,-1,2e-16) rot=(1,0,0;1.5708rad)
  Support = -> [Pad006]
  TreeRank = 15
  sketch-geometry (4):
    g0: LineSegment StartX=-58.8 StartY=-18.8 StartZ=0 EndX=-66 EndY=-26 EndZ=0
    g1: LineSegment StartX=-66 StartY=-26 StartZ=0 EndX=-66 EndY=-53 EndZ=0
    g2: LineSegment StartX=-66 StartY=-53 StartZ=0 EndX=-58.8 EndY=-53 EndZ=0
    g3: LineSegment StartX=-58.8 StartY=-53 StartZ=0 EndX=-58.8 EndY=-18.8 EndZ=0
  constraints (10):
    c: Coincident(g0,g-4)
    c: Coincident(g0,g-4)
    c: Coincident(g1,g0)
    c: Coincident(g2,g1)
    c: Horizontal(g2)
    c: Coincident(g3,g2)
    c: Coincident(g3,g0)
    c: Vertical(g3)
    c: Vertical(g1)
    c: DistanceY(g1,g-3) = 2
FEATURE [PartDesign::Pad] Pad007  label="ColumnPanel1"
  AddSubType = 0
  AlongSketchNormal = false
  BaseFeature = -> Pad006
  CheckUpToFaceLimits = true
  ClaimChildren = false
  Direction = (0,-1,2e-16)
  Fit = 0
  FitJoin = 0
  InnerFit = 0
  InnerFitJoin = 0
  InnerTaperAngle = 0
  InnerTaperAngleRev = 0
  Length = 2
  Length2 = 100
  Linearize = true
  NewSolid = false
  Profile = -> Sketch007
  Reversed = true
  Suppress = false
  TreeRank = 16
  Type = 0
  _ProfileBasedVersion = 1
FEATURE [Sketcher::SketchObject] Sketch008
  ExternalGeometry = -> [Pad007]
  FullyConstrained = true
  MapMode = 5
  Placement = pos=(-1e-16,-8.2,1.7e-15) rot=(0,0.707107,0.707107;3.14159rad)
  Support = -> [Pad007]
  TreeRank = 17
  sketch-geometry (4):
    g0: LineSegment StartX=56.8 StartY=-16.8 StartZ=0 EndX=56.8 EndY=-53 EndZ=0
    g1: LineSegment StartX=56.8 StartY=-53 StartZ=0 EndX=58.8 EndY=-53 EndZ=0
    g2: LineSegment StartX=58.8 StartY=-18.8 StartZ=0 EndX=56.8 EndY=-16.8 EndZ=0
    g3: LineSegment StartX=58.8 StartY=-18.8 StartZ=0 EndX=58.8 EndY=-53 EndZ=0
  constraints (10):
    c: PointOnObject(g0,g-4)
    c: Vertical(g0)
    c: Coincident(g1,g0)
    c: Coincident(g1,g-3)
    c: Horizontal(g1)
    c: Coincident(g2,g-4)
    c: Coincident(g2,g0)
    c: Coincident(g3,g2)
    c: Coincident(g3,g1)
    c: DistanceX(g1,g1) = 2
FEATURE [PartDesign::Pad] Pad008  label="ColumnPanel2"
  AddSubType = 0
  AlongSketchNormal = false
  BaseFeature = -> Pad007
  CheckUpToFaceLimits = true
  ClaimChildren = false
  Direction = (0,1,-2e-16)
  Fit = 0
  FitJoin = 0
  InnerFit = 0
  InnerFitJoin = 0
  InnerTaperAngle = 0
  InnerTaperAngleRev = 0
  Length = 10
  Length2 = 100
  Linearize = true
  NewSolid = false
  Profile = -> Sketch008
  Suppress = false
  TreeRank = 18
  Type = 3
  UpToFace = -> Pad007 [Face20]
  _ProfileBasedVersion = 1
FEATURE [Sketcher::SketchObject] Sketch009
  ExternalGeometry = -> [Pad008]
  FullyConstrained = true
  MapMode = 5
  Placement = pos=(0,-1,2e-16) rot=(1,0,0;1.5708rad)
  Support = -> [Pad008]
  TreeRank = 19
  sketch-geometry (4):
    g0: LineSegment StartX=-68 StartY=-51 StartZ=0 EndX=-58.8 EndY=-51 EndZ=0
    g1: LineSegment StartX=-58.8 StartY=-51 StartZ=0 EndX=-58.8 EndY=-46 EndZ=0
    g2: LineSegment StartX=-58.8 StartY=-46 StartZ=0 EndX=-68 EndY=-46 EndZ=0
    g3: LineSegment StartX=-68 StartY=-46 StartZ=0 EndX=-68 EndY=-51 EndZ=0
  constraints (11):
    c: Coincident(g0,g1)
    c: Coincident(g1,g2)
    c: Coincident(g2,g3)
    c: Coincident(g3,g0)
    c: Horizontal(g0)
    c: Horizontal(g2)
    c: Vertical(g1)
    c: Vertical(g3)
    c: Coincident(g0,g-3)
    c: PointOnObject(g1,g-4)
    c: DistanceY(g3,g3) = 5
FEATURE [PartDesign::Pad] Pad009  label="HoleSupport"
  AddSubType = 0
  AlongSketchNormal = false
  BaseFeature = -> Pad008
  CheckUpToFaceLimits = true
  ClaimChildren = false
  Direction = (0,-1,2e-16)
  Fit = 0
  FitJoin = 0
  InnerFit = 0
  InnerFitJoin = 0
  InnerTaperAngle = 0
  InnerTaperAngleRev = 0
  Length = 10
  Length2 = 100
  Linearize = true
  NewSolid = false
  Profile = -> Sketch009
  Suppress = false
  TreeRank = 20
  Type = 3
  UpToFace = -> Pad008 [Face28]
  _ProfileBasedVersion = 1
FEATURE [Sketcher::SketchObject] Sketch010
  ExternalGeometry = -> [Pad009]
  FullyConstrained = true
  MapMode = 5
  Placement = pos=(0,-1.01e-14,-46) rot=(0,0,1;0rad)
  Support = -> [Pad009]
  TreeRank = 21
  sketch-geometry (3):
    g0: LineSegment [constr] StartX=-62.4 StartY=-1 StartZ=0 EndX=-62.4 EndY=-4.6 EndZ=0
    g1: LineSegment [constr] StartX=-62.4 StartY=-4.6 StartZ=0 EndX=-58.8 EndY=-4.6 EndZ=0
    g2: Circle CenterX=-62.4 CenterY=-4.6 CenterZ=0 NormalX=0 NormalY=0 NormalZ=1 AngleXU=0 Radius=1.6
  constraints (9):
    c: Vertical(g0)
    c: Coincident(g1,g0)
    c: Horizontal(g1)
    c: Coincident(g2,g0)
    c: Diameter(g2) = 3.2
    c: PointOnObject(g1,g-4)
    c: PointOnObject(g0,g-3)
    c: DistanceX(g0,g-4) = 3.6
    c: DistanceY(g1,g-4) = 3.6
FEATURE [PartDesign::Pocket] Pocket001  label="Hole"
  AddSubType = 1
  BaseFeature = -> Pad009
  CheckUpToFaceLimits = true
  ClaimChildren = false
  Fit = 0
  FitJoin = 0
  InnerFit = 0
  InnerFitJoin = 0
  InnerTaperAngle = 0
  InnerTaperAngleRev = 0
  Length = 5
  Length2 = 100
  Linearize = true
  NewSolid = false
  Profile = -> Sketch010
  Suppress = false
  TreeRank = 22
  Type = 0
  _ProfileBasedVersion = 1
  _Version = 1
FEATURE [Sketcher::SketchObject] Sketch011
  ExternalGeometry = -> [Pocket001]
  FullyConstrained = true
  MapMode = 5
  Placement = pos=(0,0,0) rot=(0.57735,0.57735,0.57735;2.0944rad)
  Support = -> [Pocket001]
  TreeRank = 23
  sketch-geometry (4):
    g0: LineSegment StartX=-12.8 StartY=3.34 StartZ=0 EndX=94.8 EndY=3.34 EndZ=0
    g1: LineSegment StartX=94.8 StartY=3.34 StartZ=0 EndX=94.8 EndY=1.94 EndZ=0
    g2: LineSegment StartX=94.8 StartY=1.94 StartZ=0 EndX=-12.8 EndY=1.94 EndZ=0
    g3: LineSegment StartX=-12.8 StartY=1.94 StartZ=0 EndX=-12.8 EndY=3.34 EndZ=0
  constraints (12):
    c: Coincident(g0,g1)
    c: Coincident(g1,g2)
    c: Coincident(g2,g3)
    c: Coincident(g3,g0)
    c: Horizontal(g0)
    c: Horizontal(g2)
    c: Vertical(g1)
    c: Vertical(g3)
    c: DistanceY(g-3,g2) = 1.94
    c: DistanceX(g-3,g0) = 2.2
    c: DistanceY(g3,g3) = 1.4
    c: DistanceX(g0,g-4) = 21.2
FEATURE [PartDesign::Pad] Pad010  label="Puzzle1"
  AddSubType = 0
  AlongSketchNormal = false
  BaseFeature = -> Pocket001
  CheckUpToFaceLimits = true
  ClaimChildren = false
  Direction = (1,0,0)
  Fit = 0
  FitJoin = 0
  InnerFit = 0
  InnerFitJoin = 0
  InnerTaperAngle = 0
  InnerTaperAngleRev = 0
  Length = 10
  Length2 = 100
  Linearize = true
  NewSolid = false
  Profile = -> Sketch011
  Suppress = false
  TreeRank = 24
  Type = 0
  _ProfileBasedVersion = 1
FEATURE [Sketcher::SketchObject] Sketch012
  ExternalGeometry = -> [Pad010]
  FullyConstrained = true
  MapMode = 5
  Placement = pos=(0,116,0) rot=(0,0.707107,0.707107;3.14159rad)
  Support = -> [Pad010]
  TreeRank = 25
  sketch-geometry (4):
    g0: LineSegment StartX=10.95 StartY=3.58 StartZ=0 EndX=29.05 EndY=3.58 EndZ=0
    g1: LineSegment StartX=29.05 StartY=3.58 StartZ=0 EndX=29.05 EndY=1.5 EndZ=0
    g2: LineSegment StartX=29.05 StartY=1.5 StartZ=0 EndX=10.95 EndY=1.5 EndZ=0
    g3: LineSegment StartX=10.95 StartY=1.5 StartZ=0 EndX=10.95 EndY=3.58 EndZ=0
  constraints (12):
    c: Coincident(g0,g1)
    c: Coincident(g1,g2)
    c: Coincident(g2,g3)
    c: Coincident(g3,g0)
    c: Horizontal(g0)
    c: Horizontal(g2)
    c: Vertical(g1)
    c: Vertical(g3)
    c: DistanceY(g-3,g2) = 1.5
    c: DistanceY(g3,g3) = 2.08
    c: DistanceX(g-3,g0) = 10.95
    c: DistanceX(g0,g-4) = 10.95
FEATURE [PartDesign::Pocket] Pocket002  label="PuzzleHole1"
  AddSubType = 1
  BaseFeature = -> Pad010
  CheckUpToFaceLimits = true
  ClaimChildren = false
  Fit = 0
  FitJoin = 0
  InnerFit = 0
  InnerFitJoin = 0
  InnerTaperAngle = 0
  InnerTaperAngleRev = 0
  Length = 11
  Length2 = 100
  Linearize = true
  NewSolid = false
  Profile = -> Sketch012
  Suppress = false
  TreeRank = 26
  Type = 0
  _ProfileBasedVersion = 1
  _Version = 1
FEATURE [PartDesign::Chamfer] Chamfer
  AddSubType = 0
  Angle = 45
  Base = -> Pocket002 [Edge55,Edge54]
  BaseFeature = -> Pocket002
  ChamferType = 0
  FlipDirection = false
  NewSolid = false
  Size = 2
  Size2 = 1
  SupportTransform = false
  Suppress = false
  TreeRank = 27
FEATURE [Sketcher::SketchObject] Sketch013
  ExternalGeometry = -> [Chamfer]
  FullyConstrained = true
  MapMode = 5
  Placement = pos=(0,0,0) rot=(1,0,0;3.14159rad)
  Support = -> [Chamfer]
  TreeRank = 28
  sketch-geometry (4):
    g0: LineSegment StartX=-5.67128 StartY=12 StartZ=0 EndX=1.5 EndY=12 EndZ=0
    g1: LineSegment StartX=1.5 StartY=12 StartZ=0 EndX=1.5 EndY=13 EndZ=0
    g2: LineSegment StartX=0 StartY=13 StartZ=0 EndX=1.5 EndY=13 EndZ=0
    g3: LineSegment StartX=-5.67128 StartY=12 StartZ=0 EndX=0 EndY=13 EndZ=0
  constraints (11):
    c: PointOnObject(g0,g-3)
    c: Horizontal(g0)
    c: Coincident(g1,g0)
    c: Vertical(g1)
    c: Coincident(g2,g-3)
    c: Coincident(g2,g1)
    c: Horizontal(g2)
    c: DistanceY(g1,g1) = 1
    c: DistanceX(g2,g2) = 1.5
    c: Coincident(g3,g0)
    c: Coincident(g3,g2)
FEATURE [PartDesign::Pad] Pad011  label="PanelGuard"
  AddSubType = 0
  AlongSketchNormal = false
  BaseFeature = -> Chamfer
  CheckUpToFaceLimits = true
  ClaimChildren = false
  Direction = (0,0,-1)
  Fit = 0
  FitJoin = 0
  InnerFit = 0
  InnerFitJoin = 0
  InnerTaperAngle = 0
  InnerTaperAngleRev = 0
  Length = 10
  Length2 = 100
  Linearize = true
  NewSolid = false
  Profile = -> Sketch013
  Suppress = false
  TreeRank = 29
  Type = 3
  UpToFace = -> Chamfer [Face48]
  _ProfileBasedVersion = 1
FEATURE [PartDesign::Body] Body
  AutoGroupSolids = false
  ClaimAllChildren = false
  ExportMode = 0
  Group = -> [LCS_0,Sketch_1,Pad,Sketch,Pad001,Sketch001,Pad002,Pocket,Sketch005,Sketch003,Pad004,Sketch004,Pad005,Sketch006,Pad006,Sketch007,Pad007,Sketch008,Pad008,Sketch009,Pad009,Sketch010,Pocket001,Sketch011,Pad010,Sketch012,Pocket002,Chamfer,Sketch013,Pad011]
  Origin = -> Origin001
  Tip = -> Pad011
  TreeRank = 0
  _ExportChildren = -> [LCS_0,Pad,Pad001,Pad002,Pocket,Pad004,Pad005,Pad006,Pad007,Pad008,Pad009,Pocket001,Pad010,Pocket002,Chamfer,Pad011]
  _GroupVersion = 1
FEATURE [App::Part] Part  label="SecondPartPeripheralsTop"
  ClaimAllChildren = false
  ExportMode = 1
  Group = -> [Body]
  Origin = -> Origin
  TreeRank = 0
  _ExportChildren = -> [Body]
  _GroupVersion = 1
---- part SecondPartProcessor.FCStd = doc fcstd_8ed29b0da446 ----
FCSTD DOCUMENT  (FreeCAD 2022.430R26244 +4758 (Git))
Label: SecondPartProcessor
License: All rights reserved
LicenseURL: http://en.wikipedia.org/wiki/All_rights_reserved
objects: Sketcher::SketchObject×11, PartDesign::Pad×9, PartDesign::Pocket×2, PartDesign::CoordinateSystem×1, PartDesign::Fillet×1, PartDesign::Body×1, App::Part×1
note: 49 computed .brp shape members not serialized (recipe doc carries the construction recipe); baked Part::Feature solids carry a one-line shape summary decoded from their .brp

FEATURE [PartDesign::CoordinateSystem] LCS_0
  AttacherType = Attacher::AttachEngine3D
  MapMode = 2
  Support = -> [X_Axis001]
  TreeRank = 0
FEATURE [Sketcher::SketchObject] Sketch_1
  FullyConstrained = true
  TreeRank = 0
  sketch-geometry (4):
    g0: LineSegment StartX=0 StartY=0 StartZ=0 EndX=-63 EndY=0 EndZ=0
    g1: LineSegment StartX=-63 StartY=0 StartZ=0 EndX=-63 EndY=93 EndZ=0
    g2: LineSegment StartX=-63 StartY=93 StartZ=0 EndX=0 EndY=93 EndZ=0
    g3: LineSegment StartX=0 StartY=93 StartZ=0 EndX=0 EndY=0 EndZ=0
  constraints (11):
    c: Coincident(g0,g1)
    c: Coincident(g1,g2)
    c: Coincident(g2,g3)
    c: Coincident(g3,g0)
    c: Horizontal(g0)
    c: Horizontal(g2)
    c: Vertical(g1)
    c: Vertical(g3)
    c: Coincident(g0,g-1)
    c: DistanceY(g3,g3) = 93
    c: DistanceX(g2,g2) = 63
FEATURE [PartDesign::Pad] Pad  label="MainSupport"
  AddSubType = 0
  CheckUpToFaceLimits = true
  ClaimChildren = false
  Direction = (0,0,1)
  Fit = 0
  FitJoin = 0
  InnerFit = 0
  InnerFitJoin = 0
  InnerTaperAngle = 0
  InnerTaperAngleRev = 0
  Length = 5
  Length2 = 100
  NewSolid = false
  Profile = -> Sketch_1
  Suppress = false
  TreeRank = 0
  Type = 0
  _ProfileBasedVersion = 0
FEATURE [Sketcher::SketchObject] Sketch
  ExternalGeometry = -> [Pad]
  FullyConstrained = true
  MapMode = 5
  Support = -> [XY_Plane001]
  TreeRank = 1
  sketch-geometry (4):
    g0: LineSegment StartX=0 StartY=0 StartZ=0 EndX=-63 EndY=4e-16 EndZ=0
    g1: LineSegment StartX=-63 StartY=4e-16 StartZ=0 EndX=-63 EndY=-7.4 EndZ=0
    g2: LineSegment StartX=0 StartY=-7.4 StartZ=0 EndX=0 EndY=0 EndZ=0
    g3: LineSegment StartX=0 StartY=-7.4 StartZ=0 EndX=-63 EndY=-7.4 EndZ=0
  constraints (10):
    c: Coincident(g0,g1)
    c: Coincident(g2,g0)
    c: Vertical(g1)
    c: Vertical(g2)
    c: Coincident(g0,g-1)
    c: Coincident(g0,g-3)
    c: DistanceY(g1,g1) = 7.4
    c: Coincident(g3,g1)
    c: Horizontal(g3)
    c: Coincident(g2,g3)
FEATURE [PartDesign::Pad] Pad001  label="ExtraGapSize"
  AddSubType = 0
  AlongSketchNormal = false
  BaseFeature = -> Pad
  CheckUpToFaceLimits = true
  ClaimChildren = false
  Direction = (0,0,1)
  Fit = 0
  FitJoin = 0
  InnerFit = 0
  InnerFitJoin = 0
  InnerTaperAngle = 0
  InnerTaperAngleRev = 0
  Length = 5
  Length2 = 100
  Linearize = true
  NewSolid = false
  Profile = -> Sketch
  Suppress = false
  TreeRank = 2
  Type = 0
  _ProfileBasedVersion = 1
FEATURE [Sketcher::SketchObject] Sketch001
  ExternalGeometry = -> [Pad001]
  FullyConstrained = true
  MapMode = 5
  Support = -> [XY_Plane001]
  TreeRank = 3
  sketch-geometry (6):
    g0: LineSegment StartX=-68 StartY=103.2 StartZ=0 EndX=-68 EndY=-7.4 EndZ=0
    g1: LineSegment StartX=-68 StartY=103.2 StartZ=0 EndX=0 EndY=103.2 EndZ=0
    g2: LineSegment StartX=-63 StartY=93 StartZ=0 EndX=0 EndY=93 EndZ=0
    g3: LineSegment StartX=0 StartY=93 StartZ=0 EndX=0 EndY=103.2 EndZ=0
    g4: LineSegment StartX=-68 StartY=-7.4 StartZ=0 EndX=-63 EndY=-7.4 EndZ=0
    g5: LineSegment StartX=-63 StartY=-7.4 StartZ=0 EndX=-63 EndY=93 EndZ=0
  constraints (16):
    c: Vertical(g0)
    c: Coincident(g1,g0)
    c: PointOnObject(g1,g-2)
    c: Horizontal(g1)
    c: Horizontal(g2)
    c: Coincident(g3,g2)
    c: Coincident(g3,g1)
    c: Coincident(g4,g0)
    c: Coincident(g5,g4)
    c: Coincident(g5,g2)
    c: Vertical(g5)
    c: DistanceX(g4,g4) = 5
    c: DistanceY(g3,g3) = 10.2
    c: Coincident(g2,g-3)
    c: Coincident(g4,g-4)
    c: Horizontal(g4)
FEATURE [PartDesign::Pad] Pad002  label="ExtraSideSize"
  AddSubType = 0
  AlongSketchNormal = false
  BaseFeature = -> Pad001
  CheckUpToFaceLimits = true
  ClaimChildren = false
  Direction = (0,0,1)
  Fit = 0
  FitJoin = 0
  InnerFit = 0
  InnerFitJoin = 0
  InnerTaperAngle = 0
  InnerTaperAngleRev = 0
  Length = 5
  Length2 = 100
  Linearize = true
  NewSolid = false
  Profile = -> Sketch001
  Suppress = false
  TreeRank = 4
  Type = 0
  _ProfileBasedVersion = 1
FEATURE [Sketcher::SketchObject] Sketch002
  ExternalGeometry = -> [Pad002]
  FullyConstrained = true
  MapMode = 5
  Placement = pos=(0,0,5) rot=(0,0,1;0rad)
  Support = -> [Pad002]
  TreeRank = 5
  sketch-geometry (6):
    g0: LineSegment StartX=-68 StartY=103.2 StartZ=0 EndX=-68 EndY=-7.4 EndZ=0
    g1: LineSegment StartX=0 StartY=103.2 StartZ=0 EndX=-68 EndY=103.2 EndZ=0
    g2: LineSegment StartX=-68 StartY=-7.4 StartZ=0 EndX=-66 EndY=-7.4 EndZ=0
    g3: LineSegment StartX=-66 StartY=-7.4 StartZ=0 EndX=-66 EndY=101.2 EndZ=0
    g4: LineSegment StartX=-66 StartY=101.2 StartZ=0 EndX=0 EndY=101.2 EndZ=0
    g5: LineSegment StartX=0 StartY=103.2 StartZ=0 EndX=0 EndY=101.2 EndZ=0
  constraints (16):
    c: Coincident(g1,g0)
    c: Horizontal(g1)
    c: Coincident(g0,g-3)
    c: Coincident(g2,g0)
    c: Coincident(g3,g2)
    c: Vertical(g3)
    c: Coincident(g4,g3)
    c: PointOnObject(g4,g-2)
    c: Horizontal(g4)
    c: PointOnObject(g1,g-2)
    c: Coincident(g5,g1)
    c: Coincident(g5,g4)
    c: DistanceY(g5,g5) = 2
    c: DistanceX(g2,g2) = 2
    c: Coincident(g0,g-3)
    c: Horizontal(g2)
FEATURE [PartDesign::Pad] Pad003  label="SidePanel"
  AddSubType = 0
  AlongSketchNormal = false
  BaseFeature = -> Pad002
  CheckUpToFaceLimits = true
  ClaimChildren = false
  Direction = (0,0,1)
  Fit = 0
  FitJoin = 0
  InnerFit = 0
  InnerFitJoin = 0
  InnerTaperAngle = 0
  InnerTaperAngleRev = 0
  Length = 51
  Length2 = 100
  Linearize = true
  NewSolid = false
  Profile = -> Sketch002
  Suppress = false
  TreeRank = 6
  Type = 0
  _ProfileBasedVersion = 1
FEATURE [Sketcher::SketchObject] Sketch005
  ExternalGeometry = -> [Pad003]
  FullyConstrained = true
  MapMode = 5
  Placement = pos=(0,0,0) rot=(0.57735,0.57735,0.57735;2.0944rad)
  TreeRank = 11
  sketch-geometry (4):
    g0: LineSegment StartX=101 StartY=3.06 StartZ=0 EndX=13.8 EndY=3.06 EndZ=0
    g1: LineSegment StartX=13.8 StartY=3.06 StartZ=0 EndX=13.8 EndY=1.66 EndZ=0
    g2: LineSegment StartX=13.8 StartY=1.66 StartZ=0 EndX=101 EndY=1.66 EndZ=0
    g3: LineSegment StartX=101 StartY=1.66 StartZ=0 EndX=101 EndY=3.06 EndZ=0
  constraints (12):
    c: Coincident(g0,g1)
    c: Coincident(g1,g2)
    c: Coincident(g2,g3)
    c: Coincident(g3,g0)
    c: Horizontal(g0)
    c: Horizontal(g2)
    c: Vertical(g1)
    c: Vertical(g3)
    c: DistanceY(g1,g1) = 1.4
    c: DistanceX(g0,g-3) = 2.2
    c: DistanceY(g0,g-3) = 1.94
    c: DistanceX(g-4,g0) = 21.2
FEATURE [PartDesign::Pad] Pad005  label="Puzzle1"
  AddSubType = 0
  AlongSketchNormal = false
  BaseFeature = -> Pad003
  CheckUpToFaceLimits = true
  ClaimChildren = false
  Direction = (1,1e-16,-1e-16)
  Fit = 0
  FitJoin = 0
  InnerFit = 0
  InnerFitJoin = 0
  InnerTaperAngle = 0
  InnerTaperAngleRev = 0
  Length = 10
  Length2 = 100
  Linearize = true
  NewSolid = false
  Profile = -> Sketch005
  Suppress = false
  TreeRank = 12
  Type = 0
  _ProfileBasedVersion = 1
FEATURE [Sketcher::SketchObject] Sketch006
  ExternalGeometry = -> [Pad005]
  FullyConstrained = true
  MapMode = 5
  Placement = pos=(0,0,5) rot=(0,0,1;0rad)
  Support = -> [Pad005]
  TreeRank = 13
  sketch-geometry (2):
    g0: Circle CenterX=-58 CenterY=5 CenterZ=0 NormalX=0 NormalY=0 NormalZ=1 AngleXU=0 Radius=3.6
    g1: Circle CenterX=-58 CenterY=88 CenterZ=0 NormalX=0 NormalY=0 NormalZ=1 AngleXU=0 Radius=3.6
  constraints (6):
    c: Diameter(g1) = 7.2
    c: Diameter(g0) = 7.2
    c: DistanceX(g-3,g1) = 5
    c: DistanceY(g1,g-3) = 5
    c: DistanceY(g-3,g0) = 5
    c: DistanceX(g-3,g0) = 5
FEATURE [PartDesign::Pad] Pad006  label="ProcessorColumn"
  AddSubType = 0
  AlongSketchNormal = false
  BaseFeature = -> Pad005
  CheckUpToFaceLimits = true
  ClaimChildren = false
  Direction = (0,0,1)
  Fit = 0
  FitJoin = 0
  InnerFit = 0
  InnerFitJoin = 0
  InnerTaperAngle = 0
  InnerTaperAngleRev = 0
  Length = 12.4
  Length2 = 100
  Linearize = true
  NewSolid = false
  Profile = -> Sketch006
  Suppress = false
  TreeRank = 14
  Type = 0
  _ProfileBasedVersion = 1
FEATURE [Sketcher::SketchObject] Sketch007
  ExternalGeometry = -> [Pad006]
  FullyConstrained = true
  MapMode = 5
  Placement = pos=(0,0,17.4) rot=(0,0,1;0rad)
  Support = -> [Pad006]
  TreeRank = 15
  sketch-geometry (2):
    g0: Circle CenterX=-58 CenterY=5 CenterZ=0 NormalX=0 NormalY=0 NormalZ=1 AngleXU=0 Radius=2
    g1: Circle CenterX=-58 CenterY=88 CenterZ=0 NormalX=0 NormalY=0 NormalZ=1 AngleXU=0 Radius=2
  constraints (4):
    c: Coincident(g0,g-3)
    c: Coincident(g1,g-4)
    c: Diameter(g1) = 4
    c: Diameter(g0) = 4
FEATURE [PartDesign::Pocket] Pocket001  label="ColumnInsertHole"
  AddSubType = 1
  BaseFeature = -> Pad006
  CheckUpToFaceLimits = true
  ClaimChildren = false
  Fit = 0
  FitJoin = 0
  InnerFit = 0
  InnerFitJoin = 0
  InnerTaperAngle = 0
  InnerTaperAngleRev = 0
  Length = 6.7
  Length2 = 100
  Linearize = true
  NewSolid = false
  Profile = -> Sketch007
  Suppress = false
  TreeRank = 16
  Type = 0
  _ProfileBasedVersion = 1
  _Version = 1
FEATURE [Sketcher::SketchObject] Sketch008
  ExternalGeometry = -> [Pocket001]
  FullyConstrained = true
  MapMode = 5
  Placement = pos=(0,-7.4,0) rot=(1,0,0;1.5708rad)
  Support = -> [Pocket001]
  TreeRank = 17
  sketch-geometry (4):
    g0: LineSegment StartX=-65.8 StartY=3.06 StartZ=0 EndX=-21.2 EndY=3.06 EndZ=0
    g1: LineSegment StartX=-21.2 StartY=3.06 StartZ=0 EndX=-21.2 EndY=1.66 EndZ=0
    g2: LineSegment StartX=-21.2 StartY=1.66 StartZ=0 EndX=-65.8 EndY=1.66 EndZ=0
    g3: LineSegment StartX=-65.8 StartY=1.66 StartZ=0 EndX=-65.8 EndY=3.06 EndZ=0
  constraints (12):
    c: Coincident(g0,g1)
    c: Coincident(g1,g2)
    c: Coincident(g2,g3)
    c: Coincident(g3,g0)
    c: Horizontal(g0)
    c: Horizontal(g2)
    c: Vertical(g1)
    c: Vertical(g3)
    c: DistanceY(g0,g-3) = 1.94
    c: DistanceY(g1,g1) = 1.4
    c: DistanceX(g-4,g0) = 2.2
    c: DistanceX(g0,g-3) = 21.2
FEATURE [PartDesign::Pad] Pad007  label="Puzzle2"
  AddSubType = 0
  AlongSketchNormal = false
  BaseFeature = -> Pocket001
  CheckUpToFaceLimits = true
  ClaimChildren = false
  Direction = (0,-1,2e-16)
  Fit = 0
  FitJoin = 0
  InnerFit = 0
  InnerFitJoin = 0
  InnerTaperAngle = 0
  InnerTaperAngleRev = 0
  Length = 10
  Length2 = 100
  Linearize = true
  NewSolid = false
  Profile = -> Sketch008
  Suppress = false
  TreeRank = 18
  Type = 0
  _ProfileBasedVersion = 1
FEATURE [Sketcher::SketchObject] Sketch009
  ExternalGeometry = -> [Pad007]
  FullyConstrained = true
  MapMode = 5
  Placement = pos=(0,0,5) rot=(0,0,1;0rad)
  Support = -> [Pad007]
  TreeRank = 19
  sketch-geometry (6):
    g0: LineSegment [constr] StartX=-66 StartY=-5.4 StartZ=0 EndX=-65 EndY=-5.4 EndZ=0
    g1: LineSegment StartX=-65 StartY=-5.4 StartZ=0 EndX=-65 EndY=-8.9 EndZ=0
    g2: LineSegment StartX=-65 StartY=-8.9 StartZ=0 EndX=-66 EndY=-8.9 EndZ=0
    g3: LineSegment StartX=-66 StartY=-8.9 StartZ=0 EndX=-66 EndY=-5.4 EndZ=0
    g4: LineSegment StartX=-65 StartY=-5.4 StartZ=0 EndX=-66 EndY=-4.4 EndZ=0
    g5: LineSegment StartX=-66 StartY=-5.4 StartZ=0 EndX=-66 EndY=-4.4 EndZ=0
  constraints (17):
    c: Coincident(g0,g1)
    c: Coincident(g1,g2)
    c: Coincident(g2,g3)
    c: Coincident(g3,g0)
    c: Horizontal(g0)
    c: Horizontal(g2)
    c: Vertical(g1)
    c: Vertical(g3)
    c: PointOnObject(g0,g-3)
    c: DistanceY(g-3,g0) = 2
    c: DistanceY(g1,g-3) = 1.5
    c: DistanceX(g0,g0) = 1
    c: Coincident(g4,g1)
    c: PointOnObject(g4,g-3)
    c: Coincident(g5,g3)
    c: Coincident(g5,g4)
    c: Angle(g4,g0) = 0.785398
FEATURE [PartDesign::Pad] Pad008  label="PanelGuard"
  AddSubType = 0
  AlongSketchNormal = false
  BaseFeature = -> Pad007
  CheckUpToFaceLimits = true
  ClaimChildren = false
  Direction = (0,0,1)
  Fit = 0
  FitJoin = 0
  InnerFit = 0
  InnerFitJoin = 0
  InnerTaperAngle = 0
  InnerTaperAngleRev = 0
  Length = 10
  Length2 = 100
  Linearize = true
  NewSolid = false
  Profile = -> Sketch009
  Suppress = false
  TreeRank = 20
  Type = 3
  UpToFace = -> Pad007 [Face30]
  _ProfileBasedVersion = 1
FEATURE [Sketcher::SketchObject] Sketch010
  ExternalGeometry = -> [Pad008]
  FullyConstrained = true
  MapMode = 5
  Placement = pos=(0,0,5) rot=(0,0,1;0rad)
  Support = -> [Pad008]
  TreeRank = 21
  sketch-geometry (4):
    g0: LineSegment StartX=-66 StartY=101.2 StartZ=0 EndX=-58.8 EndY=101.2 EndZ=0
    g1: LineSegment StartX=-58.8 StartY=101.2 StartZ=0 EndX=-58.8 EndY=94 EndZ=0
    g2: LineSegment StartX=-58.8 StartY=94 StartZ=0 EndX=-66 EndY=94 EndZ=0
    g3: LineSegment StartX=-66 StartY=94 StartZ=0 EndX=-66 EndY=101.2 EndZ=0
  constraints (11):
    c: Coincident(g0,g1)
    c: Coincident(g1,g2)
    c: Coincident(g2,g3)
    c: Coincident(g3,g0)
    c: Horizontal(g0)
    c: Horizontal(g2)
    c: Vertical(g1)
    c: Vertical(g3)
    c: Coincident(g0,g-4)
    c: DistanceY(g1,g1) = 7.2
    c: Equal(g1,g2)
FEATURE [PartDesign::Pad] Pad009  label="ColumnPart"
  AddSubType = 0
  AlongSketchNormal = false
  BaseFeature = -> Pad008
  CheckUpToFaceLimits = true
  ClaimChildren = false
  Direction = (0,0,1)
  Fit = 0
  FitJoin = 0
  InnerFit = 0
  InnerFitJoin = 0
  InnerTaperAngle = 0
  InnerTaperAngleRev = 0
  Length = 10
  Length2 = 100
  Linearize = true
  NewSolid = false
  Profile = -> Sketch010
  Suppress = false
  TreeRank = 22
  Type = 3
  UpToFace = -> Pad008 [Face31]
  _ProfileBasedVersion = 1
FEATURE [Sketcher::SketchObject] Sketch011
  ExternalGeometry = -> [Pad009]
  FullyConstrained = true
  MapMode = 5
  Placement = pos=(0,0,56) rot=(0,0,1;0rad)
  Support = -> [Pad009]
  TreeRank = 23
  sketch-geometry (3):
    g0: LineSegment [constr] StartX=-58.8 StartY=97.6 StartZ=0 EndX=-62.4 EndY=97.6 EndZ=0
    g1: LineSegment [constr] StartX=-62.4 StartY=97.6 StartZ=0 EndX=-62.4 EndY=94 EndZ=0
    g2: Circle CenterX=-62.4 CenterY=97.6 CenterZ=0 NormalX=0 NormalY=0 NormalZ=1 AngleXU=0 Radius=2
  constraints (7):
    c: Horizontal(g0)
    c: Coincident(g1,g0)
    c: Vertical(g1)
    c: Symmetric(g-3,g-4,g0)
    c: Symmetric(g-4,g-4,g1)
    c: Coincident(g2,g0)
    c: Diameter(g2) = 4
FEATURE [PartDesign::Pocket] Pocket  label="ColumnPartHole"
  AddSubType = 1
  BaseFeature = -> Pad009
  CheckUpToFaceLimits = true
  ClaimChildren = false
  Fit = 0
  FitJoin = 0
  InnerFit = 0
  InnerFitJoin = 0
  InnerTaperAngle = 0
  InnerTaperAngleRev = 0
  Length = 6.7
  Length2 = 100
  Linearize = true
  NewSolid = false
  Profile = -> Sketch011
  Suppress = false
  TreeRank = 24
  Type = 0
  _ProfileBasedVersion = 1
  _Version = 1
FEATURE [PartDesign::Fillet] Fillet
  AddSubType = 0
  Base = -> Pocket [Edge46,Edge47]
  BaseFeature = -> Pocket
  NewSolid = false
  Radius = 2
  SupportTransform = false
  Suppress = false
  TreeRank = 25
FEATURE [PartDesign::Body] Body
  AutoGroupSolids = false
  ClaimAllChildren = false
  ExportMode = 0
  Group = -> [LCS_0,Sketch_1,Pad,Sketch,Pad001,Sketch001,Pad002,Sketch002,Pad003,Sketch005,Pad005,Sketch006,Pad006,Sketch007,Pocket001,Sketch008,Pad007,Sketch009,Pad008,Sketch010,Pad009,Sketch011,Pocket,Fillet]
  Origin = -> Origin001
  Tip = -> Fillet
  TreeRank = 0
  _ExportChildren = -> [LCS_0,Pad,Pad001,Pad002,Pad003,Pad005,Pad006,Pocket001,Pad007,Pad008,Pad009,Pocket,Fillet]
  _GroupVersion = 1
FEATURE [App::Part] Part  label="SecondPartProcessor"
  ClaimAllChildren = false
  ExportMode = 1
  Group = -> [Body]
  Origin = -> Origin
  TreeRank = 0
  _ExportChildren = -> [Body]
  _GroupVersion = 1
---- part SecondPartProcessorTop.FCStd = doc fcstd_42097c5507ef ----
FCSTD DOCUMENT  (FreeCAD 2022.1112R26244 +5306 (Git))
Label: SecondPartProcessorTop
License: All rights reserved
LicenseURL: http://en.wikipedia.org/wiki/All_rights_reserved
objects: Sketcher::SketchObject×14, PartDesign::Pad×12, PartDesign::Chamfer×4, PartDesign::Pocket×3, PartDesign::CoordinateSystem×1, PartDesign::Body×1, App::Part×1
note: 87 computed .brp shape members not serialized (recipe doc carries the construction recipe); baked Part::Feature solids carry a one-line shape summary decoded from their .brp

FEATURE [PartDesign::CoordinateSystem] LCS_0
  AttacherType = Attacher::AttachEngine3D
  AttachmentSupport = -> [X_Axis001]
  MapMode = 2
  Support = -> [X_Axis001]
  TreeRank = 0
FEATURE [Sketcher::SketchObject] Sketch_1
  ArcFitTolerance = 0
  ExternalBSplineMaxDegree = 0
  ExternalBSplineTolerance = 0
  FullyConstrained = true
  InternalTolerance = 1e-06
  MakeInternals = false
  TreeRank = 0
  sketch-geometry (4):
    g0: LineSegment StartX=0 StartY=0 StartZ=0 EndX=-40 EndY=0 EndZ=0
    g1: LineSegment StartX=-40 StartY=0 StartZ=0 EndX=-40 EndY=93 EndZ=0
    g2: LineSegment StartX=-40 StartY=93 StartZ=0 EndX=0 EndY=93 EndZ=0
    g3: LineSegment StartX=0 StartY=93 StartZ=0 EndX=0 EndY=0 EndZ=0
  constraints (11):
    c: Coincident(g0,g1)
    c: Coincident(g1,g2)
    c: Coincident(g2,g3)
    c: Coincident(g3,g0)
    c: Horizontal(g0)
    c: Horizontal(g2)
    c: Vertical(g1)
    c: Vertical(g3)
    c: Coincident(g0,g-1)
    c: DistanceY(g3,g3) = 93
    c: DistanceX(g2,g2) = 40
FEATURE [PartDesign::Pad] Pad  label="MainSupport"
  AddSubType = 0
  AutoTaperInnerAngle = false
  CheckUpToFaceLimits = true
  ClaimChildren = false
  Direction = (0,0,1)
  Fit = 0
  FitJoin = 0
  InnerFit = 0
  InnerFitJoin = 0
  Length = 5
  Length2 = 100
  NewSolid = false
  Profile = -> Sketch_1
  Suppress = false
  TaperInnerAngle = 0
  TaperInnerAngleRev = 0
  TreeRank = 0
  Type = 0
  _ProfileBasedVersion = 0
FEATURE [Sketcher::SketchObject] Sketch
  ArcFitTolerance = 0
  AttachmentSupport = -> [XY_Plane001]
  ExternalBSplineMaxDegree = 0
  ExternalBSplineTolerance = 0
  ExternalGeometry = -> [Pad]
  FullyConstrained = true
  InternalTolerance = 1e-06
  MakeInternals = false
  MapMode = 5
  Support = -> [XY_Plane001]
  TreeRank = 1
  sketch-geometry (4):
    g0: LineSegment StartX=0 StartY=0 StartZ=0 EndX=-40 EndY=0 EndZ=0
    g1: LineSegment StartX=-40 StartY=0 StartZ=0 EndX=-40 EndY=-7.4 EndZ=0
    g2: LineSegment StartX=0 StartY=-7.4 StartZ=0 EndX=0 EndY=0 EndZ=0
    g3: LineSegment StartX=-40 StartY=-7.4 StartZ=0 EndX=0 EndY=-7.4 EndZ=0
  constraints (11):
    c: Coincident(g2,g0)
    c: Vertical(g1)
    c: Vertical(g2)
    c: Coincident(g0,g-1)
    c: DistanceY(g2,g2) = 7.4
    c: Horizontal(g0)
    c: Coincident(g1,g0)
    c: Coincident(g3,g1)
    c: Horizontal(g3)
    c: DistanceX(g0,g0) = 40
    c: Coincident(g3,g2)
FEATURE [PartDesign::Pad] Pad011  label="ExtraSideSize"
  AddSubType = 0
  AlongSketchNormal = false
  AutoTaperInnerAngle = false
  BaseFeature = -> Pad
  CheckUpToFaceLimits = true
  ClaimChildren = false
  Direction = (0,1,0)
  Fit = 0
  FitJoin = 0
  InnerFit = 0
  InnerFitJoin = 0
  Length = 10.2
  Length2 = 100
  Linearize = true
  NewSolid = false
  Profile = -> Pad [Face3]
  Suppress = false
  TaperInnerAngle = 0
  TaperInnerAngleRev = 0
  TreeRank = 27
  Type = 0
  _ProfileBasedVersion = 1
FEATURE [PartDesign::Pad] Pad001  label="ExtraPeripheralsSize"
  AddSubType = 0
  AlongSketchNormal = false
  AutoTaperInnerAngle = false
  BaseFeature = -> Pad011
  CheckUpToFaceLimits = true
  ClaimChildren = false
  Direction = (0,0,1)
  Fit = 0
  FitJoin = 0
  InnerFit = 0
  InnerFitJoin = 0
  Length = 5
  Length2 = 100
  Linearize = true
  NewSolid = false
  Profile = -> Sketch
  Suppress = false
  TaperInnerAngle = 0
  TaperInnerAngleRev = 0
  TreeRank = 2
  Type = 0
  _ProfileBasedVersion = 1
FEATURE [Sketcher::SketchObject] Sketch001
  ArcFitTolerance = 0
  AttachmentSupport = -> [Pad001]
  ExternalBSplineMaxDegree = 0
  ExternalBSplineTolerance = 0
  ExternalGeometry = -> [Pad001]
  FullyConstrained = true
  InternalTolerance = 1e-06
  MakeInternals = false
  MapMode = 5
  Placement = pos=(0,-7.4,0) rot=(1,0,0;1.5708rad)
  Support = -> [Pad001]
  TreeRank = 3
  sketch-geometry (7):
    g0: LineSegment StartX=-40 StartY=5 StartZ=0 EndX=-68 EndY=-23 EndZ=0
    g1: LineSegment StartX=-68 StartY=-23 StartZ=0 EndX=-68 EndY=-28 EndZ=0
    g2: LineSegment StartX=-40 StartY=5 StartZ=0 EndX=-40 EndY=0 EndZ=0
    g3: LineSegment StartX=-68 StartY=-28 StartZ=0 EndX=-66 EndY=-28 EndZ=0
    g4: LineSegment StartX=-66 StartY=-28 StartZ=0 EndX=-66 EndY=-26 EndZ=0
    g5: LineSegment StartX=-40 StartY=0 StartZ=0 EndX=-66 EndY=-26 EndZ=0
    g6: LineSegment [constr] StartX=-66 StartY=-26 StartZ=0 EndX=-68 EndY=-28 EndZ=0
  constraints (19):
    c: Coincident(g0,g-3)
    c: Coincident(g5,g-3)
    c: Coincident(g1,g0)
    c: Vertical(g1)
    c: DistanceX(g0,g0) = 28
    c: Angle(g0,g-3) = 0.785398
    c: Coincident(g2,g0)
    c: Coincident(g2,g5)
    c: Equal(g2,g1)
    c: DistanceY(g1,g5) = 28
    c: Horizontal(g3)
    c: Coincident(g4,g3)
    c: Vertical(g4)
    c: Coincident(g5,g4)
    c: Coincident(g3,g1)
    c: Coincident(g6,g4)
    c: Coincident(g6,g1)
    c: Parallel(g6,g5)
    c: DistanceX(g3,g3) = 2
FEATURE [PartDesign::Pad] Pad002  label="Slope"
  AddSubType = 0
  AlongSketchNormal = false
  AutoTaperInnerAngle = false
  BaseFeature = -> Pad001
  CheckUpToFaceLimits = true
  ClaimChildren = false
  Direction = (0,-1,2e-16)
  Fit = 0
  FitJoin = 0
  InnerFit = 0
  InnerFitJoin = 0
  Length = 10
  Length2 = 100
  Linearize = true
  NewSolid = false
  Profile = -> Sketch001
  Reversed = true
  Suppress = false
  TaperInnerAngle = 0
  TaperInnerAngleRev = 0
  TreeRank = 4
  Type = 3
  UpToFace = -> Pad001 [Face8]
  _ProfileBasedVersion = 1
FEATURE [Sketcher::SketchObject] Sketch005
  ArcFitTolerance = 0
  AttachmentSupport = -> [Pad002]
  ExternalBSplineMaxDegree = 0
  ExternalBSplineTolerance = 0
  ExternalGeometry = -> [Pad002]
  FullyConstrained = true
  InternalTolerance = 1e-06
  MakeInternals = false
  MapMode = 5
  Placement = pos=(0,0,5) rot=(0,0,1;0rad)
  Support = -> [Pad002]
  TreeRank = 11
  sketch-geometry (4):
    g0: LineSegment StartX=-68 StartY=103.2 StartZ=0 EndX=-58.8 EndY=103.2 EndZ=0
    g1: LineSegment StartX=-58.8 StartY=103.2 StartZ=0 EndX=-58.8 EndY=94 EndZ=0
    g2: LineSegment StartX=-58.8 StartY=94 StartZ=0 EndX=-68 EndY=94 EndZ=0
    g3: LineSegment StartX=-68 StartY=94 StartZ=0 EndX=-68 EndY=103.2 EndZ=0
  constraints (11):
    c: Coincident(g0,g1)
    c: Coincident(g1,g2)
    c: Coincident(g2,g3)
    c: Coincident(g3,g0)
    c: Horizontal(g0)
    c: Horizontal(g2)
    c: Vertical(g1)
    c: Vertical(g3)
    c: Coincident(g0,g-3)
    c: Equal(g1,g2)
    c: DistanceY(g1,g1) = 9.2
FEATURE [PartDesign::Pocket] Pocket  label="ColumnPartHole"
  AddSubType = 1
  AutoTaperInnerAngle = false
  BaseFeature = -> Pad002
  CheckUpToFaceLimits = true
  ClaimChildren = false
  Fit = 0
  FitJoin = 0
  InnerFit = 0
  InnerFitJoin = 0
  Length = 5
  Length2 = 100
  Linearize = true
  NewSolid = false
  Profile = -> Sketch005
  Suppress = false
  TaperInnerAngle = 0
  TaperInnerAngleRev = 0
  TreeRank = 12
  Type = 1
  _ProfileBasedVersion = 1
  _Version = 1
FEATURE [Sketcher::SketchObject] Sketch006
  ArcFitTolerance = 0
  ExternalBSplineMaxDegree = 0
  ExternalBSplineTolerance = 0
  ExternalGeometry = -> [Pocket]
  FullyConstrained = true
  InternalTolerance = 1e-06
  MakeInternals = false
  MapMode = 5
  Placement = pos=(0,-6.2e-15,-28) rot=(1,0,0;3.14159rad)
  TreeRank = 13
  sketch-geometry (4):
    g0: LineSegment StartX=-68 StartY=-94 StartZ=0 EndX=-66 EndY=-94 EndZ=0
    g1: LineSegment StartX=-66 StartY=-94 StartZ=0 EndX=-66 EndY=7.4 EndZ=0
    g2: LineSegment StartX=-66 StartY=7.4 StartZ=0 EndX=-68 EndY=7.4 EndZ=0
    g3: LineSegment StartX=-68 StartY=7.4 StartZ=0 EndX=-68 EndY=-94 EndZ=0
  constraints (10):
    c: Coincident(g0,g1)
    c: Coincident(g1,g2)
    c: Coincident(g2,g3)
    c: Coincident(g3,g0)
    c: Horizontal(g0)
    c: Horizontal(g2)
    c: Vertical(g1)
    c: Vertical(g3)
    c: Coincident(g0,g-4)
    c: Coincident(g1,g-3)
FEATURE [PartDesign::Pad] Pad006  label="SlopeSidePanel"
  AddSubType = 0
  AlongSketchNormal = false
  AutoTaperInnerAngle = false
  BaseFeature = -> Pocket
  CheckUpToFaceLimits = true
  ClaimChildren = false
  Direction = (0,-2e-16,-1)
  Fit = 0
  FitJoin = 0
  InnerFit = 0
  InnerFitJoin = 0
  Length = 23
  Length2 = 100
  Linearize = true
  NewSolid = false
  Profile = -> Sketch006
  Suppress = false
  TaperInnerAngle = 0
  TaperInnerAngleRev = 0
  TreeRank = 14
  Type = 0
  _ProfileBasedVersion = 1
FEATURE [Sketcher::SketchObject] Sketch011
  ArcFitTolerance = 0
  ExternalBSplineMaxDegree = 0
  ExternalBSplineTolerance = 0
  ExternalGeometry = -> [Pad006]
  FullyConstrained = true
  InternalTolerance = 1e-06
  MakeInternals = false
  MapMode = 5
  Placement = pos=(0,0,0) rot=(0.57735,0.57735,0.57735;2.0944rad)
  TreeRank = 23
  sketch-geometry (4):
    g0: LineSegment StartX=13.8 StartY=3.34 StartZ=0 EndX=101 EndY=3.34 EndZ=0
    g1: LineSegment StartX=101 StartY=3.34 StartZ=0 EndX=101 EndY=1.94 EndZ=0
    g2: LineSegment StartX=101 StartY=1.94 StartZ=0 EndX=13.8 EndY=1.94 EndZ=0
    g3: LineSegment StartX=13.8 StartY=1.94 StartZ=0 EndX=13.8 EndY=3.34 EndZ=0
  constraints (12):
    c: Coincident(g0,g1)
    c: Coincident(g1,g2)
    c: Coincident(g2,g3)
    c: Coincident(g3,g0)
    c: Horizontal(g0)
    c: Horizontal(g2)
    c: Vertical(g1)
    c: Vertical(g3)
    c: DistanceY(g-3,g2) = 1.94
    c: DistanceX(g-3,g0) = 21.2
    c: DistanceY(g3,g3) = 1.4
    c: DistanceX(g0,g-4) = 2.2
FEATURE [PartDesign::Pad] Pad010  label="Puzzle1"
  AddSubType = 0
  AlongSketchNormal = false
  AutoTaperInnerAngle = false
  BaseFeature = -> Pad006
  CheckUpToFaceLimits = true
  ClaimChildren = false
  Direction = (1,0,0)
  Fit = 0
  FitJoin = 0
  InnerFit = 0
  InnerFitJoin = 0
  Length = 10
  Length2 = 100
  Linearize = true
  NewSolid = false
  Profile = -> Sketch011
  Suppress = false
  TaperInnerAngle = 0
  TaperInnerAngleRev = 0
  TreeRank = 24
  Type = 0
  _ProfileBasedVersion = 1
FEATURE [Sketcher::SketchObject] Sketch013
  ArcFitTolerance = 0
  AttachmentSupport = -> [Pad006]
  ExternalBSplineMaxDegree = 0
  ExternalBSplineTolerance = 0
  ExternalGeometry = -> [Pad006]
  FullyConstrained = true
  InternalTolerance = 1e-06
  MakeInternals = false
  MapMode = 5
  Placement = pos=(0,103.2,0) rot=(0,0.707107,0.707107;3.14159rad)
  Support = -> [Pad006]
  TreeRank = 28
  sketch-geometry (6):
    g0: LineSegment StartX=0 StartY=0 StartZ=0 EndX=40 EndY=0 EndZ=0
    g1: LineSegment StartX=40 StartY=0 StartZ=0 EndX=58.8 EndY=-18.8 EndZ=0
    g2: LineSegment StartX=58.8 StartY=-51 StartZ=0 EndX=0 EndY=-51 EndZ=0
    g3: LineSegment StartX=0 StartY=-51 StartZ=0 EndX=0 EndY=0 EndZ=0
    g4: LineSegment StartX=58.8 StartY=-18.8 StartZ=0 EndX=58.8 EndY=-51 EndZ=0
    g5: LineSegment [constr] StartX=66 StartY=-51 StartZ=0 EndX=58.8 EndY=-51 EndZ=0
  constraints (14):
    c: Coincident(g0,g-1)
    c: Coincident(g0,g-3)
    c: Coincident(g1,g0)
    c: Horizontal(g2)
    c: Coincident(g3,g2)
    c: Coincident(g3,g0)
    c: Vertical(g3)
    c: Coincident(g1,g-5)
    c: Coincident(g4,g1)
    c: Coincident(g4,g2)
    c: Vertical(g4)
    c: Coincident(g5,g-4)
    c: Coincident(g5,g2)
    c: Horizontal(g5)
FEATURE [PartDesign::Pad] Pad012  label="endPanel"
  AddSubType = 0
  AlongSketchNormal = false
  AutoTaperInnerAngle = false
  BaseFeature = -> Pad010
  CheckUpToFaceLimits = true
  ClaimChildren = false
  Direction = (0,1,-2e-16)
  Fit = 0
  FitJoin = 0
  InnerFit = 0
  InnerFitJoin = 0
  Length = 2
  Length2 = 100
  Linearize = true
  NewSolid = false
  Profile = -> Sketch013
  Reversed = true
  Suppress = false
  TaperInnerAngle = 0
  TaperInnerAngleRev = 0
  TreeRank = 29
  Type = 0
  _ProfileBasedVersion = 1
FEATURE [Sketcher::SketchObject] Sketch014
  ArcFitTolerance = 0
  AttachmentSupport = -> [Pad012]
  ExternalBSplineMaxDegree = 0
  ExternalBSplineTolerance = 0
  ExternalGeometry = -> [Pad012]
  FullyConstrained = true
  InternalTolerance = 1e-06
  MakeInternals = false
  MapMode = 5
  Placement = pos=(3e-15,101.2,-2.93e-14) rot=(1,0,0;1.5708rad)
  Support = -> [Pad012]
  TreeRank = 30
  sketch-geometry (7):
    g0: LineSegment StartX=-58.8 StartY=-51 StartZ=0 EndX=-58.8 EndY=-18.8 EndZ=0
    g1: LineSegment StartX=-58.8 StartY=-18.8 StartZ=0 EndX=-56.8 EndY=-16.8 EndZ=0
    g2: LineSegment StartX=-56.8 StartY=-16.8 StartZ=0 EndX=-56.8 EndY=-51 EndZ=0
    g3: LineSegment [constr] StartX=-56.8 StartY=-51 StartZ=0 EndX=-58.8 EndY=-51 EndZ=0
    g4: LineSegment StartX=-58.8 StartY=-51 StartZ=0 EndX=-58.8 EndY=-53 EndZ=0
    g5: LineSegment StartX=-58.8 StartY=-53 StartZ=0 EndX=-56.8 EndY=-53 EndZ=0
    g6: LineSegment StartX=-56.8 StartY=-53 StartZ=0 EndX=-56.8 EndY=-51 EndZ=0
  constraints (18):
    c: Coincident(g0,g-3)
    c: Coincident(g0,g-3)
    c: Coincident(g1,g0)
    c: PointOnObject(g1,g-4)
    c: Coincident(g2,g1)
    c: Vertical(g2)
    c: Coincident(g3,g2)
    c: Coincident(g3,g0)
    c: Horizontal(g3)
    c: DistanceX(g3,g3) = 2
    c: Coincident(g4,g0)
    c: Vertical(g4)
    c: Coincident(g5,g4)
    c: Horizontal(g5)
    c: Coincident(g6,g5)
    c: Coincident(g6,g2)
    c: Vertical(g6)
    c: DistanceY(g6,g6) = 2
FEATURE [PartDesign::Pad] Pad013  label="ColumnPanel1"
  AddSubType = 0
  AlongSketchNormal = false
  AutoTaperInnerAngle = false
  BaseFeature = -> Pad012
  CheckUpToFaceLimits = true
  ClaimChildren = false
  Direction = (0,-1,2e-16)
  Fit = 0
  FitJoin = 0
  InnerFit = 0
  InnerFitJoin = 0
  Length = 7.2
  Length2 = 100
  Linearize = true
  NewSolid = false
  Profile = -> Sketch014
  Suppress = false
  TaperInnerAngle = 0
  TaperInnerAngleRev = 0
  TreeRank = 31
  Type = 0
  _ProfileBasedVersion = 1
FEATURE [Sketcher::SketchObject] Sketch015
  ArcFitTolerance = 0
  AttachmentSupport = -> [Pad013]
  ExternalBSplineMaxDegree = 0
  ExternalBSplineTolerance = 0
  ExternalGeometry = -> [Pad013]
  FullyConstrained = true
  InternalTolerance = 1e-06
  MakeInternals = false
  MapMode = 5
  Placement = pos=(1.88e-14,94,-3.95e-14) rot=(1,0,0;1.5708rad)
  Support = -> [Pad013]
  TreeRank = 32
  sketch-geometry (4):
    g0: LineSegment StartX=-56.8 StartY=-53 StartZ=0 EndX=-66 EndY=-53 EndZ=0
    g1: LineSegment StartX=-66 StartY=-53 StartZ=0 EndX=-66 EndY=-26 EndZ=0
    g2: LineSegment StartX=-56.8 StartY=-53 StartZ=0 EndX=-56.8 EndY=-16.8 EndZ=0
    g3: LineSegment StartX=-56.8 StartY=-16.8 StartZ=0 EndX=-66 EndY=-26 EndZ=0
  constraints (10):
    c: Horizontal(g0)
    c: Coincident(g1,g0)
    c: Coincident(g1,g-4)
    c: Vertical(g1)
    c: PointOnObject(g2,g-4)
    c: Vertical(g2)
    c: Coincident(g3,g2)
    c: Coincident(g3,g1)
    c: Coincident(g0,g-3)
    c: Coincident(g2,g0)
FEATURE [PartDesign::Pad] Pad014  label="ColumnPanel2"
  AddSubType = 0
  AlongSketchNormal = false
  AutoTaperInnerAngle = false
  BaseFeature = -> Pad013
  CheckUpToFaceLimits = true
  ClaimChildren = false
  Direction = (-2e-16,-1,4e-16)
  Fit = 0
  FitJoin = 0
  InnerFit = 0
  InnerFitJoin = 0
  Length = 2
  Length2 = 100
  Linearize = true
  NewSolid = false
  Profile = -> Sketch015
  Suppress = false
  TaperInnerAngle = 0
  TaperInnerAngleRev = 0
  TreeRank = 33
  Type = 0
  _ProfileBasedVersion = 1
FEATURE [Sketcher::SketchObject] Sketch016
  ArcFitTolerance = 0
  AttachmentSupport = -> [Pad014]
  ExternalBSplineMaxDegree = 0
  ExternalBSplineTolerance = 0
  ExternalGeometry = -> [Pad014]
  FullyConstrained = true
  InternalTolerance = 1e-06
  MakeInternals = false
  MapMode = 5
  Placement = pos=(-58.8,1.8e-15,0) rot=(-0.57735,0.57735,0.57735;4.18879rad)
  Support = -> [Pad014]
  TreeRank = 34
  sketch-geometry (4):
    g0: LineSegment StartX=-103.2 StartY=-51 StartZ=0 EndX=-94 EndY=-51 EndZ=0
    g1: LineSegment StartX=-94 StartY=-51 StartZ=0 EndX=-94 EndY=-46 EndZ=0
    g2: LineSegment StartX=-94 StartY=-46 StartZ=0 EndX=-103.2 EndY=-46 EndZ=0
    g3: LineSegment StartX=-103.2 StartY=-46 StartZ=0 EndX=-103.2 EndY=-51 EndZ=0
  constraints (11):
    c: Coincident(g0,g1)
    c: Coincident(g1,g2)
    c: Coincident(g2,g3)
    c: Coincident(g3,g0)
    c: Horizontal(g0)
    c: Horizontal(g2)
    c: Vertical(g1)
    c: Vertical(g3)
    c: Coincident(g0,g-3)
    c: PointOnObject(g1,g-4)
    c: DistanceY(g3,g3) = 5
FEATURE [PartDesign::Pad] Pad015  label="HoleSupport"
  AddSubType = 0
  AlongSketchNormal = false
  AutoTaperInnerAngle = false
  BaseFeature = -> Pad014
  CheckUpToFaceLimits = true
  ClaimChildren = false
  Direction = (-1,0,0)
  Fit = 0
  FitJoin = 0
  InnerFit = 0
  InnerFitJoin = 0
  Length = 10
  Length2 = 100
  Linearize = true
  NewSolid = false
  Profile = -> Sketch016
  Suppress = false
  TaperInnerAngle = 0
  TaperInnerAngleRev = 0
  TreeRank = 35
  Type = 3
  UpToFace = -> Pad014 [Face37]
  _ProfileBasedVersion = 1
FEATURE [Sketcher::SketchObject] Sketch017
  ArcFitTolerance = 0
  AttachmentSupport = -> [Pad015]
  ExternalBSplineMaxDegree = 0
  ExternalBSplineTolerance = 0
  ExternalGeometry = -> [Pad015]
  FullyConstrained = true
  InternalTolerance = 1e-06
  MakeInternals = false
  MapMode = 5
  Placement = pos=(0,0,-46) rot=(0,0,1;0rad)
  Support = -> [Pad015]
  TreeRank = 36
  sketch-geometry (3):
    g0: LineSegment [constr] StartX=-62.4 StartY=94 StartZ=0 EndX=-62.4 EndY=97.6 EndZ=0
    g1: LineSegment [constr] StartX=-62.4 StartY=97.6 StartZ=0 EndX=-58.8 EndY=97.6 EndZ=0
    g2: Circle CenterX=-62.4 CenterY=97.6 CenterZ=0 NormalX=0 NormalY=0 NormalZ=1 AngleXU=0 Radius=1.6
  constraints (9):
    c: PointOnObject(g0,g-4)
    c: Vertical(g0)
    c: Coincident(g1,g0)
    c: PointOnObject(g1,g-3)
    c: Horizontal(g1)
    c: DistanceY(g-4,g1) = 3.6
    c: DistanceX(g0,g-4) = 3.6
    c: Coincident(g2,g0)
    c: Diameter(g2) = 3.2
FEATURE [PartDesign::Pocket] Pocket001  label="Hole"
  AddSubType = 1
  AutoTaperInnerAngle = false
  BaseFeature = -> Pad015
  CheckUpToFaceLimits = true
  ClaimChildren = false
  Fit = 0
  FitJoin = 0
  InnerFit = 0
  InnerFitJoin = 0
  Length = 5
  Length2 = 100
  Linearize = true
  NewSolid = false
  Profile = -> Sketch017
  Suppress = false
  TaperInnerAngle = 0
  TaperInnerAngleRev = 0
  TreeRank = 37
  Type = 0
  _ProfileBasedVersion = 1
  _Version = 1
FEATURE [Sketcher::SketchObject] Sketch018
  ArcFitTolerance = 0
  AttachmentSupport = -> [Pocket001]
  ExternalBSplineMaxDegree = 0
  ExternalBSplineTolerance = 0
  ExternalGeometry = -> [Pocket001]
  FullyConstrained = true
  InternalTolerance = 1e-06
  MakeInternals = false
  MapMode = 5
  Placement = pos=(0,-7.4,0) rot=(1,0,0;1.5708rad)
  Support = -> [Pocket001]
  TreeRank = 38
  sketch-geometry (4):
    g0: LineSegment StartX=-28.8 StartY=3.34 StartZ=0 EndX=-11.2 EndY=3.34 EndZ=0
    g1: LineSegment StartX=-11.2 StartY=3.34 StartZ=0 EndX=-11.2 EndY=1.94 EndZ=0
    g2: LineSegment StartX=-11.2 StartY=1.94 StartZ=0 EndX=-28.8 EndY=1.94 EndZ=0
    g3: LineSegment StartX=-28.8 StartY=1.94 StartZ=0 EndX=-28.8 EndY=3.34 EndZ=0
  constraints (12):
    c: Coincident(g0,g1)
    c: Coincident(g1,g2)
    c: Coincident(g2,g3)
    c: Coincident(g3,g0)
    c: Horizontal(g0)
    c: Horizontal(g2)
    c: Vertical(g1)
    c: Vertical(g3)
    c: DistanceX(g-3,g0) = 11.2
    c: DistanceX(g0,g-4) = 11.2
    c: DistanceY(g3,g3) = 1.4
    c: DistanceY(g-3,g2) = 1.94
FEATURE [PartDesign::Pad] Pad016  label="Puzzle002"
  AddSubType = 0
  AlongSketchNormal = false
  AutoTaperInnerAngle = false
  BaseFeature = -> Pocket001
  CheckUpToFaceLimits = true
  ClaimChildren = false
  Direction = (0,-1,2e-16)
  Fit = 0
  FitJoin = 0
  InnerFit = 0
  InnerFitJoin = 0
  Length = 10
  Length2 = 100
  Linearize = true
  NewSolid = false
  Profile = -> Sketch018
  Suppress = false
  TaperInnerAngle = 0
  TaperInnerAngleRev = 0
  TreeRank = 39
  Type = 0
  _ProfileBasedVersion = 1
FEATURE [Sketcher::SketchObject] Sketch019
  ArcFitTolerance = 0
  AttachmentSupport = -> [Pad016]
  ExternalBSplineMaxDegree = 0
  ExternalBSplineTolerance = 0
  ExternalGeometry = -> [Pad016]
  FullyConstrained = true
  InternalTolerance = 1e-06
  MakeInternals = false
  MapMode = 5
  Placement = pos=(3.1e-15,103.2,-2.99e-14) rot=(0,0.707107,0.707107;3.14159rad)
  Support = -> [Pad016]
  TreeRank = 40
  sketch-geometry (30):
    g0: LineSegment [constr] StartX=8 StartY=-11 StartZ=0 EndX=40 EndY=-11 EndZ=0
    g1: LineSegment [constr] StartX=40 StartY=-11 StartZ=0 EndX=40 EndY=-43 EndZ=0
    g2: LineSegment [constr] StartX=40 StartY=-43 StartZ=0 EndX=8 EndY=-43 EndZ=0
    g3: LineSegment [constr] StartX=8 StartY=-43 StartZ=0 EndX=8 EndY=-11 EndZ=0
    g4: Circle CenterX=8 CenterY=-11 CenterZ=0 NormalX=0 NormalY=0 NormalZ=1 AngleXU=0 Radius=2
    g5: LineSegment [constr] StartX=4 StartY=-7 StartZ=0 EndX=44 EndY=-7 EndZ=0
    g6: LineSegment [constr] StartX=44 StartY=-7 StartZ=0 EndX=44 EndY=-47 EndZ=0
    g7: LineSegment [constr] StartX=44 StartY=-47 StartZ=0 EndX=4 EndY=-47 EndZ=0
    g8: LineSegment [constr] StartX=4 StartY=-47 StartZ=0 EndX=4 EndY=-7 EndZ=0
    g9: LineSegment [constr] StartX=4 StartY=-7 StartZ=0 EndX=8 EndY=-11 EndZ=0
    g10: LineSegment [constr] StartX=40 StartY=-43 StartZ=0 EndX=44 EndY=-47 EndZ=0
    g11: LineSegment [constr] StartX=40 StartY=-11 StartZ=0 EndX=44 EndY=-7 EndZ=0
    g12: LineSegment [constr] StartX=8 StartY=-43 StartZ=0 EndX=4 EndY=-47 EndZ=0
    g13: GeomPoint X=24 Y=-27 Z=0
    g14: LineSegment StartX=8 StartY=-25 StartZ=0 EndX=22 EndY=-25 EndZ=0
    g15: LineSegment StartX=22 StartY=-25 StartZ=0 EndX=22 EndY=-11 EndZ=0
    g16: LineSegment [constr] StartX=8 StartY=-11 StartZ=0 EndX=24 EndY=-27 EndZ=0
    g17: ArcOfCircle CenterX=22 CenterY=-25 CenterZ=0 NormalX=0 NormalY=0 NormalZ=1 AngleXU=0 Radius=14 StartAngle=1.5708 EndAngle=3.14159
    g18: Circle CenterX=8 CenterY=-43 CenterZ=0 NormalX=0 NormalY=0 NormalZ=1 AngleXU=0 Radius=2
    g19: Circle CenterX=40 CenterY=-43 CenterZ=0 NormalX=0 NormalY=0 NormalZ=1 AngleXU=0 Radius=2
    g20: Circle CenterX=40 CenterY=-11 CenterZ=0 NormalX=0 NormalY=0 NormalZ=1 AngleXU=0 Radius=2
    g21: LineSegment StartX=26 StartY=-25 StartZ=0 EndX=26 EndY=-11 EndZ=0
    g22: LineSegment StartX=26 StartY=-25 StartZ=0 EndX=40 EndY=-25 EndZ=0
    g23: LineSegment StartX=22 StartY=-29 StartZ=0 EndX=8 EndY=-29 EndZ=0
    g24: LineSegment StartX=22 StartY=-29 StartZ=0 EndX=22 EndY=-43 EndZ=0
    g25: LineSegment StartX=26 StartY=-29 StartZ=0 EndX=40 EndY=-29 EndZ=0
    g26: LineSegment StartX=26 StartY=-29 StartZ=0 EndX=26 EndY=-43 EndZ=0
    g27: ArcOfCircle CenterX=22 CenterY=-29 CenterZ=0 NormalX=0 NormalY=0 NormalZ=1 AngleXU=0 Radius=14 StartAngle=3.14159 EndAngle=4.71239
    g28: ArcOfCircle CenterX=26 CenterY=-29 CenterZ=0 NormalX=0 NormalY=0 NormalZ=1 AngleXU=0 Radius=14 StartAngle=4.71239 EndAngle=6.28319
    g29: ArcOfCircle CenterX=26 CenterY=-25 CenterZ=0 NormalX=0 NormalY=0 NormalZ=1 AngleXU=0 Radius=14 StartAngle=0 EndAngle=1.5708
  constraints (79):
    c: Coincident(g0,g1)
    c: Coincident(g1,g2)
    c: Coincident(g2,g3)
    c: Coincident(g3,g0)
    c: Horizontal(g0)
    c: Horizontal(g2)
    c: Vertical(g1)
    c: Vertical(g3)
    c: Equal(g0,g1)
    c: DistanceY(g1,g1) = 32
    c: Coincident(g4,g0)
    c: Diameter(g4) = 4
    c: Coincident(g5,g6)
    c: Coincident(g6,g7)
    c: Coincident(g7,g8)
    c: Coincident(g8,g5)
    c: Horizontal(g5)
    c: Horizontal(g7)
    c: Vertical(g6)
    c: Vertical(g8)
    c: Coincident(g9,g5)
    c: Coincident(g9,g4)
    c: Coincident(g10,g6)
    c: Equal(g10,g9)
    c: Coincident(g11,g5)
    c: Coincident(g12,g7)
    c: Equal(g12,g11)
    c: DistanceX(g5,g5) = 40
    c: DistanceY(g6,g6) = 40
    c: DistanceY(g5,g-3) = 7
    c: DistanceX(g-3,g5) = 4
    c: Horizontal(g14)
    c: Coincident(g15,g14)
    c: Vertical(g15)
    c: Coincident(g16,g4)
    c: Coincident(g16,g13)
    c: PointOnObject(g14,g16)
    c: Coincident(g17,g14)
    c: Coincident(g17,g14)
    c: Coincident(g17,g15)
    c: PointOnObject(g15,g0)
    c: DistanceX(g14,g13) = 2
    c: Coincident(g1,g10)
    c: Coincident(g11,g0)
    c: Coincident(g12,g2)
    c: Symmetric(g4,g1,g13)
    c: Coincident(g18,g2)
    c: Coincident(g19,g1)
    c: Coincident(g20,g0)
    c: PointOnObject(g21,g0)
    c: Vertical(g21)
    c: Coincident(g22,g21)
    c: Horizontal(g22)
    c: Horizontal(g23)
    c: Coincident(g24,g23)
    c: PointOnObject(g24,g2)
    c: Vertical(g24)
    c: Horizontal(g25)
    c: Coincident(g26,g25)
    c: PointOnObject(g26,g2)
    c: Vertical(g26)
    c: Coincident(g27,g23)
    c: Coincident(g27,g24)
    c: Coincident(g27,g23)
    c: Coincident(g28,g25)
    c: Coincident(g28,g26)
    c: Coincident(g28,g25)
    c: Coincident(g29,g21)
    c: Coincident(g29,g21)
    c: Coincident(g29,g22)
    c: Equal(g23,g14)
    c: Equal(g21,g15)
    c: Equal(g25,g14)
    c: PointOnObject(g23,g3)
    c: PointOnObject(g25,g1)
    c: PointOnObject(g22,g1)
    c: Equal(g4,g20)
    c: Equal(g20,g19)
    c: Equal(g19,g18)
FEATURE [PartDesign::Pocket] Pocket002  label="FanHole"
  AddSubType = 1
  AutoTaperInnerAngle = false
  BaseFeature = -> Pad016
  CheckUpToFaceLimits = true
  ClaimChildren = false
  Fit = 0
  FitJoin = 0
  InnerFit = 0
  InnerFitJoin = 0
  Length = 5
  Length2 = 100
  Linearize = true
  NewSolid = false
  Profile = -> Sketch019
  Suppress = false
  TaperInnerAngle = 0
  TaperInnerAngleRev = 0
  TreeRank = 41
  Type = 2
  _ProfileBasedVersion = 1
  _Version = 1
FEATURE [PartDesign::Chamfer] Chamfer
  AddSubType = 0
  Angle = 45
  Base = -> Pocket002 [Edge156,Edge149,Edge153,Edge145]
  BaseFeature = -> Pocket002
  ChamferType = 0
  FlipDirection = false
  NewSolid = false
  Size = 6
  Size2 = 1
  SupportTransform = false
  Suppress = false
  TreeRank = 42
FEATURE [PartDesign::Chamfer] Chamfer001
  AddSubType = 0
  Angle = 45
  Base = -> Chamfer [Edge123]
  BaseFeature = -> Chamfer
  ChamferType = 0
  FlipDirection = false
  NewSolid = false
  Size = 2
  Size2 = 1
  SupportTransform = false
  Suppress = false
  TreeRank = 43
FEATURE [Sketcher::SketchObject] Sketch020
  ArcFitTolerance = 0
  AttachmentSupport = -> [Chamfer001]
  ExternalBSplineMaxDegree = 0
  ExternalBSplineTolerance = 0
  ExternalGeometry = -> [Chamfer001]
  FullyConstrained = true
  InternalTolerance = 1e-06
  MakeInternals = false
  MapMode = 5
  Placement = pos=(0,-7.4,1.6e-15) rot=(1,0,0;1.5708rad)
  Support = -> [Chamfer001]
  TreeRank = 44
  sketch-geometry (4):
    g0: LineSegment StartX=-66 StartY=-51 StartZ=0 EndX=-66 EndY=-26 EndZ=0
    g1: LineSegment StartX=-66 StartY=-51 StartZ=0 EndX=-65 EndY=-51 EndZ=0
    g2: LineSegment StartX=-65 StartY=-51 StartZ=0 EndX=-65 EndY=-25 EndZ=0
    g3: LineSegment StartX=-65 StartY=-25 StartZ=0 EndX=-66 EndY=-26 EndZ=0
  constraints (10):
    c: Coincident(g0,g-4)
    c: Coincident(g0,g-3)
    c: Coincident(g1,g0)
    c: Horizontal(g1)
    c: Coincident(g2,g1)
    c: PointOnObject(g2,g-3)
    c: Vertical(g2)
    c: Coincident(g3,g2)
    c: Coincident(g3,g0)
    c: DistanceX(g1,g1) = 1
FEATURE [PartDesign::Pad] Pad017  label="PanelGuard"
  AddSubType = 0
  AlongSketchNormal = false
  AutoTaperInnerAngle = false
  BaseFeature = -> Chamfer001
  CheckUpToFaceLimits = true
  ClaimChildren = false
  Direction = (0,-1,2e-16)
  Fit = 0
  FitJoin = 0
  InnerFit = 0
  InnerFitJoin = 0
  Length = 1.5
  Length2 = 3
  Linearize = true
  NewSolid = false
  Profile = -> Sketch020
  Suppress = false
  TaperInnerAngle = 0
  TaperInnerAngleRev = 0
  TreeRank = 45
  Type = 4
  _ProfileBasedVersion = 1
FEATURE [PartDesign::Chamfer] Chamfer002
  AddSubType = 0
  Angle = 45
  Base = -> Pad017 [Edge167]
  BaseFeature = -> Pad017
  ChamferType = 0
  FlipDirection = false
  NewSolid = false
  Size = 0.99
  Size2 = 1
  SupportTransform = false
  Suppress = false
  TreeRank = 46
FEATURE [PartDesign::Chamfer] Chamfer003
  AddSubType = 0
  Angle = 45
  Base = -> Chamfer002 [Edge159,Edge151,Edge155,Edge139,Edge143,Edge118,Edge122,Edge147]
  BaseFeature = -> Chamfer002
  ChamferType = 0
  FlipDirection = false
  NewSolid = false
  Size = 1
  Size2 = 1
  SupportTransform = false
  Suppress = false
  TreeRank = 47
FEATURE [PartDesign::Body] Body
  AutoGroupSolids = false
  ClaimAllChildren = false
  ExportMode = 0
  Group = -> [LCS_0,Sketch_1,Pad,Sketch,Pad011,Pad001,Sketch001,Pad002,Pocket,Sketch005,Sketch006,Pad006,Sketch011,Sketch013,Pad010,Pad012,Sketch014,Pad013,Sketch015,Pad014,Sketch016,Pad015,Sketch017,Pocket001,Sketch018,Pad016,Sketch019,Pocket002,Chamfer,Chamfer001,Sketch020,Pad017,Chamfer002,Chamfer003]
  Origin = -> Origin001
  Tip = -> Chamfer003
  TreeRank = 0
  _ExportChildren = -> [LCS_0,Pad,Pad011,Pad001,Pad002,Pocket,Pad006,Pad010,Pad012,Pad013,Pad014,Pad015,Pocket001,Pad016,Pocket002,Chamfer,Chamfer001,Pad017,Chamfer002,Chamfer003]
  _GroupVersion = 1
FEATURE [App::Part] Part  label="SecondPartProcessorTop"
  ClaimAllChildren = false
  ExportMode = 1
  Group = -> [Body]
  Origin = -> Origin
  TreeRank = 0
  _ExportChildren = -> [Body]
  _GroupVersion = 1
